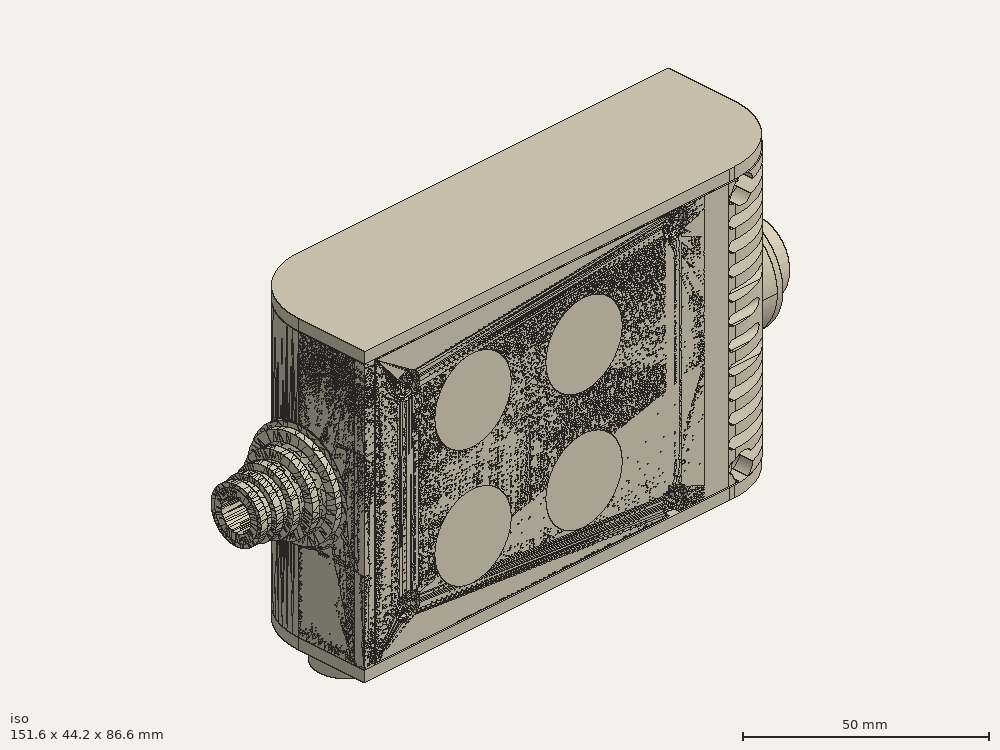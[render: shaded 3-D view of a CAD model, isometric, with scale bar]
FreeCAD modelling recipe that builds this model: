
FCSTD DOCUMENT  (FreeCAD 0.19R0.19.2)
Label: enclosure_205FCStd
License: All rights reserved
LicenseURL: http://en.wikipedia.org/wiki/All_rights_reserved
objects: Part::Revolution×152, Part::MultiFuse×146, Part::Feature×146, Sketcher::SketchObject×83, Part::Cut×70, Part::Cylinder×70, Part::Extrusion×68, Part::Fillet×58, Part::Box×36, App::MeasureDistance×4, Image::ImagePlane×1, PartDesign::Body×1, Part::FeaturePython×1
note: 831 computed .brp shape members not serialized (recipe doc carries the construction recipe); baked Part::Feature solids carry a one-line shape summary decoded from their .brp

FEATURE [Sketcher::SketchObject] Sketch  label="topSketch"
  FullyConstrained = true
  sketch-geometry (20):
    g0: LineSegment StartX=5.21097e-06 StartY=3 StartZ=0 EndX=5.21097e-06 EndY=19 EndZ=0
    g1: ArcOfCircle CenterX=19 CenterY=19 CenterZ=0 NormalX=0 NormalY=0 NormalZ=1 AngleXU=0 Radius=19 StartAngle=1.5708 EndAngle=3.14159
    g2: ArcOfCircle CenterX=19 CenterY=19 CenterZ=0 NormalX=0 NormalY=0 NormalZ=1 AngleXU=0 Radius=16 StartAngle=1.5708 EndAngle=3.14159
    g3: LineSegment StartX=114 StartY=35 StartZ=0 EndX=19 EndY=35 EndZ=0
    g4: LineSegment StartX=5.21097e-06 StartY=3 StartZ=0 EndX=5.21097e-06 EndY=0 EndZ=0
    g5: LineSegment StartX=3 StartY=0 StartZ=0 EndX=5.21097e-06 EndY=0 EndZ=0
    g6: LineSegment StartX=3 StartY=19 StartZ=0 EndX=3 EndY=0 EndZ=0
    g7: LineSegment StartX=19 StartY=38 StartZ=0 EndX=124 EndY=38 EndZ=0
    g8: Circle CenterX=119 CenterY=35 CenterZ=0 NormalX=0 NormalY=0 NormalZ=1 AngleXU=0 Radius=1
    g9: Circle CenterX=121 CenterY=35 CenterZ=0 NormalX=0 NormalY=0 NormalZ=1 AngleXU=0 Radius=1
    g10: Circle CenterX=121 CenterY=33 CenterZ=0 NormalX=0 NormalY=0 NormalZ=1 AngleXU=0 Radius=1
    g11: BSplineCurve PolesCount=3 KnotsCount=2 Degree=2 IsPeriodic=0
    g12: GeomPoint X=119 Y=35 Z=0
    g13: GeomPoint X=121 Y=33 Z=0
    g14: LineSegment StartX=119 StartY=35 StartZ=0 EndX=114 EndY=35 EndZ=0
    g15: ArcOfCircle CenterX=105 CenterY=19 CenterZ=0 NormalX=0 NormalY=0 NormalZ=1 AngleXU=0 Radius=19 StartAngle=5.7297 EndAngle=6.28319
    g16: ArcOfCircle CenterX=105 CenterY=19 CenterZ=0 NormalX=0 NormalY=0 NormalZ=1 AngleXU=0 Radius=16 StartAngle=5.60905 EndAngle=6.28319
    g17: LineSegment StartX=121 StartY=33 StartZ=0 EndX=121 EndY=19 EndZ=0
    g18: LineSegment StartX=124 StartY=38 StartZ=0 EndX=124 EndY=19 EndZ=0
    g19: LineSegment StartX=117.5 StartY=9.01251 StartZ=0 EndX=121.163 EndY=9.0125 EndZ=0
  constraints (46):
    c: Vertical(g0)
    c: Block(g0)
    c: Coincident(g1,g0)
    c: Block(g1)
    c: Coincident(g2,g1)
    c: Block(g2)
    c: Coincident(g3,g2)
    c: Horizontal(g3)
    c: Tangent(g3,g2)
    c: Coincident(g4,g0)
    c: Distance(g4) = 3
    c: Vertical(g4)
    c: Coincident(g5,g4)
    c: Horizontal(g5)
    c: Coincident(g6,g2)
    c: Coincident(g6,g5)
    c: Vertical(g6)
    c: Horizontal(g7)
    c: Distance(g7) = 105
    c: Coincident(g7,g1)
    c: Block(g3)
    c: Weight(g8) = 1
    c: Equal(g8,g9)
    c: Equal(g8,g10)
    c: InternalAlignment(g8,g11)
    c: InternalAlignment(g9,g11)
    c: InternalAlignment(g10,g11)
    c: InternalAlignment(g12,g11)
    c: InternalAlignment(g13,g11)
    c: Block(g11)
    c: Coincident(g14,g11)
    c: Coincident(g14,g3)
    c: Horizontal(g14)
    c: Block(g15)
    c: Coincident(g16,g15)
    c: Block(g16)
    c: Coincident(g17,g11)
    c: Coincident(g17,g16)
    c: Vertical(g17)
    c: Distance(g17) = 14
    c: Coincident(g18,g7)
    c: Coincident(g18,g15)
    c: Vertical(g18)
    c: Distance(g18) = 19
    c: Coincident(g19,g16)
    c: Coincident(g19,g15)
FEATURE [Sketcher::SketchObject] Sketch001  label="bottomSketch"
  FullyConstrained = true
  sketch-geometry (32):
    g0: LineSegment StartX=3.3 StartY=-6.03275e-07 StartZ=0 EndX=98 EndY=-6.03275e-07 EndZ=0
    g1: ArcOfCircle CenterX=98 CenterY=19 CenterZ=0 NormalX=0 NormalY=0 NormalZ=1 AngleXU=0 Radius=19 StartAngle=4.71239 EndAngle=5.71103
    g2: LineSegment StartX=6.3 StartY=8 StartZ=0 EndX=3.3 EndY=8 EndZ=0
    g3: LineSegment StartX=3.3 StartY=8 StartZ=0 EndX=3.3 EndY=-6.03275e-07 EndZ=0
    g4: ArcOfCircle CenterX=8.3 CenterY=5 CenterZ=0 NormalX=0 NormalY=0 NormalZ=1 AngleXU=0 Radius=2 StartAngle=3.14159 EndAngle=4.71239
    g5: LineSegment StartX=6.3 StartY=8 StartZ=0 EndX=6.3 EndY=5 EndZ=0
    g6: ArcOfCircle CenterX=98 CenterY=19 CenterZ=0 NormalX=0 NormalY=0 NormalZ=1 AngleXU=0 Radius=12.7 StartAngle=4.71239 EndAngle=6.28319
    g7: LineSegment StartX=94.7 StartY=3 StartZ=0 EndX=8.3 EndY=3 EndZ=0
    g8-g12: Circle x5 (B-spline internal-alignment scaffolding for g13; pole/knot coordinates omitted)
    g13: BSplineCurve PolesCount=5 KnotsCount=3 Degree=3 IsPeriodic=0
    g14: GeomPoint X=98 Y=6.3 Z=0
    g15: GeomPoint X=96.3938 Y=4.71946 Z=0
    g16: GeomPoint X=94.7 Y=3 Z=0
    g17-g23: Circle x7 (B-spline internal-alignment scaffolding for g24; pole/knot coordinates omitted)
    g24: BSplineCurve PolesCount=7 KnotsCount=5 Degree=3 IsPeriodic=0
    g25-g29: GeomPoint x5 (B-spline internal-alignment scaffolding for g24; pole/knot coordinates omitted)
    g30: ArcOfCircle CenterX=98 CenterY=19 CenterZ=0 NormalX=0 NormalY=0 NormalZ=1 AngleXU=0 Radius=15.7 StartAngle=5.81226 EndAngle=6.28319
    g31: LineSegment StartX=110.7 StartY=19 StartZ=0 EndX=113.7 EndY=19 EndZ=0
  constraints (41):
    c: Horizontal(g0)
    c: Coincident(g1,g0)
    c: Block(g1)
    c: Horizontal(g2)
    c: Distance(g2) = 3
    c: Coincident(g3,g2)
    c: Vertical(g3)
    c: Coincident(g3,g0)
    c: Block(g4)
    c: Block(g2)
    c: Coincident(g5,g2)
    c: Coincident(g5,g4)
    c: Vertical(g5)
    c: Coincident(g6,g1)
    c: Block(g6)
    c: Coincident(g7,g4)
    c: Horizontal(g7)
    c: Block(g0)
    c: Block(g7)
    c: Block(g3)
    c: Coincident(g13,g6)
    c: Weight(g8) = 1
    c: Equal(g8, g9-g12) x4
    c: Coincident(g13,g7)
    c: InternalAlignment(g8-g12 -> g13) x5
    c: InternalAlignment(g14,g13)
    c: InternalAlignment(g15,g13)
    c: InternalAlignment(g16,g13)
    c: Block(g13)
    c: Weight(g17) = 1
    c: Equal(g17, g18-g23) x6
    c: Coincident(g24,g1)
    c: InternalAlignment(g17-g23 -> g24) x7
    c: InternalAlignment(g25-g29 -> g24) x5
    c: Block(g24)
    c: Coincident(g30,g24)
    c: Coincident(g31,g6)
    c: Coincident(g31,g30)
    c: Horizontal(g31)
    c: Block(g31)
    c: Block(g30)
FEATURE [Part::Extrusion] Extrude  label="top"
  Base = -> Sketch
  Dir = (0,0,1)
  DirMode = 2
  FaceMakerClass = Part::FaceMakerBullseye
  LengthFwd = 72
  LengthRev = 0
  Solid = true
  Symmetric = false
FEATURE [Part::Extrusion] Extrude001  label="bottom"
  Base = -> Sketch001
  Dir = (0,0,1)
  DirMode = 2
  FaceMakerClass = Part::FaceMakerBullseye
  LengthFwd = 71.4
  LengthRev = 0
  Placement = pos=(0,0,0.3) rot=(0,0,1;0rad)
  Solid = true
  Symmetric = false
FEATURE [Sketcher::SketchObject] Sketch002  label="topSketch001"
  FullyConstrained = true
  sketch-geometry (8):
    g0: ArcOfCircle CenterX=19 CenterY=19.0975 CenterZ=0 NormalX=0 NormalY=0 NormalZ=1 AngleXU=0 Radius=18.9025 StartAngle=1.5708 EndAngle=3.14674
    g1: LineSegment StartX=0.0977805 StartY=19.0003 StartZ=0 EndX=0.0977805 EndY=0.000251602 EndZ=0
    g2: LineSegment StartX=19 StartY=38 StartZ=0 EndX=124 EndY=38 EndZ=0
    g3: LineSegment StartX=0.0977805 StartY=0.000251602 StartZ=0 EndX=105.098 EndY=0.000251602 EndZ=0
    g4: LineSegment StartX=124 StartY=38 StartZ=0 EndX=125.616 EndY=38 EndZ=0
    g5: LineSegment StartX=105.098 StartY=0.000251602 StartZ=0 EndX=106.713 EndY=0.000251602 EndZ=0
    g6: ArcOfCircle CenterX=106.616 CenterY=19 CenterZ=0 NormalX=0 NormalY=0 NormalZ=1 AngleXU=0 Radius=19 StartAngle=4.71754 EndAngle=6.28319
    g7: LineSegment StartX=125.616 StartY=38 StartZ=0 EndX=125.616 EndY=19 EndZ=0
  constraints (21):
    c: Block(g0)
    c: Coincident(g1,g0)
    c: Vertical(g1)
    c: Horizontal(g2)
    c: Distance(g2) = 105
    c: Coincident(g2,g0)
    c: Distance(g1) = 19
    c: Coincident(g3,g1)
    c: Horizontal(g3)
    c: Distance(g3) = 105
    c: Coincident(g4,g2)
    c: Horizontal(g4)
    c: Distance(g4) = 1.61553
    c: Horizontal(g5)
    c: Equal(g4,g5) = 1.61553
    c: Coincident(g5,g3)
    c: Block(g6)
    c: Coincident(g6,g5)
    c: Coincident(g7,g4)
    c: Coincident(g7,g6)
    c: Vertical(g7)
FEATURE [Part::Extrusion] Extrude002  label="sideA"
  Base = -> Sketch002
  Dir = (0,0,1)
  DirMode = 2
  FaceMakerClass = Part::FaceMakerBullseye
  LengthFwd = 3
  LengthRev = 0
  Placement = pos=(0,0,-3) rot=(0,0,1;0rad)
  Solid = true
  Symmetric = false
FEATURE [Sketcher::SketchObject] Sketch003  label="topSketch002"
  FullyConstrained = true
  sketch-geometry (6):
    g0: LineSegment StartX=19 StartY=38 StartZ=0 EndX=117 EndY=38 EndZ=0
    g1: ArcOfCircle CenterX=19 CenterY=19 CenterZ=0 NormalX=0 NormalY=0 NormalZ=1 AngleXU=0 Radius=19 StartAngle=1.5708 EndAngle=3.14159
    g2: LineSegment StartX=117 StartY=38 StartZ=0 EndX=117 EndY=19 EndZ=0
    g3: LineSegment StartX=98 StartY=1.0161e-12 StartZ=0 EndX=5.22862e-06 EndY=1.0161e-12 EndZ=0
    g4: LineSegment StartX=5.22862e-06 StartY=19 StartZ=0 EndX=5.22862e-06 EndY=1.0161e-12 EndZ=0
    g5: ArcOfCircle CenterX=98 CenterY=19 CenterZ=0 NormalX=0 NormalY=0 NormalZ=1 AngleXU=0 Radius=19 StartAngle=4.71239 EndAngle=6.28319
  constraints (16):
    c: Horizontal(g0)
    c: Distance(g0) = 98
    c: Coincident(g1,g0)
    c: Block(g1)
    c: Coincident(g2,g0)
    c: Vertical(g2)
    c: Distance(g2) = 19
    c: Horizontal(g3)
    c: Coincident(g4,g1)
    c: Vertical(g4)
    c: Coincident(g3,g4)
    c: Block(g3)
    c: Coincident(g5,g2)
    c: Coincident(g5,g3)
    c: Block(g0)
    c: Block(g5)
FEATURE [Sketcher::SketchObject] Sketch004
  FullyConstrained = true
  MapMode = 3
  Placement = pos=(0,0,0) rot=(1,0,0;1.5708rad)
  Support = -> [Extrude]
  sketch-geometry (8):
    g0: Circle CenterX=80.351 CenterY=-67.6202 CenterZ=0 NormalX=0 NormalY=0 NormalZ=1 AngleXU=0 Radius=2
    g1: Circle CenterX=80.351 CenterY=-67.6202 CenterZ=0 NormalX=0 NormalY=0 NormalZ=1 AngleXU=0 Radius=3
    g2: Circle CenterX=80.351 CenterY=-4.92017 CenterZ=0 NormalX=0 NormalY=0 NormalZ=1 AngleXU=0 Radius=2
    g3: Circle CenterX=80.351 CenterY=-4.92017 CenterZ=0 NormalX=0 NormalY=0 NormalZ=1 AngleXU=0 Radius=3
    g4: Circle CenterX=23.851 CenterY=-4.92017 CenterZ=0 NormalX=0 NormalY=0 NormalZ=1 AngleXU=0 Radius=2
    g5: Circle CenterX=23.851 CenterY=-4.92017 CenterZ=0 NormalX=0 NormalY=0 NormalZ=1 AngleXU=0 Radius=3
    g6: Circle CenterX=23.851 CenterY=-67.6202 CenterZ=0 NormalX=0 NormalY=0 NormalZ=1 AngleXU=0 Radius=2
    g7: Circle CenterX=23.851 CenterY=-67.6202 CenterZ=0 NormalX=0 NormalY=0 NormalZ=1 AngleXU=0 Radius=3
  constraints (8):
    c: Block(g3)
    c: Block(g2)
    c: Block(g1)
    c: Block(g0)
    c: Block(g6)
    c: Block(g7)
    c: Block(g4)
    c: Block(g5)
FEATURE [Part::Extrusion] Extrude004
  Base = -> Sketch004
  Dir = (0,-1,2e-16)
  DirMode = 2
  FaceMakerClass = Part::FaceMakerBullseye
  LengthFwd = 6
  LengthRev = 0
  Placement = pos=(0,9,0) rot=(0,0,1;0rad)
  Solid = true
  Symmetric = false
FEATURE [Sketcher::SketchObject] Sketch005
  FullyConstrained = true
  MapMode = 3
  Placement = pos=(0,0,0) rot=(1,0,0;1.5708rad)
  Support = -> [Extrude]
  sketch-geometry (8):
    g0: Circle CenterX=80.351 CenterY=-67.6202 CenterZ=0 NormalX=0 NormalY=0 NormalZ=1 AngleXU=0 Radius=3
    g1: Circle CenterX=80.351 CenterY=-4.92017 CenterZ=0 NormalX=0 NormalY=0 NormalZ=1 AngleXU=0 Radius=3
    g2: Circle CenterX=23.851 CenterY=-4.92017 CenterZ=0 NormalX=0 NormalY=0 NormalZ=1 AngleXU=0 Radius=3
    g3: Circle CenterX=23.851 CenterY=-67.6202 CenterZ=0 NormalX=0 NormalY=0 NormalZ=1 AngleXU=0 Radius=3
    g4: Circle CenterX=23.851 CenterY=-67.6202 CenterZ=0 NormalX=0 NormalY=0 NormalZ=1 AngleXU=0 Radius=5
    g5: Circle CenterX=80.351 CenterY=-67.6202 CenterZ=0 NormalX=0 NormalY=0 NormalZ=1 AngleXU=0 Radius=5
    g6: Circle CenterX=23.851 CenterY=-4.92017 CenterZ=0 NormalX=0 NormalY=0 NormalZ=1 AngleXU=0 Radius=5
    g7: Circle CenterX=80.351 CenterY=-4.92017 CenterZ=0 NormalX=0 NormalY=0 NormalZ=1 AngleXU=0 Radius=5
  constraints (8):
    c: Block(g1)
    c: Block(g0)
    c: Block(g3)
    c: Block(g2)
    c: Block(g5)
    c: Block(g4)
    c: Block(g6)
    c: Block(g7)
FEATURE [Part::Extrusion] Extrude005
  Base = -> Sketch005
  Dir = (0,-1,2e-16)
  DirMode = 2
  FaceMakerClass = Part::FaceMakerBullseye
  LengthFwd = 2
  LengthRev = 0
  Solid = true
  Symmetric = false
FEATURE [Sketcher::SketchObject] Sketch006
  FullyConstrained = true
  MapMode = 3
  Placement = pos=(0,0,0) rot=(1,0,0;1.5708rad)
  sketch-geometry (8):
    g0: Circle CenterX=80.351 CenterY=-67.6202 CenterZ=0 NormalX=0 NormalY=0 NormalZ=1 AngleXU=0 Radius=3
    g1: Circle CenterX=80.351 CenterY=-4.92017 CenterZ=0 NormalX=0 NormalY=0 NormalZ=1 AngleXU=0 Radius=3
    g2: Circle CenterX=23.851 CenterY=-4.92017 CenterZ=0 NormalX=0 NormalY=0 NormalZ=1 AngleXU=0 Radius=3
    g3: Circle CenterX=23.851 CenterY=-67.6202 CenterZ=0 NormalX=0 NormalY=0 NormalZ=1 AngleXU=0 Radius=3
    g4: Circle CenterX=23.851 CenterY=-67.6202 CenterZ=0 NormalX=0 NormalY=0 NormalZ=1 AngleXU=0 Radius=5
    g5: Circle CenterX=80.351 CenterY=-67.6202 CenterZ=0 NormalX=0 NormalY=0 NormalZ=1 AngleXU=0 Radius=5
    g6: Circle CenterX=23.851 CenterY=-4.92017 CenterZ=0 NormalX=0 NormalY=0 NormalZ=1 AngleXU=0 Radius=5
    g7: Circle CenterX=80.351 CenterY=-4.92017 CenterZ=0 NormalX=0 NormalY=0 NormalZ=1 AngleXU=0 Radius=5
  constraints (8):
    c: Block(g1)
    c: Block(g0)
    c: Block(g3)
    c: Block(g2)
    c: Block(g5)
    c: Block(g4)
    c: Block(g6)
    c: Block(g7)
FEATURE [Part::Extrusion] Extrude007
  Base = -> Sketch006
  Dir = (0,-1,2e-16)
  DirMode = 2
  FaceMakerClass = Part::FaceMakerBullseye
  LengthFwd = 2
  LengthRev = 0
  Solid = true
  Symmetric = false
FEATURE [Part::Fillet] Fillet
  Base = -> Extrude007
  Edges = 4 edges r=1.99: [Edge6,Edge12,Edge18,Edge24]
FEATURE [Part::Cut] Cut
  Base = -> Extrude005
  Placement = pos=(0,5,0) rot=(0,0,1;0rad)
  Tool = -> Fillet
FEATURE [Part::MultiFuse] Fusion  label="pCBScrews"
  Placement = pos=(-2.5,0,72.3) rot=(0,0,1;0rad)
  Shapes = -> [Extrude004,Cut]
FEATURE [App::MeasureDistance] Distance  label="Distance: 0.69 mm"
  Distance = 0.685967
  P1 = (24.0138,2.9647,0.3)
  P2 = (23.8901,3,-0.373787)
FEATURE [App::MeasureDistance] Distance001  label="Distance: 0.53 mm"
  Distance = 0.533607
  P1 = (80.2939,3,72.2334)
  P2 = (80.281,2.99661,71.7)
FEATURE [Part::Fillet] Fillet001
  Base = -> Extrude001
  Edges = 1 edges r=2.4: [Edge17]
FEATURE [Part::Fillet] Fillet002  label="bottom001"
  Base = -> Fillet001
  Edges = 1 edges r=2.4: [Edge36]
FEATURE [Part::Fillet] Fillet003  label="top001"
  Base = -> Extrude
  Edges = 1 edges r=2: [Edge1]
FEATURE [Sketcher::SketchObject] Sketch007
  FullyConstrained = true
  sketch-geometry (16):
    g0: LineSegment StartX=4 StartY=0 StartZ=0 EndX=4 EndY=2.4 EndZ=0
    g1: LineSegment StartX=4 StartY=2.4 StartZ=0 EndX=7 EndY=2.4 EndZ=0
    g2: LineSegment StartX=4 StartY=0 StartZ=0 EndX=5.7 EndY=0 EndZ=0
    g3: LineSegment StartX=5.7 StartY=0 StartZ=0 EndX=5.7 EndY=-5.6 EndZ=0
    g4-g8: Circle x5 (B-spline internal-alignment scaffolding for g9; pole/knot coordinates omitted)
    g9: BSplineCurve PolesCount=5 KnotsCount=3 Degree=3 IsPeriodic=0
    g10: GeomPoint X=7 Y=2.4 Z=0
    g11: GeomPoint X=10.4582 Y=-1.55472 Z=0
    g12: GeomPoint X=14 Y=-5.6 Z=0
    g13: LineSegment StartX=14 StartY=-5.6 StartZ=0 EndX=14 EndY=-14.1 EndZ=0
    g14: LineSegment StartX=14 StartY=-14.1 StartZ=0 EndX=6.5 EndY=-14.1 EndZ=0
    g15: LineSegment StartX=5.7 StartY=-5.6 StartZ=0 EndX=6.5 EndY=-14.1 EndZ=0
  constraints (28):
    c: Distance(g0) = 2.4
    c: Vertical(g0)
    c: Block(g0)
    c: Coincident(g1,g0)
    c: Horizontal(g1)
    c: Distance(g1) = 3
    c: Coincident(g2,g0)
    c: Horizontal(g2)
    c: Distance(g2) = 1.7
    c: Coincident(g3,g2)
    c: Vertical(g3)
    c: Distance(g3) = 5.6
    c: Coincident(g9,g1)
    c: Weight(g4) = 1
    c: Equal(g4, g5-g8) x4
    c: InternalAlignment(g4-g8 -> g9) x5
    c: InternalAlignment(g10,g9)
    c: InternalAlignment(g11,g9)
    c: InternalAlignment(g12,g9)
    c: Block(g9)
    c: Coincident(g13,g9)
    c: Vertical(g13)
    c: Distance(g13) = 8.5
    c: Coincident(g14,g13)
    c: Horizontal(g14)
    c: Distance(g14) = 7.5
    c: Coincident(g15,g3)
    c: Coincident(g15,g14)
FEATURE [Part::Feature] Face
  shape: bbox 10 x 16.5 x 2e-07 mm, 1 faces, 0 solids (baked)
FEATURE [Part::Revolution] Revolve  label="plugHousing"
  Angle = 360
  Axis = (0,1,0)
  Base = (0,0,0)
  FaceMakerClass = Part::FaceMakerBullseye
  Placement = pos=(0,0,36.15) rot=(0,0,1;0rad)
  Solid = false
  Source = -> Face
  Symmetric = false
FEATURE [Part::Feature] Face001
  shape: bbox 10 x 16.5 x 2e-07 mm, 1 faces, 0 solids (baked)
FEATURE [Part::Revolution] Revolve001  label="plugHousing001"
  Angle = 360
  Axis = (0,1,0)
  Base = (0,0,0)
  FaceMakerClass = Part::FaceMakerBullseye
  Placement = pos=(0,0,36.15) rot=(0,0,1;0rad)
  Solid = false
  Source = -> Face001
  Symmetric = false
FEATURE [Part::MultiFuse] Fusion001  label="plugHousing002"
  Placement = pos=(0,0,0) rot=(0,0,1;1.5708rad)
  Shapes = -> [Revolve001,Revolve]
FEATURE [Part::Feature] Face002
  shape: bbox 10 x 16.5 x 2e-07 mm, 1 faces, 0 solids (baked)
FEATURE [Part::Revolution] Revolve003  label="plugHousing005"
  Angle = 360
  Axis = (0,1,0)
  Base = (0,0,0)
  FaceMakerClass = Part::FaceMakerBullseye
  Placement = pos=(0,0,36.15) rot=(0,0,1;0rad)
  Solid = false
  Source = -> Face002
  Symmetric = false
FEATURE [Part::Feature] Face003
  shape: bbox 10 x 16.5 x 2e-07 mm, 1 faces, 0 solids (baked)
FEATURE [Part::Revolution] Revolve002  label="plugHousing003"
  Angle = 360
  Axis = (0,1,0)
  Base = (0,0,0)
  FaceMakerClass = Part::FaceMakerBullseye
  Placement = pos=(0,0,36.15) rot=(0,0,1;0rad)
  Solid = false
  Source = -> Face003
  Symmetric = false
FEATURE [Part::MultiFuse] Fusion002  label="plugHousing004"
  Placement = pos=(0,0,0) rot=(0,0,1;1.5708rad)
  Shapes = -> [Revolve002,Revolve003]
FEATURE [Part::MultiFuse] Fusion003  label="plugHousing006"
  Placement = pos=(0,19,0) rot=(0,0,1;3.14159rad)
  Shapes = -> [Fusion002,Fusion001]
FEATURE [Part::Feature] Face004
  shape: bbox 10 x 16.5 x 2e-07 mm, 1 faces, 0 solids (baked)
FEATURE [Part::Revolution] Revolve006  label="plugHousing010"
  Angle = 360
  Axis = (0,1,0)
  Base = (0,0,0)
  FaceMakerClass = Part::FaceMakerBullseye
  Placement = pos=(0,0,36.15) rot=(0,0,1;0rad)
  Solid = false
  Source = -> Face004
  Symmetric = false
FEATURE [Part::Feature] Face005
  shape: bbox 10 x 16.5 x 2e-07 mm, 1 faces, 0 solids (baked)
FEATURE [Part::Revolution] Revolve007  label="plugHousing011"
  Angle = 360
  Axis = (0,1,0)
  Base = (0,0,0)
  FaceMakerClass = Part::FaceMakerBullseye
  Placement = pos=(0,0,36.15) rot=(0,0,1;0rad)
  Solid = false
  Source = -> Face005
  Symmetric = false
FEATURE [Part::Feature] Face006
  shape: bbox 10 x 16.5 x 2e-07 mm, 1 faces, 0 solids (baked)
FEATURE [Part::Revolution] Revolve004  label="plugHousing007"
  Angle = 360
  Axis = (0,1,0)
  Base = (0,0,0)
  FaceMakerClass = Part::FaceMakerBullseye
  Placement = pos=(0,0,36.15) rot=(0,0,1;0rad)
  Solid = false
  Source = -> Face006
  Symmetric = false
FEATURE [Part::MultiFuse] Fusion004  label="plugHousing009"
  Placement = pos=(0,0,0) rot=(0,0,1;1.5708rad)
  Shapes = -> [Revolve004,Revolve007]
FEATURE [Part::Feature] Face007
  shape: bbox 10 x 16.5 x 2e-07 mm, 1 faces, 0 solids (baked)
FEATURE [Part::Revolution] Revolve005  label="plugHousing008"
  Angle = 360
  Axis = (0,1,0)
  Base = (0,0,0)
  FaceMakerClass = Part::FaceMakerBullseye
  Placement = pos=(0,0,36.15) rot=(0,0,1;0rad)
  Solid = false
  Source = -> Face007
  Symmetric = false
FEATURE [Part::MultiFuse] Fusion005  label="plugHousing012"
  Placement = pos=(0,0,0) rot=(0,0,1;1.5708rad)
  Shapes = -> [Revolve006,Revolve005]
FEATURE [Part::MultiFuse] Fusion006  label="plugHousing013"
  Placement = pos=(0,19,0) rot=(0,0,1;3.14159rad)
  Shapes = -> [Fusion005,Fusion004]
FEATURE [Part::MultiFuse] Fusion007  label="plugHousing014"
  Placement = pos=(122.621,0,-0.15) rot=(0,0,1;0rad)
  Shapes = -> [Fusion003,Fusion006]
FEATURE [Part::Cylinder] Cylinder002
  Angle = 360
  AttacherType = Attacher::AttachEngine3D
  Height = 20
  Placement = pos=(0,0,36.15) rot=(0,0,1;0rad)
  Radius = 4
FEATURE [Part::Cylinder] Cylinder003
  Angle = 360
  AttacherType = Attacher::AttachEngine3D
  Height = 10
  Placement = pos=(0,0,36.15) rot=(0,0,1;0rad)
  Radius = 4
FEATURE [Part::MultiFuse] Fusion009  label="removeToCreateHoleForPlugHousing"
  Placement = pos=(70,19,36.15) rot=(0,1,0;1.5708rad)
  Shapes = -> [Cylinder002,Cylinder003]
FEATURE [Part::Cylinder] Cylinder004
  Angle = 360
  AttacherType = Attacher::AttachEngine3D
  Height = 20
  Placement = pos=(0,0,36.15) rot=(0,0,1;0rad)
  Radius = 4
FEATURE [Part::Cylinder] Cylinder005
  Angle = 360
  AttacherType = Attacher::AttachEngine3D
  Height = 10
  Placement = pos=(0,0,36.15) rot=(0,0,1;0rad)
  Radius = 4
FEATURE [Part::MultiFuse] Fusion010  label="removeToCreateHoleForPlugHousing001"
  Placement = pos=(70,19,36.15) rot=(0,1,0;1.5708rad)
  Shapes = -> [Cylinder004,Cylinder005]
FEATURE [Part::Cut] Cut001
  Base = -> Fillet003
  Tool = -> Fusion010
FEATURE [Part::Cut] Cut002  label="Bottom"
  Base = -> Fillet002
  Tool = -> Fusion009
FEATURE [Part::Feature] Face008
  shape: bbox 10 x 16.5 x 2e-07 mm, 1 faces, 0 solids (baked)
FEATURE [Part::Revolution] Revolve011  label="plugHousing021"
  Angle = 360
  Axis = (0,1,0)
  Base = (0,0,0)
  FaceMakerClass = Part::FaceMakerBullseye
  Placement = pos=(0,0,36.15) rot=(0,0,1;0rad)
  Solid = false
  Source = -> Face008
  Symmetric = false
FEATURE [Part::Feature] Face009
  shape: bbox 10 x 16.5 x 2e-07 mm, 1 faces, 0 solids (baked)
FEATURE [Part::Revolution] Revolve012  label="plugHousing022"
  Angle = 360
  Axis = (0,1,0)
  Base = (0,0,0)
  FaceMakerClass = Part::FaceMakerBullseye
  Placement = pos=(0,0,36.15) rot=(0,0,1;0rad)
  Solid = false
  Source = -> Face009
  Symmetric = false
FEATURE [Part::Feature] Face010 .. Face013  x4 (patterned run collapsed; names and placements below)
  shape: bbox 10 x 16.5 x 2e-07 mm, 1 faces, 0 solids (baked)
FEATURE [Part::Revolution] Revolve015  label="plugHousing027"
  Angle = 360
  Axis = (0,1,0)
  Base = (0,0,0)
  FaceMakerClass = Part::FaceMakerBullseye
  Placement = pos=(0,0,36.15) rot=(0,0,1;0rad)
  Solid = false
  Source = -> Face013
  Symmetric = false
FEATURE [Part::Feature] Face014
  shape: bbox 10 x 16.5 x 2e-07 mm, 1 faces, 0 solids (baked)
FEATURE [Part::Feature] Face015
  shape: bbox 10 x 16.5 x 2e-07 mm, 1 faces, 0 solids (baked)
FEATURE [Part::Feature] Face016
  shape: bbox 10 x 16.5 x 2e-07 mm, 1 faces, 0 solids (baked)
FEATURE [Part::Revolution] Revolve019  label="plugHousing033"
  Angle = 360
  Axis = (0,1,0)
  Base = (0,0,0)
  FaceMakerClass = Part::FaceMakerBullseye
  Placement = pos=(0,0,36.15) rot=(0,0,1;0rad)
  Solid = false
  Source = -> Face016
  Symmetric = false
FEATURE [Part::Feature] Face017
  shape: bbox 10 x 16.5 x 2e-07 mm, 1 faces, 0 solids (baked)
FEATURE [Part::Revolution] Revolve020  label="plugHousing034"
  Angle = 360
  Axis = (0,1,0)
  Base = (0,0,0)
  FaceMakerClass = Part::FaceMakerBullseye
  Placement = pos=(0,0,36.15) rot=(0,0,1;0rad)
  Solid = false
  Source = -> Face017
  Symmetric = false
FEATURE [Part::Feature] Face018
  shape: bbox 10 x 16.5 x 2e-07 mm, 1 faces, 0 solids (baked)
FEATURE [Part::Revolution] Revolve016  label="plugHousing030"
  Angle = 360
  Axis = (0,1,0)
  Base = (0,0,0)
  FaceMakerClass = Part::FaceMakerBullseye
  Placement = pos=(0,0,36.15) rot=(0,0,1;0rad)
  Solid = false
  Source = -> Face018
  Symmetric = false
FEATURE [Part::MultiFuse] Fusion020  label="plugHousing038"
  Placement = pos=(0,0,0) rot=(0,0,1;1.5708rad)
  Shapes = -> [Revolve016,Revolve020]
FEATURE [Part::Feature] Face019
  shape: bbox 10 x 16.5 x 2e-07 mm, 1 faces, 0 solids (baked)
FEATURE [Part::Feature] Face020
  shape: bbox 10 x 16.5 x 2e-07 mm, 1 faces, 0 solids (baked)
FEATURE [Part::Revolution] Revolve017  label="plugHousing031"
  Angle = 360
  Axis = (0,1,0)
  Base = (0,0,0)
  FaceMakerClass = Part::FaceMakerBullseye
  Placement = pos=(0,0,36.15) rot=(0,0,1;0rad)
  Solid = false
  Source = -> Face020
  Symmetric = false
FEATURE [Part::MultiFuse] Fusion021  label="plugHousing039"
  Placement = pos=(0,0,0) rot=(0,0,1;1.5708rad)
  Shapes = -> [Revolve019,Revolve017]
FEATURE [Part::MultiFuse] Fusion023  label="plugHousing041"
  Placement = pos=(0,19,0) rot=(0,0,1;3.14159rad)
  Shapes = -> [Fusion021,Fusion020]
FEATURE [Part::Revolution] Revolve022  label="plugHousing043"
  Angle = 360
  Axis = (0,1,0)
  Base = (0,0,0)
  FaceMakerClass = Part::FaceMakerBullseye
  Placement = pos=(0,0,36.15) rot=(0,0,1;0rad)
  Solid = false
  Source = -> Face019
  Symmetric = false
FEATURE [Part::Feature] Face021
  shape: bbox 10 x 16.5 x 2e-07 mm, 1 faces, 0 solids (baked)
FEATURE [Part::Revolution] Revolve023  label="plugHousing044"
  Angle = 360
  Axis = (0,1,0)
  Base = (0,0,0)
  FaceMakerClass = Part::FaceMakerBullseye
  Placement = pos=(0,0,36.15) rot=(0,0,1;0rad)
  Solid = false
  Source = -> Face021
  Symmetric = false
FEATURE [Part::Feature] Face022
  shape: bbox 10 x 16.5 x 2e-07 mm, 1 faces, 0 solids (baked)
FEATURE [Part::Revolution] Revolve018  label="plugHousing032"
  Angle = 360
  Axis = (0,1,0)
  Base = (0,0,0)
  FaceMakerClass = Part::FaceMakerBullseye
  Placement = pos=(0,0,36.15) rot=(0,0,1;0rad)
  Solid = false
  Source = -> Face022
  Symmetric = false
FEATURE [Part::MultiFuse] Fusion022  label="plugHousing040"
  Placement = pos=(0,0,0) rot=(0,0,1;1.5708rad)
  Shapes = -> [Revolve018,Revolve023]
FEATURE [Part::Feature] Face023
  shape: bbox 10 x 16.5 x 2e-07 mm, 1 faces, 0 solids (baked)
FEATURE [Part::Revolution] Revolve021  label="plugHousing035"
  Angle = 360
  Axis = (0,1,0)
  Base = (0,0,0)
  FaceMakerClass = Part::FaceMakerBullseye
  Placement = pos=(0,0,36.15) rot=(0,0,1;0rad)
  Solid = false
  Source = -> Face023
  Symmetric = false
FEATURE [Part::MultiFuse] Fusion018  label="plugHousing036"
  Placement = pos=(0,0,0) rot=(0,0,1;1.5708rad)
  Shapes = -> [Revolve022,Revolve021]
FEATURE [Part::MultiFuse] Fusion019  label="plugHousing037"
  Placement = pos=(0,19,0) rot=(0,0,1;3.14159rad)
  Shapes = -> [Fusion018,Fusion022]
FEATURE [Part::MultiFuse] Fusion024  label="plugHousing042"
  Placement = pos=(122.621,0,-0.15) rot=(0,0,1;0rad)
  Shapes = -> [Fusion023,Fusion019]
FEATURE [Part::Cylinder] Cylinder006
  Angle = 360
  AttacherType = Attacher::AttachEngine3D
  Height = 20
  Placement = pos=(0,0,36.15) rot=(0,0,1;0rad)
  Radius = 14.3
FEATURE [Part::Cylinder] Cylinder007
  Angle = 360
  AttacherType = Attacher::AttachEngine3D
  Height = 10
  Placement = pos=(0,0,36.15) rot=(0,0,1;0rad)
  Radius = 4
FEATURE [Part::MultiFuse] Fusion026  label="removeToCreteHoleForPlugHousing"
  Placement = pos=(70,19,36) rot=(0,1,0;1.5708rad)
  Shapes = -> [Cylinder006,Cylinder007]
FEATURE [Part::Box] Box001  label="Cube001"
  AttacherType = Attacher::AttachEngine3D
  Height = 28
  Length = 3
  Placement = pos=(110.7,19,22) rot=(0,0,1;0rad)
  Width = 15.7
FEATURE [Part::Cut] Cut003  label="top002"
  Base = -> Cut001
  Tool = -> Fusion007
FEATURE [Part::Revolution] Revolve008  label="plugHousing015"
  Angle = 360
  Axis = (0,1,0)
  Base = (0,0,0)
  FaceMakerClass = Part::FaceMakerBullseye
  Placement = pos=(0,0,36.15) rot=(0,0,1;0rad)
  Solid = false
  Source = -> Face010
  Symmetric = false
FEATURE [Part::MultiFuse] Fusion013  label="plugHousing020"
  Placement = pos=(0,0,0) rot=(0,0,1;1.5708rad)
  Shapes = -> [Revolve008,Revolve012]
FEATURE [Part::Cut] Cut004  label="top003"
  Base = -> Cut003
  Placement = pos=(1,0,0) rot=(0,0,1;0rad)
  Tool = -> Fusion026
FEATURE [Part::Cylinder] Cylinder008
  Angle = 360
  AttacherType = Attacher::AttachEngine3D
  Height = 20
  Placement = pos=(0,0,36.15) rot=(0,0,1;0rad)
  Radius = 10.3
FEATURE [Part::Cylinder] Cylinder009
  Angle = 360
  AttacherType = Attacher::AttachEngine3D
  Height = 10
  Placement = pos=(0,0,36.15) rot=(0,0,1;0rad)
  Radius = 4
FEATURE [Part::MultiFuse] Fusion027  label="removeToCreteHoleForPlugHousing001"
  Placement = pos=(70,19,36) rot=(0,1,0;1.5708rad)
  Shapes = -> [Cylinder008,Cylinder009]
FEATURE [Part::Cut] Cut005  label="plugHousingTab"
  Base = -> Box001
  Tool = -> Fusion027
FEATURE [Part::MultiFuse] Fusion028  label="plugHousing045"
  Shapes = -> [Fusion024,Cut005]
FEATURE [Part::Box] Box002  label="Cube002"
  AttacherType = Attacher::AttachEngine3D
  Height = 28.8
  Length = 3
  Placement = pos=(107.3,28,21.6) rot=(0,0,1;0rad)
  Width = 7
FEATURE [Part::Box] Box003  label="Cube003"
  AttacherType = Attacher::AttachEngine3D
  Height = 3
  Length = 6.4
  Placement = pos=(107.3,28,18.6) rot=(0,0,1;0rad)
  Width = 7
FEATURE [Part::Box] Box004  label="Cube004"
  AttacherType = Attacher::AttachEngine3D
  Height = 3
  Length = 6.4
  Placement = pos=(107.3,28,50.4) rot=(0,0,1;0rad)
  Width = 7
FEATURE [Part::MultiFuse] Fusion029  label="plugHousingBracketHolder"
  Shapes = -> [Box004,Box002,Box003]
FEATURE [Part::Cylinder] Cylinder010
  Angle = 360
  AttacherType = Attacher::AttachEngine3D
  Height = 20
  Placement = pos=(0,0,36.15) rot=(0,0,1;0rad)
  Radius = 14.3
FEATURE [Part::Cylinder] Cylinder011
  Angle = 360
  AttacherType = Attacher::AttachEngine3D
  Height = 10
  Placement = pos=(0,0,36.15) rot=(0,0,1;0rad)
  Radius = 4
FEATURE [Part::MultiFuse] Fusion030  label="removeToCreteHoleForPlugHousing002"
  Placement = pos=(70,19,36) rot=(0,1,0;1.5708rad)
  Shapes = -> [Cylinder010,Cylinder011]
FEATURE [Part::Cut] Cut006  label="plugHousingBracketHolder001"
  Base = -> Fusion029
  Tool = -> Fusion030
FEATURE [Part::Cylinder] Cylinder012
  Angle = 360
  AttacherType = Attacher::AttachEngine3D
  Height = 20
  Placement = pos=(0,0,36.15) rot=(0,0,1;0rad)
  Radius = 7
FEATURE [Part::Cylinder] Cylinder013
  Angle = 360
  AttacherType = Attacher::AttachEngine3D
  Height = 10
  Placement = pos=(0,0,36.15) rot=(0,0,1;0rad)
  Radius = 4
FEATURE [Part::MultiFuse] Fusion032  label="removeToCreteHoleForPlugHousing003"
  Placement = pos=(70,19,36) rot=(0,1,0;1.5708rad)
  Shapes = -> [Cylinder012,Cylinder013]
FEATURE [Part::Cut] Cut007  label="bottom002"
  Base = -> Cut002
  Tool = -> Fusion032
FEATURE [Sketcher::SketchObject] Sketch008
  FullyConstrained = true
  sketch-geometry (54):
    g0: LineSegment StartX=-4.2 StartY=0 StartZ=0 EndX=-6.2 EndY=0 EndZ=0
    g1: LineSegment StartX=-14 StartY=-18 StartZ=0 EndX=-14 EndY=-26.5 EndZ=0
    g2: LineSegment StartX=-4.2 StartY=0 StartZ=0 EndX=-4.2 EndY=-13.4877 EndZ=0
    g3: Circle CenterX=-4.2 CenterY=-13.4877 CenterZ=0 NormalX=0 NormalY=0 NormalZ=1 AngleXU=0 Radius=1
    g4: Circle CenterX=-4.2 CenterY=-26.5 CenterZ=0 NormalX=0 NormalY=0 NormalZ=1 AngleXU=0 Radius=1
    g5: Circle CenterX=-8.2 CenterY=-26.5 CenterZ=0 NormalX=0 NormalY=0 NormalZ=1 AngleXU=0 Radius=1
    g6: BSplineCurve PolesCount=3 KnotsCount=2 Degree=2 IsPeriodic=0
    g7: GeomPoint X=-4.2 Y=-13.4877 Z=0
    g8: GeomPoint X=-8.2 Y=-26.5 Z=0
    g9: LineSegment StartX=-14 StartY=-26.5 StartZ=0 EndX=-8.2 EndY=-26.5 EndZ=0
    g10: LineSegment StartX=-10.15 StartY=-12 StartZ=0 EndX=-10.15 EndY=-14 EndZ=0
    g11: LineSegment StartX=-12.8401 StartY=-16 StartZ=0 EndX=-10.1571 EndY=-16 EndZ=0
    g12: LineSegment StartX=-10.15 StartY=-14 StartZ=0 EndX=-8.70761 EndY=-14 EndZ=0
    g13: LineSegment StartX=-12.8401 StartY=-16 StartZ=0 EndX=-12.8401 EndY=-17.6958 EndZ=0
    g14: LineSegment StartX=-10.15 StartY=-12 StartZ=0 EndX=-7.79258 EndY=-12 EndZ=0
    g15: Circle CenterX=-6.2215 CenterY=-2 CenterZ=0 NormalX=0 NormalY=0 NormalZ=1 AngleXU=0 Radius=1
    g16: Circle CenterX=-6.22762 CenterY=-2.58724 CenterZ=0 NormalX=0 NormalY=0 NormalZ=1 AngleXU=0 Radius=1
    g17: Circle CenterX=-6.32538 CenterY=-4 CenterZ=0 NormalX=0 NormalY=0 NormalZ=1 AngleXU=0 Radius=1
    g18: BSplineCurve PolesCount=3 KnotsCount=2 Degree=2 IsPeriodic=0
    g19: GeomPoint X=-6.2215 Y=-2 Z=0
    g20: GeomPoint X=-6.32538 Y=-4 Z=0
    g21: Circle CenterX=-6.48644 CenterY=-5.99526 CenterZ=0 NormalX=0 NormalY=0 NormalZ=1 AngleXU=0 Radius=1
    g22: Circle CenterX=-6.58486 CenterY=-6.99526 CenterZ=0 NormalX=0 NormalY=0 NormalZ=1 AngleXU=0 Radius=1
    g23: Circle CenterX=-6.77343 CenterY=-8 CenterZ=0 NormalX=0 NormalY=0 NormalZ=1 AngleXU=0 Radius=1
    g24: BSplineCurve PolesCount=3 KnotsCount=2 Degree=2 IsPeriodic=0
    g25: GeomPoint X=-6.48644 Y=-5.99526 Z=0
    g26: GeomPoint X=-6.77343 Y=-8 Z=0
    g27: Circle CenterX=-7.19003 CenterY=-10 CenterZ=0 NormalX=0 NormalY=0 NormalZ=1 AngleXU=0 Radius=1
    g28: Circle CenterX=-7.44407 CenterY=-11.0915 CenterZ=0 NormalX=0 NormalY=0 NormalZ=1 AngleXU=0 Radius=1
    g29: Circle CenterX=-7.79258 CenterY=-12 CenterZ=0 NormalX=0 NormalY=0 NormalZ=1 AngleXU=0 Radius=1
    g30: BSplineCurve PolesCount=3 KnotsCount=2 Degree=2 IsPeriodic=0
    g31: GeomPoint X=-7.19003 Y=-10 Z=0
    g32: GeomPoint X=-7.79258 Y=-12 Z=0
    g33: Circle CenterX=-8.70761 CenterY=-14 CenterZ=0 NormalX=0 NormalY=0 NormalZ=1 AngleXU=0 Radius=1
    g34: Circle CenterX=-9.33087 CenterY=-15.1837 CenterZ=0 NormalX=0 NormalY=0 NormalZ=1 AngleXU=0 Radius=1
    g35: Circle CenterX=-10.1571 CenterY=-16 CenterZ=0 NormalX=0 NormalY=0 NormalZ=1 AngleXU=0 Radius=1
    g36: BSplineCurve PolesCount=3 KnotsCount=2 Degree=2 IsPeriodic=0
    g37: GeomPoint X=-8.70761 Y=-14 Z=0
    g38: GeomPoint X=-10.1571 Y=-16 Z=0
    g39: Circle CenterX=-12.8401 CenterY=-17.6958 CenterZ=0 NormalX=0 NormalY=0 NormalZ=1 AngleXU=0 Radius=1
    g40: Circle CenterX=-13.3521 CenterY=-17.9027 CenterZ=0 NormalX=0 NormalY=0 NormalZ=1 AngleXU=0 Radius=1
    g41: Circle CenterX=-14 CenterY=-18 CenterZ=0 NormalX=0 NormalY=0 NormalZ=1 AngleXU=0 Radius=1
    g42: BSplineCurve PolesCount=3 KnotsCount=2 Degree=2 IsPeriodic=0
    g43: GeomPoint X=-12.8401 Y=-17.6958 Z=0
    g44: GeomPoint X=-14 Y=-18 Z=0
    g45: LineSegment StartX=-6.2 StartY=0 StartZ=0 EndX=-7.2 EndY=0 EndZ=0
    g46: LineSegment StartX=-7.2 StartY=0 StartZ=0 EndX=-7.2 EndY=-2 EndZ=0
    g47: LineSegment StartX=-7.2 StartY=-2 StartZ=0 EndX=-6.2215 EndY=-2 EndZ=0
    g48: LineSegment StartX=-6.32538 StartY=-4 StartZ=0 EndX=-7.65538 EndY=-4 EndZ=0
    g49: LineSegment StartX=-7.65538 StartY=-4 StartZ=0 EndX=-7.65538 EndY=-5.99526 EndZ=0
    g50: LineSegment StartX=-7.65538 StartY=-5.99526 StartZ=0 EndX=-6.48644 EndY=-5.99526 EndZ=0
    g51: LineSegment StartX=-6.77343 StartY=-8 StartZ=0 EndX=-8.43343 EndY=-8 EndZ=0
    g52: LineSegment StartX=-8.43343 StartY=-8 StartZ=0 EndX=-8.43343 EndY=-10 EndZ=0
    g53: LineSegment StartX=-8.43343 StartY=-10 StartZ=0 EndX=-7.19003 EndY=-10 EndZ=0
  constraints (112):
    c: Horizontal(g0)
    c: Distance(g0) = 2
    c: Block(g0)
    c: Vertical(g1)
    c: Coincident(g2,g0)
    c: Vertical(g2)
    c: Block(g2)
    c: Coincident(g6,g2)
    c: Weight(g3) = 1
    c: Equal(g3,g4)
    c: Equal(g3,g5)
    c: InternalAlignment(g3,g6)
    c: InternalAlignment(g4,g6)
    c: InternalAlignment(g5,g6)
    c: InternalAlignment(g7,g6)
    c: InternalAlignment(g8,g6)
    c: Block(g6)
    c: Coincident(g9,g1)
    c: Coincident(g9,g6)
    c: Horizontal(g9)
    c: Vertical(g10)
    c: Block(g10)
    c: Horizontal(g11)
    c: Block(g11)
    c: Coincident(g12,g10)
    c: Horizontal(g12)
    c: Block(g12)
    c: Coincident(g13,g11)
    c: Vertical(g13)
    c: Block(g13)
    c: Coincident(g14,g10)
    c: Horizontal(g14)
    c: Block(g14)
    c: Block(g9)
    c: Block(g1)
    c: Weight(g15) = 1
    c: Equal(g15,g16)
    c: Equal(g15,g17)
    c: InternalAlignment(g15,g18)
    c: InternalAlignment(g16,g18)
    c: InternalAlignment(g17,g18)
    c: InternalAlignment(g19,g18)
    c: InternalAlignment(g20,g18)
    c: Weight(g21) = 1
    c: Equal(g21,g22)
    c: Equal(g21,g23)
    c: InternalAlignment(g21,g24)
    c: InternalAlignment(g22,g24)
    c: InternalAlignment(g23,g24)
    c: InternalAlignment(g25,g24)
    c: InternalAlignment(g26,g24)
    c: Weight(g27) = 1
    c: Equal(g27,g28)
    c: Equal(g27,g29)
    c: Coincident(g30,g14)
    c: InternalAlignment(g27,g30)
    c: InternalAlignment(g28,g30)
    c: InternalAlignment(g29,g30)
    c: InternalAlignment(g31,g30)
    c: InternalAlignment(g32,g30)
    c: Coincident(g36,g12)
    c: Weight(g33) = 1
    c: Equal(g33,g34)
    c: Equal(g33,g35)
    c: Coincident(g36,g11)
    c: InternalAlignment(g33,g36)
    c: InternalAlignment(g34,g36)
    c: InternalAlignment(g35,g36)
    c: InternalAlignment(g37,g36)
    c: InternalAlignment(g38,g36)
    c: Coincident(g42,g13)
    c: Weight(g39) = 1
    c: Equal(g39,g40)
    c: Equal(g39,g41)
    c: Coincident(g42,g1)
    c: InternalAlignment(g39,g42)
    c: InternalAlignment(g40,g42)
    c: InternalAlignment(g41,g42)
    c: InternalAlignment(g43,g42)
    c: InternalAlignment(g44,g42)
    c: Block(g18)
    c: Block(g24)
    c: Block(g30)
    c: Block(g36)
    c: Block(g42)
    c: Horizontal(g45)
    c: Coincident(g45,g0)
    c: Vertical(g46)
    c: Coincident(g46,g45)
    c: Coincident(g47,g46)
    c: Coincident(g47,g18)
    c: Horizontal(g47)
    c: Block(g46)
    c: Coincident(g48,g18)
    c: Horizontal(g48)
    c: Distance(g48) = 1.33
    c: Vertical(g49)
    c: Coincident(g49,g48)
    c: Coincident(g50,g49)
    c: Coincident(g50,g24)
    c: Horizontal(g50)
    c: Tangent(g50,g22)
    c: Horizontal(g51)
    c: Coincident(g51,g24)
    c: Block(g51)
    c: Vertical(g52)
    c: Block(g52)
    c: Coincident(g52,g51)
    c: Coincident(g53,g52)
    c: Coincident(g53,g30)
    c: Horizontal(g53)
    c: Distance(g1) = 8.5
FEATURE [Part::Feature] Face024
  shape: bbox 9.8 x 26.5 x 2e-07 mm, 1 faces, 0 solids (baked)
FEATURE [Part::Revolution] Revolve024
  Angle = 360
  Axis = (0,1,0)
  Base = (0,0,0)
  FaceMakerClass = Part::FaceMakerBullseye
  Placement = pos=(0,0,0) rot=(0,0,1;1.5708rad)
  Solid = false
  Source = -> Face024
  Symmetric = false
FEATURE [Part::Feature] Face025
  shape: bbox 9.8 x 26.5 x 2e-07 mm, 1 faces, 0 solids (baked)
FEATURE [Part::Revolution] Revolve025
  Angle = 360
  Axis = (0,1,0)
  Base = (0,0,0)
  FaceMakerClass = Part::FaceMakerBullseye
  Placement = pos=(0,0,0) rot=(0,0,1;1.5708rad)
  Solid = false
  Source = -> Face025
  Symmetric = false
FEATURE [Part::MultiFuse] Fusion033
  Placement = pos=(-18,19,36) rot=(0,0,1;0rad)
  Shapes = -> [Revolve025,Revolve024]
FEATURE [Part::Cylinder] Cylinder014
  Angle = 360
  AttacherType = Attacher::AttachEngine3D
  Height = 20
  Placement = pos=(0,0,36.15) rot=(0,0,1;0rad)
  Radius = 14.3
FEATURE [Part::Cylinder] Cylinder015
  Angle = 360
  AttacherType = Attacher::AttachEngine3D
  Height = 10
  Placement = pos=(0,0,36.15) rot=(0,0,1;0rad)
  Radius = 4
FEATURE [Part::MultiFuse] Fusion034  label="removeToCreteHoleForPlugHousing004"
  Placement = pos=(-42,19,36) rot=(0,1,0;1.5708rad)
  Shapes = -> [Cylinder014,Cylinder015]
FEATURE [Part::Cut] Cut008  label="top004"
  Base = -> Cut004
  Placement = pos=(-1,0,0) rot=(0,0,1;0rad)
  Tool = -> Fusion034
FEATURE [Part::Box] Box005  label="Cube005"
  AttacherType = Attacher::AttachEngine3D
  Height = 28
  Length = 3
  Placement = pos=(110.7,19,22) rot=(0,0,1;0rad)
  Width = 15.7
FEATURE [Part::Cylinder] Cylinder016
  Angle = 360
  AttacherType = Attacher::AttachEngine3D
  Height = 10
  Placement = pos=(0,0,36.15) rot=(0,0,1;0rad)
  Radius = 4
FEATURE [Part::Cylinder] Cylinder017
  Angle = 360
  AttacherType = Attacher::AttachEngine3D
  Height = 20
  Placement = pos=(0,0,36.15) rot=(0,0,1;0rad)
  Radius = 10.3
FEATURE [Part::MultiFuse] Fusion035  label="removeToCreteHoleForPlugHousing005"
  Placement = pos=(70,19,36) rot=(0,1,0;1.5708rad)
  Shapes = -> [Cylinder017,Cylinder016]
FEATURE [Part::Cut] Cut009  label="plugHousingTab001"
  Base = -> Box005
  Placement = pos=(-107.4,-14,0) rot=(0,0,1;0rad)
  Tool = -> Fusion035
FEATURE [Part::Box] Box006  label="Cube006"
  AttacherType = Attacher::AttachEngine3D
  Height = 28
  Length = 3
  Placement = pos=(110.7,19,22) rot=(0,0,1;0rad)
  Width = 15.7
FEATURE [Part::Cylinder] Cylinder018
  Angle = 360
  AttacherType = Attacher::AttachEngine3D
  Height = 10
  Placement = pos=(0,0,36.15) rot=(0,0,1;0rad)
  Radius = 4
FEATURE [Part::Cylinder] Cylinder019
  Angle = 360
  AttacherType = Attacher::AttachEngine3D
  Height = 20
  Placement = pos=(0,0,36.15) rot=(0,0,1;0rad)
  Radius = 10.3
FEATURE [Part::MultiFuse] Fusion036  label="removeToCreteHoleForPlugHousing006"
  Placement = pos=(70,19,36) rot=(0,1,0;1.5708rad)
  Shapes = -> [Cylinder019,Cylinder018]
FEATURE [Part::Cut] Cut010  label="plugHousingTab002"
  Base = -> Box006
  Placement = pos=(-107.4,-14,0) rot=(0,0,1;0rad)
  Tool = -> Fusion036
FEATURE [Part::MultiFuse] Fusion037
  Placement = pos=(9.6,23,0) rot=(0,0,1;3.14159rad)
  Shapes = -> [Cut009,Cut010]
FEATURE [Part::Box] Box  label="Cube"
  AttacherType = Attacher::AttachEngine3D
  Height = 10
  Length = 3
  Placement = pos=(3.3,4,12) rot=(0,0,1;0rad)
  Width = 10
FEATURE [Part::Fillet] Fillet004
  Base = -> Fusion028
  Edges = 1 edges r=2: [Edge25]
FEATURE [Part::Fillet] Fillet005  label="plugHousing046"
  Base = -> Fillet004
  Edges = 1 edges r=2: [Edge8]
FEATURE [Part::Fillet] Fillet006
  Base = -> Box
  Edges = 1 edges r=2: [Edge11]
FEATURE [Part::Box] Box007  label="Cube007"
  AttacherType = Attacher::AttachEngine3D
  Height = 10
  Length = 3
  Placement = pos=(3.3,4,50) rot=(0,0,1;0rad)
  Width = 10
FEATURE [Part::Fillet] Fillet007
  Base = -> Box007
  Edges = 1 edges r=2: [Edge12]
FEATURE [Part::Box] Box008  label="Cube008"
  AttacherType = Attacher::AttachEngine3D
  Height = 28
  Length = 4
  Placement = pos=(5,0,22) rot=(0,0,1;0rad)
  Width = 10
FEATURE [Part::Fillet] Fillet008
  Base = -> Box008
  Edges = 1 edges r=1: [Edge7]
FEATURE [Part::Fillet] Fillet009
  Base = -> Fillet008
  Edges = 1 edges r=2: [Edge5]
FEATURE [Part::Fillet] Fillet010
  Base = -> Fillet009
  Edges = 1 edges r=2: [Edge2]
FEATURE [Sketcher::SketchObject] Sketch009  label="topSketch003"
  FullyConstrained = true
  sketch-geometry (4):
    g0: LineSegment StartX=16.8446 StartY=31.512 StartZ=0 EndX=16.3251 EndY=34.4666 EndZ=0
    g1: ArcOfCircle CenterX=19 CenterY=19.2524 CenterZ=0 NormalX=0 NormalY=0 NormalZ=1 AngleXU=0 Radius=15.4476 StartAngle=1.74483 EndAngle=2.72717
    g2: ArcOfCircle CenterX=19 CenterY=19.2524 CenterZ=0 NormalX=0 NormalY=0 NormalZ=1 AngleXU=0 Radius=12.4476 StartAngle=1.74483 EndAngle=2.73189
    g3: LineSegment StartX=4.86004 StartY=25.4725 StartZ=0 EndX=7.58253 EndY=24.2107 EndZ=0
  constraints (7):
    c: Block(g0)
    c: Coincident(g1,g0)
    c: Coincident(g2,g0)
    c: Coincident(g3,g1)
    c: Coincident(g3,g2)
    c: Block(g1)
    c: Block(g2)
FEATURE [Part::Extrusion] Extrude008
  Base = -> Sketch009
  Dir = (0,0,1)
  DirMode = 2
  FaceMakerClass = Part::FaceMakerBullseye
  LengthFwd = 10
  LengthRev = 0
  Placement = pos=(0,0,31) rot=(0,0,1;0rad)
  Solid = true
  Symmetric = false
FEATURE [Part::Cylinder] Cylinder020
  Angle = 360
  AttacherType = Attacher::AttachEngine3D
  Height = 20
  Placement = pos=(0,0,36.15) rot=(0,0,1;0rad)
  Radius = 8.2
FEATURE [Part::Cylinder] Cylinder021
  Angle = 360
  AttacherType = Attacher::AttachEngine3D
  Height = 10
  Placement = pos=(0,0,36.15) rot=(0,0,1;0rad)
  Radius = 4
FEATURE [Part::MultiFuse] Fusion038  label="removeToCreteHoleForPlugHousing007"
  Placement = pos=(-42,19,36) rot=(0,1,0;1.5708rad)
  Shapes = -> [Cylinder020,Cylinder021]
FEATURE [Part::Cut] Cut011
  Base = -> Extrude008
  Tool = -> Fusion038
FEATURE [Part::Fillet] Fillet011
  Base = -> Cut011
  Edges = 1 edges r=2: [Edge1]
FEATURE [Part::Fillet] Fillet012
  Base = -> Fillet011
  Edges = 1 edges r=2.5: [Edge1]
FEATURE [Part::Fillet] Fillet013
  Base = -> Fillet012
  Edges = 1 edges r=2.5: [Edge2]
FEATURE [Part::Box] Box010  label="Cube010"
  AttacherType = Attacher::AttachEngine3D
  Height = 16
  Length = 8
  Placement = pos=(12.7,31.52,28) rot=(0,0,1;0rad)
  Width = 4
FEATURE [Sketcher::SketchObject] Sketch010  label="topSketch004"
  FullyConstrained = true
  sketch-geometry (4):
    g0: LineSegment StartX=16.8446 StartY=31.512 StartZ=0 EndX=16.3251 EndY=34.4666 EndZ=0
    g1: ArcOfCircle CenterX=19 CenterY=19.2524 CenterZ=0 NormalX=0 NormalY=0 NormalZ=1 AngleXU=0 Radius=15.4476 StartAngle=1.74483 EndAngle=2.72717
    g2: ArcOfCircle CenterX=19 CenterY=19.2524 CenterZ=0 NormalX=0 NormalY=0 NormalZ=1 AngleXU=0 Radius=12.4476 StartAngle=1.74483 EndAngle=2.73189
    g3: LineSegment StartX=4.86004 StartY=25.4725 StartZ=0 EndX=7.58253 EndY=24.2107 EndZ=0
  constraints (7):
    c: Block(g0)
    c: Coincident(g1,g0)
    c: Coincident(g2,g0)
    c: Coincident(g3,g1)
    c: Coincident(g3,g2)
    c: Block(g1)
    c: Block(g2)
FEATURE [Part::Cylinder] Cylinder022
  Angle = 360
  AttacherType = Attacher::AttachEngine3D
  Height = 10
  Placement = pos=(0,0,36.15) rot=(0,0,1;0rad)
  Radius = 4
FEATURE [Sketcher::SketchObject] Sketch011  label="topSketch005"
  FullyConstrained = true
  sketch-geometry (4):
    g0: LineSegment StartX=16.8446 StartY=31.512 StartZ=0 EndX=16.3251 EndY=34.4666 EndZ=0
    g1: ArcOfCircle CenterX=19 CenterY=19.2524 CenterZ=0 NormalX=0 NormalY=0 NormalZ=1 AngleXU=0 Radius=15.4476 StartAngle=1.74483 EndAngle=2.72717
    g2: ArcOfCircle CenterX=19 CenterY=19.2524 CenterZ=0 NormalX=0 NormalY=0 NormalZ=1 AngleXU=0 Radius=12.4476 StartAngle=1.74483 EndAngle=2.73189
    g3: LineSegment StartX=4.86004 StartY=25.4725 StartZ=0 EndX=7.58253 EndY=24.2107 EndZ=0
  constraints (7):
    c: Block(g0)
    c: Coincident(g1,g0)
    c: Coincident(g2,g0)
    c: Coincident(g3,g1)
    c: Coincident(g3,g2)
    c: Block(g1)
    c: Block(g2)
FEATURE [Part::Extrusion] Extrude010
  Base = -> Sketch011
  Dir = (0,0,1)
  DirMode = 2
  FaceMakerClass = Part::FaceMakerBullseye
  LengthFwd = 10.6
  LengthRev = 0
  Placement = pos=(0,0,31) rot=(0,0,1;0rad)
  Solid = true
  Symmetric = false
FEATURE [Part::Cylinder] Cylinder023
  Angle = 360
  AttacherType = Attacher::AttachEngine3D
  Height = 20
  Placement = pos=(0,0,36.15) rot=(0,0,1;0rad)
  Radius = 8.2
FEATURE [Part::MultiFuse] Fusion039  label="removeToCreteHoleForPlugHousing008"
  Placement = pos=(-42,19,36) rot=(0,1,0;1.5708rad)
  Shapes = -> [Cylinder023,Cylinder022]
FEATURE [Part::Cut] Cut012
  Base = -> Extrude010
  Placement = pos=(0,0,-0.3) rot=(0,0,1;0rad)
  Tool = -> Fusion039
FEATURE [Part::Cut] Cut013
  Base = -> Box010
  Tool = -> Cut012
FEATURE [Part::Fillet] Fillet014
  Base = -> Cut013
  Edges = 1 edges r=0.7: [Edge13]
FEATURE [Part::Fillet] Fillet015
  Base = -> Fillet014
  Edges = 1 edges r=0.7: [Edge13]
FEATURE [Part::Fillet] Fillet016
  Base = -> Fillet015
  Edges = 1 edges r=0.7: [Edge16]
FEATURE [Part::Fillet] Fillet017
  Base = -> Fillet016
  Edges = 1 edges r=0.7: [Edge11]
FEATURE [Part::Fillet] Fillet018
  Base = -> Fillet017
  Edges = 1 edges r=0.7: [Edge10]
FEATURE [Part::Fillet] Fillet019
  Base = -> Fillet018
  Edges = 1 edges r=1.2: [Edge5]
FEATURE [Part::Fillet] Fillet020
  Base = -> Fillet019
  Edges = 1 edges r=1.2: [Edge12]
FEATURE [Part::Fillet] Fillet021
  Base = -> Fillet020
  Edges = 1 edges r=2: [Edge1]
  Placement = pos=(0.3,0,0) rot=(0,0,1;0rad)
FEATURE [Part::MultiFuse] Fusion040  label="top005"
  Shapes = -> [Cut008,Fillet021]
FEATURE [Part::MultiFuse] Fusion041  label="wireHolder"
  Shapes = -> [Fusion033,Fillet013]
FEATURE [Part::MultiFuse] Fusion042
  Shapes = -> [Fillet007,Fusion041]
FEATURE [Part::MultiFuse] Fusion043  label="wireHolder001"
  Shapes = -> [Fusion042,Fillet010]
FEATURE [Part::MultiFuse] Fusion044  label="wireHolder002"
  Shapes = -> [Fillet006,Fusion037,Fusion043]
FEATURE [Part::Feature] Face026
  shape: bbox 11 x 6 x 2e-07 mm, 1 faces, 0 solids (baked)
FEATURE [Part::Revolution] Revolve026
  Angle = 360
  Axis = (0,1,0)
  Base = (0,0,0)
  FaceMakerClass = Part::FaceMakerBullseye
  Placement = pos=(30.3,-1,19.7) rot=(0,0,1;0rad)
  Solid = false
  Source = -> Face026
  Symmetric = false
FEATURE [Sketcher::SketchObject] Sketch013  label="topSketch006"
  FullyConstrained = true
  sketch-geometry (13):
    g0: LineSegment StartX=117 StartY=19 StartZ=0 EndX=117 EndY=38 EndZ=0
    g1: ArcOfCircle CenterX=98 CenterY=19 CenterZ=0 NormalX=0 NormalY=0 NormalZ=1 AngleXU=0 Radius=19 StartAngle=5.7297 EndAngle=6.28319
    g2: LineSegment StartX=0 StartY=3 StartZ=0 EndX=0 EndY=19 EndZ=0
    g3: LineSegment StartX=19 StartY=38 StartZ=0 EndX=117 EndY=38 EndZ=0
    g4: ArcOfCircle CenterX=19 CenterY=19 CenterZ=0 NormalX=0 NormalY=0 NormalZ=1 AngleXU=0 Radius=19 StartAngle=1.5708 EndAngle=3.14159
    g5: ArcOfCircle CenterX=19 CenterY=19 CenterZ=0 NormalX=0 NormalY=0 NormalZ=1 AngleXU=0 Radius=16 StartAngle=1.5708 EndAngle=3.14159
    g6: ArcOfCircle CenterX=98 CenterY=19 CenterZ=0 NormalX=0 NormalY=0 NormalZ=1 AngleXU=0 Radius=16 StartAngle=5.60905 EndAngle=6.28319
    g7: LineSegment StartX=114 StartY=19 StartZ=0 EndX=114 EndY=35 EndZ=0
    g8: LineSegment StartX=110.5 StartY=9.01251 StartZ=0 EndX=114.163 EndY=9.01251 EndZ=0
    g9: LineSegment StartX=114 StartY=35 StartZ=0 EndX=19 EndY=35 EndZ=0
    g10: LineSegment StartX=0 StartY=3 StartZ=0 EndX=0 EndY=0 EndZ=0
    g11: LineSegment StartX=3 StartY=0 StartZ=0 EndX=0 EndY=0 EndZ=0
    g12: LineSegment StartX=3 StartY=19 StartZ=0 EndX=3 EndY=0 EndZ=0
  constraints (33):
    c: Vertical(g0)
    c: Distance(g0) = 19
    c: Block(g0)
    c: Coincident(g1,g0)
    c: Block(g1)
    c: Vertical(g2)
    c: Block(g2)
    c: Coincident(g3,g0)
    c: Horizontal(g3)
    c: Distance(g3) = 98
    c: Coincident(g4,g3)
    c: Coincident(g4,g2)
    c: Block(g4)
    c: Coincident(g5,g4)
    c: Coincident(g6,g1)
    c: Block(g6)
    c: Block(g5)
    c: Coincident(g7,g6)
    c: Vertical(g7)
    c: Coincident(g8,g6)
    c: Coincident(g8,g1)
    c: Coincident(g9,g7)
    c: Coincident(g9,g5)
    c: Horizontal(g9)
    c: Tangent(g9,g5)
    c: Coincident(g10,g2)
    c: Distance(g10) = 3
    c: Vertical(g10)
    c: Coincident(g11,g10)
    c: Horizontal(g11)
    c: Coincident(g12,g5)
    c: Coincident(g12,g11)
    c: Vertical(g12)
FEATURE [Part::Extrusion] Extrude011  label="top006"
  Base = -> Sketch013
  Dir = (0,0,1)
  DirMode = 2
  FaceMakerClass = Part::FaceMakerBullseye
  LengthFwd = 72
  LengthRev = 0
  Solid = true
  Symmetric = false
FEATURE [Sketcher::SketchObject] Sketch014
  FullyConstrained = true
  MapMode = 3
  Placement = pos=(0,0,0) rot=(1,0,0;1.5708rad)
  Support = -> [Extrude011]
  sketch-geometry (8):
    g0: Circle CenterX=80.351 CenterY=-67.6202 CenterZ=0 NormalX=0 NormalY=0 NormalZ=1 AngleXU=0 Radius=2
    g1: Circle CenterX=80.351 CenterY=-67.6202 CenterZ=0 NormalX=0 NormalY=0 NormalZ=1 AngleXU=0 Radius=3
    g2: Circle CenterX=80.351 CenterY=-4.92017 CenterZ=0 NormalX=0 NormalY=0 NormalZ=1 AngleXU=0 Radius=2
    g3: Circle CenterX=80.351 CenterY=-4.92017 CenterZ=0 NormalX=0 NormalY=0 NormalZ=1 AngleXU=0 Radius=3
    g4: Circle CenterX=23.851 CenterY=-4.92017 CenterZ=0 NormalX=0 NormalY=0 NormalZ=1 AngleXU=0 Radius=2
    g5: Circle CenterX=23.851 CenterY=-4.92017 CenterZ=0 NormalX=0 NormalY=0 NormalZ=1 AngleXU=0 Radius=3
    g6: Circle CenterX=23.851 CenterY=-67.6202 CenterZ=0 NormalX=0 NormalY=0 NormalZ=1 AngleXU=0 Radius=2
    g7: Circle CenterX=23.851 CenterY=-67.6202 CenterZ=0 NormalX=0 NormalY=0 NormalZ=1 AngleXU=0 Radius=3
  constraints (8):
    c: Block(g3)
    c: Block(g2)
    c: Block(g1)
    c: Block(g0)
    c: Block(g6)
    c: Block(g7)
    c: Block(g4)
    c: Block(g5)
FEATURE [Part::Feature] Face027
  shape: bbox 11 x 6 x 2e-07 mm, 1 faces, 0 solids (baked)
FEATURE [Part::Revolution] Revolve027
  Angle = 360
  Axis = (0,1,0)
  Base = (0,0,0)
  FaceMakerClass = Part::FaceMakerBullseye
  Placement = pos=(30.3,-1,51.7) rot=(0,0,1;0rad)
  Solid = false
  Source = -> Face027
  Symmetric = false
FEATURE [Part::Feature] Face028
  shape: bbox 11 x 6 x 2e-07 mm, 1 faces, 0 solids (baked)
FEATURE [Part::Revolution] Revolve028
  Angle = 360
  Axis = (0,1,0)
  Base = (0,0,0)
  FaceMakerClass = Part::FaceMakerBullseye
  Placement = pos=(62.3,-1,19.7) rot=(0,0,1;0rad)
  Solid = false
  Source = -> Face028
  Symmetric = false
FEATURE [Part::Feature] Face029
  shape: bbox 11 x 6 x 2e-07 mm, 1 faces, 0 solids (baked)
FEATURE [Part::Revolution] Revolve029
  Angle = 360
  Axis = (0,1,0)
  Base = (0,0,0)
  FaceMakerClass = Part::FaceMakerBullseye
  Placement = pos=(62.3,-1,51.7) rot=(0,0,1;0rad)
  Solid = false
  Source = -> Face029
  Symmetric = false
FEATURE [Part::Feature] Wire
  shape: bbox 11 x 5.2 x 2e-07 mm, 0 faces, 0 solids (baked)
FEATURE [Part::Revolution] Revolve030
  Angle = 360
  Axis = (0,1,0)
  Base = (0,0,0)
  FaceMakerClass = Part::FaceMakerBullseye
  Placement = pos=(30.3,38,19.7) rot=(0,0,1;0rad)
  Solid = true
  Source = -> Wire
  Symmetric = false
FEATURE [Part::Feature] Wire001
  shape: bbox 11 x 5.2 x 2e-07 mm, 0 faces, 0 solids (baked)
FEATURE [Part::Revolution] Revolve031
  Angle = 360
  Axis = (0,1,0)
  Base = (0,0,0)
  FaceMakerClass = Part::FaceMakerBullseye
  Placement = pos=(30.3,38,51.7) rot=(0,0,1;0rad)
  Solid = true
  Source = -> Wire001
  Symmetric = false
FEATURE [Part::Feature] Wire002
  shape: bbox 11 x 5.2 x 2e-07 mm, 0 faces, 0 solids (baked)
FEATURE [Part::Revolution] Revolve032
  Angle = 360
  Axis = (0,1,0)
  Base = (0,0,0)
  FaceMakerClass = Part::FaceMakerBullseye
  Placement = pos=(62.3,38,51.7) rot=(0,0,1;0rad)
  Solid = true
  Source = -> Wire002
  Symmetric = false
FEATURE [Part::Feature] Wire003
  shape: bbox 11 x 5.2 x 2e-07 mm, 0 faces, 0 solids (baked)
FEATURE [Part::Revolution] Revolve033
  Angle = 360
  Axis = (0,1,0)
  Base = (0,0,0)
  FaceMakerClass = Part::FaceMakerBullseye
  Placement = pos=(62.3,38,19.7) rot=(0,0,1;0rad)
  Solid = true
  Source = -> Wire003
  Symmetric = false
FEATURE [Part::MultiFuse] Fusion045  label="altRandScrewHousing"
  Shapes = -> [Revolve029,Revolve027,Revolve028,Revolve026]
FEATURE [Part::MultiFuse] Fusion046  label="fanScrewHousing"
  Shapes = -> [Revolve033,Revolve032,Revolve031,Revolve030]
FEATURE [Sketcher::SketchObject] Sketch015
  FullyConstrained = true
  sketch-geometry (17):
    g0: Circle CenterX=-3.5 CenterY=23.5 CenterZ=0 NormalX=0 NormalY=0 NormalZ=1 AngleXU=0 Radius=1
    g1: Circle CenterX=-1 CenterY=15.25 CenterZ=0 NormalX=0 NormalY=0 NormalZ=1 AngleXU=0 Radius=1
    g2: Circle CenterX=-3.5 CenterY=7 CenterZ=0 NormalX=0 NormalY=0 NormalZ=1 AngleXU=0 Radius=1
    g3: BSplineCurve PolesCount=3 KnotsCount=2 Degree=2 IsPeriodic=0
    g4: GeomPoint X=-3.5 Y=23.5 Z=0
    g5: GeomPoint X=-3.5 Y=7 Z=0
    g6: Circle CenterX=-4.8 CenterY=30.5 CenterZ=0 NormalX=0 NormalY=0 NormalZ=1 AngleXU=0 Radius=1
    g7: Circle CenterX=-3.5 CenterY=30.5 CenterZ=0 NormalX=0 NormalY=0 NormalZ=1 AngleXU=0 Radius=1
    g8: Circle CenterX=-3.5 CenterY=29.2 CenterZ=0 NormalX=0 NormalY=0 NormalZ=1 AngleXU=0 Radius=1
    g9: BSplineCurve PolesCount=3 KnotsCount=2 Degree=2 IsPeriodic=0
    g10: GeomPoint X=-4.8 Y=30.5 Z=0
    g11: GeomPoint X=-3.5 Y=29.2 Z=0
    g12: LineSegment StartX=-3.5 StartY=29.2 StartZ=0 EndX=-3.5 EndY=23.5 EndZ=0
    g13: LineSegment StartX=-4.8 StartY=30.5 StartZ=0 EndX=0 EndY=30.5 EndZ=0
    g14: LineSegment StartX=-3.5 StartY=0.3 StartZ=0 EndX=0 EndY=0.3 EndZ=0
    g15: LineSegment StartX=-3.5 StartY=0.3 StartZ=0 EndX=-3.5 EndY=7 EndZ=0
    g16: LineSegment StartX=0 StartY=0.3 StartZ=0 EndX=0 EndY=30.5 EndZ=0
  constraints (33):
    c: Weight(g0) = 1
    c: Equal(g0,g1)
    c: Equal(g0,g2)
    c: InternalAlignment(g0,g3)
    c: InternalAlignment(g1,g3)
    c: InternalAlignment(g2,g3)
    c: InternalAlignment(g4,g3)
    c: InternalAlignment(g5,g3)
    c: Block(g3)
    c: Weight(g6) = 1
    c: Equal(g6,g7)
    c: Equal(g6,g8)
    c: InternalAlignment(g6,g9)
    c: InternalAlignment(g7,g9)
    c: InternalAlignment(g8,g9)
    c: InternalAlignment(g10,g9)
    c: InternalAlignment(g11,g9)
    c: Block(g9)
    c: Coincident(g12,g9)
    c: Coincident(g12,g3)
    c: Vertical(g12)
    c: Coincident(g13,g9)
    c: Horizontal(g13)
    c: Distance(g13) = 4.8
    c: Horizontal(g14)
    c: Block(g14)
    c: Coincident(g15,g14)
    c: Coincident(g15,g3)
    c: Vertical(g15)
    c: Coincident(g16,g14)
    c: Coincident(g16,g13)
    c: Vertical(g16)
    c: Tangent(g16,g1)
FEATURE [Sketcher::SketchObject] Sketch016
  FullyConstrained = true
  sketch-geometry (16):
    g0: Circle CenterX=-3.5 CenterY=23.5 CenterZ=0 NormalX=0 NormalY=0 NormalZ=1 AngleXU=0 Radius=1
    g1: Circle CenterX=-1 CenterY=15.25 CenterZ=0 NormalX=0 NormalY=0 NormalZ=1 AngleXU=0 Radius=1
    g2: Circle CenterX=-3.5 CenterY=7 CenterZ=0 NormalX=0 NormalY=0 NormalZ=1 AngleXU=0 Radius=1
    g3: BSplineCurve PolesCount=3 KnotsCount=2 Degree=2 IsPeriodic=0
    g4: GeomPoint X=-3.5 Y=23.5 Z=0
    g5: GeomPoint X=-3.5 Y=7 Z=0
    g6: LineSegment StartX=-3.5 StartY=28.2 StartZ=0 EndX=-3.5 EndY=23.5 EndZ=0
    g7: LineSegment StartX=0 StartY=29.5 StartZ=0 EndX=0 EndY=30 EndZ=0
    g8: LineSegment StartX=-3.5 StartY=28.2 StartZ=0 EndX=-3.5 EndY=30 EndZ=0
    g9: LineSegment StartX=0 StartY=30 StartZ=0 EndX=0 EndY=30.5 EndZ=0
    g10: LineSegment StartX=0 StartY=30.5 StartZ=0 EndX=-3.5 EndY=30.5 EndZ=0
    g11: LineSegment StartX=-3.5 StartY=30.5 StartZ=0 EndX=-3.5 EndY=30 EndZ=0
    g12: LineSegment StartX=0 StartY=29.5 StartZ=0 EndX=0 EndY=5 EndZ=0
    g13: LineSegment StartX=-3.5 StartY=0.3 StartZ=0 EndX=-3.5 EndY=7 EndZ=0
    g14: LineSegment StartX=-3.5 StartY=0.3 StartZ=0 EndX=0 EndY=0.3 EndZ=0
    g15: LineSegment StartX=0 StartY=5 StartZ=0 EndX=0 EndY=0.3 EndZ=0
  constraints (39):
    c: Weight(g0) = 1
    c: Equal(g0,g1)
    c: Equal(g0,g2)
    c: InternalAlignment(g0,g3)
    c: InternalAlignment(g1,g3)
    c: InternalAlignment(g2,g3)
    c: InternalAlignment(g4,g3)
    c: InternalAlignment(g5,g3)
    c: Block(g3)
    c: Coincident(g6,g3)
    c: Vertical(g6)
    c: Vertical(g7)
    c: Distance(g7) = 0.5
    c: Coincident(g8,g6)
    c: Vertical(g8)
    c: Block(g6)
    c: Block(g7)
    c: Vertical(g9)
    c: Equal(g7,g9) = 0.5
    c: Block(g9)
    c: Coincident(g9,g7)
    c: Horizontal(g10)
    c: Coincident(g10,g9)
    c: Coincident(g11,g10)
    c: Coincident(g11,g8)
    c: Vertical(g11)
    c: Block(g11)
    c: Coincident(g12,g7)
    c: Vertical(g12)
    c: Coincident(g13,g3)
    c: Vertical(g13)
    c: Distance(g13) = 6.7
    c: Coincident(g14,g13)
    c: Horizontal(g14)
    c: Block(g14)
    c: Coincident(g15,g12)
    c: Coincident(g15,g14)
    c: Vertical(g15)
    c: Block(g15)
FEATURE [Sketcher::SketchObject] Sketch017
  FullyConstrained = true
  sketch-geometry (11):
    g0: LineSegment StartX=-3.5 StartY=1e-16 StartZ=0 EndX=-1.6 EndY=1e-16 EndZ=0
    g1: LineSegment StartX=-1.6 StartY=1e-16 StartZ=0 EndX=-1.6 EndY=1.5 EndZ=0
    g2: LineSegment StartX=-3.5 StartY=1.5 StartZ=0 EndX=-1.6 EndY=1.5 EndZ=0
    g3: LineSegment StartX=-3.5 StartY=1e-16 StartZ=0 EndX=-4.8 EndY=1e-16 EndZ=0
    g4: Circle CenterX=-3.5 CenterY=1.3 CenterZ=0 NormalX=0 NormalY=0 NormalZ=1 AngleXU=0 Radius=1
    g5: Circle CenterX=-3.5 CenterY=1e-16 CenterZ=0 NormalX=0 NormalY=0 NormalZ=1 AngleXU=0 Radius=1
    g6: Circle CenterX=-4.8 CenterY=1e-16 CenterZ=0 NormalX=0 NormalY=0 NormalZ=1 AngleXU=0 Radius=1
    g7: BSplineCurve PolesCount=3 KnotsCount=2 Degree=2 IsPeriodic=0
    g8: GeomPoint X=-3.5 Y=1.3 Z=0
    g9: GeomPoint X=-4.8 Y=1e-16 Z=0
    g10: LineSegment StartX=-3.5 StartY=1.3 StartZ=0 EndX=-3.5 EndY=1.5 EndZ=0
  constraints (24):
    c: Horizontal(g0)
    c: Distance(g0) = 1.9
    c: Block(g0)
    c: Coincident(g1,g0)
    c: Vertical(g1)
    c: Coincident(g2,g1)
    c: Horizontal(g2)
    c: Coincident(g3,g0)
    c: Horizontal(g3)
    c: Distance(g3) = 1.3
    c: Weight(g4) = 1
    c: Equal(g4,g5)
    c: Coincident(g5,g0)
    c: Equal(g4,g6)
    c: Coincident(g7,g3)
    c: InternalAlignment(g4,g7)
    c: InternalAlignment(g5,g7)
    c: InternalAlignment(g6,g7)
    c: InternalAlignment(g8,g7)
    c: InternalAlignment(g9,g7)
    c: Coincident(g10,g7)
    c: Coincident(g10,g2)
    c: Vertical(g10)
    c: Block(g10)
FEATURE [Part::Feature] Face035
  shape: bbox 3.2 x 1.5 x 2e-07 mm, 1 faces, 0 solids (baked)
FEATURE [Part::Revolution] Revolve039  label="backCaseScrewRetainer"
  Angle = 360
  Axis = (0,1,0)
  Base = (0,0,0)
  FaceMakerClass = Part::FaceMakerBullseye
  Placement = pos=(12.5,3,62) rot=(0,0,1;0rad)
  Solid = false
  Source = -> Face035
  Symmetric = false
FEATURE [Part::Feature] Face036
  shape: bbox 3.2 x 1.5 x 2e-07 mm, 1 faces, 0 solids (baked)
FEATURE [Part::Feature] Face039
  shape: bbox 4.8 x 30.2 x 2e-07 mm, 1 faces, 0 solids (baked)
FEATURE [Part::Revolution] Revolve043  label="frontCaseScrewPost002"
  Angle = 360
  Axis = (0,1,0)
  Base = (0,0,0)
  FaceMakerClass = Part::FaceMakerBullseye
  Placement = pos=(89.5,4.5,3.5) rot=(0,0,1;0rad)
  Solid = false
  Source = -> Face039
  Symmetric = false
FEATURE [Part::Feature] Face042
  shape: bbox 4.8 x 30.2 x 2e-07 mm, 1 faces, 0 solids (baked)
FEATURE [Part::Revolution] Revolve046  label="frontCaseScrewPost003"
  Angle = 360
  Axis = (0,1,0)
  Base = (0,0,0)
  FaceMakerClass = Part::FaceMakerBullseye
  Placement = pos=(89.5,4.5,68.5) rot=(0,0,1;0rad)
  Solid = false
  Source = -> Face042
  Symmetric = false
FEATURE [Part::Feature] Face043
  shape: bbox 3.2 x 1.5 x 2e-07 mm, 1 faces, 0 solids (baked)
FEATURE [Part::Revolution] Revolve047  label="frontCaseScrewRetainer002"
  Angle = 360
  Axis = (0,1,0)
  Base = (0,0,0)
  FaceMakerClass = Part::FaceMakerBullseye
  Placement = pos=(89.5,3,68.5) rot=(0,0,1;0rad)
  Solid = false
  Source = -> Face043
  Symmetric = false
FEATURE [Part::Feature] Face044
  shape: bbox 3.2 x 1.5 x 2e-07 mm, 1 faces, 0 solids (baked)
FEATURE [Part::Revolution] Revolve048  label="frontCaseScrewRetainer003"
  Angle = 360
  Axis = (0,1,0)
  Base = (0,0,0)
  FaceMakerClass = Part::FaceMakerBullseye
  Placement = pos=(89.5,3,3.5) rot=(0,0,1;0rad)
  Solid = false
  Source = -> Face044
  Symmetric = false
FEATURE [App::MeasureDistance] Distance002  label="Distance: 1.67 mm"
  Distance = 1.66921
  P1 = (99.2361,4.7524,71.7)
  P2 = (99.2347,6.42161,71.7)
FEATURE [Sketcher::SketchObject] Sketch018
  FullyConstrained = true
  sketch-geometry (7):
    g0: LineSegment StartX=0 StartY=0 StartZ=0 EndX=0 EndY=6 EndZ=0
    g1: Circle CenterX=0 CenterY=0 CenterZ=0 NormalX=0 NormalY=0 NormalZ=1 AngleXU=0 Radius=1
    g2: Circle CenterX=8 CenterY=6 CenterZ=0 NormalX=0 NormalY=0 NormalZ=1 AngleXU=0 Radius=1
    g3: BSplineCurve PolesCount=3 KnotsCount=2 Degree=2 IsPeriodic=0
    g4: GeomPoint X=0 Y=0 Z=0
    g5: GeomPoint X=8 Y=6 Z=0
    g6: LineSegment StartX=0 StartY=6 StartZ=0 EndX=8 EndY=6 EndZ=0
  constraints (14):
    c: Coincident(g0,g-1)
    c: Distance(g0) = 6
    c: Vertical(g0)
    c: Coincident(g3,g0)
    c: Weight(g1) = 1
    c: Equal(g1,g2)
    c: InternalAlignment(g1,g3)
    c: InternalAlignment(g2,g3)
    c: InternalAlignment(g4,g3)
    c: InternalAlignment(g5,g3)
    c: Block(g3)
    c: Coincident(g6,g0)
    c: Coincident(g6,g3)
    c: Horizontal(g6)
FEATURE [Part::Extrusion] Extrude012  label="caseScrewPillarBracket"
  Base = -> Sketch018
  Dir = (0,0,1)
  DirMode = 2
  FaceMakerClass = Part::FaceMakerBullseye
  LengthFwd = 2.4
  LengthRev = 0
  Placement = pos=(15.76,29,8.8) rot=(0,1,0;0rad)
  Solid = true
  Symmetric = false
FEATURE [Sketcher::SketchObject] Sketch019
  FullyConstrained = true
  sketch-geometry (7):
    g0: LineSegment StartX=0 StartY=0 StartZ=0 EndX=0 EndY=6 EndZ=0
    g1: Circle CenterX=0 CenterY=0 CenterZ=0 NormalX=0 NormalY=0 NormalZ=1 AngleXU=0 Radius=1
    g2: Circle CenterX=8 CenterY=6 CenterZ=0 NormalX=0 NormalY=0 NormalZ=1 AngleXU=0 Radius=1
    g3: BSplineCurve PolesCount=3 KnotsCount=2 Degree=2 IsPeriodic=0
    g4: GeomPoint X=0 Y=0 Z=0
    g5: GeomPoint X=8 Y=6 Z=0
    g6: LineSegment StartX=0 StartY=6 StartZ=0 EndX=8 EndY=6 EndZ=0
  constraints (14):
    c: Coincident(g0,g-1)
    c: Distance(g0) = 6
    c: Vertical(g0)
    c: Coincident(g3,g0)
    c: Weight(g1) = 1
    c: Equal(g1,g2)
    c: InternalAlignment(g1,g3)
    c: InternalAlignment(g2,g3)
    c: InternalAlignment(g4,g3)
    c: InternalAlignment(g5,g3)
    c: Block(g3)
    c: Coincident(g6,g0)
    c: Coincident(g6,g3)
    c: Horizontal(g6)
FEATURE [Part::Extrusion] Extrude013  label="caseScrewPillarBracket001"
  Base = -> Sketch019
  Dir = (0,0,1)
  DirMode = 2
  FaceMakerClass = Part::FaceMakerBullseye
  LengthFwd = 2.4
  LengthRev = 0
  Placement = pos=(15.76,29,60.8) rot=(0,0,1;0rad)
  Solid = true
  Symmetric = false
FEATURE [Sketcher::SketchObject] Sketch020
  FullyConstrained = true
  sketch-geometry (7):
    g0: LineSegment StartX=0 StartY=0 StartZ=0 EndX=0 EndY=6 EndZ=0
    g1: Circle CenterX=0 CenterY=0 CenterZ=0 NormalX=0 NormalY=0 NormalZ=1 AngleXU=0 Radius=1
    g2: Circle CenterX=8 CenterY=6 CenterZ=0 NormalX=0 NormalY=0 NormalZ=1 AngleXU=0 Radius=1
    g3: BSplineCurve PolesCount=3 KnotsCount=2 Degree=2 IsPeriodic=0
    g4: GeomPoint X=0 Y=0 Z=0
    g5: GeomPoint X=8 Y=6 Z=0
    g6: LineSegment StartX=0 StartY=6 StartZ=0 EndX=8 EndY=6 EndZ=0
  constraints (14):
    c: Coincident(g0,g-1)
    c: Distance(g0) = 6
    c: Vertical(g0)
    c: Coincident(g3,g0)
    c: Weight(g1) = 1
    c: Equal(g1,g2)
    c: InternalAlignment(g1,g3)
    c: InternalAlignment(g2,g3)
    c: InternalAlignment(g4,g3)
    c: InternalAlignment(g5,g3)
    c: Block(g3)
    c: Coincident(g6,g0)
    c: Coincident(g6,g3)
    c: Horizontal(g6)
FEATURE [Part::Extrusion] Extrude014  label="caseScrewPillarBracket002"
  Base = -> Sketch020
  Dir = (0,0,1)
  DirMode = 2
  FaceMakerClass = Part::FaceMakerBullseye
  LengthFwd = 2.4
  LengthRev = 0
  Placement = pos=(13.7,29,13.26) rot=(0,-1,0;1.5708rad)
  Solid = true
  Symmetric = false
FEATURE [Sketcher::SketchObject] Sketch021
  FullyConstrained = true
  sketch-geometry (7):
    g0: LineSegment StartX=0 StartY=0 StartZ=0 EndX=0 EndY=6 EndZ=0
    g1: Circle CenterX=0 CenterY=0 CenterZ=0 NormalX=0 NormalY=0 NormalZ=1 AngleXU=0 Radius=1
    g2: Circle CenterX=8 CenterY=6 CenterZ=0 NormalX=0 NormalY=0 NormalZ=1 AngleXU=0 Radius=1
    g3: BSplineCurve PolesCount=3 KnotsCount=2 Degree=2 IsPeriodic=0
    g4: GeomPoint X=0 Y=0 Z=0
    g5: GeomPoint X=8 Y=6 Z=0
    g6: LineSegment StartX=0 StartY=6 StartZ=0 EndX=8 EndY=6 EndZ=0
  constraints (14):
    c: Coincident(g0,g-1)
    c: Distance(g0) = 6
    c: Vertical(g0)
    c: Coincident(g3,g0)
    c: Weight(g1) = 1
    c: Equal(g1,g2)
    c: InternalAlignment(g1,g3)
    c: InternalAlignment(g2,g3)
    c: InternalAlignment(g4,g3)
    c: InternalAlignment(g5,g3)
    c: Block(g3)
    c: Coincident(g6,g0)
    c: Coincident(g6,g3)
    c: Horizontal(g6)
FEATURE [Part::Extrusion] Extrude015  label="caseScrewPillarBracket003"
  Base = -> Sketch021
  Dir = (0,0,1)
  DirMode = 2
  FaceMakerClass = Part::FaceMakerBullseye
  LengthFwd = 2.4
  LengthRev = 0
  Placement = pos=(11.3,29,58.74) rot=(0,1,0;1.5708rad)
  Solid = true
  Symmetric = false
FEATURE [Sketcher::SketchObject] Sketch022
  FullyConstrained = true
  sketch-geometry (7):
    g0: LineSegment StartX=0 StartY=0 StartZ=0 EndX=0 EndY=6 EndZ=0
    g1: Circle CenterX=0 CenterY=0 CenterZ=0 NormalX=0 NormalY=0 NormalZ=1 AngleXU=0 Radius=1
    g2: Circle CenterX=8 CenterY=6 CenterZ=0 NormalX=0 NormalY=0 NormalZ=1 AngleXU=0 Radius=1
    g3: BSplineCurve PolesCount=3 KnotsCount=2 Degree=2 IsPeriodic=0
    g4: GeomPoint X=0 Y=0 Z=0
    g5: GeomPoint X=8 Y=6 Z=0
    g6: LineSegment StartX=0 StartY=6 StartZ=0 EndX=8 EndY=6 EndZ=0
  constraints (14):
    c: Coincident(g0,g-1)
    c: Distance(g0) = 6
    c: Vertical(g0)
    c: Coincident(g3,g0)
    c: Weight(g1) = 1
    c: Equal(g1,g2)
    c: InternalAlignment(g1,g3)
    c: InternalAlignment(g2,g3)
    c: InternalAlignment(g4,g3)
    c: InternalAlignment(g5,g3)
    c: Block(g3)
    c: Coincident(g6,g0)
    c: Coincident(g6,g3)
    c: Horizontal(g6)
FEATURE [Part::Extrusion] Extrude016  label="caseScrewPillarBracket004"
  Base = -> Sketch022
  Dir = (0,0,1)
  DirMode = 2
  FaceMakerClass = Part::FaceMakerBullseye
  LengthFwd = 2.4
  LengthRev = 0
  Placement = pos=(88.3,29,65.23) rot=(0,1,0;1.5708rad)
  Solid = true
  Symmetric = false
FEATURE [Sketcher::SketchObject] Sketch023
  FullyConstrained = true
  sketch-geometry (7):
    g0: LineSegment StartX=0 StartY=0 StartZ=0 EndX=0 EndY=6 EndZ=0
    g1: Circle CenterX=0 CenterY=0 CenterZ=0 NormalX=0 NormalY=0 NormalZ=1 AngleXU=0 Radius=1
    g2: Circle CenterX=8 CenterY=6 CenterZ=0 NormalX=0 NormalY=0 NormalZ=1 AngleXU=0 Radius=1
    g3: BSplineCurve PolesCount=3 KnotsCount=2 Degree=2 IsPeriodic=0
    g4: GeomPoint X=0 Y=0 Z=0
    g5: GeomPoint X=8 Y=6 Z=0
    g6: LineSegment StartX=0 StartY=6 StartZ=0 EndX=8 EndY=6 EndZ=0
  constraints (14):
    c: Coincident(g0,g-1)
    c: Distance(g0) = 6
    c: Vertical(g0)
    c: Coincident(g3,g0)
    c: Weight(g1) = 1
    c: Equal(g1,g2)
    c: InternalAlignment(g1,g3)
    c: InternalAlignment(g2,g3)
    c: InternalAlignment(g4,g3)
    c: InternalAlignment(g5,g3)
    c: Block(g3)
    c: Coincident(g6,g0)
    c: Coincident(g6,g3)
    c: Horizontal(g6)
FEATURE [Part::Extrusion] Extrude017  label="caseScrewPillarBracket005"
  Base = -> Sketch023
  Dir = (0,0,1)
  DirMode = 2
  FaceMakerClass = Part::FaceMakerBullseye
  LengthFwd = 2.4
  LengthRev = 0
  Placement = pos=(90.7,29,6.77) rot=(0,-1,0;1.5708rad)
  Solid = true
  Symmetric = false
FEATURE [Sketcher::SketchObject] Sketch024
  FullyConstrained = true
  sketch-geometry (7):
    g0: LineSegment StartX=0 StartY=0 StartZ=0 EndX=0 EndY=6 EndZ=0
    g1: Circle CenterX=0 CenterY=0 CenterZ=0 NormalX=0 NormalY=0 NormalZ=1 AngleXU=0 Radius=1
    g2: Circle CenterX=8 CenterY=6 CenterZ=0 NormalX=0 NormalY=0 NormalZ=1 AngleXU=0 Radius=1
    g3: BSplineCurve PolesCount=3 KnotsCount=2 Degree=2 IsPeriodic=0
    g4: GeomPoint X=0 Y=0 Z=0
    g5: GeomPoint X=8 Y=6 Z=0
    g6: LineSegment StartX=0 StartY=6 StartZ=0 EndX=8 EndY=6 EndZ=0
  constraints (14):
    c: Coincident(g0,g-1)
    c: Distance(g0) = 6
    c: Vertical(g0)
    c: Coincident(g3,g0)
    c: Weight(g1) = 1
    c: Equal(g1,g2)
    c: InternalAlignment(g1,g3)
    c: InternalAlignment(g2,g3)
    c: InternalAlignment(g4,g3)
    c: InternalAlignment(g5,g3)
    c: Block(g3)
    c: Coincident(g6,g0)
    c: Coincident(g6,g3)
    c: Horizontal(g6)
FEATURE [Part::Extrusion] Extrude018  label="caseScrewPillarBracket006"
  Base = -> Sketch024
  Dir = (0,0,1)
  DirMode = 2
  FaceMakerClass = Part::FaceMakerBullseye
  LengthFwd = 2.4
  LengthRev = 0
  Placement = pos=(103.7,29,6.77) rot=(0,-1,0;1.5708rad)
  Solid = true
  Symmetric = false
FEATURE [Sketcher::SketchObject] Sketch025
  FullyConstrained = true
  sketch-geometry (7):
    g0: LineSegment StartX=0 StartY=0 StartZ=0 EndX=0 EndY=6 EndZ=0
    g1: Circle CenterX=0 CenterY=0 CenterZ=0 NormalX=0 NormalY=0 NormalZ=1 AngleXU=0 Radius=1
    g2: Circle CenterX=8 CenterY=6 CenterZ=0 NormalX=0 NormalY=0 NormalZ=1 AngleXU=0 Radius=1
    g3: BSplineCurve PolesCount=3 KnotsCount=2 Degree=2 IsPeriodic=0
    g4: GeomPoint X=0 Y=0 Z=0
    g5: GeomPoint X=8 Y=6 Z=0
    g6: LineSegment StartX=0 StartY=6 StartZ=0 EndX=8 EndY=6 EndZ=0
  constraints (14):
    c: Coincident(g0,g-1)
    c: Distance(g0) = 6
    c: Vertical(g0)
    c: Coincident(g3,g0)
    c: Weight(g1) = 1
    c: Equal(g1,g2)
    c: InternalAlignment(g1,g3)
    c: InternalAlignment(g2,g3)
    c: InternalAlignment(g4,g3)
    c: InternalAlignment(g5,g3)
    c: Block(g3)
    c: Coincident(g6,g0)
    c: Coincident(g6,g3)
    c: Horizontal(g6)
FEATURE [Part::Extrusion] Extrude019  label="caseScrewPillarBracket007"
  Base = -> Sketch025
  Dir = (0,0,1)
  DirMode = 2
  FaceMakerClass = Part::FaceMakerBullseye
  LengthFwd = 2.4
  LengthRev = 0
  Placement = pos=(101.3,29,65.23) rot=(0,1,0;1.5708rad)
  Solid = true
  Symmetric = false
FEATURE [Part::Box] Box011  label="frontCaseScrewPillarBracket"
  AttacherType = Attacher::AttachEngine3D
  Height = 2.4
  Length = 16
  Placement = pos=(87,28,2.3) rot=(0,0,1;0rad)
  Width = 7
FEATURE [Part::Box] Box012  label="frontCaseScrewPillarBracket001"
  AttacherType = Attacher::AttachEngine3D
  Height = 2.4
  Length = 16
  Placement = pos=(87,28,67.3) rot=(0,0,1;0rad)
  Width = 7
FEATURE [Sketcher::SketchObject] Sketch026
  FullyConstrained = true
  sketch-geometry (17):
    g0: Circle CenterX=-3.5 CenterY=23.5 CenterZ=0 NormalX=0 NormalY=0 NormalZ=1 AngleXU=0 Radius=1
    g1: Circle CenterX=-1 CenterY=15.25 CenterZ=0 NormalX=0 NormalY=0 NormalZ=1 AngleXU=0 Radius=1
    g2: Circle CenterX=-3.5 CenterY=7 CenterZ=0 NormalX=0 NormalY=0 NormalZ=1 AngleXU=0 Radius=1
    g3: BSplineCurve PolesCount=3 KnotsCount=2 Degree=2 IsPeriodic=0
    g4: GeomPoint X=-3.5 Y=23.5 Z=0
    g5: GeomPoint X=-3.5 Y=7 Z=0
    g6: Circle CenterX=-4.8 CenterY=30.5 CenterZ=0 NormalX=0 NormalY=0 NormalZ=1 AngleXU=0 Radius=1
    g7: Circle CenterX=-3.5 CenterY=30.5 CenterZ=0 NormalX=0 NormalY=0 NormalZ=1 AngleXU=0 Radius=1
    g8: Circle CenterX=-3.5 CenterY=29.2 CenterZ=0 NormalX=0 NormalY=0 NormalZ=1 AngleXU=0 Radius=1
    g9: BSplineCurve PolesCount=3 KnotsCount=2 Degree=2 IsPeriodic=0
    g10: GeomPoint X=-4.8 Y=30.5 Z=0
    g11: GeomPoint X=-3.5 Y=29.2 Z=0
    g12: LineSegment StartX=-3.5 StartY=29.2 StartZ=0 EndX=-3.5 EndY=23.5 EndZ=0
    g13: LineSegment StartX=-4.8 StartY=30.5 StartZ=0 EndX=0 EndY=30.5 EndZ=0
    g14: LineSegment StartX=-3.5 StartY=5 StartZ=0 EndX=-3.5 EndY=7 EndZ=0
    g15: LineSegment StartX=0 StartY=5 StartZ=0 EndX=0 EndY=30.5 EndZ=0
    g16: LineSegment StartX=-3.5 StartY=5 StartZ=0 EndX=0 EndY=5 EndZ=0
  constraints (33):
    c: Weight(g0) = 1
    c: Equal(g0,g1)
    c: Equal(g0,g2)
    c: InternalAlignment(g0,g3)
    c: InternalAlignment(g1,g3)
    c: InternalAlignment(g2,g3)
    c: InternalAlignment(g4,g3)
    c: InternalAlignment(g5,g3)
    c: Block(g3)
    c: Weight(g6) = 1
    c: Equal(g6,g7)
    c: Equal(g6,g8)
    c: InternalAlignment(g6,g9)
    c: InternalAlignment(g7,g9)
    c: InternalAlignment(g8,g9)
    c: InternalAlignment(g10,g9)
    c: InternalAlignment(g11,g9)
    c: Block(g9)
    c: Coincident(g12,g9)
    c: Coincident(g12,g3)
    c: Vertical(g12)
    c: Coincident(g13,g9)
    c: Horizontal(g13)
    c: Distance(g13) = 4.8
    c: Coincident(g14,g3)
    c: Vertical(g14)
    c: Coincident(g15,g13)
    c: Vertical(g15)
    c: Tangent(g15,g1)
    c: Distance(g14) = 2
    c: Coincident(g16,g14)
    c: Horizontal(g16)
    c: Coincident(g15,g16)
FEATURE [Part::Feature] Face050
  shape: bbox 4.8 x 25.5 x 2e-07 mm, 1 faces, 0 solids (baked)
FEATURE [Part::Revolution] Revolve054  label="moreFrontCaseScrewPost001"
  Angle = 360
  Axis = (0,1,0)
  Base = (0,0,0)
  FaceMakerClass = Part::FaceMakerBullseye
  Placement = pos=(102.5,4.5,3.5) rot=(0,0,1;0rad)
  Solid = false
  Source = -> Face050
  Symmetric = false
FEATURE [Part::Feature] Face051
  shape: bbox 4.8 x 25.5 x 2e-07 mm, 1 faces, 0 solids (baked)
FEATURE [Part::Revolution] Revolve055  label="moreFrontCaseScrewPost002"
  Angle = 360
  Axis = (0,1,0)
  Base = (0,0,0)
  FaceMakerClass = Part::FaceMakerBullseye
  Placement = pos=(102.5,4.5,68.5) rot=(0,0,1;0rad)
  Solid = false
  Source = -> Face051
  Symmetric = false
FEATURE [Sketcher::SketchObject] Sketch027
  FullyConstrained = true
  sketch-geometry (10):
    g0: LineSegment StartX=-1.6 StartY=4.7 StartZ=0 EndX=-1.6 EndY=1.7 EndZ=0
    g1: LineSegment StartX=-3.5 StartY=4.7 StartZ=0 EndX=-1.6 EndY=4.7 EndZ=0
    g2: LineSegment StartX=-1.6 StartY=1.7 StartZ=0 EndX=-1.6 EndY=1.5 EndZ=0
    g3: LineSegment StartX=-1.6 StartY=1.5 StartZ=0 EndX=-5.2 EndY=1.5 EndZ=0
    g4: Circle CenterX=-3.5 CenterY=4.7 CenterZ=0 NormalX=0 NormalY=0 NormalZ=1 AngleXU=0 Radius=1
    g5: Circle CenterX=-3.59627 CenterY=2.99743 CenterZ=0 NormalX=0 NormalY=0 NormalZ=1 AngleXU=0 Radius=1
    g6: Circle CenterX=-5.2 CenterY=1.5 CenterZ=0 NormalX=0 NormalY=0 NormalZ=1 AngleXU=0 Radius=1
    g7: BSplineCurve PolesCount=3 KnotsCount=2 Degree=2 IsPeriodic=0
    g8: GeomPoint X=-3.5 Y=4.7 Z=0
    g9: GeomPoint X=-5.2 Y=1.5 Z=0
  constraints (23):
    c: Vertical(g0)
    c: Distance(g0) = 3
    c: Coincident(g1,g0)
    c: Horizontal(g1)
    c: Block(g0)
    c: Block(g1)
    c: Coincident(g2,g0)
    c: Vertical(g2)
    c: Distance(g2) = 0.2
    c: Coincident(g3,g2)
    c: Horizontal(g3)
    c: Block(g3)
    c: Coincident(g7,g1)
    c: Weight(g4) = 1
    c: Equal(g4,g5)
    c: Equal(g4,g6)
    c: Coincident(g7,g3)
    c: InternalAlignment(g4,g7)
    c: InternalAlignment(g5,g7)
    c: InternalAlignment(g6,g7)
    c: InternalAlignment(g8,g7)
    c: InternalAlignment(g9,g7)
    c: Block(g7)
FEATURE [Sketcher::SketchObject] Sketch028
  FullyConstrained = true
  sketch-geometry (18):
    g0: LineSegment StartX=0 StartY=3e-16 StartZ=0 EndX=0 EndY=1.7 EndZ=0
    g1: LineSegment StartX=-3.5 StartY=0 StartZ=0 EndX=-3.5 EndY=0.9 EndZ=0
    g2: Circle CenterX=-2.7 CenterY=1.7 CenterZ=0 NormalX=0 NormalY=0 NormalZ=1 AngleXU=0 Radius=1
    g3: Circle CenterX=-3.5 CenterY=1.7 CenterZ=0 NormalX=0 NormalY=0 NormalZ=1 AngleXU=0 Radius=1
    g4: Circle CenterX=-3.5 CenterY=0.9 CenterZ=0 NormalX=0 NormalY=0 NormalZ=1 AngleXU=0 Radius=1
    g5: BSplineCurve PolesCount=3 KnotsCount=2 Degree=2 IsPeriodic=0
    g6: GeomPoint X=-2.7 Y=1.7 Z=0
    g7: GeomPoint X=-3.5 Y=0.9 Z=0
    g8: LineSegment StartX=-3.5 StartY=0 StartZ=0 EndX=-3.5 EndY=-7 EndZ=0
    g9: LineSegment StartX=0 StartY=3e-16 StartZ=0 EndX=0 EndY=-7 EndZ=0
    g10: LineSegment StartX=-3.5 StartY=-7 StartZ=0 EndX=0 EndY=-7 EndZ=0
    g11: LineSegment StartX=-2.7 StartY=1.7 StartZ=0 EndX=-1.6 EndY=1.7 EndZ=0
    g12: LineSegment StartX=0 StartY=1.7 StartZ=0 EndX=0 EndY=4.5 EndZ=0
    g13: LineSegment StartX=0 StartY=4.5 StartZ=0 EndX=0 EndY=10.8 EndZ=0
    g14: LineSegment StartX=0 StartY=10.8 StartZ=0 EndX=-2 EndY=10.8 EndZ=0
    g15: LineSegment StartX=-1.6 StartY=4.7 StartZ=0 EndX=-1.6 EndY=1.7 EndZ=0
    g16: LineSegment StartX=-1.6 StartY=4.7 StartZ=0 EndX=-2 EndY=4.7 EndZ=0
    g17: LineSegment StartX=-2 StartY=4.7 StartZ=0 EndX=-2 EndY=10.8 EndZ=0
  constraints (44):
    c: Vertical(g0)
    c: Vertical(g1)
    c: Distance(g1) = 0.9
    c: Block(g0)
    c: Distance(g0) = 1.7
    c: Weight(g2) = 1
    c: Equal(g2,g3)
    c: Equal(g2,g4)
    c: Coincident(g5,g1)
    c: InternalAlignment(g2,g5)
    c: InternalAlignment(g3,g5)
    c: InternalAlignment(g4,g5)
    c: InternalAlignment(g6,g5)
    c: InternalAlignment(g7,g5)
    c: Block(g5)
    c: Coincident(g8,g1)
    c: Vertical(g8)
    c: Distance(g8) = 7
    c: Vertical(g9)
    c: Equal(g8,g9) = 7
    c: Coincident(g9,g0)
    c: Coincident(g10,g8)
    c: Coincident(g10,g9)
    c: Horizontal(g10)
    c: Coincident(g11,g5)
    c: Horizontal(g11)
    c: Coincident(g12,g0)
    c: Vertical(g12)
    c: Distance(g12) = 2.8
    c: Coincident(g13,g12)
    c: Vertical(g13)
    c: Distance(g13) = 6.3
    c: Coincident(g14,g13)
    c: Horizontal(g14)
    c: Distance(g14) = 2
    c: Vertical(g15)
    c: Distance(g15) = 3
    c: Block(g11)
    c: Coincident(g15,g11)
    c: Coincident(g16,g15)
    c: Horizontal(g16)
    c: Coincident(g17,g16)
    c: Coincident(g17,g14)
    c: Vertical(g17)
FEATURE [Part::Revolution] Revolve040  label="backCaseScrewRetainer001"
  Angle = 360
  Axis = (0,1,0)
  Base = (0,0,0)
  FaceMakerClass = Part::FaceMakerBullseye
  Placement = pos=(12.5,3,10) rot=(0,0,1;0rad)
  Solid = false
  Source = -> Face036
  Symmetric = false
FEATURE [Part::Feature] Face055
  shape: bbox 3.5 x 30.2 x 2e-07 mm, 1 faces, 0 solids (baked)
FEATURE [Part::Revolution] Revolve059  label="backCaseScrewPost"
  Angle = 360
  Axis = (0,1,0)
  Base = (0,0,0)
  FaceMakerClass = Part::FaceMakerBullseye
  Placement = pos=(12.5,4.5,10) rot=(0,0,1;0rad)
  Solid = false
  Source = -> Face055
  Symmetric = false
FEATURE [Part::Feature] Face056
  shape: bbox 3.5 x 30.2 x 2e-07 mm, 1 faces, 0 solids (baked)
FEATURE [Part::Revolution] Revolve060  label="backCaseScrewPost001"
  Angle = 360
  Axis = (0,1,0)
  Base = (0,0,0)
  FaceMakerClass = Part::FaceMakerBullseye
  Placement = pos=(12.5,4.5,62) rot=(0,0,1;0rad)
  Solid = false
  Source = -> Face056
  Symmetric = false
FEATURE [Part::Feature] Face057
  shape: bbox 3.5 x 17.8 x 2e-07 mm, 1 faces, 0 solids (baked)
FEATURE [Part::Revolution] Revolve061  label="removeToCreateScrewAndThreadedInsertHole"
  Angle = 360
  Axis = (0,1,0)
  Base = (0,0,0)
  FaceMakerClass = Part::FaceMakerBullseye
  Placement = pos=(12.5,0,10) rot=(0,0,1;0rad)
  Solid = false
  Source = -> Face057
  Symmetric = false
FEATURE [Part::Feature] Face058
  shape: bbox 3.5 x 17.8 x 2e-07 mm, 1 faces, 0 solids (baked)
FEATURE [Part::Revolution] Revolve062  label="removeToCreateScrewAndThreadedInsertHole001"
  Angle = 360
  Axis = (0,1,0)
  Base = (0,0,0)
  FaceMakerClass = Part::FaceMakerBullseye
  Placement = pos=(12.5,0,62) rot=(0,0,1;0rad)
  Solid = false
  Source = -> Face058
  Symmetric = false
FEATURE [Part::Feature] Face059
  shape: bbox 3.5 x 17.8 x 2e-07 mm, 1 faces, 0 solids (baked)
FEATURE [Part::Revolution] Revolve063  label="removeToCreateScrewAndThreadedInsertHole002"
  Angle = 360
  Axis = (0,1,0)
  Base = (0,0,0)
  FaceMakerClass = Part::FaceMakerBullseye
  Placement = pos=(89.5,0,68.5) rot=(0,0,1;0rad)
  Solid = false
  Source = -> Face059
  Symmetric = false
FEATURE [Part::Feature] Face060
  shape: bbox 3.5 x 17.8 x 2e-07 mm, 1 faces, 0 solids (baked)
FEATURE [Part::Revolution] Revolve064  label="removeToCreateScrewAndThreadedInsertHole003"
  Angle = 360
  Axis = (0,1,0)
  Base = (0,0,0)
  FaceMakerClass = Part::FaceMakerBullseye
  Placement = pos=(89.5,0,3.5) rot=(0,0,1;0rad)
  Solid = false
  Source = -> Face060
  Symmetric = false
FEATURE [Part::Feature] Face061
  shape: bbox 3.5 x 17.8 x 2e-07 mm, 1 faces, 0 solids (baked)
FEATURE [Part::Revolution] Revolve065  label="removeToCreateScrewAndThreadedInsertHole004"
  Angle = 360
  Axis = (0,1,0)
  Base = (0,0,0)
  FaceMakerClass = Part::FaceMakerBullseye
  Placement = pos=(102.5,4.7,3.5) rot=(0,0,1;0rad)
  Solid = false
  Source = -> Face061
  Symmetric = false
FEATURE [Part::Feature] Face062
  shape: bbox 3.5 x 17.8 x 2e-07 mm, 1 faces, 0 solids (baked)
FEATURE [Part::Revolution] Revolve066  label="removeToCreateScrewAndThreadedInsertHole005"
  Angle = 360
  Axis = (0,1,0)
  Base = (0,0,0)
  FaceMakerClass = Part::FaceMakerBullseye
  Placement = pos=(102.5,4.7,68.5) rot=(0,0,1;0rad)
  Solid = false
  Source = -> Face062
  Symmetric = false
FEATURE [Part::MultiFuse] Fusion047  label="makeHoles"
  Shapes = -> [Revolve066,Revolve065,Revolve064,Revolve063,Revolve062,Revolve061]
FEATURE [Part::Feature] Face063
  shape: bbox 3.6 x 3.2 x 2e-07 mm, 1 faces, 0 solids (baked)
FEATURE [Part::Revolution] Revolve067  label="moreFrontCaseScrewRetainer002"
  Angle = 360
  Axis = (0,1,0)
  Base = (0,0,0)
  FaceMakerClass = Part::FaceMakerBullseye
  Placement = pos=(102.5,4.5,68.5) rot=(0,0,1;0rad)
  Solid = false
  Source = -> Face063
  Symmetric = false
FEATURE [Part::Feature] Face064
  shape: bbox 3.6 x 3.2 x 2e-07 mm, 1 faces, 0 solids (baked)
FEATURE [Part::Revolution] Revolve068  label="moreFrontCaseScrewRetainer003"
  Angle = 360
  Axis = (0,1,0)
  Base = (0,0,0)
  FaceMakerClass = Part::FaceMakerBullseye
  Placement = pos=(102.5,4.5,3.5) rot=(0,0,1;0rad)
  Solid = false
  Source = -> Face064
  Symmetric = false
FEATURE [Part::Feature] Face065
  shape: bbox 3.5 x 17.8 x 2e-07 mm, 1 faces, 0 solids (baked)
FEATURE [Part::Revolution] Revolve069  label="removeToCreateScrewAndThreadedInsertHole006"
  Angle = 360
  Axis = (0,1,0)
  Base = (0,0,0)
  FaceMakerClass = Part::FaceMakerBullseye
  Placement = pos=(12.5,0,10) rot=(0,0,1;0rad)
  Solid = false
  Source = -> Face065
  Symmetric = false
FEATURE [Part::Feature] Face066
  shape: bbox 3.5 x 17.8 x 2e-07 mm, 1 faces, 0 solids (baked)
FEATURE [Part::Revolution] Revolve070  label="removeToCreateScrewAndThreadedInsertHole007"
  Angle = 360
  Axis = (0,1,0)
  Base = (0,0,0)
  FaceMakerClass = Part::FaceMakerBullseye
  Placement = pos=(12.5,0,62) rot=(0,0,1;0rad)
  Solid = false
  Source = -> Face066
  Symmetric = false
FEATURE [Part::Feature] Face067
  shape: bbox 3.5 x 17.8 x 2e-07 mm, 1 faces, 0 solids (baked)
FEATURE [Part::Revolution] Revolve071  label="removeToCreateScrewAndThreadedInsertHole008"
  Angle = 360
  Axis = (0,1,0)
  Base = (0,0,0)
  FaceMakerClass = Part::FaceMakerBullseye
  Placement = pos=(89.5,0,68.5) rot=(0,0,1;0rad)
  Solid = false
  Source = -> Face067
  Symmetric = false
FEATURE [Part::Feature] Face068
  shape: bbox 3.5 x 17.8 x 2e-07 mm, 1 faces, 0 solids (baked)
FEATURE [Part::Revolution] Revolve072  label="removeToCreateScrewAndThreadedInsertHole009"
  Angle = 360
  Axis = (0,1,0)
  Base = (0,0,0)
  FaceMakerClass = Part::FaceMakerBullseye
  Placement = pos=(89.5,0,3.5) rot=(0,0,1;0rad)
  Solid = false
  Source = -> Face068
  Symmetric = false
FEATURE [Part::Feature] Face069
  shape: bbox 3.5 x 17.8 x 2e-07 mm, 1 faces, 0 solids (baked)
FEATURE [Part::Feature] Face070
  shape: bbox 3.5 x 17.8 x 2e-07 mm, 1 faces, 0 solids (baked)
FEATURE [Part::Revolution] Revolve073  label="removeToCreateScrewAndThreadedInsertHole010"
  Angle = 360
  Axis = (0,1,0)
  Base = (0,0,0)
  FaceMakerClass = Part::FaceMakerBullseye
  Placement = pos=(102.5,4.7,3.5) rot=(0,0,1;0rad)
  Solid = false
  Source = -> Face069
  Symmetric = false
FEATURE [Part::Revolution] Revolve074  label="removeToCreateScrewAndThreadedInsertHole011"
  Angle = 360
  Axis = (0,1,0)
  Base = (0,0,0)
  FaceMakerClass = Part::FaceMakerBullseye
  Placement = pos=(102.5,4.7,68.5) rot=(0,0,1;0rad)
  Solid = false
  Source = -> Face070
  Symmetric = false
FEATURE [Part::MultiFuse] Fusion048  label="makeHoles001"
  Shapes = -> [Revolve074,Revolve073,Revolve072,Revolve071,Revolve070,Revolve069]
FEATURE [Part::MultiFuse] Fusion049  label="caseScrewRetainers"
  Shapes = -> [Revolve067,Revolve068,Revolve048,Revolve047,Revolve039,Revolve040]
FEATURE [Part::Cut] Cut015  label="caseScrewRetainers001"
  Base = -> Fusion049
  Tool = -> Fusion048
FEATURE [Part::MultiFuse] Fusion050  label="casePillars"
  Shapes = -> [Revolve055,Revolve054,Revolve043,Revolve046,Revolve059,Revolve060]
FEATURE [Part::Feature] Face071 .. Face076  x6 (patterned run collapsed; names and placements below)
  shape: bbox 3.5 x 17.8 x 2e-07 mm, 1 faces, 0 solids (baked)
FEATURE [Part::Revolution] Revolve075  label="removeToCreateScrewAndThreadedInsertHole012"
  Angle = 360
  Axis = (0,1,0)
  Base = (0,0,0)
  FaceMakerClass = Part::FaceMakerBullseye
  Placement = pos=(12.5,0,10) rot=(0,0,1;0rad)
  Solid = false
  Source = -> Face071
  Symmetric = false
FEATURE [Part::Revolution] Revolve076  label="removeToCreateScrewAndThreadedInsertHole013"
  Angle = 360
  Axis = (0,1,0)
  Base = (0,0,0)
  FaceMakerClass = Part::FaceMakerBullseye
  Placement = pos=(12.5,0,62) rot=(0,0,1;0rad)
  Solid = false
  Source = -> Face072
  Symmetric = false
FEATURE [Part::Revolution] Revolve077  label="removeToCreateScrewAndThreadedInsertHole014"
  Angle = 360
  Axis = (0,1,0)
  Base = (0,0,0)
  FaceMakerClass = Part::FaceMakerBullseye
  Placement = pos=(89.5,0,68.5) rot=(0,0,1;0rad)
  Solid = false
  Source = -> Face073
  Symmetric = false
FEATURE [Part::Revolution] Revolve078  label="removeToCreateScrewAndThreadedInsertHole015"
  Angle = 360
  Axis = (0,1,0)
  Base = (0,0,0)
  FaceMakerClass = Part::FaceMakerBullseye
  Placement = pos=(89.5,0,3.5) rot=(0,0,1;0rad)
  Solid = false
  Source = -> Face074
  Symmetric = false
FEATURE [Part::Revolution] Revolve079  label="removeToCreateScrewAndThreadedInsertHole016"
  Angle = 360
  Axis = (0,1,0)
  Base = (0,0,0)
  FaceMakerClass = Part::FaceMakerBullseye
  Placement = pos=(102.5,4.7,3.5) rot=(0,0,1;0rad)
  Solid = false
  Source = -> Face075
  Symmetric = false
FEATURE [Part::Revolution] Revolve080  label="removeToCreateScrewAndThreadedInsertHole017"
  Angle = 360
  Axis = (0,1,0)
  Base = (0,0,0)
  FaceMakerClass = Part::FaceMakerBullseye
  Placement = pos=(102.5,4.7,68.5) rot=(0,0,1;0rad)
  Solid = false
  Source = -> Face076
  Symmetric = false
FEATURE [Part::MultiFuse] Fusion051  label="makeHoles002"
  Shapes = -> [Revolve080,Revolve079,Revolve078,Revolve077,Revolve076,Revolve075]
FEATURE [Part::Cut] Cut016  label="caesPillars"
  Base = -> Fusion050
  Tool = -> Fusion051
FEATURE [Part::Revolution] Revolve009  label="plugHousing016"
  Angle = 360
  Axis = (0,1,0)
  Base = (0,0,0)
  FaceMakerClass = Part::FaceMakerBullseye
  Placement = pos=(0,0,36.15) rot=(0,0,1;0rad)
  Solid = false
  Source = -> Face012
  Symmetric = false
FEATURE [Part::MultiFuse] Fusion014  label="plugHousing023"
  Placement = pos=(0,0,0) rot=(0,0,1;1.5708rad)
  Shapes = -> [Revolve011,Revolve009]
FEATURE [Part::Revolution] Revolve010  label="plugHousing017"
  Angle = 360
  Axis = (0,1,0)
  Base = (0,0,0)
  FaceMakerClass = Part::FaceMakerBullseye
  Placement = pos=(0,0,36.15) rot=(0,0,1;0rad)
  Solid = false
  Source = -> Face014
  Symmetric = false
FEATURE [Part::MultiFuse] Fusion015  label="plugHousing024"
  Placement = pos=(0,0,0) rot=(0,0,1;1.5708rad)
  Shapes = -> [Revolve010,Revolve015]
FEATURE [Part::Revolution] Revolve014  label="plugHousing026"
  Angle = 360
  Axis = (0,1,0)
  Base = (0,0,0)
  FaceMakerClass = Part::FaceMakerBullseye
  Placement = pos=(0,0,36.15) rot=(0,0,1;0rad)
  Solid = false
  Source = -> Face011
  Symmetric = false
FEATURE [Part::Revolution] Revolve013  label="plugHousing025"
  Angle = 360
  Axis = (0,1,0)
  Base = (0,0,0)
  FaceMakerClass = Part::FaceMakerBullseye
  Placement = pos=(0,0,36.15) rot=(0,0,1;0rad)
  Solid = false
  Source = -> Face015
  Symmetric = false
FEATURE [Part::MultiFuse] Fusion016  label="plugHousing028"
  Placement = pos=(0,19,0) rot=(0,0,1;3.14159rad)
  Shapes = -> [Fusion014,Fusion013]
FEATURE [Part::MultiFuse] Fusion011  label="plugHousing018"
  Placement = pos=(0,0,0) rot=(0,0,1;1.5708rad)
  Shapes = -> [Revolve014,Revolve013]
FEATURE [Part::MultiFuse] Fusion012  label="plugHousing019"
  Placement = pos=(0,19,0) rot=(0,0,1;3.14159rad)
  Shapes = -> [Fusion011,Fusion015]
FEATURE [Part::MultiFuse] Fusion017  label="plugHousing029"
  Placement = pos=(122.621,0,-0.15) rot=(0,0,1;0rad)
  Shapes = -> [Fusion016,Fusion012]
FEATURE [Part::MultiFuse] Fusion052  label="casePillarRetainers"
  Shapes = -> [Extrude012,Extrude013,Extrude014,Extrude015,Extrude016,Extrude017,Extrude018,Extrude019,Box011,Box012]
FEATURE [Part::Feature] Face077
  shape: bbox 3.5 x 17.8 x 2e-07 mm, 1 faces, 0 solids (baked)
FEATURE [Part::Revolution] Revolve081  label="removeToCreateScrewAndThreadedInsertHole018"
  Angle = 360
  Axis = (0,1,0)
  Base = (0,0,0)
  FaceMakerClass = Part::FaceMakerBullseye
  Placement = pos=(62.3,30.3,19.7) rot=(0,0,1;0rad)
  Solid = false
  Source = -> Face077
  Symmetric = false
FEATURE [Part::Feature] Face078
  shape: bbox 3.5 x 17.8 x 2e-07 mm, 1 faces, 0 solids (baked)
FEATURE [Part::Revolution] Revolve082  label="removeToCreateScrewAndThreadedInsertHole019"
  Angle = 360
  Axis = (0,1,0)
  Base = (0,0,0)
  FaceMakerClass = Part::FaceMakerBullseye
  Placement = pos=(62.3,30.3,51.7) rot=(0,0,1;0rad)
  Solid = false
  Source = -> Face078
  Symmetric = false
FEATURE [Part::Feature] Face079
  shape: bbox 3.5 x 17.8 x 2e-07 mm, 1 faces, 0 solids (baked)
FEATURE [Part::Revolution] Revolve083  label="removeToCreateScrewAndThreadedInsertHole020"
  Angle = 360
  Axis = (0,1,0)
  Base = (0,0,0)
  FaceMakerClass = Part::FaceMakerBullseye
  Placement = pos=(30.3,30.3,19.7) rot=(0,0,1;0rad)
  Solid = false
  Source = -> Face079
  Symmetric = false
FEATURE [Part::Feature] Face080
  shape: bbox 3.5 x 17.8 x 2e-07 mm, 1 faces, 0 solids (baked)
FEATURE [Part::Revolution] Revolve084  label="removeToCreateScrewAndThreadedInsertHole021"
  Angle = 360
  Axis = (0,1,0)
  Base = (0,0,0)
  FaceMakerClass = Part::FaceMakerBullseye
  Placement = pos=(30.3,30.3,51.7) rot=(0,0,1;0rad)
  Solid = false
  Source = -> Face080
  Symmetric = false
FEATURE [Part::MultiFuse] Fusion053  label="createThreadedInsertHolesForFan"
  Shapes = -> [Revolve081,Revolve082,Revolve083,Revolve084]
FEATURE [Part::Cut] Cut017  label="fanScrewHousing001"
  Base = -> Fusion046
  Tool = -> Fusion053
FEATURE [Part::Feature] Face081
  shape: bbox 3.5 x 17.8 x 2e-07 mm, 1 faces, 0 solids (baked)
FEATURE [Part::Revolution] Revolve085  label="removeToCreateScrewAndThreadedInsertHole022"
  Angle = 360
  Axis = (0,1,0)
  Base = (0,0,0)
  FaceMakerClass = Part::FaceMakerBullseye
  Placement = pos=(62.3,30.3,19.7) rot=(0,0,1;0rad)
  Solid = false
  Source = -> Face081
  Symmetric = false
FEATURE [Part::Feature] Face082
  shape: bbox 3.5 x 17.8 x 2e-07 mm, 1 faces, 0 solids (baked)
FEATURE [Part::Revolution] Revolve086  label="removeToCreateScrewAndThreadedInsertHole023"
  Angle = 360
  Axis = (0,1,0)
  Base = (0,0,0)
  FaceMakerClass = Part::FaceMakerBullseye
  Placement = pos=(62.3,30.3,51.7) rot=(0,0,1;0rad)
  Solid = false
  Source = -> Face082
  Symmetric = false
FEATURE [Part::Feature] Face083
  shape: bbox 3.5 x 17.8 x 2e-07 mm, 1 faces, 0 solids (baked)
FEATURE [Part::Revolution] Revolve087  label="removeToCreateScrewAndThreadedInsertHole024"
  Angle = 360
  Axis = (0,1,0)
  Base = (0,0,0)
  FaceMakerClass = Part::FaceMakerBullseye
  Placement = pos=(30.3,30.3,19.7) rot=(0,0,1;0rad)
  Solid = false
  Source = -> Face083
  Symmetric = false
FEATURE [Part::Feature] Face084
  shape: bbox 3.5 x 17.8 x 2e-07 mm, 1 faces, 0 solids (baked)
FEATURE [Part::Revolution] Revolve088  label="removeToCreateScrewAndThreadedInsertHole025"
  Angle = 360
  Axis = (0,1,0)
  Base = (0,0,0)
  FaceMakerClass = Part::FaceMakerBullseye
  Placement = pos=(30.3,30.3,51.7) rot=(0,0,1;0rad)
  Solid = false
  Source = -> Face084
  Symmetric = false
FEATURE [Part::MultiFuse] Fusion054  label="createThreadedInsertHolesForFan001"
  Shapes = -> [Revolve085,Revolve086,Revolve087,Revolve088]
FEATURE [Part::Cut] Cut018  label="top007"
  Base = -> Fusion040
  Tool = -> Fusion054
FEATURE [Sketcher::SketchObject] Sketch029
  FullyConstrained = false
  Placement = pos=(0,0,0) rot=(1,0,0;1.5708rad)
  sketch-geometry (24):
    g0: ArcOfCircle CenterX=-4 CenterY=-10.5 CenterZ=0 NormalX=0 NormalY=0 NormalZ=1 AngleXU=0 Radius=1.5 StartAngle=6e-16 EndAngle=3.14159
    g1: ArcOfCircle CenterX=-34.2 CenterY=-10.5 CenterZ=0 NormalX=0 NormalY=0 NormalZ=1 AngleXU=0 Radius=1.5 StartAngle=0 EndAngle=3.14159
    g2: ArcOfCircle CenterX=-34.2 CenterY=-27.7 CenterZ=0 NormalX=0 NormalY=0 NormalZ=1 AngleXU=0 Radius=1.5 StartAngle=3.14159 EndAngle=6.28319
    g3: ArcOfCircle CenterX=-4 CenterY=-27.7 CenterZ=0 NormalX=0 NormalY=0 NormalZ=1 AngleXU=0 Radius=1.5 StartAngle=3.1416 EndAngle=6.28319
    g4: ArcOfCircle CenterX=-10 CenterY=-4.3 CenterZ=0 NormalX=0 NormalY=0 NormalZ=1 AngleXU=0 Radius=1.5 StartAngle=2e-16 EndAngle=3.14159
    g5: ArcOfCircle CenterX=-16.1 CenterY=-1.8 CenterZ=0 NormalX=0 NormalY=0 NormalZ=1 AngleXU=0 Radius=1.5 StartAngle=5e-16 EndAngle=3.14159
    g6: ArcOfCircle CenterX=-22.1 CenterY=-1.8 CenterZ=0 NormalX=0 NormalY=0 NormalZ=1 AngleXU=0 Radius=1.5 StartAngle=5e-16 EndAngle=3.14159
    g7: ArcOfCircle CenterX=-28.2 CenterY=-4.3 CenterZ=0 NormalX=0 NormalY=0 NormalZ=1 AngleXU=0 Radius=1.5 StartAngle=2e-16 EndAngle=3.14159
    g8: ArcOfCircle CenterX=-10 CenterY=-33.9 CenterZ=0 NormalX=0 NormalY=0 NormalZ=1 AngleXU=0 Radius=1.5 StartAngle=3.14159 EndAngle=6.28319
    g9: ArcOfCircle CenterX=-16.1 CenterY=-36.4 CenterZ=0 NormalX=0 NormalY=0 NormalZ=1 AngleXU=0 Radius=1.5 StartAngle=3.14159 EndAngle=6.28319
    g10: ArcOfCircle CenterX=-22.1 CenterY=-36.4 CenterZ=0 NormalX=0 NormalY=0 NormalZ=1 AngleXU=0 Radius=1.5 StartAngle=3.14159 EndAngle=6.28319
    g11: ArcOfCircle CenterX=-28.2 CenterY=-33.9 CenterZ=0 NormalX=0 NormalY=0 NormalZ=1 AngleXU=0 Radius=1.5 StartAngle=3.14159 EndAngle=6.28319
    g12: LineSegment StartX=-35.7 StartY=-10.5 StartZ=0 EndX=-35.7 EndY=-27.7 EndZ=0
    g13: LineSegment StartX=-32.7 StartY=-10.5 StartZ=0 EndX=-32.7 EndY=-27.7 EndZ=0
    g14: LineSegment StartX=-29.7 StartY=-33.9 StartZ=0 EndX=-29.7 EndY=-4.3 EndZ=0
    g15: LineSegment StartX=-26.7 StartY=-33.9 StartZ=0 EndX=-26.7 EndY=-4.3 EndZ=0
    g16: LineSegment StartX=-2.5 StartY=-10.5 StartZ=0 EndX=-2.5 EndY=-27.7 EndZ=0
    g17: LineSegment StartX=-8.5 StartY=-4.3 StartZ=0 EndX=-8.5 EndY=-33.9 EndZ=0
    g18: LineSegment StartX=-5.5 StartY=-10.5 StartZ=0 EndX=-5.5 EndY=-27.7 EndZ=0
    g19: LineSegment StartX=-11.5 StartY=-4.3 StartZ=0 EndX=-11.5 EndY=-33.9 EndZ=0
    g20: LineSegment StartX=-14.6 StartY=-1.8 StartZ=0 EndX=-14.6 EndY=-36.4 EndZ=0
    g21: LineSegment StartX=-17.6 StartY=-1.8 StartZ=0 EndX=-17.6 EndY=-36.4 EndZ=0
    g22: LineSegment StartX=-20.6 StartY=-36.4 StartZ=0 EndX=-20.6 EndY=-1.8 EndZ=0
    g23: LineSegment StartX=-23.6 StartY=-1.8 StartZ=0 EndX=-23.6 EndY=-36.4 EndZ=0
  constraints (48):
    c: Block(g0)
    c: Block(g1)
    c: Block(g2)
    c: Block(g3)
    c: Block(g4)
    c: Block(g5)
    c: Block(g6)
    c: Block(g7)
    c: Block(g8)
    c: Block(g9)
    c: Block(g10)
    c: Block(g11)
    c: Coincident(g12,g1)
    c: Coincident(g12,g2)
    c: Vertical(g12)
    c: Coincident(g13,g1)
    c: Coincident(g13,g2)
    c: Vertical(g13)
    c: Coincident(g14,g11)
    c: Coincident(g14,g7)
    c: Vertical(g14)
    c: Coincident(g15,g11)
    c: Coincident(g15,g7)
    c: Vertical(g15)
    c: Coincident(g16,g0)
    c: Coincident(g16,g3)
    c: Vertical(g16)
    c: Coincident(g17,g4)
    c: Coincident(g17,g8)
    c: Vertical(g17)
    c: Coincident(g18,g0)
    c: Coincident(g18,g3)
    c: Vertical(g18)
    c: Coincident(g19,g4)
    c: Coincident(g19,g8)
    c: Vertical(g19)
    c: Coincident(g20,g5)
    c: Coincident(g20,g9)
    c: Vertical(g20)
    c: Coincident(g21,g5)
    c: Coincident(g21,g9)
    c: Vertical(g21)
    c: Coincident(g22,g10)
    c: Coincident(g22,g6)
    c: Vertical(g22)
    c: Coincident(g23,g6)
    c: Coincident(g23,g10)
    c: Vertical(g23)
FEATURE [Part::Extrusion] Extrude020  label="removeToCreateFanGrillHoles"
  Base = -> Sketch029
  Dir = (0,-1,6e-16)
  DirMode = 2
  FaceMakerClass = Part::FaceMakerBullseye
  LengthFwd = 10
  LengthRev = 0
  Placement = pos=(65.4,44,54.82) rot=(0,0,1;0rad)
  Solid = true
  Symmetric = false
FEATURE [Part::MultiFuse] Fusion055  label="top008"
  Shapes = -> [Cut017,Cut018]
FEATURE [Part::Cut] Cut019  label="top009"
  Base = -> Fusion055
  Tool = -> Extrude020
FEATURE [App::MeasureDistance] Distance003  label="Distance: 71.95 mm"
  Distance = 71.9513
  P1 = (117,38,72)
  P2 = (117,38,0.0487319)
FEATURE [Sketcher::SketchObject] Sketch030
  FullyConstrained = true
  Placement = pos=(117,19,0) rot=(0.57735,0.57735,0.57735;2.0944rad)
  sketch-geometry (48):
    g0: LineSegment StartX=-49.19 StartY=69.25 StartZ=0 EndX=-49.19 EndY=66.25 EndZ=0
    g1: LineSegment StartX=-49.19 StartY=63.5 StartZ=0 EndX=-49.19 EndY=60.5 EndZ=0
    g2: LineSegment StartX=-49.19 StartY=57.75 StartZ=0 EndX=-49.19 EndY=54.75 EndZ=0
    g3: LineSegment StartX=-49.19 StartY=52 StartZ=0 EndX=-49.19 EndY=49 EndZ=0
    g4: LineSegment StartX=-49.19 StartY=46.25 StartZ=0 EndX=-49.19 EndY=43.25 EndZ=0
    g5: LineSegment StartX=-49.19 StartY=40.5 StartZ=0 EndX=-49.19 EndY=37.5 EndZ=0
    g6: LineSegment StartX=-49.19 StartY=34.5 StartZ=0 EndX=-49.19 EndY=31.5 EndZ=0
    g7: LineSegment StartX=-49.19 StartY=28.75 StartZ=0 EndX=-49.19 EndY=25.75 EndZ=0
    g8: LineSegment StartX=-49.19 StartY=23 StartZ=0 EndX=-49.19 EndY=20 EndZ=0
    g9: LineSegment StartX=-49.19 StartY=17.25 StartZ=0 EndX=-49.19 EndY=14.25 EndZ=0
    g10: LineSegment StartX=-49.19 StartY=11.5 StartZ=0 EndX=-49.19 EndY=8.5 EndZ=0
    g11: LineSegment StartX=-49.19 StartY=5.75 StartZ=0 EndX=-49.19 EndY=2.75 EndZ=0
    g12: ArcOfCircle CenterX=-1.5 CenterY=67.75 CenterZ=0 NormalX=0 NormalY=0 NormalZ=1 AngleXU=0 Radius=1.5 StartAngle=4.71239 EndAngle=7.85398
    g13: ArcOfCircle CenterX=-1.5 CenterY=62 CenterZ=0 NormalX=0 NormalY=0 NormalZ=1 AngleXU=0 Radius=1.5 StartAngle=4.71239 EndAngle=7.85398
    g14: ArcOfCircle CenterX=-1.5 CenterY=56.25 CenterZ=0 NormalX=0 NormalY=0 NormalZ=1 AngleXU=0 Radius=1.5 StartAngle=4.71239 EndAngle=7.85398
    g15: ArcOfCircle CenterX=-11.49 CenterY=50.5 CenterZ=0 NormalX=0 NormalY=0 NormalZ=1 AngleXU=0 Radius=1.5 StartAngle=4.71239 EndAngle=7.85398
    g16: ArcOfCircle CenterX=-16.28 CenterY=44.75 CenterZ=0 NormalX=0 NormalY=0 NormalZ=1 AngleXU=0 Radius=1.5 StartAngle=4.71239 EndAngle=7.85398
    g17: ArcOfCircle CenterX=-18.2337 CenterY=39 CenterZ=0 NormalX=0 NormalY=0 NormalZ=1 AngleXU=0 Radius=1.5 StartAngle=4.71485 EndAngle=7.85398
    g18: ArcOfCircle CenterX=-16.2837 CenterY=27.25 CenterZ=0 NormalX=0 NormalY=0 NormalZ=1 AngleXU=0 Radius=1.5 StartAngle=4.71485 EndAngle=7.85398
    g19: ArcOfCircle CenterX=-18.2337 CenterY=33 CenterZ=0 NormalX=0 NormalY=0 NormalZ=1 AngleXU=0 Radius=1.5 StartAngle=4.71485 EndAngle=7.85398
    g20: ArcOfCircle CenterX=-11.49 CenterY=21.5 CenterZ=0 NormalX=0 NormalY=0 NormalZ=1 AngleXU=0 Radius=1.5 StartAngle=4.71239 EndAngle=7.85398
    g21: ArcOfCircle CenterX=-1.5 CenterY=4.25 CenterZ=0 NormalX=0 NormalY=0 NormalZ=1 AngleXU=0 Radius=1.5 StartAngle=4.71239 EndAngle=7.85398
    g22: ArcOfCircle CenterX=-1.5 CenterY=10 CenterZ=0 NormalX=0 NormalY=0 NormalZ=1 AngleXU=0 Radius=1.5 StartAngle=4.71239 EndAngle=7.85398
    g23: ArcOfCircle CenterX=-1.5 CenterY=15.75 CenterZ=0 NormalX=0 NormalY=0 NormalZ=1 AngleXU=0 Radius=1.5 StartAngle=4.71239 EndAngle=7.85398
    g24: LineSegment StartX=-49.19 StartY=69.25 StartZ=0 EndX=-1.5 EndY=69.25 EndZ=0
    g25: LineSegment StartX=-49.19 StartY=66.25 StartZ=0 EndX=-1.5 EndY=66.25 EndZ=0
    g26: LineSegment StartX=-49.19 StartY=63.5 StartZ=0 EndX=-1.5 EndY=63.5 EndZ=0
    g27: LineSegment StartX=-49.19 StartY=60.5 StartZ=0 EndX=-1.5 EndY=60.5 EndZ=0
    g28: LineSegment StartX=-49.19 StartY=57.75 StartZ=0 EndX=-1.5 EndY=57.75 EndZ=0
    g29: LineSegment StartX=-49.19 StartY=54.75 StartZ=0 EndX=-1.5 EndY=54.75 EndZ=0
    g30: LineSegment StartX=-49.19 StartY=52 StartZ=0 EndX=-11.49 EndY=52 EndZ=0
    g31: LineSegment StartX=-49.19 StartY=49 StartZ=0 EndX=-11.49 EndY=49 EndZ=0
    g32: LineSegment StartX=-49.19 StartY=46.25 StartZ=0 EndX=-16.28 EndY=46.25 EndZ=0
    g33: LineSegment StartX=-49.19 StartY=43.25 StartZ=0 EndX=-16.28 EndY=43.25 EndZ=0
    g34: LineSegment StartX=-49.19 StartY=40.5 StartZ=0 EndX=-18.2337 EndY=40.5 EndZ=0
    g35: LineSegment StartX=-49.19 StartY=37.5 StartZ=0 EndX=-18.23 EndY=37.5 EndZ=0
    g36: LineSegment StartX=-49.19 StartY=34.5 StartZ=0 EndX=-18.2337 EndY=34.5 EndZ=0
    g37: LineSegment StartX=-49.19 StartY=31.5 StartZ=0 EndX=-18.23 EndY=31.5 EndZ=0
    g38: LineSegment StartX=-49.19 StartY=28.75 StartZ=0 EndX=-16.2837 EndY=28.75 EndZ=0
    g39: LineSegment StartX=-49.19 StartY=25.75 StartZ=0 EndX=-16.28 EndY=25.75 EndZ=0
    g40: LineSegment StartX=-49.19 StartY=23 StartZ=0 EndX=-11.49 EndY=23 EndZ=0
    g41: LineSegment StartX=-49.19 StartY=20 StartZ=0 EndX=-11.49 EndY=20 EndZ=0
    g42: LineSegment StartX=-49.19 StartY=17.25 StartZ=0 EndX=-1.5 EndY=17.25 EndZ=0
    g43: LineSegment StartX=-49.19 StartY=14.25 StartZ=0 EndX=-1.5 EndY=14.25 EndZ=0
    g44: LineSegment StartX=-49.19 StartY=11.5 StartZ=0 EndX=-1.5 EndY=11.5 EndZ=0
    g45: LineSegment StartX=-49.19 StartY=8.5 StartZ=0 EndX=-1.5 EndY=8.5 EndZ=0
    g46: LineSegment StartX=-49.19 StartY=5.75 StartZ=0 EndX=-1.5 EndY=5.75 EndZ=0
    g47: LineSegment StartX=-49.19 StartY=2.75 StartZ=0 EndX=-1.5 EndY=2.75 EndZ=0
  constraints (120):
    c: Vertical(g0)
    c: Distance(g0) = 3
    c: Block(g0)
    c: Vertical(g1)
    c: Distance(g1) = 3
    c: Vertical(g2)
    c: Equal(g0,g2) = 3
    c: Block(g2)
    c: Vertical(g3)
    c: Equal(g1,g3) = 3
    c: Vertical(g4)
    c: Equal(g0,g4) = 3
    c: Block(g4)
    c: Vertical(g5)
    c: Equal(g1,g5) = 3
    c: Vertical(g6)
    c: Equal(g0,g6) = 3
    c: Block(g6)
    c: Vertical(g7)
    c: Equal(g1,g7) = 3
    c: Vertical(g8)
    c: Equal(g0,g8) = 3
    c: Block(g8)
    c: Vertical(g9)
    c: Equal(g1,g9) = 3
    c: Vertical(g10)
    c: Equal(g0,g10) = 3
    c: Block(g10)
    c: Vertical(g11)
    c: Equal(g1,g11) = 3
    c: Block(g12)
    c: Block(g13)
    c: Block(g14)
    c: Block(g15)
    c: Block(g16)
    c: Block(g17)
    c: Block(g18)
    c: Block(g19)
    c: Block(g20)
    c: Block(g21)
    c: Block(g22)
    c: Block(g23)
    c: Block(g11)
    c: Block(g9)
    c: Block(g7)
    c: Block(g5)
    c: Block(g3)
    c: Block(g1)
    c: Coincident(g24,g0)
    c: Coincident(g24,g12)
    c: Horizontal(g24)
    c: Coincident(g25,g0)
    c: Coincident(g25,g12)
    c: Horizontal(g25)
    c: Coincident(g26,g1)
    c: Coincident(g26,g13)
    c: Horizontal(g26)
    c: Coincident(g27,g1)
    c: Coincident(g27,g13)
    c: Horizontal(g27)
    c: Coincident(g28,g2)
    c: Coincident(g28,g14)
    c: Horizontal(g28)
    c: Coincident(g29,g2)
    c: Coincident(g29,g14)
    c: Horizontal(g29)
    c: Coincident(g30,g3)
    c: Coincident(g30,g15)
    c: Horizontal(g30)
    c: Coincident(g31,g3)
    c: Coincident(g31,g15)
    c: Horizontal(g31)
    c: Coincident(g32,g4)
    c: Coincident(g32,g16)
    c: Horizontal(g32)
    c: Coincident(g33,g4)
    c: Coincident(g33,g16)
    c: Horizontal(g33)
    c: Coincident(g34,g5)
    c: Coincident(g34,g17)
    c: Horizontal(g34)
    c: Coincident(g35,g5)
    c: Coincident(g35,g17)
    c: Horizontal(g35)
    c: Coincident(g36,g6)
    c: Coincident(g36,g19)
    c: Horizontal(g36)
    c: Coincident(g37,g6)
    c: Coincident(g37,g19)
    c: Horizontal(g37)
    c: Coincident(g38,g7)
    c: Coincident(g38,g18)
    c: Horizontal(g38)
    c: Coincident(g39,g7)
    c: Coincident(g39,g18)
    c: Horizontal(g39)
    c: Coincident(g40,g8)
    c: Coincident(g40,g20)
    c: Horizontal(g40)
    c: Coincident(g41,g8)
    c: Coincident(g41,g20)
    c: Horizontal(g41)
    c: Coincident(g42,g9)
    c: Coincident(g42,g23)
    c: Horizontal(g42)
    c: Coincident(g43,g9)
    c: Coincident(g43,g23)
    c: Horizontal(g43)
    c: Coincident(g44,g10)
    c: Coincident(g44,g22)
    c: Horizontal(g44)
    c: Coincident(g45,g10)
    c: Coincident(g45,g22)
    c: Horizontal(g45)
    c: Coincident(g46,g11)
    c: Coincident(g46,g21)
    c: Horizontal(g46)
    c: Coincident(g47,g11)
    c: Coincident(g47,g21)
    c: Horizontal(g47)
FEATURE [Sketcher::SketchObject] Sketch031
  FullyConstrained = true
  Placement = pos=(117,19,0) rot=(0.57735,0.57735,0.57735;2.0944rad)
  sketch-geometry (24):
    g0: ArcOfCircle CenterX=-49.19 CenterY=67.75 CenterZ=0 NormalX=0 NormalY=0 NormalZ=1 AngleXU=0 Radius=1.5 StartAngle=1.5708 EndAngle=4.71239
    g1: ArcOfCircle CenterX=-49.19 CenterY=62 CenterZ=0 NormalX=0 NormalY=0 NormalZ=1 AngleXU=0 Radius=1.5 StartAngle=1.5708 EndAngle=4.71239
    g2: ArcOfCircle CenterX=-49.19 CenterY=56.25 CenterZ=0 NormalX=0 NormalY=0 NormalZ=1 AngleXU=0 Radius=1.5 StartAngle=1.5708 EndAngle=4.71239
    g3: ArcOfCircle CenterX=-49.19 CenterY=50.5 CenterZ=0 NormalX=0 NormalY=0 NormalZ=1 AngleXU=0 Radius=1.5 StartAngle=1.5708 EndAngle=4.71239
    g4: ArcOfCircle CenterX=-49.19 CenterY=44.75 CenterZ=0 NormalX=0 NormalY=0 NormalZ=1 AngleXU=0 Radius=1.5 StartAngle=1.5708 EndAngle=4.71239
    g5: ArcOfCircle CenterX=-49.19 CenterY=39 CenterZ=0 NormalX=0 NormalY=0 NormalZ=1 AngleXU=0 Radius=1.5 StartAngle=1.5708 EndAngle=4.71239
    g6: ArcOfCircle CenterX=-49.19 CenterY=33 CenterZ=0 NormalX=0 NormalY=0 NormalZ=1 AngleXU=0 Radius=1.5 StartAngle=1.5708 EndAngle=4.71239
    g7: ArcOfCircle CenterX=-49.19 CenterY=27.25 CenterZ=0 NormalX=0 NormalY=0 NormalZ=1 AngleXU=0 Radius=1.5 StartAngle=1.5708 EndAngle=4.71239
    g8: ArcOfCircle CenterX=-49.19 CenterY=21.5 CenterZ=0 NormalX=0 NormalY=0 NormalZ=1 AngleXU=0 Radius=1.5 StartAngle=1.5708 EndAngle=4.71239
    g9: ArcOfCircle CenterX=-49.19 CenterY=15.75 CenterZ=0 NormalX=0 NormalY=0 NormalZ=1 AngleXU=0 Radius=1.5 StartAngle=1.5708 EndAngle=4.71239
    g10: ArcOfCircle CenterX=-49.19 CenterY=10 CenterZ=0 NormalX=0 NormalY=0 NormalZ=1 AngleXU=0 Radius=1.5 StartAngle=1.5708 EndAngle=4.71239
    g11: ArcOfCircle CenterX=-49.19 CenterY=4.25 CenterZ=0 NormalX=0 NormalY=0 NormalZ=1 AngleXU=0 Radius=1.5 StartAngle=1.5708 EndAngle=4.71239
    g12: LineSegment StartX=-49.19 StartY=69.25 StartZ=0 EndX=-49.19 EndY=66.25 EndZ=0
    g13: LineSegment StartX=-49.19 StartY=63.5 StartZ=0 EndX=-49.19 EndY=60.5 EndZ=0
    g14: LineSegment StartX=-49.19 StartY=57.75 StartZ=0 EndX=-49.19 EndY=54.75 EndZ=0
    g15: LineSegment StartX=-49.19 StartY=52 StartZ=0 EndX=-49.19 EndY=49 EndZ=0
    g16: LineSegment StartX=-49.19 StartY=46.25 StartZ=0 EndX=-49.19 EndY=43.25 EndZ=0
    g17: LineSegment StartX=-49.19 StartY=40.5 StartZ=0 EndX=-49.19 EndY=37.5 EndZ=0
    g18: LineSegment StartX=-49.19 StartY=34.5 StartZ=0 EndX=-49.19 EndY=31.5 EndZ=0
    g19: LineSegment StartX=-49.19 StartY=28.75 StartZ=0 EndX=-49.19 EndY=25.75 EndZ=0
    g20: LineSegment StartX=-49.19 StartY=23 StartZ=0 EndX=-49.19 EndY=20 EndZ=0
    g21: LineSegment StartX=-49.19 StartY=17.25 StartZ=0 EndX=-49.19 EndY=14.25 EndZ=0
    g22: LineSegment StartX=-49.19 StartY=11.5 StartZ=0 EndX=-49.19 EndY=8.5 EndZ=0
    g23: LineSegment StartX=-49.19 StartY=5.75 StartZ=0 EndX=-49.19 EndY=2.75 EndZ=0
  constraints (48):
    c: Block(g0)
    c: Block(g1)
    c: Block(g2)
    c: Block(g3)
    c: Block(g4)
    c: Block(g5)
    c: Block(g6)
    c: Block(g7)
    c: Block(g8)
    c: Block(g9)
    c: Block(g10)
    c: Block(g11)
    c: Coincident(g12,g0)
    c: Coincident(g12,g0)
    c: Vertical(g12)
    c: Vertical(g13)
    c: Coincident(g13,g1)
    c: Vertical(g14)
    c: Coincident(g14,g2)
    c: Vertical(g15)
    c: Coincident(g15,g3)
    c: Vertical(g16)
    c: Coincident(g16,g4)
    c: Vertical(g17)
    c: Coincident(g17,g5)
    c: Vertical(g18)
    c: Coincident(g18,g6)
    c: Vertical(g19)
    c: Coincident(g19,g7)
    c: Vertical(g20)
    c: Coincident(g20,g8)
    c: Vertical(g21)
    c: Coincident(g21,g9)
    c: Vertical(g22)
    c: Coincident(g22,g10)
    c: Vertical(g23)
    c: Coincident(g23,g11)
    c: Block(g23)
    c: Block(g22)
    c: Block(g21)
    c: Block(g20)
    c: Block(g13)
    c: Block(g14)
    c: Block(g15)
    c: Block(g16)
    c: Block(g17)
    c: Block(g18)
    c: Block(g19)
FEATURE [Part::Extrusion] Extrude022
  Base = -> Sketch030
  Dir = (1,-2e-16,2e-16)
  DirMode = 2
  FaceMakerClass = Part::FaceMakerBullseye
  LengthFwd = 19
  LengthRev = 0
  Placement = pos=(-19,0,0) rot=(0,0,1;0rad)
  Solid = true
  Symmetric = false
FEATURE [Part::Fillet] Fillet022
  Base = -> Extrude022
  Edges = 24 edges r=1.49: [Edge6,Edge11,Edge18,Edge23,Edge30,Edge35,Edge42,Edge47,Edge54,Edge59,Edge66,Edge71,Edge78,Edge83,Edge90,Edge95,Edge102,Edge107,Edge114,Edge119,Edge126,Edge131,Edge138,Edge143]
FEATURE [Part::Cut] Cut020  label="top010"
  Base = -> Cut019
  Tool = -> Fillet022
FEATURE [Sketcher::SketchObject] Sketch032
  FullyConstrained = true
  Placement = pos=(117,19,0) rot=(0.57735,0.57735,0.57735;2.0944rad)
  sketch-geometry (48):
    g0: LineSegment StartX=-49.19 StartY=69.25 StartZ=0 EndX=-49.19 EndY=66.25 EndZ=0
    g1: LineSegment StartX=-49.19 StartY=63.5 StartZ=0 EndX=-49.19 EndY=60.5 EndZ=0
    g2: LineSegment StartX=-49.19 StartY=57.75 StartZ=0 EndX=-49.19 EndY=54.75 EndZ=0
    g3: LineSegment StartX=-49.19 StartY=52 StartZ=0 EndX=-49.19 EndY=49 EndZ=0
    g4: LineSegment StartX=-49.19 StartY=46.25 StartZ=0 EndX=-49.19 EndY=43.25 EndZ=0
    g5: LineSegment StartX=-49.19 StartY=40.5 StartZ=0 EndX=-49.19 EndY=37.5 EndZ=0
    g6: LineSegment StartX=-49.19 StartY=34.5 StartZ=0 EndX=-49.19 EndY=31.5 EndZ=0
    g7: LineSegment StartX=-49.19 StartY=28.75 StartZ=0 EndX=-49.19 EndY=25.75 EndZ=0
    g8: LineSegment StartX=-49.19 StartY=23 StartZ=0 EndX=-49.19 EndY=20 EndZ=0
    g9: LineSegment StartX=-49.19 StartY=17.25 StartZ=0 EndX=-49.19 EndY=14.25 EndZ=0
    g10: LineSegment StartX=-49.19 StartY=11.5 StartZ=0 EndX=-49.19 EndY=8.5 EndZ=0
    g11: LineSegment StartX=-49.19 StartY=5.75 StartZ=0 EndX=-49.19 EndY=2.75 EndZ=0
    g12: ArcOfCircle CenterX=-1.5 CenterY=67.75 CenterZ=0 NormalX=0 NormalY=0 NormalZ=1 AngleXU=0 Radius=1.5 StartAngle=4.71239 EndAngle=7.85398
    g13: ArcOfCircle CenterX=-1.5 CenterY=62 CenterZ=0 NormalX=0 NormalY=0 NormalZ=1 AngleXU=0 Radius=1.5 StartAngle=4.71239 EndAngle=7.85398
    g14: ArcOfCircle CenterX=-1.5 CenterY=56.25 CenterZ=0 NormalX=0 NormalY=0 NormalZ=1 AngleXU=0 Radius=1.5 StartAngle=4.71239 EndAngle=7.85398
    g15: ArcOfCircle CenterX=-11.49 CenterY=50.5 CenterZ=0 NormalX=0 NormalY=0 NormalZ=1 AngleXU=0 Radius=1.5 StartAngle=4.71239 EndAngle=7.85398
    g16: ArcOfCircle CenterX=-16.28 CenterY=44.75 CenterZ=0 NormalX=0 NormalY=0 NormalZ=1 AngleXU=0 Radius=1.5 StartAngle=4.71239 EndAngle=7.85398
    g17: ArcOfCircle CenterX=-18.2337 CenterY=39 CenterZ=0 NormalX=0 NormalY=0 NormalZ=1 AngleXU=0 Radius=1.5 StartAngle=4.71485 EndAngle=7.85398
    g18: ArcOfCircle CenterX=-16.2837 CenterY=27.25 CenterZ=0 NormalX=0 NormalY=0 NormalZ=1 AngleXU=0 Radius=1.5 StartAngle=4.71485 EndAngle=7.85398
    g19: ArcOfCircle CenterX=-18.2337 CenterY=33 CenterZ=0 NormalX=0 NormalY=0 NormalZ=1 AngleXU=0 Radius=1.5 StartAngle=4.71485 EndAngle=7.85398
    g20: ArcOfCircle CenterX=-11.49 CenterY=21.5 CenterZ=0 NormalX=0 NormalY=0 NormalZ=1 AngleXU=0 Radius=1.5 StartAngle=4.71239 EndAngle=7.85398
    g21: ArcOfCircle CenterX=-1.5 CenterY=4.25 CenterZ=0 NormalX=0 NormalY=0 NormalZ=1 AngleXU=0 Radius=1.5 StartAngle=4.71239 EndAngle=7.85398
    g22: ArcOfCircle CenterX=-1.5 CenterY=10 CenterZ=0 NormalX=0 NormalY=0 NormalZ=1 AngleXU=0 Radius=1.5 StartAngle=4.71239 EndAngle=7.85398
    g23: ArcOfCircle CenterX=-1.5 CenterY=15.75 CenterZ=0 NormalX=0 NormalY=0 NormalZ=1 AngleXU=0 Radius=1.5 StartAngle=4.71239 EndAngle=7.85398
    g24: LineSegment StartX=-49.19 StartY=69.25 StartZ=0 EndX=-1.5 EndY=69.25 EndZ=0
    g25: LineSegment StartX=-49.19 StartY=66.25 StartZ=0 EndX=-1.5 EndY=66.25 EndZ=0
    g26: LineSegment StartX=-49.19 StartY=63.5 StartZ=0 EndX=-1.5 EndY=63.5 EndZ=0
    g27: LineSegment StartX=-49.19 StartY=60.5 StartZ=0 EndX=-1.5 EndY=60.5 EndZ=0
    g28: LineSegment StartX=-49.19 StartY=57.75 StartZ=0 EndX=-1.5 EndY=57.75 EndZ=0
    g29: LineSegment StartX=-49.19 StartY=54.75 StartZ=0 EndX=-1.5 EndY=54.75 EndZ=0
    g30: LineSegment StartX=-49.19 StartY=52 StartZ=0 EndX=-11.49 EndY=52 EndZ=0
    g31: LineSegment StartX=-49.19 StartY=49 StartZ=0 EndX=-11.49 EndY=49 EndZ=0
    g32: LineSegment StartX=-49.19 StartY=46.25 StartZ=0 EndX=-16.28 EndY=46.25 EndZ=0
    g33: LineSegment StartX=-49.19 StartY=43.25 StartZ=0 EndX=-16.28 EndY=43.25 EndZ=0
    g34: LineSegment StartX=-49.19 StartY=40.5 StartZ=0 EndX=-18.2337 EndY=40.5 EndZ=0
    g35: LineSegment StartX=-49.19 StartY=37.5 StartZ=0 EndX=-18.23 EndY=37.5 EndZ=0
    g36: LineSegment StartX=-49.19 StartY=34.5 StartZ=0 EndX=-18.2337 EndY=34.5 EndZ=0
    g37: LineSegment StartX=-49.19 StartY=31.5 StartZ=0 EndX=-18.23 EndY=31.5 EndZ=0
    g38: LineSegment StartX=-49.19 StartY=28.75 StartZ=0 EndX=-16.2837 EndY=28.75 EndZ=0
    g39: LineSegment StartX=-49.19 StartY=25.75 StartZ=0 EndX=-16.28 EndY=25.75 EndZ=0
    g40: LineSegment StartX=-49.19 StartY=23 StartZ=0 EndX=-11.49 EndY=23 EndZ=0
    g41: LineSegment StartX=-49.19 StartY=20 StartZ=0 EndX=-11.49 EndY=20 EndZ=0
    g42: LineSegment StartX=-49.19 StartY=17.25 StartZ=0 EndX=-1.5 EndY=17.25 EndZ=0
    g43: LineSegment StartX=-49.19 StartY=14.25 StartZ=0 EndX=-1.5 EndY=14.25 EndZ=0
    g44: LineSegment StartX=-49.19 StartY=11.5 StartZ=0 EndX=-1.5 EndY=11.5 EndZ=0
    g45: LineSegment StartX=-49.19 StartY=8.5 StartZ=0 EndX=-1.5 EndY=8.5 EndZ=0
    g46: LineSegment StartX=-49.19 StartY=5.75 StartZ=0 EndX=-1.5 EndY=5.75 EndZ=0
    g47: LineSegment StartX=-49.19 StartY=2.75 StartZ=0 EndX=-1.5 EndY=2.75 EndZ=0
  constraints (120):
    c: Vertical(g0)
    c: Distance(g0) = 3
    c: Block(g0)
    c: Vertical(g1)
    c: Distance(g1) = 3
    c: Vertical(g2)
    c: Equal(g0,g2) = 3
    c: Block(g2)
    c: Vertical(g3)
    c: Equal(g1,g3) = 3
    c: Vertical(g4)
    c: Equal(g0,g4) = 3
    c: Block(g4)
    c: Vertical(g5)
    c: Equal(g1,g5) = 3
    c: Vertical(g6)
    c: Equal(g0,g6) = 3
    c: Block(g6)
    c: Vertical(g7)
    c: Equal(g1,g7) = 3
    c: Vertical(g8)
    c: Equal(g0,g8) = 3
    c: Block(g8)
    c: Vertical(g9)
    c: Equal(g1,g9) = 3
    c: Vertical(g10)
    c: Equal(g0,g10) = 3
    c: Block(g10)
    c: Vertical(g11)
    c: Equal(g1,g11) = 3
    c: Block(g12)
    c: Block(g13)
    c: Block(g14)
    c: Block(g15)
    c: Block(g16)
    c: Block(g17)
    c: Block(g18)
    c: Block(g19)
    c: Block(g20)
    c: Block(g21)
    c: Block(g22)
    c: Block(g23)
    c: Block(g11)
    c: Block(g9)
    c: Block(g7)
    c: Block(g5)
    c: Block(g3)
    c: Block(g1)
    c: Coincident(g24,g0)
    c: Coincident(g24,g12)
    c: Horizontal(g24)
    c: Coincident(g25,g0)
    c: Coincident(g25,g12)
    c: Horizontal(g25)
    c: Coincident(g26,g1)
    c: Coincident(g26,g13)
    c: Horizontal(g26)
    c: Coincident(g27,g1)
    c: Coincident(g27,g13)
    c: Horizontal(g27)
    c: Coincident(g28,g2)
    c: Coincident(g28,g14)
    c: Horizontal(g28)
    c: Coincident(g29,g2)
    c: Coincident(g29,g14)
    c: Horizontal(g29)
    c: Coincident(g30,g3)
    c: Coincident(g30,g15)
    c: Horizontal(g30)
    c: Coincident(g31,g3)
    c: Coincident(g31,g15)
    c: Horizontal(g31)
    c: Coincident(g32,g4)
    c: Coincident(g32,g16)
    c: Horizontal(g32)
    c: Coincident(g33,g4)
    c: Coincident(g33,g16)
    c: Horizontal(g33)
    c: Coincident(g34,g5)
    c: Coincident(g34,g17)
    c: Horizontal(g34)
    c: Coincident(g35,g5)
    c: Coincident(g35,g17)
    c: Horizontal(g35)
    c: Coincident(g36,g6)
    c: Coincident(g36,g19)
    c: Horizontal(g36)
    c: Coincident(g37,g6)
    c: Coincident(g37,g19)
    c: Horizontal(g37)
    c: Coincident(g38,g7)
    c: Coincident(g38,g18)
    c: Horizontal(g38)
    c: Coincident(g39,g7)
    c: Coincident(g39,g18)
    c: Horizontal(g39)
    c: Coincident(g40,g8)
    c: Coincident(g40,g20)
    c: Horizontal(g40)
    c: Coincident(g41,g8)
    c: Coincident(g41,g20)
    c: Horizontal(g41)
    c: Coincident(g42,g9)
    c: Coincident(g42,g23)
    c: Horizontal(g42)
    c: Coincident(g43,g9)
    c: Coincident(g43,g23)
    c: Horizontal(g43)
    c: Coincident(g44,g10)
    c: Coincident(g44,g22)
    c: Horizontal(g44)
    c: Coincident(g45,g10)
    c: Coincident(g45,g22)
    c: Horizontal(g45)
    c: Coincident(g46,g11)
    c: Coincident(g46,g21)
    c: Horizontal(g46)
    c: Coincident(g47,g11)
    c: Coincident(g47,g21)
    c: Horizontal(g47)
FEATURE [Part::Extrusion] Extrude023
  Base = -> Sketch032
  Dir = (1,-2e-16,2e-16)
  DirMode = 2
  FaceMakerClass = Part::FaceMakerBullseye
  LengthFwd = 19
  LengthRev = 0
  Placement = pos=(-19,0,0) rot=(0,0,1;0rad)
  Solid = true
  Symmetric = false
FEATURE [Part::Fillet] Fillet023
  Base = -> Extrude023
  Edges = <same value as first occurrence — deduplicated (x6 in doc)>
  Placement = pos=(0,0.05,0) rot=(0,0,1;0rad)
FEATURE [Part::Cut] Cut014  label="bottom003"
  Base = -> Cut007
  Tool = -> Fusion047
FEATURE [Part::Cut] Cut021  label="bottom004"
  Base = -> Cut014
  Tool = -> Fillet023
FEATURE [Sketcher::SketchObject] Sketch033
  FullyConstrained = true
  Placement = pos=(117,19,0) rot=(0.57735,0.57735,0.57735;2.0944rad)
  sketch-geometry (8):
    g0: LineSegment StartX=-49.19 StartY=69.25 StartZ=0 EndX=-49.19 EndY=66.25 EndZ=0
    g1: LineSegment StartX=-49.19 StartY=5.75 StartZ=0 EndX=-49.19 EndY=2.75 EndZ=0
    g2: ArcOfCircle CenterX=-1.5 CenterY=67.75 CenterZ=0 NormalX=0 NormalY=0 NormalZ=1 AngleXU=0 Radius=1.5 StartAngle=4.71239 EndAngle=7.85398
    g3: ArcOfCircle CenterX=-1.5 CenterY=4.25 CenterZ=0 NormalX=0 NormalY=0 NormalZ=1 AngleXU=0 Radius=1.5 StartAngle=4.71239 EndAngle=7.85398
    g4: LineSegment StartX=-49.19 StartY=69.25 StartZ=0 EndX=-1.5 EndY=69.25 EndZ=0
    g5: LineSegment StartX=-49.19 StartY=66.25 StartZ=0 EndX=-1.5 EndY=66.25 EndZ=0
    g6: LineSegment StartX=-49.19 StartY=5.75 StartZ=0 EndX=-1.5 EndY=5.75 EndZ=0
    g7: LineSegment StartX=-49.19 StartY=2.75 StartZ=0 EndX=-1.5 EndY=2.75 EndZ=0
  constraints (19):
    c: Vertical(g0)
    c: Distance(g0) = 3
    c: Block(g0)
    c: Vertical(g1)
    c: Block(g2)
    c: Block(g3)
    c: Block(g1)
    c: Coincident(g4,g0)
    c: Coincident(g4,g2)
    c: Horizontal(g4)
    c: Coincident(g5,g0)
    c: Coincident(g5,g2)
    c: Horizontal(g5)
    c: Coincident(g6,g1)
    c: Coincident(g6,g3)
    c: Horizontal(g6)
    c: Coincident(g7,g1)
    c: Coincident(g7,g3)
    c: Horizontal(g7)
FEATURE [Sketcher::SketchObject] Sketch034
  FullyConstrained = true
  Placement = pos=(117,19,0) rot=(0.57735,0.57735,0.57735;2.0944rad)
  sketch-geometry (8):
    g0: LineSegment StartX=-49.19 StartY=63.5 StartZ=0 EndX=-49.19 EndY=60.5 EndZ=0
    g1: LineSegment StartX=-49.19 StartY=11.5 StartZ=0 EndX=-49.19 EndY=8.5 EndZ=0
    g2: ArcOfCircle CenterX=-1.5 CenterY=62 CenterZ=0 NormalX=0 NormalY=0 NormalZ=1 AngleXU=0 Radius=1.5 StartAngle=4.71239 EndAngle=7.85398
    g3: ArcOfCircle CenterX=-1.5 CenterY=10 CenterZ=0 NormalX=0 NormalY=0 NormalZ=1 AngleXU=0 Radius=1.5 StartAngle=4.71239 EndAngle=7.85398
    g4: LineSegment StartX=-49.19 StartY=63.5 StartZ=0 EndX=-1.5 EndY=63.5 EndZ=0
    g5: LineSegment StartX=-49.19 StartY=60.5 StartZ=0 EndX=-1.5 EndY=60.5 EndZ=0
    g6: LineSegment StartX=-49.19 StartY=11.5 StartZ=0 EndX=-1.5 EndY=11.5 EndZ=0
    g7: LineSegment StartX=-49.19 StartY=8.5 StartZ=0 EndX=-1.5 EndY=8.5 EndZ=0
  constraints (19):
    c: Vertical(g0)
    c: Distance(g0) = 3
    c: Vertical(g1)
    c: Block(g1)
    c: Block(g2)
    c: Block(g3)
    c: Block(g0)
    c: Coincident(g4,g0)
    c: Coincident(g4,g2)
    c: Horizontal(g4)
    c: Coincident(g5,g0)
    c: Coincident(g5,g2)
    c: Horizontal(g5)
    c: Coincident(g6,g1)
    c: Coincident(g6,g3)
    c: Horizontal(g6)
    c: Coincident(g7,g1)
    c: Coincident(g7,g3)
    c: Horizontal(g7)
FEATURE [Part::Extrusion] Extrude024
  Base = -> Sketch033
  Dir = (1,0,0)
  DirMode = 2
  FaceMakerClass = Part::FaceMakerBullseye
  LengthFwd = 10
  LengthRev = 0
  Solid = true
  Symmetric = false
FEATURE [Part::Extrusion] Extrude025
  Base = -> Sketch034
  Dir = (1,0,0)
  DirMode = 2
  FaceMakerClass = Part::FaceMakerBullseye
  LengthFwd = 10
  LengthRev = 0
  Solid = true
  Symmetric = false
FEATURE [Part::Fillet] Fillet024  label="removeFromtMoreFrontCaseScrewRetainers"
  Base = -> Extrude024
  Edges = 4 edges r=1.49: [Edge6,Edge11,Edge18,Edge23]
  Placement = pos=(-11,0,0) rot=(0,0,1;0rad)
FEATURE [Part::Fillet] Fillet025  label="removeFromtMoreFrontCaseScrewRetainers001"
  Base = -> Extrude025
  Edges = 4 edges r=1.49: [Edge6,Edge11,Edge18,Edge23]
  Placement = pos=(-19,0,0) rot=(0,0,1;0rad)
FEATURE [Part::Cut] Cut022
  Base = -> Cut015
  Tool = -> Fillet025
FEATURE [Part::Cut] Cut023  label="screwRetainers"
  Base = -> Cut022
  Tool = -> Fillet024
FEATURE [Part::MultiFuse] Fusion056  label="bottom005"
  Shapes = -> [Fusion044,Cut021]
FEATURE [Part::MultiFuse] Fusion057  label="casePillars001"
  Shapes = -> [Cut016,Fusion052]
FEATURE [Part::MultiFuse] Fusion058  label="bottom006"
  Shapes = -> [Fusion056,Cut023]
FEATURE [Part::MultiFuse] Fusion059  label="bottom007"
  Shapes = -> [Fusion058,Fillet005]
FEATURE [Part::MultiFuse] Fusion060  label="bottom008"
  Shapes = -> [Fusion059,Fusion]
FEATURE [Part::MultiFuse] Fusion061  label="top011"
  Shapes = -> [Cut006,Cut020]
FEATURE [Part::MultiFuse] Fusion062  label="top012"
  Shapes = -> [Fusion057,Fusion061]
FEATURE [Sketcher::SketchObject] Sketch035  label="topSketch007"
  FullyConstrained = true
  sketch-geometry (6):
    g0: LineSegment StartX=19 StartY=38 StartZ=0 EndX=117 EndY=38 EndZ=0
    g1: ArcOfCircle CenterX=19 CenterY=19 CenterZ=0 NormalX=0 NormalY=0 NormalZ=1 AngleXU=0 Radius=19 StartAngle=1.5708 EndAngle=3.14159
    g2: LineSegment StartX=117 StartY=38 StartZ=0 EndX=117 EndY=19 EndZ=0
    g3: LineSegment StartX=98 StartY=1.0161e-12 StartZ=0 EndX=5.22862e-06 EndY=1.0161e-12 EndZ=0
    g4: LineSegment StartX=5.22862e-06 StartY=19 StartZ=0 EndX=5.22862e-06 EndY=1.0161e-12 EndZ=0
    g5: ArcOfCircle CenterX=98 CenterY=19 CenterZ=0 NormalX=0 NormalY=0 NormalZ=1 AngleXU=0 Radius=19 StartAngle=4.71239 EndAngle=6.28319
  constraints (16):
    c: Horizontal(g0)
    c: Distance(g0) = 98
    c: Coincident(g1,g0)
    c: Block(g1)
    c: Coincident(g2,g0)
    c: Vertical(g2)
    c: Distance(g2) = 19
    c: Horizontal(g3)
    c: Coincident(g4,g1)
    c: Vertical(g4)
    c: Coincident(g3,g4)
    c: Block(g3)
    c: Coincident(g5,g2)
    c: Coincident(g5,g3)
    c: Block(g0)
    c: Block(g5)
FEATURE [Part::Extrusion] Extrude026  label="sideA001"
  Base = -> Sketch035
  Dir = (0,0,1)
  DirMode = 2
  FaceMakerClass = Part::FaceMakerBullseye
  LengthFwd = 3
  LengthRev = 0
  Placement = pos=(0,0,-2.7) rot=(0,0,1;0rad)
  Solid = true
  Symmetric = false
FEATURE [Sketcher::SketchObject] Sketch036  label="topSketch008"
  FullyConstrained = true
  sketch-geometry (6):
    g0: LineSegment StartX=19 StartY=38 StartZ=0 EndX=117 EndY=38 EndZ=0
    g1: ArcOfCircle CenterX=19 CenterY=19 CenterZ=0 NormalX=0 NormalY=0 NormalZ=1 AngleXU=0 Radius=19 StartAngle=1.5708 EndAngle=3.14159
    g2: LineSegment StartX=117 StartY=38 StartZ=0 EndX=117 EndY=19 EndZ=0
    g3: LineSegment StartX=98 StartY=1.0161e-12 StartZ=0 EndX=5.22862e-06 EndY=1.0161e-12 EndZ=0
    g4: LineSegment StartX=5.22862e-06 StartY=19 StartZ=0 EndX=5.22862e-06 EndY=1.0161e-12 EndZ=0
    g5: ArcOfCircle CenterX=98 CenterY=19 CenterZ=0 NormalX=0 NormalY=0 NormalZ=1 AngleXU=0 Radius=19 StartAngle=4.71239 EndAngle=6.28319
  constraints (16):
    c: Horizontal(g0)
    c: Distance(g0) = 98
    c: Coincident(g1,g0)
    c: Block(g1)
    c: Coincident(g2,g0)
    c: Vertical(g2)
    c: Distance(g2) = 19
    c: Horizontal(g3)
    c: Coincident(g4,g1)
    c: Vertical(g4)
    c: Coincident(g3,g4)
    c: Block(g3)
    c: Coincident(g5,g2)
    c: Coincident(g5,g3)
    c: Block(g0)
    c: Block(g5)
FEATURE [Part::Extrusion] Extrude027  label="sideB001"
  Base = -> Sketch036
  Dir = (0,0,1)
  DirMode = 2
  FaceMakerClass = Part::FaceMakerBullseye
  LengthFwd = 3
  LengthRev = 0
  Placement = pos=(0,0,71.7) rot=(0,0,1;0rad)
  Solid = true
  Symmetric = false
FEATURE [Part::MultiFuse] Fusion064  label="removeFromBottom"
  Shapes = -> [Extrude026,Extrude027]
FEATURE [Part::Cut] Cut024  label="bottom009"
  Base = -> Fusion060
  Tool = -> Fusion064
FEATURE [Sketcher::SketchObject] Sketch037  label="topSketch009"
  FullyConstrained = true
  sketch-geometry (8):
    g0: ArcOfCircle CenterX=19 CenterY=19.1201 CenterZ=0 NormalX=0 NormalY=0 NormalZ=1 AngleXU=0 Radius=18.8799 StartAngle=1.5708 EndAngle=3.14793
    g1: LineSegment StartX=0.120501 StartY=19.0004 StartZ=0 EndX=0.120501 EndY=0.000382114 EndZ=0
    g2: LineSegment StartX=19 StartY=38 StartZ=0 EndX=124 EndY=38 EndZ=0
    g3: LineSegment StartX=0.120501 StartY=0.000382114 StartZ=0 EndX=105.121 EndY=0.000382114 EndZ=0
    g4: LineSegment StartX=124 StartY=38 StartZ=0 EndX=125.616 EndY=38 EndZ=0
    g5: LineSegment StartX=105.121 StartY=0.000382114 StartZ=0 EndX=106.736 EndY=0.000382114 EndZ=0
    g6: ArcOfCircle CenterX=106.616 CenterY=19 CenterZ=0 NormalX=0 NormalY=0 NormalZ=1 AngleXU=0 Radius=19 StartAngle=4.71873 EndAngle=6.28319
    g7: LineSegment StartX=125.616 StartY=38 StartZ=0 EndX=125.616 EndY=19 EndZ=0
  constraints (21):
    c: Block(g0)
    c: Coincident(g1,g0)
    c: Vertical(g1)
    c: Horizontal(g2)
    c: Distance(g2) = 105
    c: Coincident(g2,g0)
    c: Distance(g1) = 19
    c: Coincident(g3,g1)
    c: Horizontal(g3)
    c: Distance(g3) = 105
    c: Coincident(g4,g2)
    c: Horizontal(g4)
    c: Distance(g4) = 1.61553
    c: Horizontal(g5)
    c: Equal(g4,g5) = 1.61553
    c: Coincident(g5,g3)
    c: Block(g6)
    c: Coincident(g6,g5)
    c: Coincident(g7,g4)
    c: Coincident(g7,g6)
    c: Vertical(g7)
FEATURE [Part::Extrusion] Extrude028  label="sideB"
  Base = -> Sketch037
  Dir = (0,0,1)
  DirMode = 2
  FaceMakerClass = Part::FaceMakerBullseye
  LengthFwd = 3
  LengthRev = 0
  Placement = pos=(0,0,72) rot=(0,0,1;0rad)
  Solid = true
  Symmetric = false
FEATURE [Sketcher::SketchObject] Sketch038  label="topSketch010"
  FullyConstrained = true
  sketch-geometry (22):
    g0: LineSegment StartX=5.21097e-06 StartY=3 StartZ=0 EndX=5.21097e-06 EndY=19 EndZ=0
    g1: ArcOfCircle CenterX=19 CenterY=19 CenterZ=0 NormalX=0 NormalY=0 NormalZ=1 AngleXU=0 Radius=19 StartAngle=1.5708 EndAngle=3.14159
    g2: ArcOfCircle CenterX=19 CenterY=19 CenterZ=0 NormalX=0 NormalY=0 NormalZ=1 AngleXU=0 Radius=16 StartAngle=1.5708 EndAngle=3.14159
    g3: LineSegment StartX=114 StartY=35 StartZ=0 EndX=19 EndY=35 EndZ=0
    g4: LineSegment StartX=5.21097e-06 StartY=3 StartZ=0 EndX=5.21097e-06 EndY=0 EndZ=0
    g5: LineSegment StartX=3 StartY=0 StartZ=0 EndX=5.21097e-06 EndY=0 EndZ=0
    g6: LineSegment StartX=3 StartY=19 StartZ=0 EndX=3 EndY=0 EndZ=0
    g7: LineSegment StartX=19 StartY=38 StartZ=0 EndX=124 EndY=38 EndZ=0
    g8: Circle CenterX=119 CenterY=35 CenterZ=0 NormalX=0 NormalY=0 NormalZ=1 AngleXU=0 Radius=1
    g9: Circle CenterX=121 CenterY=35 CenterZ=0 NormalX=0 NormalY=0 NormalZ=1 AngleXU=0 Radius=1
    g10: Circle CenterX=121 CenterY=33 CenterZ=0 NormalX=0 NormalY=0 NormalZ=1 AngleXU=0 Radius=1
    g11: BSplineCurve PolesCount=3 KnotsCount=2 Degree=2 IsPeriodic=0
    g12: GeomPoint X=119 Y=35 Z=0
    g13: GeomPoint X=121 Y=33 Z=0
    g14: LineSegment StartX=119 StartY=35 StartZ=0 EndX=114 EndY=35 EndZ=0
    g15: ArcOfCircle CenterX=105 CenterY=19 CenterZ=0 NormalX=0 NormalY=0 NormalZ=1 AngleXU=0 Radius=16 StartAngle=5.60905 EndAngle=6.28319
    g16: LineSegment StartX=121 StartY=33 StartZ=0 EndX=121 EndY=19 EndZ=0
    g17: LineSegment StartX=117.5 StartY=9.01251 StartZ=0 EndX=121.163 EndY=9.0125 EndZ=0
    g18: ArcOfCircle CenterX=105 CenterY=19 CenterZ=0 NormalX=0 NormalY=0 NormalZ=1 AngleXU=0 Radius=20.6155 StartAngle=5.7297 EndAngle=6.28319
    g19: LineSegment StartX=121.163 StartY=9.0125 StartZ=0 EndX=122.538 EndY=8.16329 EndZ=0
    g20: LineSegment StartX=124 StartY=38 StartZ=0 EndX=125.616 EndY=38 EndZ=0
    g21: LineSegment StartX=125.616 StartY=19 StartZ=0 EndX=125.616 EndY=38 EndZ=0
  constraints (49):
    c: Vertical(g0)
    c: Block(g0)
    c: Coincident(g1,g0)
    c: Block(g1)
    c: Coincident(g2,g1)
    c: Block(g2)
    c: Coincident(g3,g2)
    c: Horizontal(g3)
    c: Tangent(g3,g2)
    c: Coincident(g4,g0)
    c: Distance(g4) = 3
    c: Vertical(g4)
    c: Coincident(g5,g4)
    c: Horizontal(g5)
    c: Coincident(g6,g2)
    c: Coincident(g6,g5)
    c: Vertical(g6)
    c: Horizontal(g7)
    c: Distance(g7) = 105
    c: Coincident(g7,g1)
    c: Block(g3)
    c: Weight(g8) = 1
    c: Equal(g8,g9)
    c: Equal(g8,g10)
    c: InternalAlignment(g8,g11)
    c: InternalAlignment(g9,g11)
    c: InternalAlignment(g10,g11)
    c: InternalAlignment(g12,g11)
    c: InternalAlignment(g13,g11)
    c: Block(g11)
    c: Coincident(g14,g11)
    c: Coincident(g14,g3)
    c: Horizontal(g14)
    c: Block(g15)
    c: Coincident(g16,g11)
    c: Coincident(g16,g15)
    c: Vertical(g16)
    c: Distance(g16) = 14
    c: Coincident(g17,g15)
    c: Block(g18)
    c: Coincident(g19,g18)
    c: Coincident(g20,g7)
    c: Horizontal(g20)
    c: Vertical(g21)
    c: Coincident(g20,g21)
    c: Block(g20)
    c: Block(g21)
    c: Block(g19)
    c: Block(g17)
FEATURE [Part::Extrusion] Extrude029
  Base = -> Sketch038
  Dir = (0,0,1)
  DirMode = 2
  FaceMakerClass = Part::FaceMakerBullseye
  LengthFwd = 72
  LengthRev = 0
  Solid = true
  Symmetric = false
FEATURE [Part::Feature] Face085
  shape: bbox 4.8 x 25.5 x 2e-07 mm, 1 faces, 0 solids (baked)
FEATURE [Part::Revolution] Revolve089  label="moreFrontCaseScrewPost003"
  Angle = 360
  Axis = (0,1,0)
  Base = (0,0,0)
  FaceMakerClass = Part::FaceMakerBullseye
  Placement = pos=(109.5,4.5,3.5) rot=(0,0,1;0rad)
  Solid = false
  Source = -> Face085
  Symmetric = false
FEATURE [Part::Feature] Face086
  shape: bbox 4.8 x 25.5 x 2e-07 mm, 1 faces, 0 solids (baked)
FEATURE [Part::Revolution] Revolve090  label="moreFrontCaseScrewPost004"
  Angle = 360
  Axis = (0,1,0)
  Base = (0,0,0)
  FaceMakerClass = Part::FaceMakerBullseye
  Placement = pos=(109.5,4.5,68.5) rot=(0,0,1;0rad)
  Solid = false
  Source = -> Face086
  Symmetric = false
FEATURE [Part::Fillet] Fillet026  label="top013"
  Base = -> Extrude029
  Edges = 1 edges r=2: [Edge35]
FEATURE [Sketcher::SketchObject] Sketch039
  FullyConstrained = true
  sketch-geometry (7):
    g0: LineSegment StartX=0 StartY=0 StartZ=0 EndX=0 EndY=6 EndZ=0
    g1: Circle CenterX=0 CenterY=0 CenterZ=0 NormalX=0 NormalY=0 NormalZ=1 AngleXU=0 Radius=1
    g2: Circle CenterX=8 CenterY=6 CenterZ=0 NormalX=0 NormalY=0 NormalZ=1 AngleXU=0 Radius=1
    g3: BSplineCurve PolesCount=3 KnotsCount=2 Degree=2 IsPeriodic=0
    g4: GeomPoint X=0 Y=0 Z=0
    g5: GeomPoint X=8 Y=6 Z=0
    g6: LineSegment StartX=0 StartY=6 StartZ=0 EndX=8 EndY=6 EndZ=0
  constraints (14):
    c: Coincident(g0,g-1)
    c: Distance(g0) = 6
    c: Vertical(g0)
    c: Coincident(g3,g0)
    c: Weight(g1) = 1
    c: Equal(g1,g2)
    c: InternalAlignment(g1,g3)
    c: InternalAlignment(g2,g3)
    c: InternalAlignment(g4,g3)
    c: InternalAlignment(g5,g3)
    c: Block(g3)
    c: Coincident(g6,g0)
    c: Coincident(g6,g3)
    c: Horizontal(g6)
FEATURE [Sketcher::SketchObject] Sketch040
  FullyConstrained = true
  sketch-geometry (7):
    g0: LineSegment StartX=0 StartY=0 StartZ=0 EndX=0 EndY=6 EndZ=0
    g1: Circle CenterX=0 CenterY=0 CenterZ=0 NormalX=0 NormalY=0 NormalZ=1 AngleXU=0 Radius=1
    g2: Circle CenterX=8 CenterY=6 CenterZ=0 NormalX=0 NormalY=0 NormalZ=1 AngleXU=0 Radius=1
    g3: BSplineCurve PolesCount=3 KnotsCount=2 Degree=2 IsPeriodic=0
    g4: GeomPoint X=0 Y=0 Z=0
    g5: GeomPoint X=8 Y=6 Z=0
    g6: LineSegment StartX=0 StartY=6 StartZ=0 EndX=8 EndY=6 EndZ=0
  constraints (14):
    c: Coincident(g0,g-1)
    c: Distance(g0) = 6
    c: Vertical(g0)
    c: Coincident(g3,g0)
    c: Weight(g1) = 1
    c: Equal(g1,g2)
    c: InternalAlignment(g1,g3)
    c: InternalAlignment(g2,g3)
    c: InternalAlignment(g4,g3)
    c: InternalAlignment(g5,g3)
    c: Block(g3)
    c: Coincident(g6,g0)
    c: Coincident(g6,g3)
    c: Horizontal(g6)
FEATURE [Sketcher::SketchObject] Sketch041
  FullyConstrained = true
  sketch-geometry (7):
    g0: LineSegment StartX=0 StartY=0 StartZ=0 EndX=0 EndY=6 EndZ=0
    g1: Circle CenterX=0 CenterY=0 CenterZ=0 NormalX=0 NormalY=0 NormalZ=1 AngleXU=0 Radius=1
    g2: Circle CenterX=8 CenterY=6 CenterZ=0 NormalX=0 NormalY=0 NormalZ=1 AngleXU=0 Radius=1
    g3: BSplineCurve PolesCount=3 KnotsCount=2 Degree=2 IsPeriodic=0
    g4: GeomPoint X=0 Y=0 Z=0
    g5: GeomPoint X=8 Y=6 Z=0
    g6: LineSegment StartX=0 StartY=6 StartZ=0 EndX=8 EndY=6 EndZ=0
  constraints (14):
    c: Coincident(g0,g-1)
    c: Distance(g0) = 6
    c: Vertical(g0)
    c: Coincident(g3,g0)
    c: Weight(g1) = 1
    c: Equal(g1,g2)
    c: InternalAlignment(g1,g3)
    c: InternalAlignment(g2,g3)
    c: InternalAlignment(g4,g3)
    c: InternalAlignment(g5,g3)
    c: Block(g3)
    c: Coincident(g6,g0)
    c: Coincident(g6,g3)
    c: Horizontal(g6)
FEATURE [Sketcher::SketchObject] Sketch042
  FullyConstrained = true
  sketch-geometry (7):
    g0: LineSegment StartX=0 StartY=0 StartZ=0 EndX=0 EndY=6 EndZ=0
    g1: Circle CenterX=0 CenterY=0 CenterZ=0 NormalX=0 NormalY=0 NormalZ=1 AngleXU=0 Radius=1
    g2: Circle CenterX=8 CenterY=6 CenterZ=0 NormalX=0 NormalY=0 NormalZ=1 AngleXU=0 Radius=1
    g3: BSplineCurve PolesCount=3 KnotsCount=2 Degree=2 IsPeriodic=0
    g4: GeomPoint X=0 Y=0 Z=0
    g5: GeomPoint X=8 Y=6 Z=0
    g6: LineSegment StartX=0 StartY=6 StartZ=0 EndX=8 EndY=6 EndZ=0
  constraints (14):
    c: Coincident(g0,g-1)
    c: Distance(g0) = 6
    c: Vertical(g0)
    c: Coincident(g3,g0)
    c: Weight(g1) = 1
    c: Equal(g1,g2)
    c: InternalAlignment(g1,g3)
    c: InternalAlignment(g2,g3)
    c: InternalAlignment(g4,g3)
    c: InternalAlignment(g5,g3)
    c: Block(g3)
    c: Coincident(g6,g0)
    c: Coincident(g6,g3)
    c: Horizontal(g6)
FEATURE [Part::Extrusion] Extrude030  label="caseScrewPillarBracket008"
  Base = -> Sketch039
  Dir = (0,0,1)
  DirMode = 2
  FaceMakerClass = Part::FaceMakerBullseye
  LengthFwd = 2.4
  LengthRev = 0
  Placement = pos=(15.76,29,8.8) rot=(0,1,0;0rad)
  Solid = true
  Symmetric = false
FEATURE [Part::Extrusion] Extrude031  label="caseScrewPillarBracket009"
  Base = -> Sketch040
  Dir = (0,0,1)
  DirMode = 2
  FaceMakerClass = Part::FaceMakerBullseye
  LengthFwd = 2.4
  LengthRev = 0
  Placement = pos=(15.76,29,60.8) rot=(0,0,1;0rad)
  Solid = true
  Symmetric = false
FEATURE [Part::Extrusion] Extrude032  label="caseScrewPillarBracket010"
  Base = -> Sketch041
  Dir = (0,0,1)
  DirMode = 2
  FaceMakerClass = Part::FaceMakerBullseye
  LengthFwd = 2.4
  LengthRev = 0
  Placement = pos=(13.7,29,13.26) rot=(0,-1,0;1.5708rad)
  Solid = true
  Symmetric = false
FEATURE [Part::Extrusion] Extrude033  label="caseScrewPillarBracket011"
  Base = -> Sketch042
  Dir = (0,0,1)
  DirMode = 2
  FaceMakerClass = Part::FaceMakerBullseye
  LengthFwd = 2.4
  LengthRev = 0
  Placement = pos=(11.3,29,58.74) rot=(0,1,0;1.5708rad)
  Solid = true
  Symmetric = false
FEATURE [Sketcher::SketchObject] Sketch043
  FullyConstrained = true
  sketch-geometry (7):
    g0: LineSegment StartX=0 StartY=0 StartZ=0 EndX=0 EndY=6 EndZ=0
    g1: Circle CenterX=0 CenterY=0 CenterZ=0 NormalX=0 NormalY=0 NormalZ=1 AngleXU=0 Radius=1
    g2: Circle CenterX=8 CenterY=6 CenterZ=0 NormalX=0 NormalY=0 NormalZ=1 AngleXU=0 Radius=1
    g3: BSplineCurve PolesCount=3 KnotsCount=2 Degree=2 IsPeriodic=0
    g4: GeomPoint X=0 Y=0 Z=0
    g5: GeomPoint X=8 Y=6 Z=0
    g6: LineSegment StartX=0 StartY=6 StartZ=0 EndX=8 EndY=6 EndZ=0
  constraints (14):
    c: Coincident(g0,g-1)
    c: Distance(g0) = 6
    c: Vertical(g0)
    c: Coincident(g3,g0)
    c: Weight(g1) = 1
    c: Equal(g1,g2)
    c: InternalAlignment(g1,g3)
    c: InternalAlignment(g2,g3)
    c: InternalAlignment(g4,g3)
    c: InternalAlignment(g5,g3)
    c: Block(g3)
    c: Coincident(g6,g0)
    c: Coincident(g6,g3)
    c: Horizontal(g6)
FEATURE [Part::Extrusion] Extrude034  label="caseScrewPillarBracket012"
  Base = -> Sketch043
  Dir = (0,0,1)
  DirMode = 2
  FaceMakerClass = Part::FaceMakerBullseye
  LengthFwd = 2.4
  LengthRev = 0
  Placement = pos=(88.3,29,65.23) rot=(0,1,0;1.5708rad)
  Solid = true
  Symmetric = false
FEATURE [Sketcher::SketchObject] Sketch044
  FullyConstrained = true
  sketch-geometry (7):
    g0: LineSegment StartX=0 StartY=0 StartZ=0 EndX=0 EndY=6 EndZ=0
    g1: Circle CenterX=0 CenterY=0 CenterZ=0 NormalX=0 NormalY=0 NormalZ=1 AngleXU=0 Radius=1
    g2: Circle CenterX=8 CenterY=6 CenterZ=0 NormalX=0 NormalY=0 NormalZ=1 AngleXU=0 Radius=1
    g3: BSplineCurve PolesCount=3 KnotsCount=2 Degree=2 IsPeriodic=0
    g4: GeomPoint X=0 Y=0 Z=0
    g5: GeomPoint X=8 Y=6 Z=0
    g6: LineSegment StartX=0 StartY=6 StartZ=0 EndX=8 EndY=6 EndZ=0
  constraints (14):
    c: Coincident(g0,g-1)
    c: Distance(g0) = 6
    c: Vertical(g0)
    c: Coincident(g3,g0)
    c: Weight(g1) = 1
    c: Equal(g1,g2)
    c: InternalAlignment(g1,g3)
    c: InternalAlignment(g2,g3)
    c: InternalAlignment(g4,g3)
    c: InternalAlignment(g5,g3)
    c: Block(g3)
    c: Coincident(g6,g0)
    c: Coincident(g6,g3)
    c: Horizontal(g6)
FEATURE [Part::Extrusion] Extrude035  label="caseScrewPillarBracket013"
  Base = -> Sketch044
  Dir = (0,0,1)
  DirMode = 2
  FaceMakerClass = Part::FaceMakerBullseye
  LengthFwd = 2.4
  LengthRev = 0
  Placement = pos=(90.7,29,6.77) rot=(0,-1,0;1.5708rad)
  Solid = true
  Symmetric = false
FEATURE [Sketcher::SketchObject] Sketch045
  FullyConstrained = true
  sketch-geometry (7):
    g0: LineSegment StartX=0 StartY=0 StartZ=0 EndX=0 EndY=6 EndZ=0
    g1: Circle CenterX=0 CenterY=0 CenterZ=0 NormalX=0 NormalY=0 NormalZ=1 AngleXU=0 Radius=1
    g2: Circle CenterX=8 CenterY=6 CenterZ=0 NormalX=0 NormalY=0 NormalZ=1 AngleXU=0 Radius=1
    g3: BSplineCurve PolesCount=3 KnotsCount=2 Degree=2 IsPeriodic=0
    g4: GeomPoint X=0 Y=0 Z=0
    g5: GeomPoint X=8 Y=6 Z=0
    g6: LineSegment StartX=0 StartY=6 StartZ=0 EndX=8 EndY=6 EndZ=0
  constraints (14):
    c: Coincident(g0,g-1)
    c: Distance(g0) = 6
    c: Vertical(g0)
    c: Coincident(g3,g0)
    c: Weight(g1) = 1
    c: Equal(g1,g2)
    c: InternalAlignment(g1,g3)
    c: InternalAlignment(g2,g3)
    c: InternalAlignment(g4,g3)
    c: InternalAlignment(g5,g3)
    c: Block(g3)
    c: Coincident(g6,g0)
    c: Coincident(g6,g3)
    c: Horizontal(g6)
FEATURE [Sketcher::SketchObject] Sketch046
  FullyConstrained = true
  sketch-geometry (7):
    g0: LineSegment StartX=0 StartY=0 StartZ=0 EndX=0 EndY=6 EndZ=0
    g1: Circle CenterX=0 CenterY=0 CenterZ=0 NormalX=0 NormalY=0 NormalZ=1 AngleXU=0 Radius=1
    g2: Circle CenterX=8 CenterY=6 CenterZ=0 NormalX=0 NormalY=0 NormalZ=1 AngleXU=0 Radius=1
    g3: BSplineCurve PolesCount=3 KnotsCount=2 Degree=2 IsPeriodic=0
    g4: GeomPoint X=0 Y=0 Z=0
    g5: GeomPoint X=8 Y=6 Z=0
    g6: LineSegment StartX=0 StartY=6 StartZ=0 EndX=8 EndY=6 EndZ=0
  constraints (14):
    c: Coincident(g0,g-1)
    c: Distance(g0) = 6
    c: Vertical(g0)
    c: Coincident(g3,g0)
    c: Weight(g1) = 1
    c: Equal(g1,g2)
    c: InternalAlignment(g1,g3)
    c: InternalAlignment(g2,g3)
    c: InternalAlignment(g4,g3)
    c: InternalAlignment(g5,g3)
    c: Block(g3)
    c: Coincident(g6,g0)
    c: Coincident(g6,g3)
    c: Horizontal(g6)
FEATURE [Part::Extrusion] Extrude036  label="caseScrewPillarBracket014"
  Base = -> Sketch045
  Dir = (0,0,1)
  DirMode = 2
  FaceMakerClass = Part::FaceMakerBullseye
  LengthFwd = 2.4
  LengthRev = 0
  Placement = pos=(110.7,29,6.77) rot=(0,-1,0;1.5708rad)
  Solid = true
  Symmetric = false
FEATURE [Part::Extrusion] Extrude037  label="caseScrewPillarBracket015"
  Base = -> Sketch046
  Dir = (0,0,1)
  DirMode = 2
  FaceMakerClass = Part::FaceMakerBullseye
  LengthFwd = 2.4
  LengthRev = 0
  Placement = pos=(108.3,29,65.23) rot=(0,1,0;1.5708rad)
  Solid = true
  Symmetric = false
FEATURE [Part::Box] Box013  label="frontCaseScrewPillarBracket002"
  AttacherType = Attacher::AttachEngine3D
  Height = 2.4
  Length = 22
  Placement = pos=(87,28,2.3) rot=(0,0,1;0rad)
  Width = 7
FEATURE [Part::Box] Box014  label="frontCaseScrewPillarBracket003"
  AttacherType = Attacher::AttachEngine3D
  Height = 2.4
  Length = 22
  Placement = pos=(87,28,67.3) rot=(0,0,1;0rad)
  Width = 7
FEATURE [Part::Feature] Face087
  shape: bbox 4.8 x 30.2 x 2e-07 mm, 1 faces, 0 solids (baked)
FEATURE [Part::Revolution] Revolve091  label="frontCaseScrewPost004"
  Angle = 360
  Axis = (0,1,0)
  Base = (0,0,0)
  FaceMakerClass = Part::FaceMakerBullseye
  Placement = pos=(89.5,4.5,3.5) rot=(0,0,1;0rad)
  Solid = false
  Source = -> Face087
  Symmetric = false
FEATURE [Part::Feature] Face088
  shape: bbox 4.8 x 30.2 x 2e-07 mm, 1 faces, 0 solids (baked)
FEATURE [Part::Revolution] Revolve092  label="frontCaseScrewPost005"
  Angle = 360
  Axis = (0,1,0)
  Base = (0,0,0)
  FaceMakerClass = Part::FaceMakerBullseye
  Placement = pos=(89.5,4.5,68.5) rot=(0,0,1;0rad)
  Solid = false
  Source = -> Face088
  Symmetric = false
FEATURE [Part::Feature] Face089
  shape: bbox 3.5 x 30.2 x 2e-07 mm, 1 faces, 0 solids (baked)
FEATURE [Part::Revolution] Revolve093  label="backCaseScrewPost002"
  Angle = 360
  Axis = (0,1,0)
  Base = (0,0,0)
  FaceMakerClass = Part::FaceMakerBullseye
  Placement = pos=(12.5,4.5,10) rot=(0,0,1;0rad)
  Solid = false
  Source = -> Face089
  Symmetric = false
FEATURE [Part::Feature] Face090
  shape: bbox 3.5 x 30.2 x 2e-07 mm, 1 faces, 0 solids (baked)
FEATURE [Part::Revolution] Revolve094  label="backCaseScrewPost003"
  Angle = 360
  Axis = (0,1,0)
  Base = (0,0,0)
  FaceMakerClass = Part::FaceMakerBullseye
  Placement = pos=(12.5,4.5,62) rot=(0,0,1;0rad)
  Solid = false
  Source = -> Face090
  Symmetric = false
FEATURE [Part::Box] Box015  label="Cube011"
  AttacherType = Attacher::AttachEngine3D
  Height = 28.8
  Length = 3
  Placement = pos=(107.3,28,21.6) rot=(0,0,1;0rad)
  Width = 7
FEATURE [Part::Box] Box016  label="Cube012"
  AttacherType = Attacher::AttachEngine3D
  Height = 3
  Length = 7.4
  Placement = pos=(107.3,28,18.6) rot=(0,0,1;0rad)
  Width = 7
FEATURE [Part::Box] Box017  label="Cube013"
  AttacherType = Attacher::AttachEngine3D
  Height = 3
  Length = 7.4
  Placement = pos=(107.3,28,50.4) rot=(0,0,1;0rad)
  Width = 7
FEATURE [Part::Cylinder] Cylinder024
  Angle = 360
  AttacherType = Attacher::AttachEngine3D
  Height = 20
  Placement = pos=(0,0,36.15) rot=(0,0,1;0rad)
  Radius = 14.3
FEATURE [Part::Cylinder] Cylinder025
  Angle = 360
  AttacherType = Attacher::AttachEngine3D
  Height = 10
  Placement = pos=(0,0,36.15) rot=(0,0,1;0rad)
  Radius = 4
FEATURE [Part::MultiFuse] Fusion066  label="removeToCreteHoleForPlugHousing009"
  Placement = pos=(70,19,36) rot=(0,1,0;1.5708rad)
  Shapes = -> [Cylinder024,Cylinder025]
FEATURE [Part::MultiFuse] Fusion065  label="plugHousingBracketHolder002"
  Shapes = -> [Box017,Box015,Box016]
FEATURE [Part::Cut] Cut025  label="plugHousingBracketHolder003"
  Base = -> Fusion065
  Placement = pos=(7,0,0) rot=(0,0,1;0rad)
  Tool = -> Fusion066
FEATURE [Sketcher::SketchObject] Sketch047
  FullyConstrained = false
  Placement = pos=(0,0,0) rot=(1,0,0;1.5708rad)
  sketch-geometry (24):
    g0: ArcOfCircle CenterX=-4 CenterY=-10.5 CenterZ=0 NormalX=0 NormalY=0 NormalZ=1 AngleXU=0 Radius=1.5 StartAngle=6e-16 EndAngle=3.14159
    g1: ArcOfCircle CenterX=-34.2 CenterY=-10.5 CenterZ=0 NormalX=0 NormalY=0 NormalZ=1 AngleXU=0 Radius=1.5 StartAngle=0 EndAngle=3.14159
    g2: ArcOfCircle CenterX=-34.2 CenterY=-27.7 CenterZ=0 NormalX=0 NormalY=0 NormalZ=1 AngleXU=0 Radius=1.5 StartAngle=3.14159 EndAngle=6.28319
    g3: ArcOfCircle CenterX=-4 CenterY=-27.7 CenterZ=0 NormalX=0 NormalY=0 NormalZ=1 AngleXU=0 Radius=1.5 StartAngle=3.1416 EndAngle=6.28319
    g4: ArcOfCircle CenterX=-10 CenterY=-4.3 CenterZ=0 NormalX=0 NormalY=0 NormalZ=1 AngleXU=0 Radius=1.5 StartAngle=2e-16 EndAngle=3.14159
    g5: ArcOfCircle CenterX=-16.1 CenterY=-1.8 CenterZ=0 NormalX=0 NormalY=0 NormalZ=1 AngleXU=0 Radius=1.5 StartAngle=5e-16 EndAngle=3.14159
    g6: ArcOfCircle CenterX=-22.1 CenterY=-1.8 CenterZ=0 NormalX=0 NormalY=0 NormalZ=1 AngleXU=0 Radius=1.5 StartAngle=5e-16 EndAngle=3.14159
    g7: ArcOfCircle CenterX=-28.2 CenterY=-4.3 CenterZ=0 NormalX=0 NormalY=0 NormalZ=1 AngleXU=0 Radius=1.5 StartAngle=2e-16 EndAngle=3.14159
    g8: ArcOfCircle CenterX=-10 CenterY=-33.9 CenterZ=0 NormalX=0 NormalY=0 NormalZ=1 AngleXU=0 Radius=1.5 StartAngle=3.14159 EndAngle=6.28319
    g9: ArcOfCircle CenterX=-16.1 CenterY=-36.4 CenterZ=0 NormalX=0 NormalY=0 NormalZ=1 AngleXU=0 Radius=1.5 StartAngle=3.14159 EndAngle=6.28319
    g10: ArcOfCircle CenterX=-22.1 CenterY=-36.4 CenterZ=0 NormalX=0 NormalY=0 NormalZ=1 AngleXU=0 Radius=1.5 StartAngle=3.14159 EndAngle=6.28319
    g11: ArcOfCircle CenterX=-28.2 CenterY=-33.9 CenterZ=0 NormalX=0 NormalY=0 NormalZ=1 AngleXU=0 Radius=1.5 StartAngle=3.14159 EndAngle=6.28319
    g12: LineSegment StartX=-35.7 StartY=-10.5 StartZ=0 EndX=-35.7 EndY=-27.7 EndZ=0
    g13: LineSegment StartX=-32.7 StartY=-10.5 StartZ=0 EndX=-32.7 EndY=-27.7 EndZ=0
    g14: LineSegment StartX=-29.7 StartY=-33.9 StartZ=0 EndX=-29.7 EndY=-4.3 EndZ=0
    g15: LineSegment StartX=-26.7 StartY=-33.9 StartZ=0 EndX=-26.7 EndY=-4.3 EndZ=0
    g16: LineSegment StartX=-2.5 StartY=-10.5 StartZ=0 EndX=-2.5 EndY=-27.7 EndZ=0
    g17: LineSegment StartX=-8.5 StartY=-4.3 StartZ=0 EndX=-8.5 EndY=-33.9 EndZ=0
    g18: LineSegment StartX=-5.5 StartY=-10.5 StartZ=0 EndX=-5.5 EndY=-27.7 EndZ=0
    g19: LineSegment StartX=-11.5 StartY=-4.3 StartZ=0 EndX=-11.5 EndY=-33.9 EndZ=0
    g20: LineSegment StartX=-14.6 StartY=-1.8 StartZ=0 EndX=-14.6 EndY=-36.4 EndZ=0
    g21: LineSegment StartX=-17.6 StartY=-1.8 StartZ=0 EndX=-17.6 EndY=-36.4 EndZ=0
    g22: LineSegment StartX=-20.6 StartY=-36.4 StartZ=0 EndX=-20.6 EndY=-1.8 EndZ=0
    g23: LineSegment StartX=-23.6 StartY=-1.8 StartZ=0 EndX=-23.6 EndY=-36.4 EndZ=0
  constraints (48):
    c: Block(g0)
    c: Block(g1)
    c: Block(g2)
    c: Block(g3)
    c: Block(g4)
    c: Block(g5)
    c: Block(g6)
    c: Block(g7)
    c: Block(g8)
    c: Block(g9)
    c: Block(g10)
    c: Block(g11)
    c: Coincident(g12,g1)
    c: Coincident(g12,g2)
    c: Vertical(g12)
    c: Coincident(g13,g1)
    c: Coincident(g13,g2)
    c: Vertical(g13)
    c: Coincident(g14,g11)
    c: Coincident(g14,g7)
    c: Vertical(g14)
    c: Coincident(g15,g11)
    c: Coincident(g15,g7)
    c: Vertical(g15)
    c: Coincident(g16,g0)
    c: Coincident(g16,g3)
    c: Vertical(g16)
    c: Coincident(g17,g4)
    c: Coincident(g17,g8)
    c: Vertical(g17)
    c: Coincident(g18,g0)
    c: Coincident(g18,g3)
    c: Vertical(g18)
    c: Coincident(g19,g4)
    c: Coincident(g19,g8)
    c: Vertical(g19)
    c: Coincident(g20,g5)
    c: Coincident(g20,g9)
    c: Vertical(g20)
    c: Coincident(g21,g5)
    c: Coincident(g21,g9)
    c: Vertical(g21)
    c: Coincident(g22,g10)
    c: Coincident(g22,g6)
    c: Vertical(g22)
    c: Coincident(g23,g6)
    c: Coincident(g23,g10)
    c: Vertical(g23)
FEATURE [Part::Extrusion] Extrude038  label="removeToCreateFanGrillHoles001"
  Base = -> Sketch047
  Dir = (0,-1,6e-16)
  DirMode = 2
  FaceMakerClass = Part::FaceMakerBullseye
  LengthFwd = 10
  LengthRev = 0
  Placement = pos=(65.4,44,54.82) rot=(0,0,1;0rad)
  Solid = true
  Symmetric = false
FEATURE [Part::Feature] Wire004
  shape: bbox 11 x 5.2 x 2e-07 mm, 0 faces, 0 solids (baked)
FEATURE [Part::Revolution] Revolve095
  Angle = 360
  Axis = (0,1,0)
  Base = (0,0,0)
  FaceMakerClass = Part::FaceMakerBullseye
  Placement = pos=(30.3,38,19.7) rot=(0,0,1;0rad)
  Solid = true
  Source = -> Wire004
  Symmetric = false
FEATURE [Part::Feature] Wire005
  shape: bbox 11 x 5.2 x 2e-07 mm, 0 faces, 0 solids (baked)
FEATURE [Part::Revolution] Revolve096
  Angle = 360
  Axis = (0,1,0)
  Base = (0,0,0)
  FaceMakerClass = Part::FaceMakerBullseye
  Placement = pos=(30.3,38,51.7) rot=(0,0,1;0rad)
  Solid = true
  Source = -> Wire005
  Symmetric = false
FEATURE [Part::Feature] Wire006
  shape: bbox 11 x 5.2 x 2e-07 mm, 0 faces, 0 solids (baked)
FEATURE [Part::Revolution] Revolve097
  Angle = 360
  Axis = (0,1,0)
  Base = (0,0,0)
  FaceMakerClass = Part::FaceMakerBullseye
  Placement = pos=(62.3,38,51.7) rot=(0,0,1;0rad)
  Solid = true
  Source = -> Wire006
  Symmetric = false
FEATURE [Part::Feature] Wire007
  shape: bbox 11 x 5.2 x 2e-07 mm, 0 faces, 0 solids (baked)
FEATURE [Part::Revolution] Revolve098
  Angle = 360
  Axis = (0,1,0)
  Base = (0,0,0)
  FaceMakerClass = Part::FaceMakerBullseye
  Placement = pos=(62.3,38,19.7) rot=(0,0,1;0rad)
  Solid = true
  Source = -> Wire007
  Symmetric = false
FEATURE [Part::MultiFuse] Fusion067  label="fanScrewHousing002"
  Shapes = -> [Revolve098,Revolve097,Revolve096,Revolve095]
FEATURE [Part::Feature] Face091 .. Face094  x4 (patterned run collapsed; names and placements below)
  shape: bbox 3.5 x 17.8 x 2e-07 mm, 1 faces, 0 solids (baked)
FEATURE [Part::Revolution] Revolve099  label="removeToCreateScrewAndThreadedInsertHole026"
  Angle = 360
  Axis = (0,1,0)
  Base = (0,0,0)
  FaceMakerClass = Part::FaceMakerBullseye
  Placement = pos=(62.3,30.3,19.7) rot=(0,0,1;0rad)
  Solid = false
  Source = -> Face091
  Symmetric = false
FEATURE [Part::Revolution] Revolve100  label="removeToCreateScrewAndThreadedInsertHole027"
  Angle = 360
  Axis = (0,1,0)
  Base = (0,0,0)
  FaceMakerClass = Part::FaceMakerBullseye
  Placement = pos=(62.3,30.3,51.7) rot=(0,0,1;0rad)
  Solid = false
  Source = -> Face092
  Symmetric = false
FEATURE [Part::Revolution] Revolve101  label="removeToCreateScrewAndThreadedInsertHole028"
  Angle = 360
  Axis = (0,1,0)
  Base = (0,0,0)
  FaceMakerClass = Part::FaceMakerBullseye
  Placement = pos=(30.3,30.3,19.7) rot=(0,0,1;0rad)
  Solid = false
  Source = -> Face093
  Symmetric = false
FEATURE [Part::Revolution] Revolve102  label="removeToCreateScrewAndThreadedInsertHole029"
  Angle = 360
  Axis = (0,1,0)
  Base = (0,0,0)
  FaceMakerClass = Part::FaceMakerBullseye
  Placement = pos=(30.3,30.3,51.7) rot=(0,0,1;0rad)
  Solid = false
  Source = -> Face094
  Symmetric = false
FEATURE [Part::MultiFuse] Fusion068  label="createThreadedInsertHolesForFan002"
  Shapes = -> [Revolve099,Revolve100,Revolve101,Revolve102]
FEATURE [Part::Cut] Cut026  label="fanScrewHousing003"
  Base = -> Fusion067
  Tool = -> Fusion068
FEATURE [Sketcher::SketchObject] Sketch048
  FullyConstrained = false
  Placement = pos=(0,0,0) rot=(1,0,0;1.5708rad)
  sketch-geometry (24):
    g0: ArcOfCircle CenterX=-4 CenterY=-10.5 CenterZ=0 NormalX=0 NormalY=0 NormalZ=1 AngleXU=0 Radius=1.5 StartAngle=6e-16 EndAngle=3.14159
    g1: ArcOfCircle CenterX=-34.2 CenterY=-10.5 CenterZ=0 NormalX=0 NormalY=0 NormalZ=1 AngleXU=0 Radius=1.5 StartAngle=0 EndAngle=3.14159
    g2: ArcOfCircle CenterX=-34.2 CenterY=-27.7 CenterZ=0 NormalX=0 NormalY=0 NormalZ=1 AngleXU=0 Radius=1.5 StartAngle=3.14159 EndAngle=6.28319
    g3: ArcOfCircle CenterX=-4 CenterY=-27.7 CenterZ=0 NormalX=0 NormalY=0 NormalZ=1 AngleXU=0 Radius=1.5 StartAngle=3.1416 EndAngle=6.28319
    g4: ArcOfCircle CenterX=-10 CenterY=-4.3 CenterZ=0 NormalX=0 NormalY=0 NormalZ=1 AngleXU=0 Radius=1.5 StartAngle=2e-16 EndAngle=3.14159
    g5: ArcOfCircle CenterX=-16.1 CenterY=-1.8 CenterZ=0 NormalX=0 NormalY=0 NormalZ=1 AngleXU=0 Radius=1.5 StartAngle=5e-16 EndAngle=3.14159
    g6: ArcOfCircle CenterX=-22.1 CenterY=-1.8 CenterZ=0 NormalX=0 NormalY=0 NormalZ=1 AngleXU=0 Radius=1.5 StartAngle=5e-16 EndAngle=3.14159
    g7: ArcOfCircle CenterX=-28.2 CenterY=-4.3 CenterZ=0 NormalX=0 NormalY=0 NormalZ=1 AngleXU=0 Radius=1.5 StartAngle=2e-16 EndAngle=3.14159
    g8: ArcOfCircle CenterX=-10 CenterY=-33.9 CenterZ=0 NormalX=0 NormalY=0 NormalZ=1 AngleXU=0 Radius=1.5 StartAngle=3.14159 EndAngle=6.28319
    g9: ArcOfCircle CenterX=-16.1 CenterY=-36.4 CenterZ=0 NormalX=0 NormalY=0 NormalZ=1 AngleXU=0 Radius=1.5 StartAngle=3.14159 EndAngle=6.28319
    g10: ArcOfCircle CenterX=-22.1 CenterY=-36.4 CenterZ=0 NormalX=0 NormalY=0 NormalZ=1 AngleXU=0 Radius=1.5 StartAngle=3.14159 EndAngle=6.28319
    g11: ArcOfCircle CenterX=-28.2 CenterY=-33.9 CenterZ=0 NormalX=0 NormalY=0 NormalZ=1 AngleXU=0 Radius=1.5 StartAngle=3.14159 EndAngle=6.28319
    g12: LineSegment StartX=-35.7 StartY=-10.5 StartZ=0 EndX=-35.7 EndY=-27.7 EndZ=0
    g13: LineSegment StartX=-32.7 StartY=-10.5 StartZ=0 EndX=-32.7 EndY=-27.7 EndZ=0
    g14: LineSegment StartX=-29.7 StartY=-33.9 StartZ=0 EndX=-29.7 EndY=-4.3 EndZ=0
    g15: LineSegment StartX=-26.7 StartY=-33.9 StartZ=0 EndX=-26.7 EndY=-4.3 EndZ=0
    g16: LineSegment StartX=-2.5 StartY=-10.5 StartZ=0 EndX=-2.5 EndY=-27.7 EndZ=0
    g17: LineSegment StartX=-8.5 StartY=-4.3 StartZ=0 EndX=-8.5 EndY=-33.9 EndZ=0
    g18: LineSegment StartX=-5.5 StartY=-10.5 StartZ=0 EndX=-5.5 EndY=-27.7 EndZ=0
    g19: LineSegment StartX=-11.5 StartY=-4.3 StartZ=0 EndX=-11.5 EndY=-33.9 EndZ=0
    g20: LineSegment StartX=-14.6 StartY=-1.8 StartZ=0 EndX=-14.6 EndY=-36.4 EndZ=0
    g21: LineSegment StartX=-17.6 StartY=-1.8 StartZ=0 EndX=-17.6 EndY=-36.4 EndZ=0
    g22: LineSegment StartX=-20.6 StartY=-36.4 StartZ=0 EndX=-20.6 EndY=-1.8 EndZ=0
    g23: LineSegment StartX=-23.6 StartY=-1.8 StartZ=0 EndX=-23.6 EndY=-36.4 EndZ=0
  constraints (48):
    c: Block(g0)
    c: Block(g1)
    c: Block(g2)
    c: Block(g3)
    c: Block(g4)
    c: Block(g5)
    c: Block(g6)
    c: Block(g7)
    c: Block(g8)
    c: Block(g9)
    c: Block(g10)
    c: Block(g11)
    c: Coincident(g12,g1)
    c: Coincident(g12,g2)
    c: Vertical(g12)
    c: Coincident(g13,g1)
    c: Coincident(g13,g2)
    c: Vertical(g13)
    c: Coincident(g14,g11)
    c: Coincident(g14,g7)
    c: Vertical(g14)
    c: Coincident(g15,g11)
    c: Coincident(g15,g7)
    c: Vertical(g15)
    c: Coincident(g16,g0)
    c: Coincident(g16,g3)
    c: Vertical(g16)
    c: Coincident(g17,g4)
    c: Coincident(g17,g8)
    c: Vertical(g17)
    c: Coincident(g18,g0)
    c: Coincident(g18,g3)
    c: Vertical(g18)
    c: Coincident(g19,g4)
    c: Coincident(g19,g8)
    c: Vertical(g19)
    c: Coincident(g20,g5)
    c: Coincident(g20,g9)
    c: Vertical(g20)
    c: Coincident(g21,g5)
    c: Coincident(g21,g9)
    c: Vertical(g21)
    c: Coincident(g22,g10)
    c: Coincident(g22,g6)
    c: Vertical(g22)
    c: Coincident(g23,g6)
    c: Coincident(g23,g10)
    c: Vertical(g23)
FEATURE [Part::Extrusion] Extrude039  label="removeToCreateFanGrillHoles002"
  Base = -> Sketch048
  Dir = (0,-1,6e-16)
  DirMode = 2
  FaceMakerClass = Part::FaceMakerBullseye
  LengthFwd = 10
  LengthRev = 0
  Placement = pos=(65.4,44,54.82) rot=(0,0,1;0rad)
  Solid = true
  Symmetric = false
FEATURE [Part::Cut] Cut027  label="fanScrewHousing004"
  Base = -> Cut026
  Tool = -> Extrude038
FEATURE [Part::Cut] Cut028  label="top014"
  Base = -> Fillet026
  Tool = -> Extrude039
FEATURE [Part::Feature] Face095 .. Face098  x4 (patterned run collapsed; names and placements below)
  shape: bbox 3.5 x 17.8 x 2e-07 mm, 1 faces, 0 solids (baked)
FEATURE [Part::Revolution] Revolve103  label="removeToCreateScrewAndThreadedInsertHole030"
  Angle = 360
  Axis = (0,1,0)
  Base = (0,0,0)
  FaceMakerClass = Part::FaceMakerBullseye
  Placement = pos=(62.3,30.3,19.7) rot=(0,0,1;0rad)
  Solid = false
  Source = -> Face095
  Symmetric = false
FEATURE [Part::Revolution] Revolve104  label="removeToCreateScrewAndThreadedInsertHole031"
  Angle = 360
  Axis = (0,1,0)
  Base = (0,0,0)
  FaceMakerClass = Part::FaceMakerBullseye
  Placement = pos=(62.3,30.3,51.7) rot=(0,0,1;0rad)
  Solid = false
  Source = -> Face096
  Symmetric = false
FEATURE [Part::Revolution] Revolve105  label="removeToCreateScrewAndThreadedInsertHole032"
  Angle = 360
  Axis = (0,1,0)
  Base = (0,0,0)
  FaceMakerClass = Part::FaceMakerBullseye
  Placement = pos=(30.3,30.3,19.7) rot=(0,0,1;0rad)
  Solid = false
  Source = -> Face097
  Symmetric = false
FEATURE [Part::Revolution] Revolve106  label="removeToCreateScrewAndThreadedInsertHole033"
  Angle = 360
  Axis = (0,1,0)
  Base = (0,0,0)
  FaceMakerClass = Part::FaceMakerBullseye
  Placement = pos=(30.3,30.3,51.7) rot=(0,0,1;0rad)
  Solid = false
  Source = -> Face098
  Symmetric = false
FEATURE [Part::MultiFuse] Fusion069  label="createThreadedInsertHolesForFan003"
  Shapes = -> [Revolve103,Revolve104,Revolve105,Revolve106]
FEATURE [Part::Cut] Cut029  label="top015"
  Base = -> Cut028
  Tool = -> Fusion054
FEATURE [Part::Cut] Cut030  label="fanScrewHousing005"
  Base = -> Cut027
  Tool = -> Fusion069
FEATURE [Part::Cylinder] Cylinder026  label="removeToCreteHoleForPlugHousing010"
  Angle = 360
  AttacherType = Attacher::AttachEngine3D
  Height = 20
  Placement = pos=(-2,19,36) rot=(0,1,0;1.5708rad)
  Radius = 14.3
FEATURE [Part::Box] Box018  label="removeToCreteHoleForPlugHousing011"
  AttacherType = Attacher::AttachEngine3D
  Height = 28.6
  Length = 10
  Placement = pos=(-2,0,21.7) rot=(0,0,1;0rad)
  Width = 19
FEATURE [Part::Box] Box019  label="wireHolderBottomCaseBit"
  AttacherType = Attacher::AttachEngine3D
  Height = 28
  Length = 3
  Placement = pos=(0,0,22) rot=(0,0,1;0rad)
  Width = 21
FEATURE [Part::Cylinder] Cylinder027  label="removeToCreteHoleForPlugHousing012"
  Angle = 360
  AttacherType = Attacher::AttachEngine3D
  Height = 20
  Placement = pos=(-2,19,36) rot=(0,1,0;1.5708rad)
  Radius = 14.3
FEATURE [Part::Cut] Cut031  label="wireHolderBottomCaseBit001"
  Base = -> Box019
  Tool = -> Cylinder027
FEATURE [Part::MultiFuse] Fusion070  label="removeToCreteHoleForPlugHousing013"
  Shapes = -> [Box018,Cylinder026]
FEATURE [Part::Cut] Cut032  label="top016"
  Base = -> Cut029
  Tool = -> Fusion070
FEATURE [Part::Cylinder] Cylinder028
  Angle = 360
  AttacherType = Attacher::AttachEngine3D
  Height = 20
  Placement = pos=(0,0,36.15) rot=(0,0,1;0rad)
  Radius = 14.3
FEATURE [Part::Cylinder] Cylinder029
  Angle = 360
  AttacherType = Attacher::AttachEngine3D
  Height = 10
  Placement = pos=(0,0,36.15) rot=(0,0,1;0rad)
  Radius = 4
FEATURE [Part::MultiFuse] Fusion071  label="removeToCreteHoleForPlugHousing014"
  Placement = pos=(70,19,36) rot=(0,1,0;1.5708rad)
  Shapes = -> [Cylinder028,Cylinder029]
FEATURE [Sketcher::SketchObject] Sketch049  label="topSketch011"
  FullyConstrained = true
  sketch-geometry (4):
    g0: ArcOfCircle CenterX=105 CenterY=19 CenterZ=0 NormalX=0 NormalY=0 NormalZ=1 AngleXU=0 Radius=20.6155 StartAngle=5.54125 EndAngle=6.28319
    g1: ArcOfCircle CenterX=105 CenterY=19 CenterZ=0 NormalX=0 NormalY=0 NormalZ=1 AngleXU=0 Radius=13 StartAngle=5.54125 EndAngle=6.28319
    g2: LineSegment StartX=118 StartY=19 StartZ=0 EndX=125.616 EndY=19 EndZ=0
    g3: LineSegment StartX=114.583 StartY=10.2157 StartZ=0 EndX=120.197 EndY=5.06982 EndZ=0
  constraints (7):
    c: Block(g0)
    c: Block(g1)
    c: Coincident(g2,g1)
    c: Coincident(g2,g0)
    c: Horizontal(g2)
    c: Coincident(g3,g1)
    c: Coincident(g3,g0)
FEATURE [Part::Box] Box020  label="removeToCreteHoleForPlugHousing015"
  AttacherType = Attacher::AttachEngine3D
  Height = 28.6
  Length = 20
  Placement = pos=(106.15,0,21.7) rot=(0,0,1;0rad)
  Width = 19
FEATURE [Part::MultiFuse] Fusion072  label="removeToCreteHoleForPlugHousing016"
  Shapes = -> [Box020,Fusion071]
FEATURE [Part::Cut] Cut033  label="removeToCreteHoleForPlugHousing017"
  Base = -> Cut032
  Tool = -> Fusion072
FEATURE [Part::Cylinder] Cylinder030
  Angle = 360
  AttacherType = Attacher::AttachEngine3D
  Height = 20
  Placement = pos=(0,0,36.15) rot=(0,0,1;0rad)
  Radius = 14.3
FEATURE [Part::Cylinder] Cylinder031
  Angle = 360
  AttacherType = Attacher::AttachEngine3D
  Height = 10
  Placement = pos=(0,0,36.15) rot=(0,0,1;0rad)
  Radius = 4
FEATURE [Part::Box] Box021  label="removeToCreteHoleForPlugHousing019"
  AttacherType = Attacher::AttachEngine3D
  Height = 28.6
  Length = 20
  Placement = pos=(106.15,0,21.7) rot=(0,0,1;0rad)
  Width = 19
FEATURE [Part::MultiFuse] Fusion074  label="removeToCreteHoleForPlugHousing020"
  Placement = pos=(70,19,36) rot=(0,1,0;1.5708rad)
  Shapes = -> [Cylinder030,Cylinder031]
FEATURE [Part::MultiFuse] Fusion073  label="removeToCreteHoleForPlugHousing018"
  Placement = pos=(0,0,28.3) rot=(0,0,1;0rad)
  Shapes = -> [Box021,Fusion074]
FEATURE [Part::Cylinder] Cylinder032
  Angle = 360
  AttacherType = Attacher::AttachEngine3D
  Height = 20
  Placement = pos=(0,0,36.15) rot=(0,0,1;0rad)
  Radius = 14.3
FEATURE [Part::Cylinder] Cylinder033
  Angle = 360
  AttacherType = Attacher::AttachEngine3D
  Height = 10
  Placement = pos=(0,0,36.15) rot=(0,0,1;0rad)
  Radius = 4
FEATURE [Part::Box] Box022  label="removeToCreteHoleForPlugHousing021"
  AttacherType = Attacher::AttachEngine3D
  Height = 28.6
  Length = 20
  Placement = pos=(106.15,0,21.7) rot=(0,0,1;0rad)
  Width = 19
FEATURE [Part::MultiFuse] Fusion076  label="removeToCreteHoleForPlugHousing023"
  Placement = pos=(70,19,36) rot=(0,1,0;1.5708rad)
  Shapes = -> [Cylinder032,Cylinder033]
FEATURE [Part::MultiFuse] Fusion075  label="removeToCreteHoleForPlugHousing022"
  Placement = pos=(0,0,-28.3) rot=(0,0,1;0rad)
  Shapes = -> [Box022,Fusion076]
FEATURE [Part::MultiFuse] Fusion077  label="removeToCreatePlugHousingBottomBit"
  Shapes = -> [Fusion075,Fusion073]
FEATURE [Part::Cylinder] Cylinder034
  Angle = 360
  AttacherType = Attacher::AttachEngine3D
  Height = 20
  Placement = pos=(0,0,36.15) rot=(0,0,1;0rad)
  Radius = 14
FEATURE [Part::Cylinder] Cylinder035
  Angle = 360
  AttacherType = Attacher::AttachEngine3D
  Height = 10
  Placement = pos=(0,0,36.15) rot=(0,0,1;0rad)
  Radius = 4
FEATURE [Part::MultiFuse] Fusion078  label="removeToCreteHoleForPlugHousing024"
  Placement = pos=(70,19,36) rot=(0,1,0;1.5708rad)
  Shapes = -> [Cylinder034,Cylinder035]
FEATURE [Part::MultiFuse] Fusion079  label="removeToCreatePlugHousingBottomBit001"
  Shapes = -> [Fusion078,Fusion077]
FEATURE [Part::Extrusion] Extrude040  label="bottomPlugHousingBit"
  Base = -> Sketch049
  Dir = (0,0,1)
  DirMode = 2
  FaceMakerClass = Part::FaceMakerBullseye
  LengthFwd = 72
  LengthRev = 0
  Solid = true
  Symmetric = false
FEATURE [Part::Cut] Cut034  label="bottomPlugHousingBit001"
  Base = -> Extrude040
  Placement = pos=(-0.09,0,0) rot=(0,0,1;0rad)
  Tool = -> Fusion079
FEATURE [Part::Box] Box023  label="Cube014"
  AttacherType = Attacher::AttachEngine3D
  Height = 16
  Length = 8
  Placement = pos=(12.7,31.52,28) rot=(0,0,1;0rad)
  Width = 4
FEATURE [Part::Cylinder] Cylinder036
  Angle = 360
  AttacherType = Attacher::AttachEngine3D
  Height = 10
  Placement = pos=(0,0,36.15) rot=(0,0,1;0rad)
  Radius = 4
FEATURE [Part::Cylinder] Cylinder037
  Angle = 360
  AttacherType = Attacher::AttachEngine3D
  Height = 20
  Placement = pos=(0,0,36.15) rot=(0,0,1;0rad)
  Radius = 8.2
FEATURE [Part::MultiFuse] Fusion080  label="removeToCreteHoleForPlugHousing025"
  Placement = pos=(-42,19,36) rot=(0,1,0;1.5708rad)
  Shapes = -> [Cylinder037,Cylinder036]
FEATURE [Sketcher::SketchObject] Sketch050  label="topSketch012"
  FullyConstrained = true
  sketch-geometry (4):
    g0: LineSegment StartX=16.8446 StartY=31.512 StartZ=0 EndX=16.3251 EndY=34.4666 EndZ=0
    g1: ArcOfCircle CenterX=19 CenterY=19.2524 CenterZ=0 NormalX=0 NormalY=0 NormalZ=1 AngleXU=0 Radius=15.4476 StartAngle=1.74483 EndAngle=2.72717
    g2: ArcOfCircle CenterX=19 CenterY=19.2524 CenterZ=0 NormalX=0 NormalY=0 NormalZ=1 AngleXU=0 Radius=12.4476 StartAngle=1.74483 EndAngle=2.73189
    g3: LineSegment StartX=4.86004 StartY=25.4725 StartZ=0 EndX=7.58253 EndY=24.2107 EndZ=0
  constraints (7):
    c: Block(g0)
    c: Coincident(g1,g0)
    c: Coincident(g2,g0)
    c: Coincident(g3,g1)
    c: Coincident(g3,g2)
    c: Block(g1)
    c: Block(g2)
FEATURE [Part::Extrusion] Extrude041
  Base = -> Sketch050
  Dir = (0,0,1)
  DirMode = 2
  FaceMakerClass = Part::FaceMakerBullseye
  LengthFwd = 10.6
  LengthRev = 0
  Placement = pos=(0,0,31) rot=(0,0,1;0rad)
  Solid = true
  Symmetric = false
FEATURE [Part::Cut] Cut035
  Base = -> Extrude041
  Placement = pos=(0,0,-0.3) rot=(0,0,1;0rad)
  Tool = -> Fusion080
FEATURE [Part::Cut] Cut036
  Base = -> Box023
  Tool = -> Cut035
FEATURE [Part::Fillet] Fillet027
  Base = -> Cut036
  Edges = 1 edges r=0.7: [Edge13]
FEATURE [Part::Fillet] Fillet028
  Base = -> Fillet027
  Edges = 1 edges r=0.7: [Edge13]
FEATURE [Part::Fillet] Fillet029
  Base = -> Fillet028
  Edges = 1 edges r=0.7: [Edge16]
FEATURE [Part::Fillet] Fillet030
  Base = -> Fillet029
  Edges = 1 edges r=0.7: [Edge11]
FEATURE [Part::Fillet] Fillet031
  Base = -> Fillet030
  Edges = 1 edges r=0.7: [Edge10]
FEATURE [Part::Fillet] Fillet032
  Base = -> Fillet031
  Edges = 1 edges r=1.2: [Edge5]
FEATURE [Part::Fillet] Fillet033
  Base = -> Fillet032
  Edges = 1 edges r=1.2: [Edge12]
FEATURE [Part::Fillet] Fillet034  label="wireHousingRetainer"
  Base = -> Fillet033
  Edges = 1 edges r=2: [Edge1]
  Placement = pos=(0.3,0,0) rot=(0,0,1;0rad)
FEATURE [Part::Feature] Face099
  shape: bbox 3.5 x 17.8 x 2e-07 mm, 1 faces, 0 solids (baked)
FEATURE [Part::Revolution] Revolve107  label="removeToCreateScrewAndThreadedInsertHole034"
  Angle = 360
  Axis = (0,1,0)
  Base = (0,0,0)
  FaceMakerClass = Part::FaceMakerBullseye
  Placement = pos=(12.5,0,10) rot=(0,0,1;0rad)
  Solid = false
  Source = -> Face099
  Symmetric = false
FEATURE [Part::Feature] Face100
  shape: bbox 3.5 x 17.8 x 2e-07 mm, 1 faces, 0 solids (baked)
FEATURE [Part::Revolution] Revolve108  label="removeToCreateScrewAndThreadedInsertHole035"
  Angle = 360
  Axis = (0,1,0)
  Base = (0,0,0)
  FaceMakerClass = Part::FaceMakerBullseye
  Placement = pos=(12.5,0,62) rot=(0,0,1;0rad)
  Solid = false
  Source = -> Face100
  Symmetric = false
FEATURE [Part::Feature] Face101
  shape: bbox 3.5 x 17.8 x 2e-07 mm, 1 faces, 0 solids (baked)
FEATURE [Part::Revolution] Revolve109  label="removeToCreateScrewAndThreadedInsertHole036"
  Angle = 360
  Axis = (0,1,0)
  Base = (0,0,0)
  FaceMakerClass = Part::FaceMakerBullseye
  Placement = pos=(89.5,0,68.5) rot=(0,0,1;0rad)
  Solid = false
  Source = -> Face101
  Symmetric = false
FEATURE [Part::Feature] Face102
  shape: bbox 3.5 x 17.8 x 2e-07 mm, 1 faces, 0 solids (baked)
FEATURE [Part::Revolution] Revolve110  label="removeToCreateScrewAndThreadedInsertHole037"
  Angle = 360
  Axis = (0,1,0)
  Base = (0,0,0)
  FaceMakerClass = Part::FaceMakerBullseye
  Placement = pos=(89.5,0,3.5) rot=(0,0,1;0rad)
  Solid = false
  Source = -> Face102
  Symmetric = false
FEATURE [Part::Feature] Face103
  shape: bbox 3.5 x 17.8 x 2e-07 mm, 1 faces, 0 solids (baked)
FEATURE [Part::Revolution] Revolve111  label="removeToCreateScrewAndThreadedInsertHole038"
  Angle = 360
  Axis = (0,1,0)
  Base = (0,0,0)
  FaceMakerClass = Part::FaceMakerBullseye
  Placement = pos=(109.5,4.7,3.5) rot=(0,0,1;0rad)
  Solid = false
  Source = -> Face103
  Symmetric = false
FEATURE [Part::Feature] Face104
  shape: bbox 3.5 x 17.8 x 2e-07 mm, 1 faces, 0 solids (baked)
FEATURE [Part::Revolution] Revolve112  label="removeToCreateScrewAndThreadedInsertHole039"
  Angle = 360
  Axis = (0,1,0)
  Base = (0,0,0)
  FaceMakerClass = Part::FaceMakerBullseye
  Placement = pos=(109.5,4.7,68.5) rot=(0,0,1;0rad)
  Solid = false
  Source = -> Face104
  Symmetric = false
FEATURE [Part::MultiFuse] Fusion081  label="removeToCreateScrewAndThreadedInsertHole040"
  Shapes = -> [Revolve107,Revolve108,Revolve109,Revolve110,Revolve111,Revolve112]
FEATURE [Part::MultiFuse] Fusion082  label="casePillars002"
  Shapes = -> [Revolve094,Revolve092,Revolve090,Revolve089,Revolve091,Revolve093]
FEATURE [Part::Cut] Cut037  label="casePillars003"
  Base = -> Fusion082
  Tool = -> Fusion081
FEATURE [Sketcher::SketchObject] Sketch051
  FullyConstrained = true
  Placement = pos=(117,19,0) rot=(0.57735,0.57735,0.57735;2.0944rad)
  sketch-geometry (48):
    g0: LineSegment StartX=-49.19 StartY=69.25 StartZ=0 EndX=-49.19 EndY=66.25 EndZ=0
    g1: LineSegment StartX=-49.19 StartY=63.5 StartZ=0 EndX=-49.19 EndY=60.5 EndZ=0
    g2: LineSegment StartX=-49.19 StartY=57.75 StartZ=0 EndX=-49.19 EndY=54.75 EndZ=0
    g3: LineSegment StartX=-49.19 StartY=52 StartZ=0 EndX=-49.19 EndY=49 EndZ=0
    g4: LineSegment StartX=-49.19 StartY=46.25 StartZ=0 EndX=-49.19 EndY=43.25 EndZ=0
    g5: LineSegment StartX=-49.19 StartY=40.5 StartZ=0 EndX=-49.19 EndY=37.5 EndZ=0
    g6: LineSegment StartX=-49.19 StartY=34.5 StartZ=0 EndX=-49.19 EndY=31.5 EndZ=0
    g7: LineSegment StartX=-49.19 StartY=28.75 StartZ=0 EndX=-49.19 EndY=25.75 EndZ=0
    g8: LineSegment StartX=-49.19 StartY=23 StartZ=0 EndX=-49.19 EndY=20 EndZ=0
    g9: LineSegment StartX=-49.19 StartY=17.25 StartZ=0 EndX=-49.19 EndY=14.25 EndZ=0
    g10: LineSegment StartX=-49.19 StartY=11.5 StartZ=0 EndX=-49.19 EndY=8.5 EndZ=0
    g11: LineSegment StartX=-49.19 StartY=5.75 StartZ=0 EndX=-49.19 EndY=2.75 EndZ=0
    g12: ArcOfCircle CenterX=-1.5 CenterY=67.75 CenterZ=0 NormalX=0 NormalY=0 NormalZ=1 AngleXU=0 Radius=1.5 StartAngle=4.71239 EndAngle=7.85398
    g13: ArcOfCircle CenterX=-1.5 CenterY=62 CenterZ=0 NormalX=0 NormalY=0 NormalZ=1 AngleXU=0 Radius=1.5 StartAngle=4.71239 EndAngle=7.85398
    g14: ArcOfCircle CenterX=-1.5 CenterY=56.25 CenterZ=0 NormalX=0 NormalY=0 NormalZ=1 AngleXU=0 Radius=1.5 StartAngle=4.71239 EndAngle=7.85398
    g15: ArcOfCircle CenterX=-11.49 CenterY=50.5 CenterZ=0 NormalX=0 NormalY=0 NormalZ=1 AngleXU=0 Radius=1.5 StartAngle=4.71239 EndAngle=7.85398
    g16: ArcOfCircle CenterX=-16.28 CenterY=44.75 CenterZ=0 NormalX=0 NormalY=0 NormalZ=1 AngleXU=0 Radius=1.5 StartAngle=4.71239 EndAngle=7.85398
    g17: ArcOfCircle CenterX=-18.2337 CenterY=39 CenterZ=0 NormalX=0 NormalY=0 NormalZ=1 AngleXU=0 Radius=1.5 StartAngle=4.71485 EndAngle=7.85398
    g18: ArcOfCircle CenterX=-16.2837 CenterY=27.25 CenterZ=0 NormalX=0 NormalY=0 NormalZ=1 AngleXU=0 Radius=1.5 StartAngle=4.71485 EndAngle=7.85398
    g19: ArcOfCircle CenterX=-18.2337 CenterY=33 CenterZ=0 NormalX=0 NormalY=0 NormalZ=1 AngleXU=0 Radius=1.5 StartAngle=4.71485 EndAngle=7.85398
    g20: ArcOfCircle CenterX=-11.49 CenterY=21.5 CenterZ=0 NormalX=0 NormalY=0 NormalZ=1 AngleXU=0 Radius=1.5 StartAngle=4.71239 EndAngle=7.85398
    g21: ArcOfCircle CenterX=-1.5 CenterY=4.25 CenterZ=0 NormalX=0 NormalY=0 NormalZ=1 AngleXU=0 Radius=1.5 StartAngle=4.71239 EndAngle=7.85398
    g22: ArcOfCircle CenterX=-1.5 CenterY=10 CenterZ=0 NormalX=0 NormalY=0 NormalZ=1 AngleXU=0 Radius=1.5 StartAngle=4.71239 EndAngle=7.85398
    g23: ArcOfCircle CenterX=-1.5 CenterY=15.75 CenterZ=0 NormalX=0 NormalY=0 NormalZ=1 AngleXU=0 Radius=1.5 StartAngle=4.71239 EndAngle=7.85398
    g24: LineSegment StartX=-49.19 StartY=69.25 StartZ=0 EndX=-1.5 EndY=69.25 EndZ=0
    g25: LineSegment StartX=-49.19 StartY=66.25 StartZ=0 EndX=-1.5 EndY=66.25 EndZ=0
    g26: LineSegment StartX=-49.19 StartY=63.5 StartZ=0 EndX=-1.5 EndY=63.5 EndZ=0
    g27: LineSegment StartX=-49.19 StartY=60.5 StartZ=0 EndX=-1.5 EndY=60.5 EndZ=0
    g28: LineSegment StartX=-49.19 StartY=57.75 StartZ=0 EndX=-1.5 EndY=57.75 EndZ=0
    g29: LineSegment StartX=-49.19 StartY=54.75 StartZ=0 EndX=-1.5 EndY=54.75 EndZ=0
    g30: LineSegment StartX=-49.19 StartY=52 StartZ=0 EndX=-11.49 EndY=52 EndZ=0
    g31: LineSegment StartX=-49.19 StartY=49 StartZ=0 EndX=-11.49 EndY=49 EndZ=0
    g32: LineSegment StartX=-49.19 StartY=46.25 StartZ=0 EndX=-16.28 EndY=46.25 EndZ=0
    g33: LineSegment StartX=-49.19 StartY=43.25 StartZ=0 EndX=-16.28 EndY=43.25 EndZ=0
    g34: LineSegment StartX=-49.19 StartY=40.5 StartZ=0 EndX=-18.2337 EndY=40.5 EndZ=0
    g35: LineSegment StartX=-49.19 StartY=37.5 StartZ=0 EndX=-18.23 EndY=37.5 EndZ=0
    g36: LineSegment StartX=-49.19 StartY=34.5 StartZ=0 EndX=-18.2337 EndY=34.5 EndZ=0
    g37: LineSegment StartX=-49.19 StartY=31.5 StartZ=0 EndX=-18.23 EndY=31.5 EndZ=0
    g38: LineSegment StartX=-49.19 StartY=28.75 StartZ=0 EndX=-16.2837 EndY=28.75 EndZ=0
    g39: LineSegment StartX=-49.19 StartY=25.75 StartZ=0 EndX=-16.28 EndY=25.75 EndZ=0
    g40: LineSegment StartX=-49.19 StartY=23 StartZ=0 EndX=-11.49 EndY=23 EndZ=0
    g41: LineSegment StartX=-49.19 StartY=20 StartZ=0 EndX=-11.49 EndY=20 EndZ=0
    g42: LineSegment StartX=-49.19 StartY=17.25 StartZ=0 EndX=-1.5 EndY=17.25 EndZ=0
    g43: LineSegment StartX=-49.19 StartY=14.25 StartZ=0 EndX=-1.5 EndY=14.25 EndZ=0
    g44: LineSegment StartX=-49.19 StartY=11.5 StartZ=0 EndX=-1.5 EndY=11.5 EndZ=0
    g45: LineSegment StartX=-49.19 StartY=8.5 StartZ=0 EndX=-1.5 EndY=8.5 EndZ=0
    g46: LineSegment StartX=-49.19 StartY=5.75 StartZ=0 EndX=-1.5 EndY=5.75 EndZ=0
    g47: LineSegment StartX=-49.19 StartY=2.75 StartZ=0 EndX=-1.5 EndY=2.75 EndZ=0
  constraints (120):
    c: Vertical(g0)
    c: Distance(g0) = 3
    c: Block(g0)
    c: Vertical(g1)
    c: Distance(g1) = 3
    c: Vertical(g2)
    c: Equal(g0,g2) = 3
    c: Block(g2)
    c: Vertical(g3)
    c: Equal(g1,g3) = 3
    c: Vertical(g4)
    c: Equal(g0,g4) = 3
    c: Block(g4)
    c: Vertical(g5)
    c: Equal(g1,g5) = 3
    c: Vertical(g6)
    c: Equal(g0,g6) = 3
    c: Block(g6)
    c: Vertical(g7)
    c: Equal(g1,g7) = 3
    c: Vertical(g8)
    c: Equal(g0,g8) = 3
    c: Block(g8)
    c: Vertical(g9)
    c: Equal(g1,g9) = 3
    c: Vertical(g10)
    c: Equal(g0,g10) = 3
    c: Block(g10)
    c: Vertical(g11)
    c: Equal(g1,g11) = 3
    c: Block(g12)
    c: Block(g13)
    c: Block(g14)
    c: Block(g15)
    c: Block(g16)
    c: Block(g17)
    c: Block(g18)
    c: Block(g19)
    c: Block(g20)
    c: Block(g21)
    c: Block(g22)
    c: Block(g23)
    c: Block(g11)
    c: Block(g9)
    c: Block(g7)
    c: Block(g5)
    c: Block(g3)
    c: Block(g1)
    c: Coincident(g24,g0)
    c: Coincident(g24,g12)
    c: Horizontal(g24)
    c: Coincident(g25,g0)
    c: Coincident(g25,g12)
    c: Horizontal(g25)
    c: Coincident(g26,g1)
    c: Coincident(g26,g13)
    c: Horizontal(g26)
    c: Coincident(g27,g1)
    c: Coincident(g27,g13)
    c: Horizontal(g27)
    c: Coincident(g28,g2)
    c: Coincident(g28,g14)
    c: Horizontal(g28)
    c: Coincident(g29,g2)
    c: Coincident(g29,g14)
    c: Horizontal(g29)
    c: Coincident(g30,g3)
    c: Coincident(g30,g15)
    c: Horizontal(g30)
    c: Coincident(g31,g3)
    c: Coincident(g31,g15)
    c: Horizontal(g31)
    c: Coincident(g32,g4)
    c: Coincident(g32,g16)
    c: Horizontal(g32)
    c: Coincident(g33,g4)
    c: Coincident(g33,g16)
    c: Horizontal(g33)
    c: Coincident(g34,g5)
    c: Coincident(g34,g17)
    c: Horizontal(g34)
    c: Coincident(g35,g5)
    c: Coincident(g35,g17)
    c: Horizontal(g35)
    c: Coincident(g36,g6)
    c: Coincident(g36,g19)
    c: Horizontal(g36)
    c: Coincident(g37,g6)
    c: Coincident(g37,g19)
    c: Horizontal(g37)
    c: Coincident(g38,g7)
    c: Coincident(g38,g18)
    c: Horizontal(g38)
    c: Coincident(g39,g7)
    c: Coincident(g39,g18)
    c: Horizontal(g39)
    c: Coincident(g40,g8)
    c: Coincident(g40,g20)
    c: Horizontal(g40)
    c: Coincident(g41,g8)
    c: Coincident(g41,g20)
    c: Horizontal(g41)
    c: Coincident(g42,g9)
    c: Coincident(g42,g23)
    c: Horizontal(g42)
    c: Coincident(g43,g9)
    c: Coincident(g43,g23)
    c: Horizontal(g43)
    c: Coincident(g44,g10)
    c: Coincident(g44,g22)
    c: Horizontal(g44)
    c: Coincident(g45,g10)
    c: Coincident(g45,g22)
    c: Horizontal(g45)
    c: Coincident(g46,g11)
    c: Coincident(g46,g21)
    c: Horizontal(g46)
    c: Coincident(g47,g11)
    c: Coincident(g47,g21)
    c: Horizontal(g47)
FEATURE [Part::Extrusion] Extrude042
  Base = -> Sketch051
  Dir = (1,-2e-16,2e-16)
  DirMode = 2
  FaceMakerClass = Part::FaceMakerBullseye
  LengthFwd = 19
  LengthRev = 0
  Placement = pos=(-19,0,0) rot=(0,0,1;0rad)
  Solid = true
  Symmetric = false
FEATURE [Part::Fillet] Fillet035  label="removeToCreateVentalationHoles"
  Base = -> Extrude042
  Edges = <same value as first occurrence — deduplicated (x6 in doc)>
  Placement = pos=(7,0,0) rot=(0,0,1;0rad)
FEATURE [Part::Cut] Cut038  label="top017"
  Base = -> Cut033
  Tool = -> Fillet035
FEATURE [Sketcher::SketchObject] Sketch052  label="bottomSketch001"
  FullyConstrained = true
  sketch-geometry (45):
    g0: LineSegment StartX=6.29999 StartY=8 StartZ=0 EndX=3.29999 EndY=8 EndZ=0
    g1: LineSegment StartX=3.29999 StartY=8 StartZ=0 EndX=3.29999 EndY=-6.03275e-07 EndZ=0
    g2: ArcOfCircle CenterX=8.29999 CenterY=5 CenterZ=0 NormalX=0 NormalY=0 NormalZ=1 AngleXU=0 Radius=2 StartAngle=3.14159 EndAngle=4.71239
    g3: LineSegment StartX=6.29999 StartY=8 StartZ=0 EndX=6.29999 EndY=5 EndZ=0
    g4: ArcOfCircle CenterX=105 CenterY=19 CenterZ=0 NormalX=0 NormalY=0 NormalZ=1 AngleXU=0 Radius=12.7 StartAngle=4.71239 EndAngle=5.94289
    g5-g11: Circle x7 (B-spline internal-alignment scaffolding for g12; pole/knot coordinates omitted)
    g12: BSplineCurve PolesCount=7 KnotsCount=5 Degree=3 IsPeriodic=0
    g13-g17: GeomPoint x5 (B-spline internal-alignment scaffolding for g12; pole/knot coordinates omitted)
    g18: ArcOfCircle CenterX=105 CenterY=19 CenterZ=0 NormalX=0 NormalY=0 NormalZ=1 AngleXU=0 Radius=15.7 StartAngle=5.81226 EndAngle=6.28319
    g19: BSplineCurve PolesCount=5 KnotsCount=3 Degree=3 IsPeriodic=0
    g20: LineSegment StartX=8.29999 StartY=3 StartZ=0 EndX=101.7 EndY=3 EndZ=0
    g21: LineSegment StartX=3.29999 StartY=-6.03275e-07 StartZ=0 EndX=105 EndY=-6.03275e-07 EndZ=0
    g22: LineSegment StartX=120.974 StartY=8.71251 StartZ=0 EndX=122.332 EndY=7.83778 EndZ=0
    g23: LineSegment StartX=105 StartY=-6.03274e-07 StartZ=0 EndX=113 EndY=-6.03274e-07 EndZ=0
    g24: ArcOfCircle CenterX=105 CenterY=19 CenterZ=0 NormalX=0 NormalY=0 NormalZ=1 AngleXU=0 Radius=20.6155 StartAngle=5.11091 EndAngle=5.71103
    g25: ArcOfCircle CenterX=117.7 CenterY=19 CenterZ=0 NormalX=0 NormalY=0 NormalZ=1 AngleXU=0 Radius=3 StartAngle=1.2e-15 EndAngle=2.10468
    g26: Circle CenterX=116.345 CenterY=16.3232 CenterZ=0 NormalX=0 NormalY=0 NormalZ=1 AngleXU=0 Radius=1
    g27: Circle CenterX=117.24 CenterY=15.7584 CenterZ=0 NormalX=0 NormalY=0 NormalZ=1 AngleXU=0 Radius=1
    g28: Circle CenterX=116.972 CenterY=14.7612 CenterZ=0 NormalX=0 NormalY=0 NormalZ=1 AngleXU=0 Radius=1
    g29: BSplineCurve PolesCount=3 KnotsCount=2 Degree=2 IsPeriodic=0
    g30: GeomPoint X=116.345 Y=16.3232 Z=0
    g31: GeomPoint X=116.972 Y=14.7612 Z=0
    g32: Circle CenterX=115.828 CenterY=17.157 CenterZ=0 NormalX=0 NormalY=0 NormalZ=1 AngleXU=0 Radius=1
    g33: Circle CenterX=115.841 CenterY=16.639 CenterZ=0 NormalX=0 NormalY=0 NormalZ=1 AngleXU=0 Radius=1
    g34: Circle CenterX=116.345 CenterY=16.3232 CenterZ=0 NormalX=0 NormalY=0 NormalZ=1 AngleXU=0 Radius=1
    g35: BSplineCurve PolesCount=3 KnotsCount=2 Degree=2 IsPeriodic=0
    g36: GeomPoint X=115.828 Y=17.157 Z=0
    g37: GeomPoint X=116.345 Y=16.3232 Z=0
    g38: LineSegment StartX=115.828 StartY=17.157 StartZ=0 EndX=115.828 EndY=20.8307 EndZ=0
    g39: Circle CenterX=115.828 CenterY=20.8307 CenterZ=0 NormalX=0 NormalY=0 NormalZ=1 AngleXU=0 Radius=1
    g40: Circle CenterX=115.831 CenterY=21.3396 CenterZ=0 NormalX=0 NormalY=0 NormalZ=1 AngleXU=0 Radius=1
    g41: Circle CenterX=116.173 CenterY=21.5825 CenterZ=0 NormalX=0 NormalY=0 NormalZ=1 AngleXU=0 Radius=1
    g42: BSplineCurve PolesCount=3 KnotsCount=2 Degree=2 IsPeriodic=0
    g43: GeomPoint X=115.828 Y=20.8307 Z=0
    g44: GeomPoint X=116.173 Y=21.5825 Z=0
  constraints (70):
    c: Horizontal(g0)
    c: Distance(g0) = 3
    c: Coincident(g1,g0)
    c: Vertical(g1)
    c: Block(g2)
    c: Block(g0)
    c: Coincident(g3,g0)
    c: Coincident(g3,g2)
    c: Vertical(g3)
    c: Block(g1)
    c: Block(g4)
    c: Coincident(g19,g4)
    c: Block(g19)
    c: Equal(g5, g6-g11) x6
    c: InternalAlignment(g5-g11 -> g12) x7
    c: InternalAlignment(g13-g17 -> g12) x5
    c: Block(g12)
    c: Coincident(g18,g12)
    c: Block(g18)
    c: Coincident(g20,g2)
    c: Coincident(g20,g19)
    c: Horizontal(g20)
    c: Distance(g20) = 93.4
    c: Coincident(g21,g1)
    c: Horizontal(g21)
    c: Distance(g21) = 101.7
    c: Horizontal(g23)
    c: Distance(g23) = 8
    c: Coincident(g24,g23)
    c: Block(g23)
    c: Coincident(g22,g24)
    c: Block(g24)
    c: Block(g22)
    c: Distance(g22) = 1.61553
    c: Coincident(g25,g18)
    c: Block(g25)
    c: Weight(g26) = 1
    c: Equal(g26,g27)
    c: Equal(g26,g28)
    c: Coincident(g29,g4)
    c: InternalAlignment(g26,g29)
    c: InternalAlignment(g27,g29)
    c: InternalAlignment(g28,g29)
    c: InternalAlignment(g30,g29)
    c: InternalAlignment(g31,g29)
    c: Block(g29)
    c: Weight(g32) = 1
    c: Equal(g32,g33)
    c: Equal(g32,g34)
    c: Coincident(g35,g29)
    c: InternalAlignment(g32,g35)
    c: InternalAlignment(g33,g35)
    c: InternalAlignment(g34,g35)
    c: InternalAlignment(g36,g35)
    c: InternalAlignment(g37,g35)
    c: Block(g35)
    c: Coincident(g38,g35)
    c: Vertical(g38)
    c: Block(g38)
    c: Coincident(g42,g38)
    c: Weight(g39) = 1
    c: Equal(g39,g40)
    c: Equal(g39,g41)
    c: Coincident(g42,g25)
    c: InternalAlignment(g39,g42)
    c: InternalAlignment(g40,g42)
    c: InternalAlignment(g41,g42)
    c: InternalAlignment(g43,g42)
    c: InternalAlignment(g44,g42)
    c: Block(g42)
FEATURE [Part::Extrusion] Extrude043  label="bottom010"
  Base = -> Sketch052
  Dir = (0,0,1)
  DirMode = 2
  FaceMakerClass = Part::FaceMakerBullseye
  LengthFwd = 71.4
  LengthRev = 0
  Placement = pos=(0,0,0.3) rot=(0,0,1;0rad)
  Solid = true
  Symmetric = false
FEATURE [Sketcher::SketchObject] Sketch053  label="topSketch013"
  FullyConstrained = true
  sketch-geometry (22):
    g0: LineSegment StartX=5.21097e-06 StartY=3 StartZ=0 EndX=5.21097e-06 EndY=19 EndZ=0
    g1: ArcOfCircle CenterX=19 CenterY=19 CenterZ=0 NormalX=0 NormalY=0 NormalZ=1 AngleXU=0 Radius=19 StartAngle=1.5708 EndAngle=3.14159
    g2: ArcOfCircle CenterX=19 CenterY=19 CenterZ=0 NormalX=0 NormalY=0 NormalZ=1 AngleXU=0 Radius=16 StartAngle=1.5708 EndAngle=3.14159
    g3: LineSegment StartX=114 StartY=35 StartZ=0 EndX=19 EndY=35 EndZ=0
    g4: LineSegment StartX=5.21097e-06 StartY=3 StartZ=0 EndX=5.21097e-06 EndY=0 EndZ=0
    g5: LineSegment StartX=3 StartY=0 StartZ=0 EndX=5.21097e-06 EndY=0 EndZ=0
    g6: LineSegment StartX=3 StartY=19 StartZ=0 EndX=3 EndY=0 EndZ=0
    g7: LineSegment StartX=19 StartY=38 StartZ=0 EndX=124 EndY=38 EndZ=0
    g8: Circle CenterX=119 CenterY=35 CenterZ=0 NormalX=0 NormalY=0 NormalZ=1 AngleXU=0 Radius=1
    g9: Circle CenterX=121 CenterY=35 CenterZ=0 NormalX=0 NormalY=0 NormalZ=1 AngleXU=0 Radius=1
    g10: Circle CenterX=121 CenterY=33 CenterZ=0 NormalX=0 NormalY=0 NormalZ=1 AngleXU=0 Radius=1
    g11: BSplineCurve PolesCount=3 KnotsCount=2 Degree=2 IsPeriodic=0
    g12: GeomPoint X=119 Y=35 Z=0
    g13: GeomPoint X=121 Y=33 Z=0
    g14: LineSegment StartX=119 StartY=35 StartZ=0 EndX=114 EndY=35 EndZ=0
    g15: ArcOfCircle CenterX=105 CenterY=19 CenterZ=0 NormalX=0 NormalY=0 NormalZ=1 AngleXU=0 Radius=16 StartAngle=5.60905 EndAngle=6.28319
    g16: LineSegment StartX=121 StartY=33 StartZ=0 EndX=121 EndY=19 EndZ=0
    g17: LineSegment StartX=117.5 StartY=9.01251 StartZ=0 EndX=121.163 EndY=9.0125 EndZ=0
    g18: ArcOfCircle CenterX=105 CenterY=19 CenterZ=0 NormalX=0 NormalY=0 NormalZ=1 AngleXU=0 Radius=20.6155 StartAngle=5.7297 EndAngle=6.28319
    g19: LineSegment StartX=121.163 StartY=9.0125 StartZ=0 EndX=122.538 EndY=8.16329 EndZ=0
    g20: LineSegment StartX=124 StartY=38 StartZ=0 EndX=125.616 EndY=38 EndZ=0
    g21: LineSegment StartX=125.616 StartY=19 StartZ=0 EndX=125.616 EndY=38 EndZ=0
  constraints (50):
    c: Vertical(g0)
    c: Block(g0)
    c: Coincident(g1,g0)
    c: Block(g1)
    c: Coincident(g2,g1)
    c: Block(g2)
    c: Coincident(g3,g2)
    c: Horizontal(g3)
    c: Tangent(g3,g2)
    c: Coincident(g4,g0)
    c: Distance(g4) = 3
    c: Vertical(g4)
    c: Coincident(g5,g4)
    c: Horizontal(g5)
    c: Coincident(g6,g2)
    c: Coincident(g6,g5)
    c: Vertical(g6)
    c: Horizontal(g7)
    c: Distance(g7) = 105
    c: Coincident(g7,g1)
    c: Block(g3)
    c: Weight(g8) = 1
    c: Equal(g8,g9)
    c: Equal(g8,g10)
    c: InternalAlignment(g8,g11)
    c: InternalAlignment(g9,g11)
    c: InternalAlignment(g10,g11)
    c: InternalAlignment(g12,g11)
    c: InternalAlignment(g13,g11)
    c: Block(g11)
    c: Coincident(g14,g11)
    c: Coincident(g14,g3)
    c: Horizontal(g14)
    c: Block(g15)
    c: Coincident(g16,g11)
    c: Coincident(g16,g15)
    c: Vertical(g16)
    c: Distance(g16) = 14
    c: Coincident(g17,g15)
    c: Block(g18)
    c: Coincident(g19,g18)
    c: Coincident(g20,g7)
    c: Horizontal(g20)
    c: Vertical(g21)
    c: Coincident(g20,g21)
    c: Block(g20)
    c: Block(g21)
    c: Block(g19)
    c: Block(g17)
    c: Distance(g20) = 1.61553
FEATURE [Part::Extrusion] Extrude044
  Base = -> Sketch053
  Dir = (0,0,1)
  DirMode = 2
  FaceMakerClass = Part::FaceMakerBullseye
  LengthFwd = 72
  LengthRev = 0
  Solid = true
  Symmetric = false
FEATURE [Part::Fillet] Fillet036  label="top018"
  Base = -> Extrude044
  Edges = 1 edges r=2: [Edge41]
FEATURE [Sketcher::SketchObject] Sketch054
  FullyConstrained = false
  Placement = pos=(0,0,0) rot=(1,0,0;1.5708rad)
  sketch-geometry (24):
    g0: ArcOfCircle CenterX=-4 CenterY=-10.5 CenterZ=0 NormalX=0 NormalY=0 NormalZ=1 AngleXU=0 Radius=1.5 StartAngle=6e-16 EndAngle=3.14159
    g1: ArcOfCircle CenterX=-34.2 CenterY=-10.5 CenterZ=0 NormalX=0 NormalY=0 NormalZ=1 AngleXU=0 Radius=1.5 StartAngle=0 EndAngle=3.14159
    g2: ArcOfCircle CenterX=-34.2 CenterY=-27.7 CenterZ=0 NormalX=0 NormalY=0 NormalZ=1 AngleXU=0 Radius=1.5 StartAngle=3.14159 EndAngle=6.28319
    g3: ArcOfCircle CenterX=-4 CenterY=-27.7 CenterZ=0 NormalX=0 NormalY=0 NormalZ=1 AngleXU=0 Radius=1.5 StartAngle=3.1416 EndAngle=6.28319
    g4: ArcOfCircle CenterX=-10 CenterY=-4.3 CenterZ=0 NormalX=0 NormalY=0 NormalZ=1 AngleXU=0 Radius=1.5 StartAngle=2e-16 EndAngle=3.14159
    g5: ArcOfCircle CenterX=-16.1 CenterY=-1.8 CenterZ=0 NormalX=0 NormalY=0 NormalZ=1 AngleXU=0 Radius=1.5 StartAngle=5e-16 EndAngle=3.14159
    g6: ArcOfCircle CenterX=-22.1 CenterY=-1.8 CenterZ=0 NormalX=0 NormalY=0 NormalZ=1 AngleXU=0 Radius=1.5 StartAngle=5e-16 EndAngle=3.14159
    g7: ArcOfCircle CenterX=-28.2 CenterY=-4.3 CenterZ=0 NormalX=0 NormalY=0 NormalZ=1 AngleXU=0 Radius=1.5 StartAngle=2e-16 EndAngle=3.14159
    g8: ArcOfCircle CenterX=-10 CenterY=-33.9 CenterZ=0 NormalX=0 NormalY=0 NormalZ=1 AngleXU=0 Radius=1.5 StartAngle=3.14159 EndAngle=6.28319
    g9: ArcOfCircle CenterX=-16.1 CenterY=-36.4 CenterZ=0 NormalX=0 NormalY=0 NormalZ=1 AngleXU=0 Radius=1.5 StartAngle=3.14159 EndAngle=6.28319
    g10: ArcOfCircle CenterX=-22.1 CenterY=-36.4 CenterZ=0 NormalX=0 NormalY=0 NormalZ=1 AngleXU=0 Radius=1.5 StartAngle=3.14159 EndAngle=6.28319
    g11: ArcOfCircle CenterX=-28.2 CenterY=-33.9 CenterZ=0 NormalX=0 NormalY=0 NormalZ=1 AngleXU=0 Radius=1.5 StartAngle=3.14159 EndAngle=6.28319
    g12: LineSegment StartX=-35.7 StartY=-10.5 StartZ=0 EndX=-35.7 EndY=-27.7 EndZ=0
    g13: LineSegment StartX=-32.7 StartY=-10.5 StartZ=0 EndX=-32.7 EndY=-27.7 EndZ=0
    g14: LineSegment StartX=-29.7 StartY=-33.9 StartZ=0 EndX=-29.7 EndY=-4.3 EndZ=0
    g15: LineSegment StartX=-26.7 StartY=-33.9 StartZ=0 EndX=-26.7 EndY=-4.3 EndZ=0
    g16: LineSegment StartX=-2.5 StartY=-10.5 StartZ=0 EndX=-2.5 EndY=-27.7 EndZ=0
    g17: LineSegment StartX=-8.5 StartY=-4.3 StartZ=0 EndX=-8.5 EndY=-33.9 EndZ=0
    g18: LineSegment StartX=-5.5 StartY=-10.5 StartZ=0 EndX=-5.5 EndY=-27.7 EndZ=0
    g19: LineSegment StartX=-11.5 StartY=-4.3 StartZ=0 EndX=-11.5 EndY=-33.9 EndZ=0
    g20: LineSegment StartX=-14.6 StartY=-1.8 StartZ=0 EndX=-14.6 EndY=-36.4 EndZ=0
    g21: LineSegment StartX=-17.6 StartY=-1.8 StartZ=0 EndX=-17.6 EndY=-36.4 EndZ=0
    g22: LineSegment StartX=-20.6 StartY=-36.4 StartZ=0 EndX=-20.6 EndY=-1.8 EndZ=0
    g23: LineSegment StartX=-23.6 StartY=-1.8 StartZ=0 EndX=-23.6 EndY=-36.4 EndZ=0
  constraints (48):
    c: Block(g0)
    c: Block(g1)
    c: Block(g2)
    c: Block(g3)
    c: Block(g4)
    c: Block(g5)
    c: Block(g6)
    c: Block(g7)
    c: Block(g8)
    c: Block(g9)
    c: Block(g10)
    c: Block(g11)
    c: Coincident(g12,g1)
    c: Coincident(g12,g2)
    c: Vertical(g12)
    c: Coincident(g13,g1)
    c: Coincident(g13,g2)
    c: Vertical(g13)
    c: Coincident(g14,g11)
    c: Coincident(g14,g7)
    c: Vertical(g14)
    c: Coincident(g15,g11)
    c: Coincident(g15,g7)
    c: Vertical(g15)
    c: Coincident(g16,g0)
    c: Coincident(g16,g3)
    c: Vertical(g16)
    c: Coincident(g17,g4)
    c: Coincident(g17,g8)
    c: Vertical(g17)
    c: Coincident(g18,g0)
    c: Coincident(g18,g3)
    c: Vertical(g18)
    c: Coincident(g19,g4)
    c: Coincident(g19,g8)
    c: Vertical(g19)
    c: Coincident(g20,g5)
    c: Coincident(g20,g9)
    c: Vertical(g20)
    c: Coincident(g21,g5)
    c: Coincident(g21,g9)
    c: Vertical(g21)
    c: Coincident(g22,g10)
    c: Coincident(g22,g6)
    c: Vertical(g22)
    c: Coincident(g23,g6)
    c: Coincident(g23,g10)
    c: Vertical(g23)
FEATURE [Part::Extrusion] Extrude045  label="removeToCreateFanGrillHoles003"
  Base = -> Sketch054
  Dir = (0,-1,6e-16)
  DirMode = 2
  FaceMakerClass = Part::FaceMakerBullseye
  LengthFwd = 10
  LengthRev = 0
  Placement = pos=(65.4,44,54.82) rot=(0,0,1;0rad)
  Solid = true
  Symmetric = false
FEATURE [Part::Feature] Face105 .. Face108  x4 (patterned run collapsed; names and placements below)
  shape: bbox 3.5 x 17.8 x 2e-07 mm, 1 faces, 0 solids (baked)
FEATURE [Part::Revolution] Revolve113  label="removeToCreateScrewAndThreadedInsertHole041"
  Angle = 360
  Axis = (0,1,0)
  Base = (0,0,0)
  FaceMakerClass = Part::FaceMakerBullseye
  Placement = pos=(62.3,30.3,19.7) rot=(0,0,1;0rad)
  Solid = false
  Source = -> Face105
  Symmetric = false
FEATURE [Part::Revolution] Revolve114  label="removeToCreateScrewAndThreadedInsertHole042"
  Angle = 360
  Axis = (0,1,0)
  Base = (0,0,0)
  FaceMakerClass = Part::FaceMakerBullseye
  Placement = pos=(62.3,30.3,51.7) rot=(0,0,1;0rad)
  Solid = false
  Source = -> Face106
  Symmetric = false
FEATURE [Part::Revolution] Revolve115  label="removeToCreateScrewAndThreadedInsertHole043"
  Angle = 360
  Axis = (0,1,0)
  Base = (0,0,0)
  FaceMakerClass = Part::FaceMakerBullseye
  Placement = pos=(30.3,30.3,19.7) rot=(0,0,1;0rad)
  Solid = false
  Source = -> Face107
  Symmetric = false
FEATURE [Part::Revolution] Revolve116  label="removeToCreateScrewAndThreadedInsertHole044"
  Angle = 360
  Axis = (0,1,0)
  Base = (0,0,0)
  FaceMakerClass = Part::FaceMakerBullseye
  Placement = pos=(30.3,30.3,51.7) rot=(0,0,1;0rad)
  Solid = false
  Source = -> Face108
  Symmetric = false
FEATURE [Part::MultiFuse] Fusion083  label="createThreadedInsertHolesForFan004"
  Shapes = -> [Revolve113,Revolve114,Revolve115,Revolve116]
FEATURE [Part::Box] Box024  label="removeToCreteHoleForPlugHousing026"
  AttacherType = Attacher::AttachEngine3D
  Height = 28.6
  Length = 10
  Placement = pos=(-2,0,21.7) rot=(0,0,1;0rad)
  Width = 19
FEATURE [Part::Cylinder] Cylinder038  label="removeToCreteHoleForPlugHousing027"
  Angle = 360
  AttacherType = Attacher::AttachEngine3D
  Height = 20
  Placement = pos=(-2,19,36) rot=(0,1,0;1.5708rad)
  Radius = 14.3
FEATURE [Part::MultiFuse] Fusion084  label="removeToCreteHoleForPlugHousing028"
  Shapes = -> [Box024,Cylinder038]
FEATURE [Part::Cylinder] Cylinder039
  Angle = 360
  AttacherType = Attacher::AttachEngine3D
  Height = 20
  Placement = pos=(0,0,36.15) rot=(0,0,1;0rad)
  Radius = 14.3
FEATURE [Part::Cylinder] Cylinder040
  Angle = 360
  AttacherType = Attacher::AttachEngine3D
  Height = 10
  Placement = pos=(0,0,36.15) rot=(0,0,1;0rad)
  Radius = 4
FEATURE [Part::Box] Box025  label="removeToCreteHoleForPlugHousing030"
  AttacherType = Attacher::AttachEngine3D
  Height = 28.6
  Length = 20
  Placement = pos=(106.15,0,21.7) rot=(0,0,1;0rad)
  Width = 19
FEATURE [Part::MultiFuse] Fusion086  label="removeToCreteHoleForPlugHousing031"
  Placement = pos=(70,19,36) rot=(0,1,0;1.5708rad)
  Shapes = -> [Cylinder039,Cylinder040]
FEATURE [Part::MultiFuse] Fusion085  label="removeToCreteHoleForPlugHousing029"
  Shapes = -> [Box025,Fusion086]
FEATURE [Sketcher::SketchObject] Sketch055
  FullyConstrained = true
  Placement = pos=(117,19,0) rot=(0.57735,0.57735,0.57735;2.0944rad)
  sketch-geometry (48):
    g0: LineSegment StartX=-49.19 StartY=69.25 StartZ=0 EndX=-49.19 EndY=66.25 EndZ=0
    g1: LineSegment StartX=-49.19 StartY=63.5 StartZ=0 EndX=-49.19 EndY=60.5 EndZ=0
    g2: LineSegment StartX=-49.19 StartY=57.75 StartZ=0 EndX=-49.19 EndY=54.75 EndZ=0
    g3: LineSegment StartX=-49.19 StartY=52 StartZ=0 EndX=-49.19 EndY=49 EndZ=0
    g4: LineSegment StartX=-49.19 StartY=46.25 StartZ=0 EndX=-49.19 EndY=43.25 EndZ=0
    g5: LineSegment StartX=-49.19 StartY=40.5 StartZ=0 EndX=-49.19 EndY=37.5 EndZ=0
    g6: LineSegment StartX=-49.19 StartY=34.5 StartZ=0 EndX=-49.19 EndY=31.5 EndZ=0
    g7: LineSegment StartX=-49.19 StartY=28.75 StartZ=0 EndX=-49.19 EndY=25.75 EndZ=0
    g8: LineSegment StartX=-49.19 StartY=23 StartZ=0 EndX=-49.19 EndY=20 EndZ=0
    g9: LineSegment StartX=-49.19 StartY=17.25 StartZ=0 EndX=-49.19 EndY=14.25 EndZ=0
    g10: LineSegment StartX=-49.19 StartY=11.5 StartZ=0 EndX=-49.19 EndY=8.5 EndZ=0
    g11: LineSegment StartX=-49.19 StartY=5.75 StartZ=0 EndX=-49.19 EndY=2.75 EndZ=0
    g12: ArcOfCircle CenterX=-1.5 CenterY=67.75 CenterZ=0 NormalX=0 NormalY=0 NormalZ=1 AngleXU=0 Radius=1.5 StartAngle=4.71239 EndAngle=7.85398
    g13: ArcOfCircle CenterX=-1.5 CenterY=62 CenterZ=0 NormalX=0 NormalY=0 NormalZ=1 AngleXU=0 Radius=1.5 StartAngle=4.71239 EndAngle=7.85398
    g14: ArcOfCircle CenterX=-1.5 CenterY=56.25 CenterZ=0 NormalX=0 NormalY=0 NormalZ=1 AngleXU=0 Radius=1.5 StartAngle=4.71239 EndAngle=7.85398
    g15: ArcOfCircle CenterX=-11.49 CenterY=50.5 CenterZ=0 NormalX=0 NormalY=0 NormalZ=1 AngleXU=0 Radius=1.5 StartAngle=4.71239 EndAngle=7.85398
    g16: ArcOfCircle CenterX=-16.28 CenterY=44.75 CenterZ=0 NormalX=0 NormalY=0 NormalZ=1 AngleXU=0 Radius=1.5 StartAngle=4.71239 EndAngle=7.85398
    g17: ArcOfCircle CenterX=-18.2337 CenterY=39 CenterZ=0 NormalX=0 NormalY=0 NormalZ=1 AngleXU=0 Radius=1.5 StartAngle=4.71485 EndAngle=7.85398
    g18: ArcOfCircle CenterX=-16.2837 CenterY=27.25 CenterZ=0 NormalX=0 NormalY=0 NormalZ=1 AngleXU=0 Radius=1.5 StartAngle=4.71485 EndAngle=7.85398
    g19: ArcOfCircle CenterX=-18.2337 CenterY=33 CenterZ=0 NormalX=0 NormalY=0 NormalZ=1 AngleXU=0 Radius=1.5 StartAngle=4.71485 EndAngle=7.85398
    g20: ArcOfCircle CenterX=-11.49 CenterY=21.5 CenterZ=0 NormalX=0 NormalY=0 NormalZ=1 AngleXU=0 Radius=1.5 StartAngle=4.71239 EndAngle=7.85398
    g21: ArcOfCircle CenterX=-1.5 CenterY=4.25 CenterZ=0 NormalX=0 NormalY=0 NormalZ=1 AngleXU=0 Radius=1.5 StartAngle=4.71239 EndAngle=7.85398
    g22: ArcOfCircle CenterX=-1.5 CenterY=10 CenterZ=0 NormalX=0 NormalY=0 NormalZ=1 AngleXU=0 Radius=1.5 StartAngle=4.71239 EndAngle=7.85398
    g23: ArcOfCircle CenterX=-1.5 CenterY=15.75 CenterZ=0 NormalX=0 NormalY=0 NormalZ=1 AngleXU=0 Radius=1.5 StartAngle=4.71239 EndAngle=7.85398
    g24: LineSegment StartX=-49.19 StartY=69.25 StartZ=0 EndX=-1.5 EndY=69.25 EndZ=0
    g25: LineSegment StartX=-49.19 StartY=66.25 StartZ=0 EndX=-1.5 EndY=66.25 EndZ=0
    g26: LineSegment StartX=-49.19 StartY=63.5 StartZ=0 EndX=-1.5 EndY=63.5 EndZ=0
    g27: LineSegment StartX=-49.19 StartY=60.5 StartZ=0 EndX=-1.5 EndY=60.5 EndZ=0
    g28: LineSegment StartX=-49.19 StartY=57.75 StartZ=0 EndX=-1.5 EndY=57.75 EndZ=0
    g29: LineSegment StartX=-49.19 StartY=54.75 StartZ=0 EndX=-1.5 EndY=54.75 EndZ=0
    g30: LineSegment StartX=-49.19 StartY=52 StartZ=0 EndX=-11.49 EndY=52 EndZ=0
    g31: LineSegment StartX=-49.19 StartY=49 StartZ=0 EndX=-11.49 EndY=49 EndZ=0
    g32: LineSegment StartX=-49.19 StartY=46.25 StartZ=0 EndX=-16.28 EndY=46.25 EndZ=0
    g33: LineSegment StartX=-49.19 StartY=43.25 StartZ=0 EndX=-16.28 EndY=43.25 EndZ=0
    g34: LineSegment StartX=-49.19 StartY=40.5 StartZ=0 EndX=-18.2337 EndY=40.5 EndZ=0
    g35: LineSegment StartX=-49.19 StartY=37.5 StartZ=0 EndX=-18.23 EndY=37.5 EndZ=0
    g36: LineSegment StartX=-49.19 StartY=34.5 StartZ=0 EndX=-18.2337 EndY=34.5 EndZ=0
    g37: LineSegment StartX=-49.19 StartY=31.5 StartZ=0 EndX=-18.23 EndY=31.5 EndZ=0
    g38: LineSegment StartX=-49.19 StartY=28.75 StartZ=0 EndX=-16.2837 EndY=28.75 EndZ=0
    g39: LineSegment StartX=-49.19 StartY=25.75 StartZ=0 EndX=-16.28 EndY=25.75 EndZ=0
    g40: LineSegment StartX=-49.19 StartY=23 StartZ=0 EndX=-11.49 EndY=23 EndZ=0
    g41: LineSegment StartX=-49.19 StartY=20 StartZ=0 EndX=-11.49 EndY=20 EndZ=0
    g42: LineSegment StartX=-49.19 StartY=17.25 StartZ=0 EndX=-1.5 EndY=17.25 EndZ=0
    g43: LineSegment StartX=-49.19 StartY=14.25 StartZ=0 EndX=-1.5 EndY=14.25 EndZ=0
    g44: LineSegment StartX=-49.19 StartY=11.5 StartZ=0 EndX=-1.5 EndY=11.5 EndZ=0
    g45: LineSegment StartX=-49.19 StartY=8.5 StartZ=0 EndX=-1.5 EndY=8.5 EndZ=0
    g46: LineSegment StartX=-49.19 StartY=5.75 StartZ=0 EndX=-1.5 EndY=5.75 EndZ=0
    g47: LineSegment StartX=-49.19 StartY=2.75 StartZ=0 EndX=-1.5 EndY=2.75 EndZ=0
  constraints (120):
    c: Vertical(g0)
    c: Distance(g0) = 3
    c: Block(g0)
    c: Vertical(g1)
    c: Distance(g1) = 3
    c: Vertical(g2)
    c: Equal(g0,g2) = 3
    c: Block(g2)
    c: Vertical(g3)
    c: Equal(g1,g3) = 3
    c: Vertical(g4)
    c: Equal(g0,g4) = 3
    c: Block(g4)
    c: Vertical(g5)
    c: Equal(g1,g5) = 3
    c: Vertical(g6)
    c: Equal(g0,g6) = 3
    c: Block(g6)
    c: Vertical(g7)
    c: Equal(g1,g7) = 3
    c: Vertical(g8)
    c: Equal(g0,g8) = 3
    c: Block(g8)
    c: Vertical(g9)
    c: Equal(g1,g9) = 3
    c: Vertical(g10)
    c: Equal(g0,g10) = 3
    c: Block(g10)
    c: Vertical(g11)
    c: Equal(g1,g11) = 3
    c: Block(g12)
    c: Block(g13)
    c: Block(g14)
    c: Block(g15)
    c: Block(g16)
    c: Block(g17)
    c: Block(g18)
    c: Block(g19)
    c: Block(g20)
    c: Block(g21)
    c: Block(g22)
    c: Block(g23)
    c: Block(g11)
    c: Block(g9)
    c: Block(g7)
    c: Block(g5)
    c: Block(g3)
    c: Block(g1)
    c: Coincident(g24,g0)
    c: Coincident(g24,g12)
    c: Horizontal(g24)
    c: Coincident(g25,g0)
    c: Coincident(g25,g12)
    c: Horizontal(g25)
    c: Coincident(g26,g1)
    c: Coincident(g26,g13)
    c: Horizontal(g26)
    c: Coincident(g27,g1)
    c: Coincident(g27,g13)
    c: Horizontal(g27)
    c: Coincident(g28,g2)
    c: Coincident(g28,g14)
    c: Horizontal(g28)
    c: Coincident(g29,g2)
    c: Coincident(g29,g14)
    c: Horizontal(g29)
    c: Coincident(g30,g3)
    c: Coincident(g30,g15)
    c: Horizontal(g30)
    c: Coincident(g31,g3)
    c: Coincident(g31,g15)
    c: Horizontal(g31)
    c: Coincident(g32,g4)
    c: Coincident(g32,g16)
    c: Horizontal(g32)
    c: Coincident(g33,g4)
    c: Coincident(g33,g16)
    c: Horizontal(g33)
    c: Coincident(g34,g5)
    c: Coincident(g34,g17)
    c: Horizontal(g34)
    c: Coincident(g35,g5)
    c: Coincident(g35,g17)
    c: Horizontal(g35)
    c: Coincident(g36,g6)
    c: Coincident(g36,g19)
    c: Horizontal(g36)
    c: Coincident(g37,g6)
    c: Coincident(g37,g19)
    c: Horizontal(g37)
    c: Coincident(g38,g7)
    c: Coincident(g38,g18)
    c: Horizontal(g38)
    c: Coincident(g39,g7)
    c: Coincident(g39,g18)
    c: Horizontal(g39)
    c: Coincident(g40,g8)
    c: Coincident(g40,g20)
    c: Horizontal(g40)
    c: Coincident(g41,g8)
    c: Coincident(g41,g20)
    c: Horizontal(g41)
    c: Coincident(g42,g9)
    c: Coincident(g42,g23)
    c: Horizontal(g42)
    c: Coincident(g43,g9)
    c: Coincident(g43,g23)
    c: Horizontal(g43)
    c: Coincident(g44,g10)
    c: Coincident(g44,g22)
    c: Horizontal(g44)
    c: Coincident(g45,g10)
    c: Coincident(g45,g22)
    c: Horizontal(g45)
    c: Coincident(g46,g11)
    c: Coincident(g46,g21)
    c: Horizontal(g46)
    c: Coincident(g47,g11)
    c: Coincident(g47,g21)
    c: Horizontal(g47)
FEATURE [Part::Extrusion] Extrude046
  Base = -> Sketch055
  Dir = (1,0,0)
  DirMode = 2
  FaceMakerClass = Part::FaceMakerBullseye
  LengthFwd = 23
  LengthRev = 0
  Placement = pos=(-19,0,0) rot=(0,0,1;0rad)
  Solid = true
  Symmetric = false
FEATURE [Part::Fillet] Fillet038  label="removeToCreateVentalationHoles001"
  Base = -> Extrude046
  Edges = <same value as first occurrence — deduplicated (x6 in doc)>
  Placement = pos=(7,0,0) rot=(0,0,1;0rad)
FEATURE [Sketcher::SketchObject] Sketch056  label="topSketch014"
  FullyConstrained = true
  sketch-geometry (22):
    g0: LineSegment StartX=5.21097e-06 StartY=3 StartZ=0 EndX=5.21097e-06 EndY=19 EndZ=0
    g1: ArcOfCircle CenterX=19 CenterY=19 CenterZ=0 NormalX=0 NormalY=0 NormalZ=1 AngleXU=0 Radius=19 StartAngle=1.5708 EndAngle=3.14159
    g2: ArcOfCircle CenterX=19 CenterY=19 CenterZ=0 NormalX=0 NormalY=0 NormalZ=1 AngleXU=0 Radius=16 StartAngle=1.5708 EndAngle=3.14159
    g3: LineSegment StartX=114 StartY=35 StartZ=0 EndX=19 EndY=35 EndZ=0
    g4: LineSegment StartX=5.21097e-06 StartY=3 StartZ=0 EndX=5.21097e-06 EndY=0 EndZ=0
    g5: LineSegment StartX=3 StartY=0 StartZ=0 EndX=5.21097e-06 EndY=0 EndZ=0
    g6: LineSegment StartX=3 StartY=19 StartZ=0 EndX=3 EndY=0 EndZ=0
    g7: LineSegment StartX=19 StartY=38 StartZ=0 EndX=124 EndY=38 EndZ=0
    g8: Circle CenterX=119 CenterY=35 CenterZ=0 NormalX=0 NormalY=0 NormalZ=1 AngleXU=0 Radius=1
    g9: Circle CenterX=121 CenterY=35 CenterZ=0 NormalX=0 NormalY=0 NormalZ=1 AngleXU=0 Radius=1
    g10: Circle CenterX=121 CenterY=33 CenterZ=0 NormalX=0 NormalY=0 NormalZ=1 AngleXU=0 Radius=1
    g11: BSplineCurve PolesCount=3 KnotsCount=2 Degree=2 IsPeriodic=0
    g12: GeomPoint X=119 Y=35 Z=0
    g13: GeomPoint X=121 Y=33 Z=0
    g14: LineSegment StartX=119 StartY=35 StartZ=0 EndX=114 EndY=35 EndZ=0
    g15: ArcOfCircle CenterX=105 CenterY=19 CenterZ=0 NormalX=0 NormalY=0 NormalZ=1 AngleXU=0 Radius=16 StartAngle=5.60905 EndAngle=6.28319
    g16: LineSegment StartX=121 StartY=33 StartZ=0 EndX=121 EndY=19 EndZ=0
    g17: LineSegment StartX=117.5 StartY=9.01251 StartZ=0 EndX=121.163 EndY=9.0125 EndZ=0
    g18: ArcOfCircle CenterX=105 CenterY=19 CenterZ=0 NormalX=0 NormalY=0 NormalZ=1 AngleXU=0 Radius=20.6155 StartAngle=5.7297 EndAngle=6.28319
    g19: LineSegment StartX=121.163 StartY=9.0125 StartZ=0 EndX=122.538 EndY=8.16329 EndZ=0
    g20: LineSegment StartX=124 StartY=38 StartZ=0 EndX=125.616 EndY=38 EndZ=0
    g21: LineSegment StartX=125.616 StartY=19 StartZ=0 EndX=125.616 EndY=38 EndZ=0
  constraints (49):
    c: Vertical(g0)
    c: Block(g0)
    c: Coincident(g1,g0)
    c: Block(g1)
    c: Coincident(g2,g1)
    c: Block(g2)
    c: Coincident(g3,g2)
    c: Horizontal(g3)
    c: Tangent(g3,g2)
    c: Coincident(g4,g0)
    c: Distance(g4) = 3
    c: Vertical(g4)
    c: Coincident(g5,g4)
    c: Horizontal(g5)
    c: Coincident(g6,g2)
    c: Coincident(g6,g5)
    c: Vertical(g6)
    c: Horizontal(g7)
    c: Distance(g7) = 105
    c: Coincident(g7,g1)
    c: Block(g3)
    c: Weight(g8) = 1
    c: Equal(g8,g9)
    c: Equal(g8,g10)
    c: InternalAlignment(g8,g11)
    c: InternalAlignment(g9,g11)
    c: InternalAlignment(g10,g11)
    c: InternalAlignment(g12,g11)
    c: InternalAlignment(g13,g11)
    c: Block(g11)
    c: Coincident(g14,g11)
    c: Coincident(g14,g3)
    c: Horizontal(g14)
    c: Block(g15)
    c: Coincident(g16,g11)
    c: Coincident(g16,g15)
    c: Vertical(g16)
    c: Distance(g16) = 14
    c: Coincident(g17,g15)
    c: Block(g18)
    c: Coincident(g19,g18)
    c: Coincident(g20,g7)
    c: Horizontal(g20)
    c: Vertical(g21)
    c: Coincident(g20,g21)
    c: Block(g20)
    c: Block(g21)
    c: Block(g19)
    c: Block(g17)
FEATURE [Part::Box] Box026  label="removeToCreteHoleForPlugHousing032"
  AttacherType = Attacher::AttachEngine3D
  Height = 28.6
  Length = 10
  Placement = pos=(-2,0,21.7) rot=(0,0,1;0rad)
  Width = 19
FEATURE [Part::Feature] Face109 .. Face112  x4 (patterned run collapsed; names and placements below)
  shape: bbox 3.5 x 17.8 x 2e-07 mm, 1 faces, 0 solids (baked)
FEATURE [Part::Revolution] Revolve117  label="removeToCreateScrewAndThreadedInsertHole045"
  Angle = 360
  Axis = (0,1,0)
  Base = (0,0,0)
  FaceMakerClass = Part::FaceMakerBullseye
  Placement = pos=(62.3,30.3,19.7) rot=(0,0,1;0rad)
  Solid = false
  Source = -> Face109
  Symmetric = false
FEATURE [Part::Revolution] Revolve118  label="removeToCreateScrewAndThreadedInsertHole046"
  Angle = 360
  Axis = (0,1,0)
  Base = (0,0,0)
  FaceMakerClass = Part::FaceMakerBullseye
  Placement = pos=(62.3,30.3,51.7) rot=(0,0,1;0rad)
  Solid = false
  Source = -> Face110
  Symmetric = false
FEATURE [Part::Revolution] Revolve119  label="removeToCreateScrewAndThreadedInsertHole047"
  Angle = 360
  Axis = (0,1,0)
  Base = (0,0,0)
  FaceMakerClass = Part::FaceMakerBullseye
  Placement = pos=(30.3,30.3,19.7) rot=(0,0,1;0rad)
  Solid = false
  Source = -> Face111
  Symmetric = false
FEATURE [Part::Revolution] Revolve120  label="removeToCreateScrewAndThreadedInsertHole048"
  Angle = 360
  Axis = (0,1,0)
  Base = (0,0,0)
  FaceMakerClass = Part::FaceMakerBullseye
  Placement = pos=(30.3,30.3,51.7) rot=(0,0,1;0rad)
  Solid = false
  Source = -> Face112
  Symmetric = false
FEATURE [Part::MultiFuse] Fusion087  label="createThreadedInsertHolesForFan005"
  Shapes = -> [Revolve117,Revolve118,Revolve119,Revolve120]
FEATURE [Part::Extrusion] Extrude047
  Base = -> Sketch056
  Dir = (0,0,1)
  DirMode = 2
  FaceMakerClass = Part::FaceMakerBullseye
  LengthFwd = 72
  LengthRev = 0
  Solid = true
  Symmetric = false
FEATURE [Part::Fillet] Fillet039  label="top019"
  Base = -> Extrude047
  Edges = 1 edges r=2: [Edge35]
FEATURE [Sketcher::SketchObject] Sketch057
  FullyConstrained = false
  Placement = pos=(0,0,0) rot=(1,0,0;1.5708rad)
  sketch-geometry (24):
    g0: ArcOfCircle CenterX=-4 CenterY=-10.5 CenterZ=0 NormalX=0 NormalY=0 NormalZ=1 AngleXU=0 Radius=1.5 StartAngle=6e-16 EndAngle=3.14159
    g1: ArcOfCircle CenterX=-34.2 CenterY=-10.5 CenterZ=0 NormalX=0 NormalY=0 NormalZ=1 AngleXU=0 Radius=1.5 StartAngle=0 EndAngle=3.14159
    g2: ArcOfCircle CenterX=-34.2 CenterY=-27.7 CenterZ=0 NormalX=0 NormalY=0 NormalZ=1 AngleXU=0 Radius=1.5 StartAngle=3.14159 EndAngle=6.28319
    g3: ArcOfCircle CenterX=-4 CenterY=-27.7 CenterZ=0 NormalX=0 NormalY=0 NormalZ=1 AngleXU=0 Radius=1.5 StartAngle=3.1416 EndAngle=6.28319
    g4: ArcOfCircle CenterX=-10 CenterY=-4.3 CenterZ=0 NormalX=0 NormalY=0 NormalZ=1 AngleXU=0 Radius=1.5 StartAngle=2e-16 EndAngle=3.14159
    g5: ArcOfCircle CenterX=-16.1 CenterY=-1.8 CenterZ=0 NormalX=0 NormalY=0 NormalZ=1 AngleXU=0 Radius=1.5 StartAngle=5e-16 EndAngle=3.14159
    g6: ArcOfCircle CenterX=-22.1 CenterY=-1.8 CenterZ=0 NormalX=0 NormalY=0 NormalZ=1 AngleXU=0 Radius=1.5 StartAngle=5e-16 EndAngle=3.14159
    g7: ArcOfCircle CenterX=-28.2 CenterY=-4.3 CenterZ=0 NormalX=0 NormalY=0 NormalZ=1 AngleXU=0 Radius=1.5 StartAngle=2e-16 EndAngle=3.14159
    g8: ArcOfCircle CenterX=-10 CenterY=-33.9 CenterZ=0 NormalX=0 NormalY=0 NormalZ=1 AngleXU=0 Radius=1.5 StartAngle=3.14159 EndAngle=6.28319
    g9: ArcOfCircle CenterX=-16.1 CenterY=-36.4 CenterZ=0 NormalX=0 NormalY=0 NormalZ=1 AngleXU=0 Radius=1.5 StartAngle=3.14159 EndAngle=6.28319
    g10: ArcOfCircle CenterX=-22.1 CenterY=-36.4 CenterZ=0 NormalX=0 NormalY=0 NormalZ=1 AngleXU=0 Radius=1.5 StartAngle=3.14159 EndAngle=6.28319
    g11: ArcOfCircle CenterX=-28.2 CenterY=-33.9 CenterZ=0 NormalX=0 NormalY=0 NormalZ=1 AngleXU=0 Radius=1.5 StartAngle=3.14159 EndAngle=6.28319
    g12: LineSegment StartX=-35.7 StartY=-10.5 StartZ=0 EndX=-35.7 EndY=-27.7 EndZ=0
    g13: LineSegment StartX=-32.7 StartY=-10.5 StartZ=0 EndX=-32.7 EndY=-27.7 EndZ=0
    g14: LineSegment StartX=-29.7 StartY=-33.9 StartZ=0 EndX=-29.7 EndY=-4.3 EndZ=0
    g15: LineSegment StartX=-26.7 StartY=-33.9 StartZ=0 EndX=-26.7 EndY=-4.3 EndZ=0
    g16: LineSegment StartX=-2.5 StartY=-10.5 StartZ=0 EndX=-2.5 EndY=-27.7 EndZ=0
    g17: LineSegment StartX=-8.5 StartY=-4.3 StartZ=0 EndX=-8.5 EndY=-33.9 EndZ=0
    g18: LineSegment StartX=-5.5 StartY=-10.5 StartZ=0 EndX=-5.5 EndY=-27.7 EndZ=0
    g19: LineSegment StartX=-11.5 StartY=-4.3 StartZ=0 EndX=-11.5 EndY=-33.9 EndZ=0
    g20: LineSegment StartX=-14.6 StartY=-1.8 StartZ=0 EndX=-14.6 EndY=-36.4 EndZ=0
    g21: LineSegment StartX=-17.6 StartY=-1.8 StartZ=0 EndX=-17.6 EndY=-36.4 EndZ=0
    g22: LineSegment StartX=-20.6 StartY=-36.4 StartZ=0 EndX=-20.6 EndY=-1.8 EndZ=0
    g23: LineSegment StartX=-23.6 StartY=-1.8 StartZ=0 EndX=-23.6 EndY=-36.4 EndZ=0
  constraints (48):
    c: Block(g0)
    c: Block(g1)
    c: Block(g2)
    c: Block(g3)
    c: Block(g4)
    c: Block(g5)
    c: Block(g6)
    c: Block(g7)
    c: Block(g8)
    c: Block(g9)
    c: Block(g10)
    c: Block(g11)
    c: Coincident(g12,g1)
    c: Coincident(g12,g2)
    c: Vertical(g12)
    c: Coincident(g13,g1)
    c: Coincident(g13,g2)
    c: Vertical(g13)
    c: Coincident(g14,g11)
    c: Coincident(g14,g7)
    c: Vertical(g14)
    c: Coincident(g15,g11)
    c: Coincident(g15,g7)
    c: Vertical(g15)
    c: Coincident(g16,g0)
    c: Coincident(g16,g3)
    c: Vertical(g16)
    c: Coincident(g17,g4)
    c: Coincident(g17,g8)
    c: Vertical(g17)
    c: Coincident(g18,g0)
    c: Coincident(g18,g3)
    c: Vertical(g18)
    c: Coincident(g19,g4)
    c: Coincident(g19,g8)
    c: Vertical(g19)
    c: Coincident(g20,g5)
    c: Coincident(g20,g9)
    c: Vertical(g20)
    c: Coincident(g21,g5)
    c: Coincident(g21,g9)
    c: Vertical(g21)
    c: Coincident(g22,g10)
    c: Coincident(g22,g6)
    c: Vertical(g22)
    c: Coincident(g23,g6)
    c: Coincident(g23,g10)
    c: Vertical(g23)
FEATURE [Part::Extrusion] Extrude048  label="removeToCreateFanGrillHoles004"
  Base = -> Sketch057
  Dir = (0,-1,6e-16)
  DirMode = 2
  FaceMakerClass = Part::FaceMakerBullseye
  LengthFwd = 10
  LengthRev = 0
  Placement = pos=(65.4,44,54.82) rot=(0,0,1;0rad)
  Solid = true
  Symmetric = false
FEATURE [Part::Cut] Cut040  label="top021"
  Base = -> Fillet039
  Tool = -> Extrude048
FEATURE [Part::Cylinder] Cylinder041  label="removeToCreteHoleForPlugHousing034"
  Angle = 360
  AttacherType = Attacher::AttachEngine3D
  Height = 20
  Placement = pos=(-2,19,36) rot=(0,1,0;1.5708rad)
  Radius = 14.3
FEATURE [Part::MultiFuse] Fusion089  label="removeToCreteHoleForPlugHousing035"
  Shapes = -> [Box026,Cylinder041]
FEATURE [Part::Cylinder] Cylinder042
  Angle = 360
  AttacherType = Attacher::AttachEngine3D
  Height = 20
  Placement = pos=(0,0,36.15) rot=(0,0,1;0rad)
  Radius = 14.3
FEATURE [Part::Cylinder] Cylinder043
  Angle = 360
  AttacherType = Attacher::AttachEngine3D
  Height = 10
  Placement = pos=(0,0,36.15) rot=(0,0,1;0rad)
  Radius = 4
FEATURE [Part::Box] Box027  label="removeToCreteHoleForPlugHousing036"
  AttacherType = Attacher::AttachEngine3D
  Height = 28.6
  Length = 20
  Placement = pos=(106.15,0,21.7) rot=(0,0,1;0rad)
  Width = 19
FEATURE [Part::Cut] Cut041  label="top022"
  Base = -> Cut040
  Tool = -> Fusion087
FEATURE [Part::Cut] Cut039  label="top020"
  Base = -> Cut041
  Tool = -> Fusion089
FEATURE [Part::MultiFuse] Fusion090  label="removeToCreteHoleForPlugHousing037"
  Placement = pos=(70,19,36) rot=(0,1,0;1.5708rad)
  Shapes = -> [Cylinder042,Cylinder043]
FEATURE [Part::MultiFuse] Fusion088  label="removeToCreteHoleForPlugHousing033"
  Shapes = -> [Box027,Fusion090]
FEATURE [Part::Cut] Cut042  label="removeToCreteHoleForPlugHousing038"
  Base = -> Cut039
  Tool = -> Fusion088
FEATURE [Part::MultiFuse] Fusion091  label="removeFromTop"
  Shapes = -> [Fillet038,Fusion085,Fusion084,Fusion083,Extrude045]
FEATURE [Part::Cut] Cut043  label="REAL TOP ====="
  Base = -> Fillet036
  Tool = -> Fusion091
FEATURE [Part::MultiFuse] Fusion092  label="caseScrewPillarBracket016"
  Shapes = -> [Extrude030,Extrude031,Extrude032,Extrude033,Extrude034,Extrude035,Extrude036,Extrude037,Box013,Box014]
FEATURE [Sketcher::SketchObject] Sketch058  label="topSketch015"
  FullyConstrained = true
  sketch-geometry (20):
    g0: LineSegment StartX=5.21097e-06 StartY=3 StartZ=0 EndX=5.21097e-06 EndY=19 EndZ=0
    g1: ArcOfCircle CenterX=19 CenterY=19 CenterZ=0 NormalX=0 NormalY=0 NormalZ=1 AngleXU=0 Radius=19 StartAngle=1.5708 EndAngle=3.14159
    g2: ArcOfCircle CenterX=19 CenterY=19 CenterZ=0 NormalX=0 NormalY=0 NormalZ=1 AngleXU=0 Radius=16 StartAngle=1.5708 EndAngle=3.14159
    g3: LineSegment StartX=114 StartY=35 StartZ=0 EndX=19 EndY=35 EndZ=0
    g4: LineSegment StartX=5.21097e-06 StartY=3 StartZ=0 EndX=5.21097e-06 EndY=0 EndZ=0
    g5: LineSegment StartX=3 StartY=0 StartZ=0 EndX=5.21097e-06 EndY=0 EndZ=0
    g6: LineSegment StartX=3 StartY=19 StartZ=0 EndX=3 EndY=0 EndZ=0
    g7: LineSegment StartX=19 StartY=38 StartZ=0 EndX=124 EndY=38 EndZ=0
    g8: Circle CenterX=119 CenterY=35 CenterZ=0 NormalX=0 NormalY=0 NormalZ=1 AngleXU=0 Radius=1
    g9: Circle CenterX=121 CenterY=35 CenterZ=0 NormalX=0 NormalY=0 NormalZ=1 AngleXU=0 Radius=1
    g10: Circle CenterX=121 CenterY=33 CenterZ=0 NormalX=0 NormalY=0 NormalZ=1 AngleXU=0 Radius=1
    g11: BSplineCurve PolesCount=3 KnotsCount=2 Degree=2 IsPeriodic=0
    g12: GeomPoint X=119 Y=35 Z=0
    g13: GeomPoint X=121 Y=33 Z=0
    g14: LineSegment StartX=119 StartY=35 StartZ=0 EndX=114 EndY=35 EndZ=0
    g15: ArcOfCircle CenterX=105 CenterY=19 CenterZ=0 NormalX=0 NormalY=0 NormalZ=1 AngleXU=0 Radius=19 StartAngle=5.7297 EndAngle=6.28319
    g16: ArcOfCircle CenterX=105 CenterY=19 CenterZ=0 NormalX=0 NormalY=0 NormalZ=1 AngleXU=0 Radius=16 StartAngle=5.60905 EndAngle=6.28319
    g17: LineSegment StartX=121 StartY=33 StartZ=0 EndX=121 EndY=19 EndZ=0
    g18: LineSegment StartX=124 StartY=38 StartZ=0 EndX=124 EndY=19 EndZ=0
    g19: LineSegment StartX=117.5 StartY=9.01251 StartZ=0 EndX=121.163 EndY=9.0125 EndZ=0
  constraints (46):
    c: Vertical(g0)
    c: Block(g0)
    c: Coincident(g1,g0)
    c: Block(g1)
    c: Coincident(g2,g1)
    c: Block(g2)
    c: Coincident(g3,g2)
    c: Horizontal(g3)
    c: Tangent(g3,g2)
    c: Coincident(g4,g0)
    c: Distance(g4) = 3
    c: Vertical(g4)
    c: Coincident(g5,g4)
    c: Horizontal(g5)
    c: Coincident(g6,g2)
    c: Coincident(g6,g5)
    c: Vertical(g6)
    c: Horizontal(g7)
    c: Distance(g7) = 105
    c: Coincident(g7,g1)
    c: Block(g3)
    c: Weight(g8) = 1
    c: Equal(g8,g9)
    c: Equal(g8,g10)
    c: InternalAlignment(g8,g11)
    c: InternalAlignment(g9,g11)
    c: InternalAlignment(g10,g11)
    c: InternalAlignment(g12,g11)
    c: InternalAlignment(g13,g11)
    c: Block(g11)
    c: Coincident(g14,g11)
    c: Coincident(g14,g3)
    c: Horizontal(g14)
    c: Block(g15)
    c: Coincident(g16,g15)
    c: Block(g16)
    c: Coincident(g17,g11)
    c: Coincident(g17,g16)
    c: Vertical(g17)
    c: Distance(g17) = 14
    c: Coincident(g18,g7)
    c: Coincident(g18,g15)
    c: Vertical(g18)
    c: Distance(g18) = 19
    c: Coincident(g19,g16)
    c: Coincident(g19,g15)
FEATURE [Part::Extrusion] Extrude049  label="top023"
  Base = -> Sketch058
  Dir = (0,0,1)
  DirMode = 2
  FaceMakerClass = Part::FaceMakerBullseye
  LengthFwd = 72
  LengthRev = 0
  Solid = true
  Symmetric = false
FEATURE [Sketcher::SketchObject] Sketch059
  FullyConstrained = true
  MapMode = 3
  Placement = pos=(0,0,0) rot=(1,0,0;1.5708rad)
  Support = -> [Extrude049]
  sketch-geometry (8):
    g0: Circle CenterX=80.351 CenterY=-67.6202 CenterZ=0 NormalX=0 NormalY=0 NormalZ=1 AngleXU=0 Radius=2
    g1: Circle CenterX=80.351 CenterY=-67.6202 CenterZ=0 NormalX=0 NormalY=0 NormalZ=1 AngleXU=0 Radius=3
    g2: Circle CenterX=80.351 CenterY=-4.92017 CenterZ=0 NormalX=0 NormalY=0 NormalZ=1 AngleXU=0 Radius=2
    g3: Circle CenterX=80.351 CenterY=-4.92017 CenterZ=0 NormalX=0 NormalY=0 NormalZ=1 AngleXU=0 Radius=3
    g4: Circle CenterX=23.851 CenterY=-4.92017 CenterZ=0 NormalX=0 NormalY=0 NormalZ=1 AngleXU=0 Radius=2
    g5: Circle CenterX=23.851 CenterY=-4.92017 CenterZ=0 NormalX=0 NormalY=0 NormalZ=1 AngleXU=0 Radius=3
    g6: Circle CenterX=23.851 CenterY=-67.6202 CenterZ=0 NormalX=0 NormalY=0 NormalZ=1 AngleXU=0 Radius=2
    g7: Circle CenterX=23.851 CenterY=-67.6202 CenterZ=0 NormalX=0 NormalY=0 NormalZ=1 AngleXU=0 Radius=3
  constraints (8):
    c: Block(g3)
    c: Block(g2)
    c: Block(g1)
    c: Block(g0)
    c: Block(g6)
    c: Block(g7)
    c: Block(g4)
    c: Block(g5)
FEATURE [Sketcher::SketchObject] Sketch060
  FullyConstrained = true
  MapMode = 3
  Placement = pos=(0,0,0) rot=(1,0,0;1.5708rad)
  Support = -> [Extrude049]
  sketch-geometry (8):
    g0: Circle CenterX=80.351 CenterY=-67.6202 CenterZ=0 NormalX=0 NormalY=0 NormalZ=1 AngleXU=0 Radius=3
    g1: Circle CenterX=80.351 CenterY=-4.92017 CenterZ=0 NormalX=0 NormalY=0 NormalZ=1 AngleXU=0 Radius=3
    g2: Circle CenterX=23.851 CenterY=-4.92017 CenterZ=0 NormalX=0 NormalY=0 NormalZ=1 AngleXU=0 Radius=3
    g3: Circle CenterX=23.851 CenterY=-67.6202 CenterZ=0 NormalX=0 NormalY=0 NormalZ=1 AngleXU=0 Radius=3
    g4: Circle CenterX=23.851 CenterY=-67.6202 CenterZ=0 NormalX=0 NormalY=0 NormalZ=1 AngleXU=0 Radius=5
    g5: Circle CenterX=80.351 CenterY=-67.6202 CenterZ=0 NormalX=0 NormalY=0 NormalZ=1 AngleXU=0 Radius=5
    g6: Circle CenterX=23.851 CenterY=-4.92017 CenterZ=0 NormalX=0 NormalY=0 NormalZ=1 AngleXU=0 Radius=5
    g7: Circle CenterX=80.351 CenterY=-4.92017 CenterZ=0 NormalX=0 NormalY=0 NormalZ=1 AngleXU=0 Radius=5
  constraints (8):
    c: Block(g1)
    c: Block(g0)
    c: Block(g3)
    c: Block(g2)
    c: Block(g5)
    c: Block(g4)
    c: Block(g6)
    c: Block(g7)
FEATURE [Sketcher::SketchObject] Sketch061
  FullyConstrained = true
  MapMode = 3
  Placement = pos=(0,0,0) rot=(1,0,0;1.5708rad)
  sketch-geometry (8):
    g0: Circle CenterX=80.351 CenterY=-67.6202 CenterZ=0 NormalX=0 NormalY=0 NormalZ=1 AngleXU=0 Radius=3
    g1: Circle CenterX=80.351 CenterY=-4.92017 CenterZ=0 NormalX=0 NormalY=0 NormalZ=1 AngleXU=0 Radius=3
    g2: Circle CenterX=23.851 CenterY=-4.92017 CenterZ=0 NormalX=0 NormalY=0 NormalZ=1 AngleXU=0 Radius=3
    g3: Circle CenterX=23.851 CenterY=-67.6202 CenterZ=0 NormalX=0 NormalY=0 NormalZ=1 AngleXU=0 Radius=3
    g4: Circle CenterX=23.851 CenterY=-67.6202 CenterZ=0 NormalX=0 NormalY=0 NormalZ=1 AngleXU=0 Radius=5
    g5: Circle CenterX=80.351 CenterY=-67.6202 CenterZ=0 NormalX=0 NormalY=0 NormalZ=1 AngleXU=0 Radius=5
    g6: Circle CenterX=23.851 CenterY=-4.92017 CenterZ=0 NormalX=0 NormalY=0 NormalZ=1 AngleXU=0 Radius=5
    g7: Circle CenterX=80.351 CenterY=-4.92017 CenterZ=0 NormalX=0 NormalY=0 NormalZ=1 AngleXU=0 Radius=5
  constraints (8):
    c: Block(g1)
    c: Block(g0)
    c: Block(g3)
    c: Block(g2)
    c: Block(g5)
    c: Block(g4)
    c: Block(g6)
    c: Block(g7)
FEATURE [Sketcher::SketchObject] Sketch062  label="topSketch016"
  FullyConstrained = true
  sketch-geometry (20):
    g0: LineSegment StartX=5.21097e-06 StartY=3 StartZ=0 EndX=5.21097e-06 EndY=19 EndZ=0
    g1: ArcOfCircle CenterX=19 CenterY=19 CenterZ=0 NormalX=0 NormalY=0 NormalZ=1 AngleXU=0 Radius=19 StartAngle=1.5708 EndAngle=3.14159
    g2: ArcOfCircle CenterX=19 CenterY=19 CenterZ=0 NormalX=0 NormalY=0 NormalZ=1 AngleXU=0 Radius=16 StartAngle=1.5708 EndAngle=3.14159
    g3: LineSegment StartX=114 StartY=35 StartZ=0 EndX=19 EndY=35 EndZ=0
    g4: LineSegment StartX=5.21097e-06 StartY=3 StartZ=0 EndX=5.21097e-06 EndY=0 EndZ=0
    g5: LineSegment StartX=3 StartY=0 StartZ=0 EndX=5.21097e-06 EndY=0 EndZ=0
    g6: LineSegment StartX=3 StartY=19 StartZ=0 EndX=3 EndY=0 EndZ=0
    g7: LineSegment StartX=19 StartY=38 StartZ=0 EndX=124 EndY=38 EndZ=0
    g8: Circle CenterX=119 CenterY=35 CenterZ=0 NormalX=0 NormalY=0 NormalZ=1 AngleXU=0 Radius=1
    g9: Circle CenterX=121 CenterY=35 CenterZ=0 NormalX=0 NormalY=0 NormalZ=1 AngleXU=0 Radius=1
    g10: Circle CenterX=121 CenterY=33 CenterZ=0 NormalX=0 NormalY=0 NormalZ=1 AngleXU=0 Radius=1
    g11: BSplineCurve PolesCount=3 KnotsCount=2 Degree=2 IsPeriodic=0
    g12: GeomPoint X=119 Y=35 Z=0
    g13: GeomPoint X=121 Y=33 Z=0
    g14: LineSegment StartX=119 StartY=35 StartZ=0 EndX=114 EndY=35 EndZ=0
    g15: ArcOfCircle CenterX=105 CenterY=19 CenterZ=0 NormalX=0 NormalY=0 NormalZ=1 AngleXU=0 Radius=19 StartAngle=5.7297 EndAngle=6.28319
    g16: ArcOfCircle CenterX=105 CenterY=19 CenterZ=0 NormalX=0 NormalY=0 NormalZ=1 AngleXU=0 Radius=16 StartAngle=5.60905 EndAngle=6.28319
    g17: LineSegment StartX=121 StartY=33 StartZ=0 EndX=121 EndY=19 EndZ=0
    g18: LineSegment StartX=124 StartY=38 StartZ=0 EndX=124 EndY=19 EndZ=0
    g19: LineSegment StartX=117.5 StartY=9.01251 StartZ=0 EndX=121.163 EndY=9.0125 EndZ=0
  constraints (46):
    c: Vertical(g0)
    c: Block(g0)
    c: Coincident(g1,g0)
    c: Block(g1)
    c: Coincident(g2,g1)
    c: Block(g2)
    c: Coincident(g3,g2)
    c: Horizontal(g3)
    c: Tangent(g3,g2)
    c: Coincident(g4,g0)
    c: Distance(g4) = 3
    c: Vertical(g4)
    c: Coincident(g5,g4)
    c: Horizontal(g5)
    c: Coincident(g6,g2)
    c: Coincident(g6,g5)
    c: Vertical(g6)
    c: Horizontal(g7)
    c: Distance(g7) = 105
    c: Coincident(g7,g1)
    c: Block(g3)
    c: Weight(g8) = 1
    c: Equal(g8,g9)
    c: Equal(g8,g10)
    c: InternalAlignment(g8,g11)
    c: InternalAlignment(g9,g11)
    c: InternalAlignment(g10,g11)
    c: InternalAlignment(g12,g11)
    c: InternalAlignment(g13,g11)
    c: Block(g11)
    c: Coincident(g14,g11)
    c: Coincident(g14,g3)
    c: Horizontal(g14)
    c: Block(g15)
    c: Coincident(g16,g15)
    c: Block(g16)
    c: Coincident(g17,g11)
    c: Coincident(g17,g16)
    c: Vertical(g17)
    c: Distance(g17) = 14
    c: Coincident(g18,g7)
    c: Coincident(g18,g15)
    c: Vertical(g18)
    c: Distance(g18) = 19
    c: Coincident(g19,g16)
    c: Coincident(g19,g15)
FEATURE [Part::Extrusion] Extrude053  label="top024"
  Base = -> Sketch062
  Dir = (0,0,1)
  DirMode = 2
  FaceMakerClass = Part::FaceMakerBullseye
  LengthFwd = 72
  LengthRev = 0
  Solid = true
  Symmetric = false
FEATURE [Sketcher::SketchObject] Sketch063
  FullyConstrained = true
  MapMode = 3
  Placement = pos=(0,0,0) rot=(1,0,0;1.5708rad)
  Support = -> [Extrude053]
  sketch-geometry (8):
    g0: Circle CenterX=80.351 CenterY=-67.6202 CenterZ=0 NormalX=0 NormalY=0 NormalZ=1 AngleXU=0 Radius=2
    g1: Circle CenterX=80.351 CenterY=-67.6202 CenterZ=0 NormalX=0 NormalY=0 NormalZ=1 AngleXU=0 Radius=3
    g2: Circle CenterX=80.351 CenterY=-4.92017 CenterZ=0 NormalX=0 NormalY=0 NormalZ=1 AngleXU=0 Radius=2
    g3: Circle CenterX=80.351 CenterY=-4.92017 CenterZ=0 NormalX=0 NormalY=0 NormalZ=1 AngleXU=0 Radius=3
    g4: Circle CenterX=23.851 CenterY=-4.92017 CenterZ=0 NormalX=0 NormalY=0 NormalZ=1 AngleXU=0 Radius=2
    g5: Circle CenterX=23.851 CenterY=-4.92017 CenterZ=0 NormalX=0 NormalY=0 NormalZ=1 AngleXU=0 Radius=3
    g6: Circle CenterX=23.851 CenterY=-67.6202 CenterZ=0 NormalX=0 NormalY=0 NormalZ=1 AngleXU=0 Radius=2
    g7: Circle CenterX=23.851 CenterY=-67.6202 CenterZ=0 NormalX=0 NormalY=0 NormalZ=1 AngleXU=0 Radius=3
  constraints (8):
    c: Block(g3)
    c: Block(g2)
    c: Block(g1)
    c: Block(g0)
    c: Block(g6)
    c: Block(g7)
    c: Block(g4)
    c: Block(g5)
FEATURE [Part::Extrusion] Extrude054
  Base = -> Sketch063
  Dir = (0,-1,2e-16)
  DirMode = 2
  FaceMakerClass = Part::FaceMakerBullseye
  LengthFwd = 6
  LengthRev = 0
  Placement = pos=(0,9,0) rot=(0,0,1;0rad)
  Solid = true
  Symmetric = false
FEATURE [Sketcher::SketchObject] Sketch064  label="topSketch017"
  FullyConstrained = true
  sketch-geometry (20):
    g0: LineSegment StartX=5.21097e-06 StartY=3 StartZ=0 EndX=5.21097e-06 EndY=19 EndZ=0
    g1: ArcOfCircle CenterX=19 CenterY=19 CenterZ=0 NormalX=0 NormalY=0 NormalZ=1 AngleXU=0 Radius=19 StartAngle=1.5708 EndAngle=3.14159
    g2: ArcOfCircle CenterX=19 CenterY=19 CenterZ=0 NormalX=0 NormalY=0 NormalZ=1 AngleXU=0 Radius=16 StartAngle=1.5708 EndAngle=3.14159
    g3: LineSegment StartX=114 StartY=35 StartZ=0 EndX=19 EndY=35 EndZ=0
    g4: LineSegment StartX=5.21097e-06 StartY=3 StartZ=0 EndX=5.21097e-06 EndY=0 EndZ=0
    g5: LineSegment StartX=3 StartY=0 StartZ=0 EndX=5.21097e-06 EndY=0 EndZ=0
    g6: LineSegment StartX=3 StartY=19 StartZ=0 EndX=3 EndY=0 EndZ=0
    g7: LineSegment StartX=19 StartY=38 StartZ=0 EndX=124 EndY=38 EndZ=0
    g8: Circle CenterX=119 CenterY=35 CenterZ=0 NormalX=0 NormalY=0 NormalZ=1 AngleXU=0 Radius=1
    g9: Circle CenterX=121 CenterY=35 CenterZ=0 NormalX=0 NormalY=0 NormalZ=1 AngleXU=0 Radius=1
    g10: Circle CenterX=121 CenterY=33 CenterZ=0 NormalX=0 NormalY=0 NormalZ=1 AngleXU=0 Radius=1
    g11: BSplineCurve PolesCount=3 KnotsCount=2 Degree=2 IsPeriodic=0
    g12: GeomPoint X=119 Y=35 Z=0
    g13: GeomPoint X=121 Y=33 Z=0
    g14: LineSegment StartX=119 StartY=35 StartZ=0 EndX=114 EndY=35 EndZ=0
    g15: ArcOfCircle CenterX=105 CenterY=19 CenterZ=0 NormalX=0 NormalY=0 NormalZ=1 AngleXU=0 Radius=19 StartAngle=5.7297 EndAngle=6.28319
    g16: ArcOfCircle CenterX=105 CenterY=19 CenterZ=0 NormalX=0 NormalY=0 NormalZ=1 AngleXU=0 Radius=16 StartAngle=5.60905 EndAngle=6.28319
    g17: LineSegment StartX=121 StartY=33 StartZ=0 EndX=121 EndY=19 EndZ=0
    g18: LineSegment StartX=124 StartY=38 StartZ=0 EndX=124 EndY=19 EndZ=0
    g19: LineSegment StartX=117.5 StartY=9.01251 StartZ=0 EndX=121.163 EndY=9.0125 EndZ=0
  constraints (46):
    c: Vertical(g0)
    c: Block(g0)
    c: Coincident(g1,g0)
    c: Block(g1)
    c: Coincident(g2,g1)
    c: Block(g2)
    c: Coincident(g3,g2)
    c: Horizontal(g3)
    c: Tangent(g3,g2)
    c: Coincident(g4,g0)
    c: Distance(g4) = 3
    c: Vertical(g4)
    c: Coincident(g5,g4)
    c: Horizontal(g5)
    c: Coincident(g6,g2)
    c: Coincident(g6,g5)
    c: Vertical(g6)
    c: Horizontal(g7)
    c: Distance(g7) = 105
    c: Coincident(g7,g1)
    c: Block(g3)
    c: Weight(g8) = 1
    c: Equal(g8,g9)
    c: Equal(g8,g10)
    c: InternalAlignment(g8,g11)
    c: InternalAlignment(g9,g11)
    c: InternalAlignment(g10,g11)
    c: InternalAlignment(g12,g11)
    c: InternalAlignment(g13,g11)
    c: Block(g11)
    c: Coincident(g14,g11)
    c: Coincident(g14,g3)
    c: Horizontal(g14)
    c: Block(g15)
    c: Coincident(g16,g15)
    c: Block(g16)
    c: Coincident(g17,g11)
    c: Coincident(g17,g16)
    c: Vertical(g17)
    c: Distance(g17) = 14
    c: Coincident(g18,g7)
    c: Coincident(g18,g15)
    c: Vertical(g18)
    c: Distance(g18) = 19
    c: Coincident(g19,g16)
    c: Coincident(g19,g15)
FEATURE [Sketcher::SketchObject] Sketch065
  FullyConstrained = true
  MapMode = 3
  Placement = pos=(0,0,0) rot=(1,0,0;1.5708rad)
  sketch-geometry (8):
    g0: Circle CenterX=80.351 CenterY=-67.6202 CenterZ=0 NormalX=0 NormalY=0 NormalZ=1 AngleXU=0 Radius=3
    g1: Circle CenterX=80.351 CenterY=-4.92017 CenterZ=0 NormalX=0 NormalY=0 NormalZ=1 AngleXU=0 Radius=3
    g2: Circle CenterX=23.851 CenterY=-4.92017 CenterZ=0 NormalX=0 NormalY=0 NormalZ=1 AngleXU=0 Radius=3
    g3: Circle CenterX=23.851 CenterY=-67.6202 CenterZ=0 NormalX=0 NormalY=0 NormalZ=1 AngleXU=0 Radius=3
    g4: Circle CenterX=23.851 CenterY=-67.6202 CenterZ=0 NormalX=0 NormalY=0 NormalZ=1 AngleXU=0 Radius=5
    g5: Circle CenterX=80.351 CenterY=-67.6202 CenterZ=0 NormalX=0 NormalY=0 NormalZ=1 AngleXU=0 Radius=5
    g6: Circle CenterX=23.851 CenterY=-4.92017 CenterZ=0 NormalX=0 NormalY=0 NormalZ=1 AngleXU=0 Radius=5
    g7: Circle CenterX=80.351 CenterY=-4.92017 CenterZ=0 NormalX=0 NormalY=0 NormalZ=1 AngleXU=0 Radius=5
  constraints (8):
    c: Block(g1)
    c: Block(g0)
    c: Block(g3)
    c: Block(g2)
    c: Block(g5)
    c: Block(g4)
    c: Block(g6)
    c: Block(g7)
FEATURE [Part::Extrusion] Extrude056
  Base = -> Sketch065
  Dir = (0,-1,2e-16)
  DirMode = 2
  FaceMakerClass = Part::FaceMakerBullseye
  LengthFwd = 2
  LengthRev = 0
  Solid = true
  Symmetric = false
FEATURE [Part::Extrusion] Extrude057  label="top025"
  Base = -> Sketch064
  Dir = (0,0,1)
  DirMode = 2
  FaceMakerClass = Part::FaceMakerBullseye
  LengthFwd = 72
  LengthRev = 0
  Solid = true
  Symmetric = false
FEATURE [Sketcher::SketchObject] Sketch066
  FullyConstrained = true
  MapMode = 3
  Placement = pos=(0,0,0) rot=(1,0,0;1.5708rad)
  Support = -> [Extrude057]
  sketch-geometry (8):
    g0: Circle CenterX=80.351 CenterY=-67.6202 CenterZ=0 NormalX=0 NormalY=0 NormalZ=1 AngleXU=0 Radius=3
    g1: Circle CenterX=80.351 CenterY=-4.92017 CenterZ=0 NormalX=0 NormalY=0 NormalZ=1 AngleXU=0 Radius=3
    g2: Circle CenterX=23.851 CenterY=-4.92017 CenterZ=0 NormalX=0 NormalY=0 NormalZ=1 AngleXU=0 Radius=3
    g3: Circle CenterX=23.851 CenterY=-67.6202 CenterZ=0 NormalX=0 NormalY=0 NormalZ=1 AngleXU=0 Radius=3
    g4: Circle CenterX=23.851 CenterY=-67.6202 CenterZ=0 NormalX=0 NormalY=0 NormalZ=1 AngleXU=0 Radius=5
    g5: Circle CenterX=80.351 CenterY=-67.6202 CenterZ=0 NormalX=0 NormalY=0 NormalZ=1 AngleXU=0 Radius=5
    g6: Circle CenterX=23.851 CenterY=-4.92017 CenterZ=0 NormalX=0 NormalY=0 NormalZ=1 AngleXU=0 Radius=5
    g7: Circle CenterX=80.351 CenterY=-4.92017 CenterZ=0 NormalX=0 NormalY=0 NormalZ=1 AngleXU=0 Radius=5
  constraints (8):
    c: Block(g1)
    c: Block(g0)
    c: Block(g3)
    c: Block(g2)
    c: Block(g5)
    c: Block(g4)
    c: Block(g6)
    c: Block(g7)
FEATURE [Part::Extrusion] Extrude055
  Base = -> Sketch066
  Dir = (0,-1,2e-16)
  DirMode = 2
  FaceMakerClass = Part::FaceMakerBullseye
  LengthFwd = 2
  LengthRev = 0
  Solid = true
  Symmetric = false
FEATURE [Part::Fillet] Fillet041
  Base = -> Extrude056
  Edges = 4 edges r=1.99: [Edge6,Edge12,Edge18,Edge24]
FEATURE [Part::Cut] Cut045
  Base = -> Extrude055
  Placement = pos=(0,6,0) rot=(0,0,1;0rad)
  Tool = -> Fillet041
FEATURE [Part::MultiFuse] Fusion095  label="pcbScrewPillars"
  Placement = pos=(-3.2,-1,72.3) rot=(0,0,1;0rad)
  Shapes = -> [Cut045,Extrude054]
FEATURE [Part::Feature] Face113
  shape: bbox 3.2 x 1.5 x 2e-07 mm, 1 faces, 0 solids (baked)
FEATURE [Part::Revolution] Revolve121  label="backCaseScrewRetainer002"
  Angle = 360
  Axis = (0,1,0)
  Base = (0,0,0)
  FaceMakerClass = Part::FaceMakerBullseye
  Placement = pos=(12.5,3,62) rot=(0,0,1;0rad)
  Solid = false
  Source = -> Face113
  Symmetric = false
FEATURE [Part::Feature] Face114
  shape: bbox 3.2 x 1.5 x 2e-07 mm, 1 faces, 0 solids (baked)
FEATURE [Part::Feature] Face115
  shape: bbox 3.2 x 1.5 x 2e-07 mm, 1 faces, 0 solids (baked)
FEATURE [Part::Feature] Face116
  shape: bbox 3.2 x 1.5 x 2e-07 mm, 1 faces, 0 solids (baked)
FEATURE [Part::Revolution] Revolve122  label="frontCaseScrewRetainer004"
  Angle = 360
  Axis = (0,1,0)
  Base = (0,0,0)
  FaceMakerClass = Part::FaceMakerBullseye
  Placement = pos=(89.5,3,68.5) rot=(0,0,1;0rad)
  Solid = false
  Source = -> Face115
  Symmetric = false
FEATURE [Part::Revolution] Revolve123  label="frontCaseScrewRetainer005"
  Angle = 360
  Axis = (0,1,0)
  Base = (0,0,0)
  FaceMakerClass = Part::FaceMakerBullseye
  Placement = pos=(89.5,3,3.5) rot=(0,0,1;0rad)
  Solid = false
  Source = -> Face116
  Symmetric = false
FEATURE [Part::Revolution] Revolve124  label="backCaseScrewRetainer003"
  Angle = 360
  Axis = (0,1,0)
  Base = (0,0,0)
  FaceMakerClass = Part::FaceMakerBullseye
  Placement = pos=(12.5,3,10) rot=(0,0,1;0rad)
  Solid = false
  Source = -> Face114
  Symmetric = false
FEATURE [Part::Feature] Face117
  shape: bbox 3.6 x 3.2 x 2e-07 mm, 1 faces, 0 solids (baked)
FEATURE [Part::Revolution] Revolve125  label="moreFrontCaseScrewRetainer004"
  Angle = 360
  Axis = (0,1,0)
  Base = (0,0,0)
  FaceMakerClass = Part::FaceMakerBullseye
  Placement = pos=(109.5,4.5,68.5) rot=(0,0,1;0rad)
  Solid = false
  Source = -> Face117
  Symmetric = false
FEATURE [Part::Feature] Face118
  shape: bbox 3.6 x 3.2 x 2e-07 mm, 1 faces, 0 solids (baked)
FEATURE [Part::Revolution] Revolve126  label="moreFrontCaseScrewRetainer005"
  Angle = 360
  Axis = (0,1,0)
  Base = (0,0,0)
  FaceMakerClass = Part::FaceMakerBullseye
  Placement = pos=(109.5,4.5,3.5) rot=(0,0,1;0rad)
  Solid = false
  Source = -> Face118
  Symmetric = false
FEATURE [Part::MultiFuse] Fusion096  label="screwRetainers001"
  Shapes = -> [Revolve126,Revolve125,Revolve124,Revolve123,Revolve122,Revolve121]
FEATURE [Part::Feature] Face119
  shape: bbox 10 x 16.5 x 2e-07 mm, 1 faces, 0 solids (baked)
FEATURE [Part::Revolution] Revolve130  label="plugHousing050"
  Angle = 360
  Axis = (0,1,0)
  Base = (0,0,0)
  FaceMakerClass = Part::FaceMakerBullseye
  Placement = pos=(0,0,36.15) rot=(0,0,1;0rad)
  Solid = false
  Source = -> Face119
  Symmetric = false
FEATURE [Part::Feature] Face120
  shape: bbox 10 x 16.5 x 2e-07 mm, 1 faces, 0 solids (baked)
FEATURE [Part::Feature] Face121
  shape: bbox 10 x 16.5 x 2e-07 mm, 1 faces, 0 solids (baked)
FEATURE [Part::Revolution] Revolve127  label="plugHousing047"
  Angle = 360
  Axis = (0,1,0)
  Base = (0,0,0)
  FaceMakerClass = Part::FaceMakerBullseye
  Placement = pos=(0,0,36.15) rot=(0,0,1;0rad)
  Solid = false
  Source = -> Face121
  Symmetric = false
FEATURE [Part::Feature] Face122
  shape: bbox 10 x 16.5 x 2e-07 mm, 1 faces, 0 solids (baked)
FEATURE [Part::Feature] Face123
  shape: bbox 10 x 16.5 x 2e-07 mm, 1 faces, 0 solids (baked)
FEATURE [Part::Revolution] Revolve128  label="plugHousing048"
  Angle = 360
  Axis = (0,1,0)
  Base = (0,0,0)
  FaceMakerClass = Part::FaceMakerBullseye
  Placement = pos=(0,0,36.15) rot=(0,0,1;0rad)
  Solid = false
  Source = -> Face123
  Symmetric = false
FEATURE [Part::MultiFuse] Fusion100  label="plugHousing054"
  Placement = pos=(0,0,0) rot=(0,0,1;1.5708rad)
  Shapes = -> [Revolve130,Revolve128]
FEATURE [Part::Feature] Face124
  shape: bbox 10 x 16.5 x 2e-07 mm, 1 faces, 0 solids (baked)
FEATURE [Part::Feature] Face125
  shape: bbox 10 x 16.5 x 2e-07 mm, 1 faces, 0 solids (baked)
FEATURE [Part::Revolution] Revolve129  label="plugHousing049"
  Angle = 360
  Axis = (0,1,0)
  Base = (0,0,0)
  FaceMakerClass = Part::FaceMakerBullseye
  Placement = pos=(0,0,36.15) rot=(0,0,1;0rad)
  Solid = false
  Source = -> Face125
  Symmetric = false
FEATURE [Part::Feature] Face126
  shape: bbox 10 x 16.5 x 2e-07 mm, 1 faces, 0 solids (baked)
FEATURE [Part::Revolution] Revolve131  label="plugHousing058"
  Angle = 360
  Axis = (0,1,0)
  Base = (0,0,0)
  FaceMakerClass = Part::FaceMakerBullseye
  Placement = pos=(0,0,36.15) rot=(0,0,1;0rad)
  Solid = false
  Source = -> Face120
  Symmetric = false
FEATURE [Part::MultiFuse] Fusion099  label="plugHousing053"
  Placement = pos=(0,0,0) rot=(0,0,1;1.5708rad)
  Shapes = -> [Revolve127,Revolve131]
FEATURE [Part::MultiFuse] Fusion102  label="plugHousing056"
  Placement = pos=(0,19,0) rot=(0,0,1;3.14159rad)
  Shapes = -> [Fusion100,Fusion099]
FEATURE [Part::Revolution] Revolve132  label="plugHousing059"
  Angle = 360
  Axis = (0,1,0)
  Base = (0,0,0)
  FaceMakerClass = Part::FaceMakerBullseye
  Placement = pos=(0,0,36.15) rot=(0,0,1;0rad)
  Solid = false
  Source = -> Face126
  Symmetric = false
FEATURE [Part::Revolution] Revolve133  label="plugHousing060"
  Angle = 360
  Axis = (0,1,0)
  Base = (0,0,0)
  FaceMakerClass = Part::FaceMakerBullseye
  Placement = pos=(0,0,36.15) rot=(0,0,1;0rad)
  Solid = false
  Source = -> Face122
  Symmetric = false
FEATURE [Part::MultiFuse] Fusion097  label="plugHousing051"
  Placement = pos=(0,0,0) rot=(0,0,1;1.5708rad)
  Shapes = -> [Revolve133,Revolve132]
FEATURE [Part::Revolution] Revolve134  label="plugHousing061"
  Angle = 360
  Axis = (0,1,0)
  Base = (0,0,0)
  FaceMakerClass = Part::FaceMakerBullseye
  Placement = pos=(0,0,36.15) rot=(0,0,1;0rad)
  Solid = false
  Source = -> Face124
  Symmetric = false
FEATURE [Part::MultiFuse] Fusion101  label="plugHousing055"
  Placement = pos=(0,0,0) rot=(0,0,1;1.5708rad)
  Shapes = -> [Revolve129,Revolve134]
FEATURE [Part::MultiFuse] Fusion098  label="plugHousing052"
  Placement = pos=(0,19,0) rot=(0,0,1;3.14159rad)
  Shapes = -> [Fusion097,Fusion101]
FEATURE [Part::MultiFuse] Fusion103  label="plugHousing057"
  Placement = pos=(122.621,0,-0.15) rot=(0,0,1;0rad)
  Shapes = -> [Fusion102,Fusion098]
FEATURE [Part::Box] Box028  label="Cube015"
  AttacherType = Attacher::AttachEngine3D
  Height = 28
  Length = 3
  Placement = pos=(110.7,19,22) rot=(0,0,1;0rad)
  Width = 15.7
FEATURE [Part::Cylinder] Cylinder044
  Angle = 360
  AttacherType = Attacher::AttachEngine3D
  Height = 20
  Placement = pos=(0,0,36.15) rot=(0,0,1;0rad)
  Radius = 10.3
FEATURE [Part::Cylinder] Cylinder045
  Angle = 360
  AttacherType = Attacher::AttachEngine3D
  Height = 10
  Placement = pos=(0,0,36.15) rot=(0,0,1;0rad)
  Radius = 4
FEATURE [Part::MultiFuse] Fusion104  label="removeToCreteHoleForPlugHousing040"
  Placement = pos=(70,19,36) rot=(0,1,0;1.5708rad)
  Shapes = -> [Cylinder044,Cylinder045]
FEATURE [Part::Cut] Cut046  label="plugHousingTab003"
  Base = -> Box028
  Tool = -> Fusion104
FEATURE [Part::MultiFuse] Fusion105  label="plugHousing062"
  Shapes = -> [Fusion103,Cut046]
FEATURE [Part::Fillet] Fillet042
  Base = -> Fusion105
  Edges = 1 edges r=2: [Edge25]
FEATURE [Part::Fillet] Fillet043  label="plugHousing063"
  Base = -> Fillet042
  Edges = 1 edges r=2: [Edge8]
  Placement = pos=(7,0,0) rot=(0,0,1;0rad)
FEATURE [Part::Feature] Face127
  shape: bbox 10 x 16.5 x 2e-07 mm, 1 faces, 0 solids (baked)
FEATURE [Part::Feature] Face128
  shape: bbox 10 x 16.5 x 2e-07 mm, 1 faces, 0 solids (baked)
FEATURE [Part::Revolution] Revolve137  label="plugHousing070"
  Angle = 360
  Axis = (0,1,0)
  Base = (0,0,0)
  FaceMakerClass = Part::FaceMakerBullseye
  Placement = pos=(0,0,36.15) rot=(0,0,1;0rad)
  Solid = false
  Source = -> Face127
  Symmetric = false
FEATURE [Part::Revolution] Revolve140  label="plugHousing073"
  Angle = 360
  Axis = (0,1,0)
  Base = (0,0,0)
  FaceMakerClass = Part::FaceMakerBullseye
  Placement = pos=(0,0,36.15) rot=(0,0,1;0rad)
  Solid = false
  Source = -> Face128
  Symmetric = false
FEATURE [Part::Feature] Face129
  shape: bbox 10 x 16.5 x 2e-07 mm, 1 faces, 0 solids (baked)
FEATURE [Part::Revolution] Revolve138  label="plugHousing071"
  Angle = 360
  Axis = (0,1,0)
  Base = (0,0,0)
  FaceMakerClass = Part::FaceMakerBullseye
  Placement = pos=(0,0,36.15) rot=(0,0,1;0rad)
  Solid = false
  Source = -> Face129
  Symmetric = false
FEATURE [Part::Feature] Face130
  shape: bbox 10 x 16.5 x 2e-07 mm, 1 faces, 0 solids (baked)
FEATURE [Part::Revolution] Revolve139  label="plugHousing072"
  Angle = 360
  Axis = (0,1,0)
  Base = (0,0,0)
  FaceMakerClass = Part::FaceMakerBullseye
  Placement = pos=(0,0,36.15) rot=(0,0,1;0rad)
  Solid = false
  Source = -> Face130
  Symmetric = false
FEATURE [Part::Feature] Face131
  shape: bbox 10 x 16.5 x 2e-07 mm, 1 faces, 0 solids (baked)
FEATURE [Part::Revolution] Revolve135  label="plugHousing068"
  Angle = 360
  Axis = (0,1,0)
  Base = (0,0,0)
  FaceMakerClass = Part::FaceMakerBullseye
  Placement = pos=(0,0,36.15) rot=(0,0,1;0rad)
  Solid = false
  Source = -> Face131
  Symmetric = false
FEATURE [Part::MultiFuse] Fusion112  label="plugHousing078"
  Placement = pos=(0,0,0) rot=(0,0,1;1.5708rad)
  Shapes = -> [Revolve135,Revolve139]
FEATURE [Part::Feature] Face132
  shape: bbox 10 x 16.5 x 2e-07 mm, 1 faces, 0 solids (baked)
FEATURE [Part::Revolution] Revolve141  label="plugHousing074"
  Angle = 360
  Axis = (0,1,0)
  Base = (0,0,0)
  FaceMakerClass = Part::FaceMakerBullseye
  Placement = pos=(0,0,36.15) rot=(0,0,1;0rad)
  Solid = false
  Source = -> Face132
  Symmetric = false
FEATURE [Part::MultiFuse] Fusion110  label="plugHousing076"
  Placement = pos=(0,0,0) rot=(0,0,1;1.5708rad)
  Shapes = -> [Revolve141,Revolve140]
FEATURE [Part::Feature] Face133
  shape: bbox 10 x 16.5 x 2e-07 mm, 1 faces, 0 solids (baked)
FEATURE [Part::Revolution] Revolve136  label="plugHousing069"
  Angle = 360
  Axis = (0,1,0)
  Base = (0,0,0)
  FaceMakerClass = Part::FaceMakerBullseye
  Placement = pos=(0,0,36.15) rot=(0,0,1;0rad)
  Solid = false
  Source = -> Face133
  Symmetric = false
FEATURE [Part::MultiFuse] Fusion106  label="plugHousing064"
  Placement = pos=(0,0,0) rot=(0,0,1;1.5708rad)
  Shapes = -> [Revolve138,Revolve136]
FEATURE [Part::MultiFuse] Fusion108  label="plugHousing066"
  Placement = pos=(0,19,0) rot=(0,0,1;3.14159rad)
  Shapes = -> [Fusion106,Fusion112]
FEATURE [Part::Feature] Face134
  shape: bbox 10 x 16.5 x 2e-07 mm, 1 faces, 0 solids (baked)
FEATURE [Part::Revolution] Revolve142  label="plugHousing075"
  Angle = 360
  Axis = (0,1,0)
  Base = (0,0,0)
  FaceMakerClass = Part::FaceMakerBullseye
  Placement = pos=(0,0,36.15) rot=(0,0,1;0rad)
  Solid = false
  Source = -> Face134
  Symmetric = false
FEATURE [Part::MultiFuse] Fusion107  label="plugHousing065"
  Placement = pos=(0,0,0) rot=(0,0,1;1.5708rad)
  Shapes = -> [Revolve137,Revolve142]
FEATURE [Part::MultiFuse] Fusion111  label="plugHousing077"
  Placement = pos=(0,19,0) rot=(0,0,1;3.14159rad)
  Shapes = -> [Fusion110,Fusion107]
FEATURE [Part::MultiFuse] Fusion109  label="plugHousing067"
  Placement = pos=(131.236,0,-0.15) rot=(0,0,1;0rad)
  Shapes = -> [Fusion108,Fusion111]
FEATURE [Part::MultiFuse] Fusion113  label="plugHousing079"
  Shapes = -> [Fillet043,Fusion109]
FEATURE [Part::Feature] Face135
  shape: bbox 3.5 x 17.8 x 2e-07 mm, 1 faces, 0 solids (baked)
FEATURE [Part::Revolution] Revolve143  label="removeToCreateScrewAndThreadedInsertHole049"
  Angle = 360
  Axis = (0,1,0)
  Base = (0,0,0)
  FaceMakerClass = Part::FaceMakerBullseye
  Placement = pos=(12.5,0,10) rot=(0,0,1;0rad)
  Solid = false
  Source = -> Face135
  Symmetric = false
FEATURE [Part::Feature] Face136
  shape: bbox 3.5 x 17.8 x 2e-07 mm, 1 faces, 0 solids (baked)
FEATURE [Part::Revolution] Revolve144  label="removeToCreateScrewAndThreadedInsertHole050"
  Angle = 360
  Axis = (0,1,0)
  Base = (0,0,0)
  FaceMakerClass = Part::FaceMakerBullseye
  Placement = pos=(12.5,0,62) rot=(0,0,1;0rad)
  Solid = false
  Source = -> Face136
  Symmetric = false
FEATURE [Part::Feature] Face137
  shape: bbox 3.5 x 17.8 x 2e-07 mm, 1 faces, 0 solids (baked)
FEATURE [Part::Revolution] Revolve145  label="removeToCreateScrewAndThreadedInsertHole051"
  Angle = 360
  Axis = (0,1,0)
  Base = (0,0,0)
  FaceMakerClass = Part::FaceMakerBullseye
  Placement = pos=(89.5,0,68.5) rot=(0,0,1;0rad)
  Solid = false
  Source = -> Face137
  Symmetric = false
FEATURE [Part::Feature] Face138
  shape: bbox 3.5 x 17.8 x 2e-07 mm, 1 faces, 0 solids (baked)
FEATURE [Part::Revolution] Revolve146  label="removeToCreateScrewAndThreadedInsertHole052"
  Angle = 360
  Axis = (0,1,0)
  Base = (0,0,0)
  FaceMakerClass = Part::FaceMakerBullseye
  Placement = pos=(89.5,0,3.5) rot=(0,0,1;0rad)
  Solid = false
  Source = -> Face138
  Symmetric = false
FEATURE [Part::Feature] Face139
  shape: bbox 3.5 x 17.8 x 2e-07 mm, 1 faces, 0 solids (baked)
FEATURE [Part::Revolution] Revolve147  label="removeToCreateScrewAndThreadedInsertHole053"
  Angle = 360
  Axis = (0,1,0)
  Base = (0,0,0)
  FaceMakerClass = Part::FaceMakerBullseye
  Placement = pos=(109.5,4.7,3.5) rot=(0,0,1;0rad)
  Solid = false
  Source = -> Face139
  Symmetric = false
FEATURE [Part::Feature] Face140
  shape: bbox 3.5 x 17.8 x 2e-07 mm, 1 faces, 0 solids (baked)
FEATURE [Part::Revolution] Revolve148  label="removeToCreateScrewAndThreadedInsertHole054"
  Angle = 360
  Axis = (0,1,0)
  Base = (0,0,0)
  FaceMakerClass = Part::FaceMakerBullseye
  Placement = pos=(109.5,4.7,68.5) rot=(0,0,1;0rad)
  Solid = false
  Source = -> Face140
  Symmetric = false
FEATURE [Part::MultiFuse] Fusion114  label="removeToCreateScrewAndThreadedInsertHole055"
  Shapes = -> [Revolve148,Revolve147,Revolve146,Revolve145,Revolve144,Revolve143]
FEATURE [Part::Cut] Cut047  label="casePillars004"
  Base = -> Cut037
  Tool = -> Fusion114
FEATURE [Part::Feature] Face141
  shape: bbox 3.5 x 17.8 x 2e-07 mm, 1 faces, 0 solids (baked)
FEATURE [Part::Feature] Face142
  shape: bbox 3.5 x 17.8 x 2e-07 mm, 1 faces, 0 solids (baked)
FEATURE [Part::Feature] Face143
  shape: bbox 3.5 x 17.8 x 2e-07 mm, 1 faces, 0 solids (baked)
FEATURE [Part::Revolution] Revolve149  label="removeToCreateScrewAndThreadedInsertHole057"
  Angle = 360
  Axis = (0,1,0)
  Base = (0,0,0)
  FaceMakerClass = Part::FaceMakerBullseye
  Placement = pos=(12.5,0,10) rot=(0,0,1;0rad)
  Solid = false
  Source = -> Face141
  Symmetric = false
FEATURE [Part::Feature] Face144
  shape: bbox 3.5 x 17.8 x 2e-07 mm, 1 faces, 0 solids (baked)
FEATURE [Part::Feature] Face145
  shape: bbox 3.5 x 17.8 x 2e-07 mm, 1 faces, 0 solids (baked)
FEATURE [Part::Feature] Face146
  shape: bbox 3.5 x 17.8 x 2e-07 mm, 1 faces, 0 solids (baked)
FEATURE [Part::Revolution] Revolve150  label="removeToCreateScrewAndThreadedInsertHole058"
  Angle = 360
  Axis = (0,1,0)
  Base = (0,0,0)
  FaceMakerClass = Part::FaceMakerBullseye
  Placement = pos=(12.5,0,62) rot=(0,0,1;0rad)
  Solid = false
  Source = -> Face146
  Symmetric = false
FEATURE [Part::Revolution] Revolve151  label="removeToCreateScrewAndThreadedInsertHole059"
  Angle = 360
  Axis = (0,1,0)
  Base = (0,0,0)
  FaceMakerClass = Part::FaceMakerBullseye
  Placement = pos=(89.5,0,68.5) rot=(0,0,1;0rad)
  Solid = false
  Source = -> Face143
  Symmetric = false
FEATURE [Part::Revolution] Revolve152  label="removeToCreateScrewAndThreadedInsertHole060"
  Angle = 360
  Axis = (0,1,0)
  Base = (0,0,0)
  FaceMakerClass = Part::FaceMakerBullseye
  Placement = pos=(89.5,0,3.5) rot=(0,0,1;0rad)
  Solid = false
  Source = -> Face142
  Symmetric = false
FEATURE [Part::Revolution] Revolve153  label="removeToCreateScrewAndThreadedInsertHole061"
  Angle = 360
  Axis = (0,1,0)
  Base = (0,0,0)
  FaceMakerClass = Part::FaceMakerBullseye
  Placement = pos=(109.5,4.7,3.5) rot=(0,0,1;0rad)
  Solid = false
  Source = -> Face145
  Symmetric = false
FEATURE [Part::Revolution] Revolve154  label="removeToCreateScrewAndThreadedInsertHole062"
  Angle = 360
  Axis = (0,1,0)
  Base = (0,0,0)
  FaceMakerClass = Part::FaceMakerBullseye
  Placement = pos=(109.5,4.7,68.5) rot=(0,0,1;0rad)
  Solid = false
  Source = -> Face144
  Symmetric = false
FEATURE [Part::MultiFuse] Fusion115  label="removeToCreateScrewAndThreadedInsertHole056"
  Shapes = -> [Revolve154,Revolve153,Revolve152,Revolve151,Revolve150,Revolve149]
FEATURE [Part::Feature] Face147
  shape: bbox 9.8 x 26.5 x 2e-07 mm, 1 faces, 0 solids (baked)
FEATURE [Part::Revolution] Revolve155
  Angle = 360
  Axis = (0,1,0)
  Base = (0,0,0)
  FaceMakerClass = Part::FaceMakerBullseye
  Placement = pos=(0,0,0) rot=(0,0,1;1.5708rad)
  Solid = false
  Source = -> Face147
  Symmetric = false
FEATURE [Part::Feature] Face148
  shape: bbox 9.8 x 26.5 x 2e-07 mm, 1 faces, 0 solids (baked)
FEATURE [Part::Revolution] Revolve156
  Angle = 360
  Axis = (0,1,0)
  Base = (0,0,0)
  FaceMakerClass = Part::FaceMakerBullseye
  Placement = pos=(0,0,0) rot=(0,0,1;1.5708rad)
  Solid = false
  Source = -> Face148
  Symmetric = false
FEATURE [Part::MultiFuse] Fusion116
  Placement = pos=(-18,19,36) rot=(0,0,1;0rad)
  Shapes = -> [Revolve156,Revolve155]
FEATURE [Part::Box] Box029  label="Cube016"
  AttacherType = Attacher::AttachEngine3D
  Height = 28
  Length = 3
  Placement = pos=(110.7,19,22) rot=(0,0,1;0rad)
  Width = 15.7
FEATURE [Part::Cylinder] Cylinder046
  Angle = 360
  AttacherType = Attacher::AttachEngine3D
  Height = 10
  Placement = pos=(0,0,36.15) rot=(0,0,1;0rad)
  Radius = 4
FEATURE [Part::Cylinder] Cylinder047
  Angle = 360
  AttacherType = Attacher::AttachEngine3D
  Height = 20
  Placement = pos=(0,0,36.15) rot=(0,0,1;0rad)
  Radius = 10.3
FEATURE [Part::MultiFuse] Fusion117  label="removeToCreteHoleForPlugHousing041"
  Placement = pos=(70,19,36) rot=(0,1,0;1.5708rad)
  Shapes = -> [Cylinder047,Cylinder046]
FEATURE [Part::Cut] Cut049  label="plugHousingTab004"
  Base = -> Box029
  Placement = pos=(-107.4,-14,0) rot=(0,0,1;0rad)
  Tool = -> Fusion117
FEATURE [Part::Box] Box030  label="Cube017"
  AttacherType = Attacher::AttachEngine3D
  Height = 28
  Length = 3
  Placement = pos=(110.7,19,22) rot=(0,0,1;0rad)
  Width = 15.7
FEATURE [Part::Cylinder] Cylinder048
  Angle = 360
  AttacherType = Attacher::AttachEngine3D
  Height = 10
  Placement = pos=(0,0,36.15) rot=(0,0,1;0rad)
  Radius = 4
FEATURE [Part::Cylinder] Cylinder049
  Angle = 360
  AttacherType = Attacher::AttachEngine3D
  Height = 20
  Placement = pos=(0,0,36.15) rot=(0,0,1;0rad)
  Radius = 10.3
FEATURE [Part::MultiFuse] Fusion118  label="removeToCreteHoleForPlugHousing042"
  Placement = pos=(70,19,36) rot=(0,1,0;1.5708rad)
  Shapes = -> [Cylinder049,Cylinder048]
FEATURE [Part::Cut] Cut050  label="plugHousingTab005"
  Base = -> Box030
  Placement = pos=(-107.4,-14,0) rot=(0,0,1;0rad)
  Tool = -> Fusion118
FEATURE [Part::MultiFuse] Fusion119
  Placement = pos=(9.6,23,0) rot=(0,0,1;3.14159rad)
  Shapes = -> [Cut049,Cut050]
FEATURE [Part::Box] Box031  label="Cube018"
  AttacherType = Attacher::AttachEngine3D
  Height = 10
  Length = 3
  Placement = pos=(3.3,4,12) rot=(0,0,1;0rad)
  Width = 10
FEATURE [Part::Fillet] Fillet044
  Base = -> Box031
  Edges = 1 edges r=2: [Edge11]
FEATURE [Part::Box] Box032  label="Cube019"
  AttacherType = Attacher::AttachEngine3D
  Height = 10
  Length = 3
  Placement = pos=(3.3,4,50) rot=(0,0,1;0rad)
  Width = 10
FEATURE [Part::Fillet] Fillet045
  Base = -> Box032
  Edges = 1 edges r=2: [Edge12]
FEATURE [Part::Box] Box033  label="Cube020"
  AttacherType = Attacher::AttachEngine3D
  Height = 28
  Length = 4
  Placement = pos=(5,0,22) rot=(0,0,1;0rad)
  Width = 10
FEATURE [Part::Fillet] Fillet046
  Base = -> Box033
  Edges = 1 edges r=1: [Edge7]
FEATURE [Part::Fillet] Fillet047
  Base = -> Fillet046
  Edges = 1 edges r=2: [Edge5]
FEATURE [Part::Fillet] Fillet048
  Base = -> Fillet047
  Edges = 1 edges r=2: [Edge2]
FEATURE [Part::Cylinder] Cylinder050
  Angle = 360
  AttacherType = Attacher::AttachEngine3D
  Height = 20
  Placement = pos=(0,0,36.15) rot=(0,0,1;0rad)
  Radius = 8.2
FEATURE [Part::Cylinder] Cylinder051
  Angle = 360
  AttacherType = Attacher::AttachEngine3D
  Height = 10
  Placement = pos=(0,0,36.15) rot=(0,0,1;0rad)
  Radius = 4
FEATURE [Part::MultiFuse] Fusion120  label="removeToCreteHoleForPlugHousing043"
  Placement = pos=(-42,19,36) rot=(0,1,0;1.5708rad)
  Shapes = -> [Cylinder050,Cylinder051]
FEATURE [Sketcher::SketchObject] Sketch067  label="topSketch018"
  FullyConstrained = true
  sketch-geometry (4):
    g0: LineSegment StartX=16.8446 StartY=31.512 StartZ=0 EndX=16.3251 EndY=34.4666 EndZ=0
    g1: ArcOfCircle CenterX=19 CenterY=19.2524 CenterZ=0 NormalX=0 NormalY=0 NormalZ=1 AngleXU=0 Radius=15.4476 StartAngle=1.74483 EndAngle=2.72717
    g2: ArcOfCircle CenterX=19 CenterY=19.2524 CenterZ=0 NormalX=0 NormalY=0 NormalZ=1 AngleXU=0 Radius=12.4476 StartAngle=1.74483 EndAngle=2.73189
    g3: LineSegment StartX=4.86004 StartY=25.4725 StartZ=0 EndX=7.58253 EndY=24.2107 EndZ=0
  constraints (7):
    c: Block(g0)
    c: Coincident(g1,g0)
    c: Coincident(g2,g0)
    c: Coincident(g3,g1)
    c: Coincident(g3,g2)
    c: Block(g1)
    c: Block(g2)
FEATURE [Part::Extrusion] Extrude058
  Base = -> Sketch067
  Dir = (0,0,1)
  DirMode = 2
  FaceMakerClass = Part::FaceMakerBullseye
  LengthFwd = 10
  LengthRev = 0
  Placement = pos=(0,0,31) rot=(0,0,1;0rad)
  Solid = true
  Symmetric = false
FEATURE [Part::Cut] Cut051
  Base = -> Extrude058
  Tool = -> Fusion120
FEATURE [Part::Fillet] Fillet049
  Base = -> Cut051
  Edges = 1 edges r=2: [Edge1]
FEATURE [Part::Fillet] Fillet050
  Base = -> Fillet049
  Edges = 1 edges r=2.5: [Edge1]
FEATURE [Part::Fillet] Fillet051
  Base = -> Fillet050
  Edges = 1 edges r=2.5: [Edge2]
FEATURE [Part::MultiFuse] Fusion121  label="wireHolder003"
  Shapes = -> [Fusion116,Fillet051]
FEATURE [Part::MultiFuse] Fusion122
  Shapes = -> [Fillet045,Fusion121]
FEATURE [Part::MultiFuse] Fusion123  label="wireHolder004"
  Shapes = -> [Fusion122,Fillet048]
FEATURE [Part::MultiFuse] Fusion124  label="wireHolder005"
  Shapes = -> [Fillet044,Fusion119,Fusion123]
FEATURE [Sketcher::SketchObject] Sketch068  label="topSketch019"
  FullyConstrained = true
  sketch-geometry (6):
    g0: LineSegment StartX=19 StartY=38 StartZ=0 EndX=117 EndY=38 EndZ=0
    g1: ArcOfCircle CenterX=19 CenterY=19 CenterZ=0 NormalX=0 NormalY=0 NormalZ=1 AngleXU=0 Radius=19 StartAngle=1.5708 EndAngle=3.14159
    g2: LineSegment StartX=117 StartY=38 StartZ=0 EndX=117 EndY=19 EndZ=0
    g3: LineSegment StartX=98 StartY=1.0161e-12 StartZ=0 EndX=5.22862e-06 EndY=1.0161e-12 EndZ=0
    g4: LineSegment StartX=5.22862e-06 StartY=19 StartZ=0 EndX=5.22862e-06 EndY=1.0161e-12 EndZ=0
    g5: ArcOfCircle CenterX=98 CenterY=19 CenterZ=0 NormalX=0 NormalY=0 NormalZ=1 AngleXU=0 Radius=19 StartAngle=4.71239 EndAngle=6.28319
  constraints (16):
    c: Horizontal(g0)
    c: Distance(g0) = 98
    c: Coincident(g1,g0)
    c: Block(g1)
    c: Coincident(g2,g0)
    c: Vertical(g2)
    c: Distance(g2) = 19
    c: Horizontal(g3)
    c: Coincident(g4,g1)
    c: Vertical(g4)
    c: Coincident(g3,g4)
    c: Block(g3)
    c: Coincident(g5,g2)
    c: Coincident(g5,g3)
    c: Block(g0)
    c: Block(g5)
FEATURE [Part::Extrusion] Extrude059  label="sideA002"
  Base = -> Sketch068
  Dir = (0,0,1)
  DirMode = 2
  FaceMakerClass = Part::FaceMakerBullseye
  LengthFwd = 3
  LengthRev = 0
  Placement = pos=(0,0,-2.7) rot=(0,0,1;0rad)
  Solid = true
  Symmetric = false
FEATURE [Sketcher::SketchObject] Sketch069  label="topSketch020"
  FullyConstrained = true
  sketch-geometry (6):
    g0: LineSegment StartX=19 StartY=38 StartZ=0 EndX=117 EndY=38 EndZ=0
    g1: ArcOfCircle CenterX=19 CenterY=19 CenterZ=0 NormalX=0 NormalY=0 NormalZ=1 AngleXU=0 Radius=19 StartAngle=1.5708 EndAngle=3.14159
    g2: LineSegment StartX=117 StartY=38 StartZ=0 EndX=117 EndY=19 EndZ=0
    g3: LineSegment StartX=98 StartY=1.0161e-12 StartZ=0 EndX=5.22862e-06 EndY=1.0161e-12 EndZ=0
    g4: LineSegment StartX=5.22862e-06 StartY=19 StartZ=0 EndX=5.22862e-06 EndY=1.0161e-12 EndZ=0
    g5: ArcOfCircle CenterX=98 CenterY=19 CenterZ=0 NormalX=0 NormalY=0 NormalZ=1 AngleXU=0 Radius=19 StartAngle=4.71239 EndAngle=6.28319
  constraints (16):
    c: Horizontal(g0)
    c: Distance(g0) = 98
    c: Coincident(g1,g0)
    c: Block(g1)
    c: Coincident(g2,g0)
    c: Vertical(g2)
    c: Distance(g2) = 19
    c: Horizontal(g3)
    c: Coincident(g4,g1)
    c: Vertical(g4)
    c: Coincident(g3,g4)
    c: Block(g3)
    c: Coincident(g5,g2)
    c: Coincident(g5,g3)
    c: Block(g0)
    c: Block(g5)
FEATURE [Part::Extrusion] Extrude060  label="sideB002"
  Base = -> Sketch069
  Dir = (0,0,1)
  DirMode = 2
  FaceMakerClass = Part::FaceMakerBullseye
  LengthFwd = 3
  LengthRev = 0
  Placement = pos=(0,0,71.7) rot=(0,0,1;0rad)
  Solid = true
  Symmetric = false
FEATURE [Part::MultiFuse] Fusion127  label="removeFromBottom001"
  Placement = pos=(2,0,0) rot=(0,0,1;0rad)
  Shapes = -> [Extrude059,Extrude060]
FEATURE [Part::Cylinder] Cylinder052
  Angle = 360
  AttacherType = Attacher::AttachEngine3D
  Height = 20
  Placement = pos=(0,0,36.15) rot=(0,0,1;0rad)
  Radius = 14
FEATURE [Part::Cylinder] Cylinder053
  Angle = 360
  AttacherType = Attacher::AttachEngine3D
  Height = 10
  Placement = pos=(0,0,36.15) rot=(0,0,1;0rad)
  Radius = 4
FEATURE [Part::MultiFuse] Fusion128  label="removeToCreteHoleForPlugHousing044"
  Placement = pos=(70,19,36) rot=(0,1,0;1.5708rad)
  Shapes = -> [Cylinder052,Cylinder053]
FEATURE [Part::Cut] Cut052  label="bottom011"
  Base = -> Extrude043
  Tool = -> Fusion128
FEATURE [Part::Cut] Cut054  label="bottom012"
  Base = -> Cut052
  Tool = -> Fusion115
FEATURE [Sketcher::SketchObject] Sketch070
  FullyConstrained = true
  Placement = pos=(117,19,0) rot=(0.57735,0.57735,0.57735;2.0944rad)
  sketch-geometry (48):
    g0: LineSegment StartX=-49.19 StartY=69.25 StartZ=0 EndX=-49.19 EndY=66.25 EndZ=0
    g1: LineSegment StartX=-49.19 StartY=63.5 StartZ=0 EndX=-49.19 EndY=60.5 EndZ=0
    g2: LineSegment StartX=-49.19 StartY=57.75 StartZ=0 EndX=-49.19 EndY=54.75 EndZ=0
    g3: LineSegment StartX=-49.19 StartY=52 StartZ=0 EndX=-49.19 EndY=49 EndZ=0
    g4: LineSegment StartX=-49.19 StartY=46.25 StartZ=0 EndX=-49.19 EndY=43.25 EndZ=0
    g5: LineSegment StartX=-49.19 StartY=40.5 StartZ=0 EndX=-49.19 EndY=37.5 EndZ=0
    g6: LineSegment StartX=-49.19 StartY=34.5 StartZ=0 EndX=-49.19 EndY=31.5 EndZ=0
    g7: LineSegment StartX=-49.19 StartY=28.75 StartZ=0 EndX=-49.19 EndY=25.75 EndZ=0
    g8: LineSegment StartX=-49.19 StartY=23 StartZ=0 EndX=-49.19 EndY=20 EndZ=0
    g9: LineSegment StartX=-49.19 StartY=17.25 StartZ=0 EndX=-49.19 EndY=14.25 EndZ=0
    g10: LineSegment StartX=-49.19 StartY=11.5 StartZ=0 EndX=-49.19 EndY=8.5 EndZ=0
    g11: LineSegment StartX=-49.19 StartY=5.75 StartZ=0 EndX=-49.19 EndY=2.75 EndZ=0
    g12: ArcOfCircle CenterX=-1.5 CenterY=67.75 CenterZ=0 NormalX=0 NormalY=0 NormalZ=1 AngleXU=0 Radius=1.5 StartAngle=4.71239 EndAngle=7.85398
    g13: ArcOfCircle CenterX=-1.5 CenterY=62 CenterZ=0 NormalX=0 NormalY=0 NormalZ=1 AngleXU=0 Radius=1.5 StartAngle=4.71239 EndAngle=7.85398
    g14: ArcOfCircle CenterX=-1.5 CenterY=56.25 CenterZ=0 NormalX=0 NormalY=0 NormalZ=1 AngleXU=0 Radius=1.5 StartAngle=4.71239 EndAngle=7.85398
    g15: ArcOfCircle CenterX=-11.49 CenterY=50.5 CenterZ=0 NormalX=0 NormalY=0 NormalZ=1 AngleXU=0 Radius=1.5 StartAngle=4.71239 EndAngle=7.85398
    g16: ArcOfCircle CenterX=-16.28 CenterY=44.75 CenterZ=0 NormalX=0 NormalY=0 NormalZ=1 AngleXU=0 Radius=1.5 StartAngle=4.71239 EndAngle=7.85398
    g17: ArcOfCircle CenterX=-18.2337 CenterY=39 CenterZ=0 NormalX=0 NormalY=0 NormalZ=1 AngleXU=0 Radius=1.5 StartAngle=4.71485 EndAngle=7.85398
    g18: ArcOfCircle CenterX=-16.2837 CenterY=27.25 CenterZ=0 NormalX=0 NormalY=0 NormalZ=1 AngleXU=0 Radius=1.5 StartAngle=4.71485 EndAngle=7.85398
    g19: ArcOfCircle CenterX=-18.2337 CenterY=33 CenterZ=0 NormalX=0 NormalY=0 NormalZ=1 AngleXU=0 Radius=1.5 StartAngle=4.71485 EndAngle=7.85398
    g20: ArcOfCircle CenterX=-11.49 CenterY=21.5 CenterZ=0 NormalX=0 NormalY=0 NormalZ=1 AngleXU=0 Radius=1.5 StartAngle=4.71239 EndAngle=7.85398
    g21: ArcOfCircle CenterX=-1.5 CenterY=4.25 CenterZ=0 NormalX=0 NormalY=0 NormalZ=1 AngleXU=0 Radius=1.5 StartAngle=4.71239 EndAngle=7.85398
    g22: ArcOfCircle CenterX=-1.5 CenterY=10 CenterZ=0 NormalX=0 NormalY=0 NormalZ=1 AngleXU=0 Radius=1.5 StartAngle=4.71239 EndAngle=7.85398
    g23: ArcOfCircle CenterX=-1.5 CenterY=15.75 CenterZ=0 NormalX=0 NormalY=0 NormalZ=1 AngleXU=0 Radius=1.5 StartAngle=4.71239 EndAngle=7.85398
    g24: LineSegment StartX=-49.19 StartY=69.25 StartZ=0 EndX=-1.5 EndY=69.25 EndZ=0
    g25: LineSegment StartX=-49.19 StartY=66.25 StartZ=0 EndX=-1.5 EndY=66.25 EndZ=0
    g26: LineSegment StartX=-49.19 StartY=63.5 StartZ=0 EndX=-1.5 EndY=63.5 EndZ=0
    g27: LineSegment StartX=-49.19 StartY=60.5 StartZ=0 EndX=-1.5 EndY=60.5 EndZ=0
    g28: LineSegment StartX=-49.19 StartY=57.75 StartZ=0 EndX=-1.5 EndY=57.75 EndZ=0
    g29: LineSegment StartX=-49.19 StartY=54.75 StartZ=0 EndX=-1.5 EndY=54.75 EndZ=0
    g30: LineSegment StartX=-49.19 StartY=52 StartZ=0 EndX=-11.49 EndY=52 EndZ=0
    g31: LineSegment StartX=-49.19 StartY=49 StartZ=0 EndX=-11.49 EndY=49 EndZ=0
    g32: LineSegment StartX=-49.19 StartY=46.25 StartZ=0 EndX=-16.28 EndY=46.25 EndZ=0
    g33: LineSegment StartX=-49.19 StartY=43.25 StartZ=0 EndX=-16.28 EndY=43.25 EndZ=0
    g34: LineSegment StartX=-49.19 StartY=40.5 StartZ=0 EndX=-18.2337 EndY=40.5 EndZ=0
    g35: LineSegment StartX=-49.19 StartY=37.5 StartZ=0 EndX=-18.23 EndY=37.5 EndZ=0
    g36: LineSegment StartX=-49.19 StartY=34.5 StartZ=0 EndX=-18.2337 EndY=34.5 EndZ=0
    g37: LineSegment StartX=-49.19 StartY=31.5 StartZ=0 EndX=-18.23 EndY=31.5 EndZ=0
    g38: LineSegment StartX=-49.19 StartY=28.75 StartZ=0 EndX=-16.2837 EndY=28.75 EndZ=0
    g39: LineSegment StartX=-49.19 StartY=25.75 StartZ=0 EndX=-16.28 EndY=25.75 EndZ=0
    g40: LineSegment StartX=-49.19 StartY=23 StartZ=0 EndX=-11.49 EndY=23 EndZ=0
    g41: LineSegment StartX=-49.19 StartY=20 StartZ=0 EndX=-11.49 EndY=20 EndZ=0
    g42: LineSegment StartX=-49.19 StartY=17.25 StartZ=0 EndX=-1.5 EndY=17.25 EndZ=0
    g43: LineSegment StartX=-49.19 StartY=14.25 StartZ=0 EndX=-1.5 EndY=14.25 EndZ=0
    g44: LineSegment StartX=-49.19 StartY=11.5 StartZ=0 EndX=-1.5 EndY=11.5 EndZ=0
    g45: LineSegment StartX=-49.19 StartY=8.5 StartZ=0 EndX=-1.5 EndY=8.5 EndZ=0
    g46: LineSegment StartX=-49.19 StartY=5.75 StartZ=0 EndX=-1.5 EndY=5.75 EndZ=0
    g47: LineSegment StartX=-49.19 StartY=2.75 StartZ=0 EndX=-1.5 EndY=2.75 EndZ=0
  constraints (120):
    c: Vertical(g0)
    c: Distance(g0) = 3
    c: Block(g0)
    c: Vertical(g1)
    c: Distance(g1) = 3
    c: Vertical(g2)
    c: Equal(g0,g2) = 3
    c: Block(g2)
    c: Vertical(g3)
    c: Equal(g1,g3) = 3
    c: Vertical(g4)
    c: Equal(g0,g4) = 3
    c: Block(g4)
    c: Vertical(g5)
    c: Equal(g1,g5) = 3
    c: Vertical(g6)
    c: Equal(g0,g6) = 3
    c: Block(g6)
    c: Vertical(g7)
    c: Equal(g1,g7) = 3
    c: Vertical(g8)
    c: Equal(g0,g8) = 3
    c: Block(g8)
    c: Vertical(g9)
    c: Equal(g1,g9) = 3
    c: Vertical(g10)
    c: Equal(g0,g10) = 3
    c: Block(g10)
    c: Vertical(g11)
    c: Equal(g1,g11) = 3
    c: Block(g12)
    c: Block(g13)
    c: Block(g14)
    c: Block(g15)
    c: Block(g16)
    c: Block(g17)
    c: Block(g18)
    c: Block(g19)
    c: Block(g20)
    c: Block(g21)
    c: Block(g22)
    c: Block(g23)
    c: Block(g11)
    c: Block(g9)
    c: Block(g7)
    c: Block(g5)
    c: Block(g3)
    c: Block(g1)
    c: Coincident(g24,g0)
    c: Coincident(g24,g12)
    c: Horizontal(g24)
    c: Coincident(g25,g0)
    c: Coincident(g25,g12)
    c: Horizontal(g25)
    c: Coincident(g26,g1)
    c: Coincident(g26,g13)
    c: Horizontal(g26)
    c: Coincident(g27,g1)
    c: Coincident(g27,g13)
    c: Horizontal(g27)
    c: Coincident(g28,g2)
    c: Coincident(g28,g14)
    c: Horizontal(g28)
    c: Coincident(g29,g2)
    c: Coincident(g29,g14)
    c: Horizontal(g29)
    c: Coincident(g30,g3)
    c: Coincident(g30,g15)
    c: Horizontal(g30)
    c: Coincident(g31,g3)
    c: Coincident(g31,g15)
    c: Horizontal(g31)
    c: Coincident(g32,g4)
    c: Coincident(g32,g16)
    c: Horizontal(g32)
    c: Coincident(g33,g4)
    c: Coincident(g33,g16)
    c: Horizontal(g33)
    c: Coincident(g34,g5)
    c: Coincident(g34,g17)
    c: Horizontal(g34)
    c: Coincident(g35,g5)
    c: Coincident(g35,g17)
    c: Horizontal(g35)
    c: Coincident(g36,g6)
    c: Coincident(g36,g19)
    c: Horizontal(g36)
    c: Coincident(g37,g6)
    c: Coincident(g37,g19)
    c: Horizontal(g37)
    c: Coincident(g38,g7)
    c: Coincident(g38,g18)
    c: Horizontal(g38)
    c: Coincident(g39,g7)
    c: Coincident(g39,g18)
    c: Horizontal(g39)
    c: Coincident(g40,g8)
    c: Coincident(g40,g20)
    c: Horizontal(g40)
    c: Coincident(g41,g8)
    c: Coincident(g41,g20)
    c: Horizontal(g41)
    c: Coincident(g42,g9)
    c: Coincident(g42,g23)
    c: Horizontal(g42)
    c: Coincident(g43,g9)
    c: Coincident(g43,g23)
    c: Horizontal(g43)
    c: Coincident(g44,g10)
    c: Coincident(g44,g22)
    c: Horizontal(g44)
    c: Coincident(g45,g10)
    c: Coincident(g45,g22)
    c: Horizontal(g45)
    c: Coincident(g46,g11)
    c: Coincident(g46,g21)
    c: Horizontal(g46)
    c: Coincident(g47,g11)
    c: Coincident(g47,g21)
    c: Horizontal(g47)
FEATURE [Part::Extrusion] Extrude061
  Base = -> Sketch070
  Dir = (1,0,0)
  DirMode = 2
  FaceMakerClass = Part::FaceMakerBullseye
  LengthFwd = 23
  LengthRev = 0
  Placement = pos=(-19,0,0) rot=(0,0,1;0rad)
  Solid = true
  Symmetric = false
FEATURE [Part::Fillet] Fillet052  label="removeToCreateVentalationHoles002"
  Base = -> Extrude061
  Edges = <same value as first occurrence — deduplicated (x6 in doc)>
  Placement = pos=(7,0.02,0) rot=(0,0,1;0rad)
FEATURE [Part::MultiFuse] Fusion130  label="bottom013"
  Shapes = -> [Cut054,Cut034]
FEATURE [Part::Cut] Cut055
  Base = -> Fusion130
  Tool = -> Fillet052
FEATURE [Part::Cylinder] Cylinder054
  Angle = 360
  AttacherType = Attacher::AttachEngine3D
  Height = 20
  Placement = pos=(0,0,36.15) rot=(0,0,1;0rad)
  Radius = 4
FEATURE [Sketcher::SketchObject] Sketch071  label="bottomSketch002"
  FullyConstrained = true
  sketch-geometry (32):
    g0: LineSegment StartX=3.3 StartY=-6.03275e-07 StartZ=0 EndX=98 EndY=-6.03275e-07 EndZ=0
    g1: ArcOfCircle CenterX=98 CenterY=19 CenterZ=0 NormalX=0 NormalY=0 NormalZ=1 AngleXU=0 Radius=19 StartAngle=4.71239 EndAngle=5.71103
    g2: LineSegment StartX=6.3 StartY=8 StartZ=0 EndX=3.3 EndY=8 EndZ=0
    g3: LineSegment StartX=3.3 StartY=8 StartZ=0 EndX=3.3 EndY=-6.03275e-07 EndZ=0
    g4: ArcOfCircle CenterX=8.3 CenterY=5 CenterZ=0 NormalX=0 NormalY=0 NormalZ=1 AngleXU=0 Radius=2 StartAngle=3.14159 EndAngle=4.71239
    g5: LineSegment StartX=6.3 StartY=8 StartZ=0 EndX=6.3 EndY=5 EndZ=0
    g6: ArcOfCircle CenterX=98 CenterY=19 CenterZ=0 NormalX=0 NormalY=0 NormalZ=1 AngleXU=0 Radius=12.7 StartAngle=4.71239 EndAngle=6.28319
    g7: LineSegment StartX=94.7 StartY=3 StartZ=0 EndX=8.3 EndY=3 EndZ=0
    g8-g12: Circle x5 (B-spline internal-alignment scaffolding for g13; pole/knot coordinates omitted)
    g13: BSplineCurve PolesCount=5 KnotsCount=3 Degree=3 IsPeriodic=0
    g14: GeomPoint X=98 Y=6.3 Z=0
    g15: GeomPoint X=96.3938 Y=4.71946 Z=0
    g16: GeomPoint X=94.7 Y=3 Z=0
    g17-g23: Circle x7 (B-spline internal-alignment scaffolding for g24; pole/knot coordinates omitted)
    g24: BSplineCurve PolesCount=7 KnotsCount=5 Degree=3 IsPeriodic=0
    g25-g29: GeomPoint x5 (B-spline internal-alignment scaffolding for g24; pole/knot coordinates omitted)
    g30: ArcOfCircle CenterX=98 CenterY=19 CenterZ=0 NormalX=0 NormalY=0 NormalZ=1 AngleXU=0 Radius=15.7 StartAngle=5.81226 EndAngle=6.28319
    g31: LineSegment StartX=110.7 StartY=19 StartZ=0 EndX=113.7 EndY=19 EndZ=0
  constraints (41):
    c: Horizontal(g0)
    c: Coincident(g1,g0)
    c: Block(g1)
    c: Horizontal(g2)
    c: Distance(g2) = 3
    c: Coincident(g3,g2)
    c: Vertical(g3)
    c: Coincident(g3,g0)
    c: Block(g4)
    c: Block(g2)
    c: Coincident(g5,g2)
    c: Coincident(g5,g4)
    c: Vertical(g5)
    c: Coincident(g6,g1)
    c: Block(g6)
    c: Coincident(g7,g4)
    c: Horizontal(g7)
    c: Block(g0)
    c: Block(g7)
    c: Block(g3)
    c: Coincident(g13,g6)
    c: Weight(g8) = 1
    c: Equal(g8, g9-g12) x4
    c: Coincident(g13,g7)
    c: InternalAlignment(g8-g12 -> g13) x5
    c: InternalAlignment(g14,g13)
    c: InternalAlignment(g15,g13)
    c: InternalAlignment(g16,g13)
    c: Block(g13)
    c: Weight(g17) = 1
    c: Equal(g17, g18-g23) x6
    c: Coincident(g24,g1)
    c: InternalAlignment(g17-g23 -> g24) x7
    c: InternalAlignment(g25-g29 -> g24) x5
    c: Block(g24)
    c: Coincident(g30,g24)
    c: Coincident(g31,g6)
    c: Coincident(g31,g30)
    c: Horizontal(g31)
    c: Block(g31)
    c: Block(g30)
FEATURE [Part::Extrusion] Extrude062  label="bottom014"
  Base = -> Sketch071
  Dir = (0,0,1)
  DirMode = 2
  FaceMakerClass = Part::FaceMakerBullseye
  LengthFwd = 71.4
  LengthRev = 0
  Placement = pos=(0,0,0.3) rot=(0,0,1;0rad)
  Solid = true
  Symmetric = false
FEATURE [Part::Fillet] Fillet054
  Base = -> Extrude062
  Edges = 1 edges r=2.4: [Edge17]
FEATURE [Part::Fillet] Fillet055  label="bottom015"
  Base = -> Fillet054
  Edges = 1 edges r=2.4: [Edge36]
FEATURE [Part::Cylinder] Cylinder055
  Angle = 360
  AttacherType = Attacher::AttachEngine3D
  Height = 10
  Placement = pos=(0,0,36.15) rot=(0,0,1;0rad)
  Radius = 4
FEATURE [Part::MultiFuse] Fusion131  label="removeToCreateHoleForPlugHousing002"
  Placement = pos=(70,19,36.15) rot=(0,1,0;1.5708rad)
  Shapes = -> [Cylinder054,Cylinder055]
FEATURE [Part::Cut] Cut056  label="Bottom001"
  Base = -> Fillet055
  Placement = pos=(9,0,0) rot=(0,0,1;0rad)
  Tool = -> Fusion131
FEATURE [Part::Cut] Cut057
  Base = -> Cut055
  Tool = -> Cut056
FEATURE [Sketcher::SketchObject] Sketch072  label="topSketch021"
  FullyConstrained = true
  sketch-geometry (4):
    g0: ArcOfCircle CenterX=105 CenterY=19 CenterZ=0 NormalX=0 NormalY=0 NormalZ=1 AngleXU=0 Radius=20.6155 StartAngle=5.54125 EndAngle=6.28319
    g1: ArcOfCircle CenterX=105 CenterY=19 CenterZ=0 NormalX=0 NormalY=0 NormalZ=1 AngleXU=0 Radius=13 StartAngle=5.54125 EndAngle=6.28319
    g2: LineSegment StartX=118 StartY=19 StartZ=0 EndX=125.616 EndY=19 EndZ=0
    g3: LineSegment StartX=114.583 StartY=10.2157 StartZ=0 EndX=120.197 EndY=5.06982 EndZ=0
  constraints (7):
    c: Block(g0)
    c: Block(g1)
    c: Coincident(g2,g1)
    c: Coincident(g2,g0)
    c: Horizontal(g2)
    c: Coincident(g3,g1)
    c: Coincident(g3,g0)
FEATURE [Part::Extrusion] Extrude063  label="bottomPlugHousingBit003"
  Base = -> Sketch072
  Dir = (0,0,1)
  DirMode = 2
  FaceMakerClass = Part::FaceMakerBullseye
  LengthFwd = 72
  LengthRev = 0
  Solid = true
  Symmetric = false
FEATURE [Part::Cylinder] Cylinder056
  Angle = 360
  AttacherType = Attacher::AttachEngine3D
  Height = 20
  Placement = pos=(0,0,36.15) rot=(0,0,1;0rad)
  Radius = 14.3
FEATURE [Part::Cylinder] Cylinder057
  Angle = 360
  AttacherType = Attacher::AttachEngine3D
  Height = 10
  Placement = pos=(0,0,36.15) rot=(0,0,1;0rad)
  Radius = 4
FEATURE [Part::Box] Box034  label="removeToCreteHoleForPlugHousing047"
  AttacherType = Attacher::AttachEngine3D
  Height = 28.6
  Length = 20
  Placement = pos=(106.15,0,21.7) rot=(0,0,1;0rad)
  Width = 19
FEATURE [Part::Cylinder] Cylinder058
  Angle = 360
  AttacherType = Attacher::AttachEngine3D
  Height = 20
  Placement = pos=(0,0,36.15) rot=(0,0,1;0rad)
  Radius = 14.3
FEATURE [Part::Cylinder] Cylinder059
  Angle = 360
  AttacherType = Attacher::AttachEngine3D
  Height = 10
  Placement = pos=(0,0,36.15) rot=(0,0,1;0rad)
  Radius = 4
FEATURE [Part::MultiFuse] Fusion134  label="removeToCreteHoleForPlugHousing046"
  Placement = pos=(70,19,36) rot=(0,1,0;1.5708rad)
  Shapes = -> [Cylinder058,Cylinder059]
FEATURE [Part::Cylinder] Cylinder060
  Angle = 360
  AttacherType = Attacher::AttachEngine3D
  Height = 20
  Placement = pos=(0,0,36.15) rot=(0,0,1;0rad)
  Radius = 14
FEATURE [Part::Cylinder] Cylinder061
  Angle = 360
  AttacherType = Attacher::AttachEngine3D
  Height = 10
  Placement = pos=(0,0,36.15) rot=(0,0,1;0rad)
  Radius = 4
FEATURE [Part::MultiFuse] Fusion135  label="removeToCreteHoleForPlugHousing048"
  Placement = pos=(70,19,36) rot=(0,1,0;1.5708rad)
  Shapes = -> [Cylinder060,Cylinder061]
FEATURE [Part::Box] Box035  label="removeToCreteHoleForPlugHousing049"
  AttacherType = Attacher::AttachEngine3D
  Height = 28.6
  Length = 20
  Placement = pos=(106.15,0,21.7) rot=(0,0,1;0rad)
  Width = 19
FEATURE [Part::MultiFuse] Fusion133  label="removeToCreteHoleForPlugHousing045"
  Placement = pos=(0,0,-28.3) rot=(0,0,1;0rad)
  Shapes = -> [Box035,Fusion134]
FEATURE [Part::MultiFuse] Fusion138  label="removeToCreteHoleForPlugHousing051"
  Placement = pos=(70,19,36) rot=(0,1,0;1.5708rad)
  Shapes = -> [Cylinder056,Cylinder057]
FEATURE [Part::MultiFuse] Fusion137  label="removeToCreteHoleForPlugHousing050"
  Placement = pos=(0,0,28.3) rot=(0,0,1;0rad)
  Shapes = -> [Box034,Fusion138]
FEATURE [Part::MultiFuse] Fusion132  label="removeToCreatePlugHousingBottomBit002"
  Shapes = -> [Fusion133,Fusion137]
FEATURE [Part::MultiFuse] Fusion136  label="removeToCreatePlugHousingBottomBit003"
  Shapes = -> [Fusion135,Fusion132]
FEATURE [Part::Cut] Cut058  label="bottomPlugHousingBit002"
  Base = -> Extrude063
  Placement = pos=(-0.09,0,0) rot=(0,0,1;0rad)
  Tool = -> Fusion136
FEATURE [Sketcher::SketchObject] Sketch073  label="bottomSketch003"
  FullyConstrained = true
  sketch-geometry (45):
    g0: LineSegment StartX=6.29999 StartY=8 StartZ=0 EndX=3.29999 EndY=8 EndZ=0
    g1: LineSegment StartX=3.29999 StartY=8 StartZ=0 EndX=3.29999 EndY=-6.03275e-07 EndZ=0
    g2: ArcOfCircle CenterX=8.29999 CenterY=5 CenterZ=0 NormalX=0 NormalY=0 NormalZ=1 AngleXU=0 Radius=2 StartAngle=3.14159 EndAngle=4.71239
    g3: LineSegment StartX=6.29999 StartY=8 StartZ=0 EndX=6.29999 EndY=5 EndZ=0
    g4: ArcOfCircle CenterX=105 CenterY=19 CenterZ=0 NormalX=0 NormalY=0 NormalZ=1 AngleXU=0 Radius=12.7 StartAngle=4.71239 EndAngle=5.94289
    g5-g11: Circle x7 (B-spline internal-alignment scaffolding for g12; pole/knot coordinates omitted)
    g12: BSplineCurve PolesCount=7 KnotsCount=5 Degree=3 IsPeriodic=0
    g13-g17: GeomPoint x5 (B-spline internal-alignment scaffolding for g12; pole/knot coordinates omitted)
    g18: ArcOfCircle CenterX=105 CenterY=19 CenterZ=0 NormalX=0 NormalY=0 NormalZ=1 AngleXU=0 Radius=15.7 StartAngle=5.81226 EndAngle=6.28319
    g19: BSplineCurve PolesCount=5 KnotsCount=3 Degree=3 IsPeriodic=0
    g20: LineSegment StartX=8.29999 StartY=3 StartZ=0 EndX=101.7 EndY=3 EndZ=0
    g21: LineSegment StartX=3.29999 StartY=-6.03275e-07 StartZ=0 EndX=105 EndY=-6.03275e-07 EndZ=0
    g22: LineSegment StartX=120.974 StartY=8.71251 StartZ=0 EndX=122.332 EndY=7.83778 EndZ=0
    g23: LineSegment StartX=105 StartY=-6.03274e-07 StartZ=0 EndX=113 EndY=-6.03274e-07 EndZ=0
    g24: ArcOfCircle CenterX=105 CenterY=19 CenterZ=0 NormalX=0 NormalY=0 NormalZ=1 AngleXU=0 Radius=20.6155 StartAngle=5.11091 EndAngle=5.71103
    g25: ArcOfCircle CenterX=117.7 CenterY=19 CenterZ=0 NormalX=0 NormalY=0 NormalZ=1 AngleXU=0 Radius=3 StartAngle=1.2e-15 EndAngle=2.10468
    g26: Circle CenterX=116.345 CenterY=16.3232 CenterZ=0 NormalX=0 NormalY=0 NormalZ=1 AngleXU=0 Radius=1
    g27: Circle CenterX=117.24 CenterY=15.7584 CenterZ=0 NormalX=0 NormalY=0 NormalZ=1 AngleXU=0 Radius=1
    g28: Circle CenterX=116.972 CenterY=14.7612 CenterZ=0 NormalX=0 NormalY=0 NormalZ=1 AngleXU=0 Radius=1
    g29: BSplineCurve PolesCount=3 KnotsCount=2 Degree=2 IsPeriodic=0
    g30: GeomPoint X=116.345 Y=16.3232 Z=0
    g31: GeomPoint X=116.972 Y=14.7612 Z=0
    g32: Circle CenterX=115.828 CenterY=17.157 CenterZ=0 NormalX=0 NormalY=0 NormalZ=1 AngleXU=0 Radius=1
    g33: Circle CenterX=115.841 CenterY=16.639 CenterZ=0 NormalX=0 NormalY=0 NormalZ=1 AngleXU=0 Radius=1
    g34: Circle CenterX=116.345 CenterY=16.3232 CenterZ=0 NormalX=0 NormalY=0 NormalZ=1 AngleXU=0 Radius=1
    g35: BSplineCurve PolesCount=3 KnotsCount=2 Degree=2 IsPeriodic=0
    g36: GeomPoint X=115.828 Y=17.157 Z=0
    g37: GeomPoint X=116.345 Y=16.3232 Z=0
    g38: LineSegment StartX=115.828 StartY=17.157 StartZ=0 EndX=115.828 EndY=20.8307 EndZ=0
    g39: Circle CenterX=115.828 CenterY=20.8307 CenterZ=0 NormalX=0 NormalY=0 NormalZ=1 AngleXU=0 Radius=1
    g40: Circle CenterX=115.831 CenterY=21.3396 CenterZ=0 NormalX=0 NormalY=0 NormalZ=1 AngleXU=0 Radius=1
    g41: Circle CenterX=116.173 CenterY=21.5825 CenterZ=0 NormalX=0 NormalY=0 NormalZ=1 AngleXU=0 Radius=1
    g42: BSplineCurve PolesCount=3 KnotsCount=2 Degree=2 IsPeriodic=0
    g43: GeomPoint X=115.828 Y=20.8307 Z=0
    g44: GeomPoint X=116.173 Y=21.5825 Z=0
  constraints (70):
    c: Horizontal(g0)
    c: Distance(g0) = 3
    c: Coincident(g1,g0)
    c: Vertical(g1)
    c: Block(g2)
    c: Block(g0)
    c: Coincident(g3,g0)
    c: Coincident(g3,g2)
    c: Vertical(g3)
    c: Block(g1)
    c: Block(g4)
    c: Coincident(g19,g4)
    c: Block(g19)
    c: Equal(g5, g6-g11) x6
    c: InternalAlignment(g5-g11 -> g12) x7
    c: InternalAlignment(g13-g17 -> g12) x5
    c: Block(g12)
    c: Coincident(g18,g12)
    c: Block(g18)
    c: Coincident(g20,g2)
    c: Coincident(g20,g19)
    c: Horizontal(g20)
    c: Distance(g20) = 93.4
    c: Coincident(g21,g1)
    c: Horizontal(g21)
    c: Distance(g21) = 101.7
    c: Horizontal(g23)
    c: Distance(g23) = 8
    c: Coincident(g24,g23)
    c: Block(g23)
    c: Coincident(g22,g24)
    c: Block(g24)
    c: Block(g22)
    c: Distance(g22) = 1.61553
    c: Coincident(g25,g18)
    c: Block(g25)
    c: Weight(g26) = 1
    c: Equal(g26,g27)
    c: Equal(g26,g28)
    c: Coincident(g29,g4)
    c: InternalAlignment(g26,g29)
    c: InternalAlignment(g27,g29)
    c: InternalAlignment(g28,g29)
    c: InternalAlignment(g30,g29)
    c: InternalAlignment(g31,g29)
    c: Block(g29)
    c: Weight(g32) = 1
    c: Equal(g32,g33)
    c: Equal(g32,g34)
    c: Coincident(g35,g29)
    c: InternalAlignment(g32,g35)
    c: InternalAlignment(g33,g35)
    c: InternalAlignment(g34,g35)
    c: InternalAlignment(g36,g35)
    c: InternalAlignment(g37,g35)
    c: Block(g35)
    c: Coincident(g38,g35)
    c: Vertical(g38)
    c: Block(g38)
    c: Coincident(g42,g38)
    c: Weight(g39) = 1
    c: Equal(g39,g40)
    c: Equal(g39,g41)
    c: Coincident(g42,g25)
    c: InternalAlignment(g39,g42)
    c: InternalAlignment(g40,g42)
    c: InternalAlignment(g41,g42)
    c: InternalAlignment(g43,g42)
    c: InternalAlignment(g44,g42)
    c: Block(g42)
FEATURE [Part::Extrusion] Extrude064  label="bottom016"
  Base = -> Sketch073
  Dir = (0,0,1)
  DirMode = 2
  FaceMakerClass = Part::FaceMakerBullseye
  LengthFwd = 71.4
  LengthRev = 0
  Placement = pos=(0,0,0.3) rot=(0,0,1;0rad)
  Solid = true
  Symmetric = false
FEATURE [Part::Revolution] Revolve157  label="removeToCreateScrewAndThreadedInsertHole063"
  Angle = 360
  Axis = (0,1,0)
  Base = (0,0,0)
  FaceMakerClass = Part::FaceMakerBullseye
  Placement = pos=(12.5,0,10) rot=(0,0,1;0rad)
  Solid = false
  Source = -> Face141
  Symmetric = false
FEATURE [Sketcher::SketchObject] Sketch074
  FullyConstrained = true
  Placement = pos=(117,19,0) rot=(0.57735,0.57735,0.57735;2.0944rad)
  sketch-geometry (48):
    g0: LineSegment StartX=-49.19 StartY=69.25 StartZ=0 EndX=-49.19 EndY=66.25 EndZ=0
    g1: LineSegment StartX=-49.19 StartY=63.5 StartZ=0 EndX=-49.19 EndY=60.5 EndZ=0
    g2: LineSegment StartX=-49.19 StartY=57.75 StartZ=0 EndX=-49.19 EndY=54.75 EndZ=0
    g3: LineSegment StartX=-49.19 StartY=52 StartZ=0 EndX=-49.19 EndY=49 EndZ=0
    g4: LineSegment StartX=-49.19 StartY=46.25 StartZ=0 EndX=-49.19 EndY=43.25 EndZ=0
    g5: LineSegment StartX=-49.19 StartY=40.5 StartZ=0 EndX=-49.19 EndY=37.5 EndZ=0
    g6: LineSegment StartX=-49.19 StartY=34.5 StartZ=0 EndX=-49.19 EndY=31.5 EndZ=0
    g7: LineSegment StartX=-49.19 StartY=28.75 StartZ=0 EndX=-49.19 EndY=25.75 EndZ=0
    g8: LineSegment StartX=-49.19 StartY=23 StartZ=0 EndX=-49.19 EndY=20 EndZ=0
    g9: LineSegment StartX=-49.19 StartY=17.25 StartZ=0 EndX=-49.19 EndY=14.25 EndZ=0
    g10: LineSegment StartX=-49.19 StartY=11.5 StartZ=0 EndX=-49.19 EndY=8.5 EndZ=0
    g11: LineSegment StartX=-49.19 StartY=5.75 StartZ=0 EndX=-49.19 EndY=2.75 EndZ=0
    g12: ArcOfCircle CenterX=-1.5 CenterY=67.75 CenterZ=0 NormalX=0 NormalY=0 NormalZ=1 AngleXU=0 Radius=1.5 StartAngle=4.71239 EndAngle=7.85398
    g13: ArcOfCircle CenterX=-1.5 CenterY=62 CenterZ=0 NormalX=0 NormalY=0 NormalZ=1 AngleXU=0 Radius=1.5 StartAngle=4.71239 EndAngle=7.85398
    g14: ArcOfCircle CenterX=-1.5 CenterY=56.25 CenterZ=0 NormalX=0 NormalY=0 NormalZ=1 AngleXU=0 Radius=1.5 StartAngle=4.71239 EndAngle=7.85398
    g15: ArcOfCircle CenterX=-11.49 CenterY=50.5 CenterZ=0 NormalX=0 NormalY=0 NormalZ=1 AngleXU=0 Radius=1.5 StartAngle=4.71239 EndAngle=7.85398
    g16: ArcOfCircle CenterX=-16.28 CenterY=44.75 CenterZ=0 NormalX=0 NormalY=0 NormalZ=1 AngleXU=0 Radius=1.5 StartAngle=4.71239 EndAngle=7.85398
    g17: ArcOfCircle CenterX=-18.2337 CenterY=39 CenterZ=0 NormalX=0 NormalY=0 NormalZ=1 AngleXU=0 Radius=1.5 StartAngle=4.71485 EndAngle=7.85398
    g18: ArcOfCircle CenterX=-16.2837 CenterY=27.25 CenterZ=0 NormalX=0 NormalY=0 NormalZ=1 AngleXU=0 Radius=1.5 StartAngle=4.71485 EndAngle=7.85398
    g19: ArcOfCircle CenterX=-18.2337 CenterY=33 CenterZ=0 NormalX=0 NormalY=0 NormalZ=1 AngleXU=0 Radius=1.5 StartAngle=4.71485 EndAngle=7.85398
    g20: ArcOfCircle CenterX=-11.49 CenterY=21.5 CenterZ=0 NormalX=0 NormalY=0 NormalZ=1 AngleXU=0 Radius=1.5 StartAngle=4.71239 EndAngle=7.85398
    g21: ArcOfCircle CenterX=-1.5 CenterY=4.25 CenterZ=0 NormalX=0 NormalY=0 NormalZ=1 AngleXU=0 Radius=1.5 StartAngle=4.71239 EndAngle=7.85398
    g22: ArcOfCircle CenterX=-1.5 CenterY=10 CenterZ=0 NormalX=0 NormalY=0 NormalZ=1 AngleXU=0 Radius=1.5 StartAngle=4.71239 EndAngle=7.85398
    g23: ArcOfCircle CenterX=-1.5 CenterY=15.75 CenterZ=0 NormalX=0 NormalY=0 NormalZ=1 AngleXU=0 Radius=1.5 StartAngle=4.71239 EndAngle=7.85398
    g24: LineSegment StartX=-49.19 StartY=69.25 StartZ=0 EndX=-1.5 EndY=69.25 EndZ=0
    g25: LineSegment StartX=-49.19 StartY=66.25 StartZ=0 EndX=-1.5 EndY=66.25 EndZ=0
    g26: LineSegment StartX=-49.19 StartY=63.5 StartZ=0 EndX=-1.5 EndY=63.5 EndZ=0
    g27: LineSegment StartX=-49.19 StartY=60.5 StartZ=0 EndX=-1.5 EndY=60.5 EndZ=0
    g28: LineSegment StartX=-49.19 StartY=57.75 StartZ=0 EndX=-1.5 EndY=57.75 EndZ=0
    g29: LineSegment StartX=-49.19 StartY=54.75 StartZ=0 EndX=-1.5 EndY=54.75 EndZ=0
    g30: LineSegment StartX=-49.19 StartY=52 StartZ=0 EndX=-11.49 EndY=52 EndZ=0
    g31: LineSegment StartX=-49.19 StartY=49 StartZ=0 EndX=-11.49 EndY=49 EndZ=0
    g32: LineSegment StartX=-49.19 StartY=46.25 StartZ=0 EndX=-16.28 EndY=46.25 EndZ=0
    g33: LineSegment StartX=-49.19 StartY=43.25 StartZ=0 EndX=-16.28 EndY=43.25 EndZ=0
    g34: LineSegment StartX=-49.19 StartY=40.5 StartZ=0 EndX=-18.2337 EndY=40.5 EndZ=0
    g35: LineSegment StartX=-49.19 StartY=37.5 StartZ=0 EndX=-18.23 EndY=37.5 EndZ=0
    g36: LineSegment StartX=-49.19 StartY=34.5 StartZ=0 EndX=-18.2337 EndY=34.5 EndZ=0
    g37: LineSegment StartX=-49.19 StartY=31.5 StartZ=0 EndX=-18.23 EndY=31.5 EndZ=0
    g38: LineSegment StartX=-49.19 StartY=28.75 StartZ=0 EndX=-16.2837 EndY=28.75 EndZ=0
    g39: LineSegment StartX=-49.19 StartY=25.75 StartZ=0 EndX=-16.28 EndY=25.75 EndZ=0
    g40: LineSegment StartX=-49.19 StartY=23 StartZ=0 EndX=-11.49 EndY=23 EndZ=0
    g41: LineSegment StartX=-49.19 StartY=20 StartZ=0 EndX=-11.49 EndY=20 EndZ=0
    g42: LineSegment StartX=-49.19 StartY=17.25 StartZ=0 EndX=-1.5 EndY=17.25 EndZ=0
    g43: LineSegment StartX=-49.19 StartY=14.25 StartZ=0 EndX=-1.5 EndY=14.25 EndZ=0
    g44: LineSegment StartX=-49.19 StartY=11.5 StartZ=0 EndX=-1.5 EndY=11.5 EndZ=0
    g45: LineSegment StartX=-49.19 StartY=8.5 StartZ=0 EndX=-1.5 EndY=8.5 EndZ=0
    g46: LineSegment StartX=-49.19 StartY=5.75 StartZ=0 EndX=-1.5 EndY=5.75 EndZ=0
    g47: LineSegment StartX=-49.19 StartY=2.75 StartZ=0 EndX=-1.5 EndY=2.75 EndZ=0
  constraints (120):
    c: Vertical(g0)
    c: Distance(g0) = 3
    c: Block(g0)
    c: Vertical(g1)
    c: Distance(g1) = 3
    c: Vertical(g2)
    c: Equal(g0,g2) = 3
    c: Block(g2)
    c: Vertical(g3)
    c: Equal(g1,g3) = 3
    c: Vertical(g4)
    c: Equal(g0,g4) = 3
    c: Block(g4)
    c: Vertical(g5)
    c: Equal(g1,g5) = 3
    c: Vertical(g6)
    c: Equal(g0,g6) = 3
    c: Block(g6)
    c: Vertical(g7)
    c: Equal(g1,g7) = 3
    c: Vertical(g8)
    c: Equal(g0,g8) = 3
    c: Block(g8)
    c: Vertical(g9)
    c: Equal(g1,g9) = 3
    c: Vertical(g10)
    c: Equal(g0,g10) = 3
    c: Block(g10)
    c: Vertical(g11)
    c: Equal(g1,g11) = 3
    c: Block(g12)
    c: Block(g13)
    c: Block(g14)
    c: Block(g15)
    c: Block(g16)
    c: Block(g17)
    c: Block(g18)
    c: Block(g19)
    c: Block(g20)
    c: Block(g21)
    c: Block(g22)
    c: Block(g23)
    c: Block(g11)
    c: Block(g9)
    c: Block(g7)
    c: Block(g5)
    c: Block(g3)
    c: Block(g1)
    c: Coincident(g24,g0)
    c: Coincident(g24,g12)
    c: Horizontal(g24)
    c: Coincident(g25,g0)
    c: Coincident(g25,g12)
    c: Horizontal(g25)
    c: Coincident(g26,g1)
    c: Coincident(g26,g13)
    c: Horizontal(g26)
    c: Coincident(g27,g1)
    c: Coincident(g27,g13)
    c: Horizontal(g27)
    c: Coincident(g28,g2)
    c: Coincident(g28,g14)
    c: Horizontal(g28)
    c: Coincident(g29,g2)
    c: Coincident(g29,g14)
    c: Horizontal(g29)
    c: Coincident(g30,g3)
    c: Coincident(g30,g15)
    c: Horizontal(g30)
    c: Coincident(g31,g3)
    c: Coincident(g31,g15)
    c: Horizontal(g31)
    c: Coincident(g32,g4)
    c: Coincident(g32,g16)
    c: Horizontal(g32)
    c: Coincident(g33,g4)
    c: Coincident(g33,g16)
    c: Horizontal(g33)
    c: Coincident(g34,g5)
    c: Coincident(g34,g17)
    c: Horizontal(g34)
    c: Coincident(g35,g5)
    c: Coincident(g35,g17)
    c: Horizontal(g35)
    c: Coincident(g36,g6)
    c: Coincident(g36,g19)
    c: Horizontal(g36)
    c: Coincident(g37,g6)
    c: Coincident(g37,g19)
    c: Horizontal(g37)
    c: Coincident(g38,g7)
    c: Coincident(g38,g18)
    c: Horizontal(g38)
    c: Coincident(g39,g7)
    c: Coincident(g39,g18)
    c: Horizontal(g39)
    c: Coincident(g40,g8)
    c: Coincident(g40,g20)
    c: Horizontal(g40)
    c: Coincident(g41,g8)
    c: Coincident(g41,g20)
    c: Horizontal(g41)
    c: Coincident(g42,g9)
    c: Coincident(g42,g23)
    c: Horizontal(g42)
    c: Coincident(g43,g9)
    c: Coincident(g43,g23)
    c: Horizontal(g43)
    c: Coincident(g44,g10)
    c: Coincident(g44,g22)
    c: Horizontal(g44)
    c: Coincident(g45,g10)
    c: Coincident(g45,g22)
    c: Horizontal(g45)
    c: Coincident(g46,g11)
    c: Coincident(g46,g21)
    c: Horizontal(g46)
    c: Coincident(g47,g11)
    c: Coincident(g47,g21)
    c: Horizontal(g47)
FEATURE [Part::Extrusion] Extrude065
  Base = -> Sketch074
  Dir = (1,0,0)
  DirMode = 2
  FaceMakerClass = Part::FaceMakerBullseye
  LengthFwd = 23
  LengthRev = 0
  Placement = pos=(-19,0,0) rot=(0,0,1;0rad)
  Solid = true
  Symmetric = false
FEATURE [Part::Fillet] Fillet056  label="removeToCreateVentalationHoles003"
  Base = -> Extrude065
  Edges = <same value as first occurrence — deduplicated (x6 in doc)>
  Placement = pos=(7,0.02,0) rot=(0,0,1;0rad)
FEATURE [Part::Revolution] Revolve158  label="removeToCreateScrewAndThreadedInsertHole065"
  Angle = 360
  Axis = (0,1,0)
  Base = (0,0,0)
  FaceMakerClass = Part::FaceMakerBullseye
  Placement = pos=(12.5,0,62) rot=(0,0,1;0rad)
  Solid = false
  Source = -> Face146
  Symmetric = false
FEATURE [Part::Revolution] Revolve159  label="removeToCreateScrewAndThreadedInsertHole066"
  Angle = 360
  Axis = (0,1,0)
  Base = (0,0,0)
  FaceMakerClass = Part::FaceMakerBullseye
  Placement = pos=(89.5,0,68.5) rot=(0,0,1;0rad)
  Solid = false
  Source = -> Face143
  Symmetric = false
FEATURE [Part::Revolution] Revolve160  label="removeToCreateScrewAndThreadedInsertHole067"
  Angle = 360
  Axis = (0,1,0)
  Base = (0,0,0)
  FaceMakerClass = Part::FaceMakerBullseye
  Placement = pos=(89.5,0,3.5) rot=(0,0,1;0rad)
  Solid = false
  Source = -> Face142
  Symmetric = false
FEATURE [Part::Revolution] Revolve161  label="removeToCreateScrewAndThreadedInsertHole068"
  Angle = 360
  Axis = (0,1,0)
  Base = (0,0,0)
  FaceMakerClass = Part::FaceMakerBullseye
  Placement = pos=(109.5,4.7,3.5) rot=(0,0,1;0rad)
  Solid = false
  Source = -> Face145
  Symmetric = false
FEATURE [Part::Revolution] Revolve162  label="removeToCreateScrewAndThreadedInsertHole069"
  Angle = 360
  Axis = (0,1,0)
  Base = (0,0,0)
  FaceMakerClass = Part::FaceMakerBullseye
  Placement = pos=(109.5,4.7,68.5) rot=(0,0,1;0rad)
  Solid = false
  Source = -> Face144
  Symmetric = false
FEATURE [Part::MultiFuse] Fusion141  label="removeToCreateScrewAndThreadedInsertHole064"
  Shapes = -> [Revolve162,Revolve161,Revolve160,Revolve159,Revolve158,Revolve157]
FEATURE [Part::Cylinder] Cylinder062
  Angle = 360
  AttacherType = Attacher::AttachEngine3D
  Height = 20
  Placement = pos=(0,0,36.15) rot=(0,0,1;0rad)
  Radius = 14
FEATURE [Part::Cylinder] Cylinder063
  Angle = 360
  AttacherType = Attacher::AttachEngine3D
  Height = 10
  Placement = pos=(0,0,36.15) rot=(0,0,1;0rad)
  Radius = 4
FEATURE [Part::MultiFuse] Fusion139  label="removeToCreteHoleForPlugHousing052"
  Placement = pos=(70,19,36) rot=(0,1,0;1.5708rad)
  Shapes = -> [Cylinder062,Cylinder063]
FEATURE [Part::Cut] Cut060  label="bottom017"
  Base = -> Extrude064
  Tool = -> Fusion139
FEATURE [Part::Cut] Cut061  label="bottom019"
  Base = -> Cut060
  Tool = -> Fusion141
FEATURE [Part::MultiFuse] Fusion140  label="bottom018"
  Shapes = -> [Cut061,Cut058]
FEATURE [Part::Cut] Cut059  label="bottom020"
  Base = -> Fusion140
  Tool = -> Fillet056
FEATURE [Part::Box] Box036  label="Cube021"
  AttacherType = Attacher::AttachEngine3D
  Height = 80
  Length = 26
  Placement = pos=(0,-1,-5) rot=(0,0,1;0rad)
  Width = 11
FEATURE [Part::Cut] Cut062  label="removeFromBottom002"
  Base = -> Cut057
  Tool = -> Box036
FEATURE [Part::Cut] Cut063
  Base = -> Cut059
  Tool = -> Cut062
FEATURE [Part::Cut] Cut064  label="pcbStands"
  Base = -> Fusion095
  Tool = -> Fusion127
FEATURE [Sketcher::SketchObject] Sketch075  label="topSketch022"
  FullyConstrained = true
  sketch-geometry (6):
    g0: LineSegment StartX=19 StartY=38 StartZ=0 EndX=117 EndY=38 EndZ=0
    g1: ArcOfCircle CenterX=19 CenterY=19 CenterZ=0 NormalX=0 NormalY=0 NormalZ=1 AngleXU=0 Radius=19 StartAngle=1.5708 EndAngle=3.14159
    g2: LineSegment StartX=117 StartY=38 StartZ=0 EndX=117 EndY=19 EndZ=0
    g3: LineSegment StartX=98 StartY=1.0161e-12 StartZ=0 EndX=5.22862e-06 EndY=1.0161e-12 EndZ=0
    g4: LineSegment StartX=5.22862e-06 StartY=19 StartZ=0 EndX=5.22862e-06 EndY=1.0161e-12 EndZ=0
    g5: ArcOfCircle CenterX=98 CenterY=19 CenterZ=0 NormalX=0 NormalY=0 NormalZ=1 AngleXU=0 Radius=19 StartAngle=4.71239 EndAngle=6.28319
  constraints (16):
    c: Horizontal(g0)
    c: Distance(g0) = 98
    c: Coincident(g1,g0)
    c: Block(g1)
    c: Coincident(g2,g0)
    c: Vertical(g2)
    c: Distance(g2) = 19
    c: Horizontal(g3)
    c: Coincident(g4,g1)
    c: Vertical(g4)
    c: Coincident(g3,g4)
    c: Block(g3)
    c: Coincident(g5,g2)
    c: Coincident(g5,g3)
    c: Block(g0)
    c: Block(g5)
FEATURE [Part::Extrusion] Extrude067  label="sideB003"
  Base = -> Sketch075
  Dir = (0,0,1)
  DirMode = 2
  FaceMakerClass = Part::FaceMakerBullseye
  LengthFwd = 3
  LengthRev = 0
  Placement = pos=(0,0,71.7) rot=(0,0,1;0rad)
  Solid = true
  Symmetric = false
FEATURE [Sketcher::SketchObject] Sketch076  label="topSketch023"
  FullyConstrained = true
  sketch-geometry (6):
    g0: LineSegment StartX=19 StartY=38 StartZ=0 EndX=117 EndY=38 EndZ=0
    g1: ArcOfCircle CenterX=19 CenterY=19 CenterZ=0 NormalX=0 NormalY=0 NormalZ=1 AngleXU=0 Radius=19 StartAngle=1.5708 EndAngle=3.14159
    g2: LineSegment StartX=117 StartY=38 StartZ=0 EndX=117 EndY=19 EndZ=0
    g3: LineSegment StartX=98 StartY=1.0161e-12 StartZ=0 EndX=5.22862e-06 EndY=1.0161e-12 EndZ=0
    g4: LineSegment StartX=5.22862e-06 StartY=19 StartZ=0 EndX=5.22862e-06 EndY=1.0161e-12 EndZ=0
    g5: ArcOfCircle CenterX=98 CenterY=19 CenterZ=0 NormalX=0 NormalY=0 NormalZ=1 AngleXU=0 Radius=19 StartAngle=4.71239 EndAngle=6.28319
  constraints (16):
    c: Horizontal(g0)
    c: Distance(g0) = 98
    c: Coincident(g1,g0)
    c: Block(g1)
    c: Coincident(g2,g0)
    c: Vertical(g2)
    c: Distance(g2) = 19
    c: Horizontal(g3)
    c: Coincident(g4,g1)
    c: Vertical(g4)
    c: Coincident(g3,g4)
    c: Block(g3)
    c: Coincident(g5,g2)
    c: Coincident(g5,g3)
    c: Block(g0)
    c: Block(g5)
FEATURE [Part::Extrusion] Extrude066  label="sideA003"
  Base = -> Sketch076
  Dir = (0,0,1)
  DirMode = 2
  FaceMakerClass = Part::FaceMakerBullseye
  LengthFwd = 3
  LengthRev = 0
  Placement = pos=(0,0,-2.7) rot=(0,0,1;0rad)
  Solid = true
  Symmetric = false
FEATURE [Part::MultiFuse] Fusion142  label="removeFromBottom003"
  Placement = pos=(2,0,0) rot=(0,0,1;0rad)
  Shapes = -> [Extrude066,Extrude067]
FEATURE [Part::Cut] Cut065  label="screwRetainers002"
  Base = -> Fusion096
  Tool = -> Fusion142
FEATURE [Sketcher::SketchObject] Sketch077
  FullyConstrained = true
  Placement = pos=(117,19,0) rot=(0.57735,0.57735,0.57735;2.0944rad)
  sketch-geometry (8):
    g0: LineSegment StartX=-49.19 StartY=63.5 StartZ=0 EndX=-49.19 EndY=60.5 EndZ=0
    g1: LineSegment StartX=-49.19 StartY=11.5 StartZ=0 EndX=-49.19 EndY=8.5 EndZ=0
    g2: ArcOfCircle CenterX=-1.5 CenterY=62 CenterZ=0 NormalX=0 NormalY=0 NormalZ=1 AngleXU=0 Radius=1.5 StartAngle=4.71239 EndAngle=7.85398
    g3: ArcOfCircle CenterX=-1.5 CenterY=10 CenterZ=0 NormalX=0 NormalY=0 NormalZ=1 AngleXU=0 Radius=1.5 StartAngle=4.71239 EndAngle=7.85398
    g4: LineSegment StartX=-49.19 StartY=63.5 StartZ=0 EndX=-1.5 EndY=63.5 EndZ=0
    g5: LineSegment StartX=-49.19 StartY=60.5 StartZ=0 EndX=-1.5 EndY=60.5 EndZ=0
    g6: LineSegment StartX=-49.19 StartY=11.5 StartZ=0 EndX=-1.5 EndY=11.5 EndZ=0
    g7: LineSegment StartX=-49.19 StartY=8.5 StartZ=0 EndX=-1.5 EndY=8.5 EndZ=0
  constraints (19):
    c: Vertical(g0)
    c: Distance(g0) = 3
    c: Vertical(g1)
    c: Block(g1)
    c: Block(g2)
    c: Block(g3)
    c: Block(g0)
    c: Coincident(g4,g0)
    c: Coincident(g4,g2)
    c: Horizontal(g4)
    c: Coincident(g5,g0)
    c: Coincident(g5,g2)
    c: Horizontal(g5)
    c: Coincident(g6,g1)
    c: Coincident(g6,g3)
    c: Horizontal(g6)
    c: Coincident(g7,g1)
    c: Coincident(g7,g3)
    c: Horizontal(g7)
FEATURE [Part::Extrusion] Extrude068
  Base = -> Sketch077
  Dir = (1,0,0)
  DirMode = 2
  FaceMakerClass = Part::FaceMakerBullseye
  LengthFwd = 10
  LengthRev = 0
  Solid = true
  Symmetric = false
FEATURE [Part::Fillet] Fillet057  label="removeFromtMoreFrontCaseScrewRetainers002"
  Base = -> Extrude068
  Edges = 4 edges r=1.49: [Edge6,Edge11,Edge18,Edge23]
  Placement = pos=(-12,0,0) rot=(0,0,1;0rad)
FEATURE [Sketcher::SketchObject] Sketch078
  FullyConstrained = true
  Placement = pos=(117,19,0) rot=(0.57735,0.57735,0.57735;2.0944rad)
  sketch-geometry (8):
    g0: LineSegment StartX=-49.19 StartY=69.25 StartZ=0 EndX=-49.19 EndY=66.25 EndZ=0
    g1: LineSegment StartX=-49.19 StartY=5.75 StartZ=0 EndX=-49.19 EndY=2.75 EndZ=0
    g2: ArcOfCircle CenterX=-1.5 CenterY=67.75 CenterZ=0 NormalX=0 NormalY=0 NormalZ=1 AngleXU=0 Radius=1.5 StartAngle=4.71239 EndAngle=7.85398
    g3: ArcOfCircle CenterX=-1.5 CenterY=4.25 CenterZ=0 NormalX=0 NormalY=0 NormalZ=1 AngleXU=0 Radius=1.5 StartAngle=4.71239 EndAngle=7.85398
    g4: LineSegment StartX=-49.19 StartY=69.25 StartZ=0 EndX=-1.5 EndY=69.25 EndZ=0
    g5: LineSegment StartX=-49.19 StartY=66.25 StartZ=0 EndX=-1.5 EndY=66.25 EndZ=0
    g6: LineSegment StartX=-49.19 StartY=5.75 StartZ=0 EndX=-1.5 EndY=5.75 EndZ=0
    g7: LineSegment StartX=-49.19 StartY=2.75 StartZ=0 EndX=-1.5 EndY=2.75 EndZ=0
  constraints (19):
    c: Vertical(g0)
    c: Distance(g0) = 3
    c: Block(g0)
    c: Vertical(g1)
    c: Block(g2)
    c: Block(g3)
    c: Block(g1)
    c: Coincident(g4,g0)
    c: Coincident(g4,g2)
    c: Horizontal(g4)
    c: Coincident(g5,g0)
    c: Coincident(g5,g2)
    c: Horizontal(g5)
    c: Coincident(g6,g1)
    c: Coincident(g6,g3)
    c: Horizontal(g6)
    c: Coincident(g7,g1)
    c: Coincident(g7,g3)
    c: Horizontal(g7)
FEATURE [Part::Extrusion] Extrude069
  Base = -> Sketch078
  Dir = (1,0,0)
  DirMode = 2
  FaceMakerClass = Part::FaceMakerBullseye
  LengthFwd = 10
  LengthRev = 0
  Solid = true
  Symmetric = false
FEATURE [Part::Fillet] Fillet058  label="removeFromtMoreFrontCaseScrewRetainers003"
  Base = -> Extrude069
  Edges = 4 edges r=1.49: [Edge6,Edge11,Edge18,Edge23]
  Placement = pos=(-4,0,0) rot=(0,0,1;0rad)
FEATURE [Part::Cut] Cut066
  Base = -> Cut065
  Tool = -> Fillet058
FEATURE [Part::Cut] Cut067  label="screwPillars"
  Base = -> Cut066
  Tool = -> Fillet057
FEATURE [Part::MultiFuse] Fusion143  label="bottom021"
  Shapes = -> [Cut031,Cut063]
FEATURE [Part::Cylinder] Cylinder
  Angle = 360
  AttacherType = Attacher::AttachEngine3D
  Height = 10
  Placement = pos=(20.65,12,4.68) rot=(1,0,0;1.5708rad)
  Radius = 2
FEATURE [Part::Cylinder] Cylinder064
  Angle = 360
  AttacherType = Attacher::AttachEngine3D
  Height = 10
  Placement = pos=(20.65,12,67.38) rot=(1,0,0;1.5708rad)
  Radius = 2
FEATURE [Part::Cylinder] Cylinder065
  Angle = 360
  AttacherType = Attacher::AttachEngine3D
  Height = 10
  Placement = pos=(77.15,12,67.38) rot=(1,0,0;1.5708rad)
  Radius = 2
FEATURE [Part::Cylinder] Cylinder066
  Angle = 360
  AttacherType = Attacher::AttachEngine3D
  Height = 10
  Placement = pos=(77.15,12,4.68) rot=(1,0,0;1.5708rad)
  Radius = 2
FEATURE [Part::MultiFuse] Fusion144  label="removeFromThreadedInsertHousing"
  Shapes = -> [Cylinder065,Cylinder064,Cylinder,Cylinder066]
FEATURE [Part::Cut] Cut068  label="pcbStands001"
  Base = -> Cut064
  Tool = -> Fusion144
FEATURE [Part::MultiFuse] Fusion145
  Shapes = -> [Cut068,Fusion143]
FEATURE [Part::MultiFuse] Fusion146
  Shapes = -> [Fusion145]
FEATURE [Part::MultiFuse] Fusion147  label="bottom022"
  Shapes = -> [Cut067,Fusion146]
FEATURE [Part::MultiFuse] Fusion148  label="casePillars005"
  Shapes = -> [Cut047,Fusion092]
FEATURE [Part::MultiFuse] Fusion149  label="bottom023"
  Shapes = -> [Fusion124,Fusion113,Fusion147]
FEATURE [Part::MultiFuse] Fusion150  label="topBits"
  Shapes = -> [Cut025,Fusion148,Cut030,Fillet034]
FEATURE [Part::Feature] Face149 .. Face152  x4 (patterned run collapsed; names and placements below)
  shape: bbox 3.2 x 1.5 x 2e-07 mm, 1 faces, 0 solids (baked)
FEATURE [Part::Feature] Face153
  shape: bbox 3.6 x 3.2 x 2e-07 mm, 1 faces, 0 solids (baked)
FEATURE [Part::Feature] Face154
  shape: bbox 3.6 x 3.2 x 2e-07 mm, 1 faces, 0 solids (baked)
FEATURE [Sketcher::SketchObject] Sketch079  label="topSketch024"
  FullyConstrained = true
  sketch-geometry (6):
    g0: LineSegment StartX=19 StartY=38 StartZ=0 EndX=117 EndY=38 EndZ=0
    g1: ArcOfCircle CenterX=19 CenterY=19 CenterZ=0 NormalX=0 NormalY=0 NormalZ=1 AngleXU=0 Radius=19 StartAngle=1.5708 EndAngle=3.14159
    g2: LineSegment StartX=117 StartY=38 StartZ=0 EndX=117 EndY=19 EndZ=0
    g3: LineSegment StartX=98 StartY=1.0161e-12 StartZ=0 EndX=5.22862e-06 EndY=1.0161e-12 EndZ=0
    g4: LineSegment StartX=5.22862e-06 StartY=19 StartZ=0 EndX=5.22862e-06 EndY=1.0161e-12 EndZ=0
    g5: ArcOfCircle CenterX=98 CenterY=19 CenterZ=0 NormalX=0 NormalY=0 NormalZ=1 AngleXU=0 Radius=19 StartAngle=4.71239 EndAngle=6.28319
  constraints (16):
    c: Horizontal(g0)
    c: Distance(g0) = 98
    c: Coincident(g1,g0)
    c: Block(g1)
    c: Coincident(g2,g0)
    c: Vertical(g2)
    c: Distance(g2) = 19
    c: Horizontal(g3)
    c: Coincident(g4,g1)
    c: Vertical(g4)
    c: Coincident(g3,g4)
    c: Block(g3)
    c: Coincident(g5,g2)
    c: Coincident(g5,g3)
    c: Block(g0)
    c: Block(g5)
FEATURE [Sketcher::SketchObject] Sketch080  label="topSketch025"
  FullyConstrained = true
  sketch-geometry (6):
    g0: LineSegment StartX=19 StartY=38 StartZ=0 EndX=117 EndY=38 EndZ=0
    g1: ArcOfCircle CenterX=19 CenterY=19 CenterZ=0 NormalX=0 NormalY=0 NormalZ=1 AngleXU=0 Radius=19 StartAngle=1.5708 EndAngle=3.14159
    g2: LineSegment StartX=117 StartY=38 StartZ=0 EndX=117 EndY=19 EndZ=0
    g3: LineSegment StartX=98 StartY=1.0161e-12 StartZ=0 EndX=5.22862e-06 EndY=1.0161e-12 EndZ=0
    g4: LineSegment StartX=5.22862e-06 StartY=19 StartZ=0 EndX=5.22862e-06 EndY=1.0161e-12 EndZ=0
    g5: ArcOfCircle CenterX=98 CenterY=19 CenterZ=0 NormalX=0 NormalY=0 NormalZ=1 AngleXU=0 Radius=19 StartAngle=4.71239 EndAngle=6.28319
  constraints (16):
    c: Horizontal(g0)
    c: Distance(g0) = 98
    c: Coincident(g1,g0)
    c: Block(g1)
    c: Coincident(g2,g0)
    c: Vertical(g2)
    c: Distance(g2) = 19
    c: Horizontal(g3)
    c: Coincident(g4,g1)
    c: Vertical(g4)
    c: Coincident(g3,g4)
    c: Block(g3)
    c: Coincident(g5,g2)
    c: Coincident(g5,g3)
    c: Block(g0)
    c: Block(g5)
FEATURE [Part::Extrusion] Extrude070  label="sideA004"
  Base = -> Sketch080
  Dir = (0,0,1)
  DirMode = 2
  FaceMakerClass = Part::FaceMakerBullseye
  LengthFwd = 3
  LengthRev = 0
  Placement = pos=(0,0,-2.7) rot=(0,0,1;0rad)
  Solid = true
  Symmetric = false
FEATURE [Sketcher::SketchObject] Sketch081
  FullyConstrained = true
  Placement = pos=(117,19,0) rot=(0.57735,0.57735,0.57735;2.0944rad)
  sketch-geometry (8):
    g0: LineSegment StartX=-49.19 StartY=63.5 StartZ=0 EndX=-49.19 EndY=60.5 EndZ=0
    g1: LineSegment StartX=-49.19 StartY=11.5 StartZ=0 EndX=-49.19 EndY=8.5 EndZ=0
    g2: ArcOfCircle CenterX=-1.5 CenterY=62 CenterZ=0 NormalX=0 NormalY=0 NormalZ=1 AngleXU=0 Radius=1.5 StartAngle=4.71239 EndAngle=7.85398
    g3: ArcOfCircle CenterX=-1.5 CenterY=10 CenterZ=0 NormalX=0 NormalY=0 NormalZ=1 AngleXU=0 Radius=1.5 StartAngle=4.71239 EndAngle=7.85398
    g4: LineSegment StartX=-49.19 StartY=63.5 StartZ=0 EndX=-1.5 EndY=63.5 EndZ=0
    g5: LineSegment StartX=-49.19 StartY=60.5 StartZ=0 EndX=-1.5 EndY=60.5 EndZ=0
    g6: LineSegment StartX=-49.19 StartY=11.5 StartZ=0 EndX=-1.5 EndY=11.5 EndZ=0
    g7: LineSegment StartX=-49.19 StartY=8.5 StartZ=0 EndX=-1.5 EndY=8.5 EndZ=0
  constraints (19):
    c: Vertical(g0)
    c: Distance(g0) = 3
    c: Vertical(g1)
    c: Block(g1)
    c: Block(g2)
    c: Block(g3)
    c: Block(g0)
    c: Coincident(g4,g0)
    c: Coincident(g4,g2)
    c: Horizontal(g4)
    c: Coincident(g5,g0)
    c: Coincident(g5,g2)
    c: Horizontal(g5)
    c: Coincident(g6,g1)
    c: Coincident(g6,g3)
    c: Horizontal(g6)
    c: Coincident(g7,g1)
    c: Coincident(g7,g3)
    c: Horizontal(g7)
FEATURE [Part::Extrusion] Extrude071  label="sideB004"
  Base = -> Sketch079
  Dir = (0,0,1)
  DirMode = 2
  FaceMakerClass = Part::FaceMakerBullseye
  LengthFwd = 3
  LengthRev = 0
  Placement = pos=(0,0,71.7) rot=(0,0,1;0rad)
  Solid = true
  Symmetric = false
FEATURE [Part::MultiFuse] Fusion152  label="removeFromBottom004"
  Placement = pos=(2,0,0) rot=(0,0,1;0rad)
  Shapes = -> [Extrude070,Extrude071]
FEATURE [Part::Extrusion] Extrude072
  Base = -> Sketch081
  Dir = (1,0,0)
  DirMode = 2
  FaceMakerClass = Part::FaceMakerBullseye
  LengthFwd = 10
  LengthRev = 0
  Solid = true
  Symmetric = false
FEATURE [Part::Fillet] Fillet059  label="removeFromtMoreFrontCaseScrewRetainers004"
  Base = -> Extrude072
  Edges = 4 edges r=1.49: [Edge6,Edge11,Edge18,Edge23]
  Placement = pos=(-12,0,0) rot=(0,0,1;0rad)
FEATURE [Sketcher::SketchObject] Sketch082
  FullyConstrained = true
  Placement = pos=(117,19,0) rot=(0.57735,0.57735,0.57735;2.0944rad)
  sketch-geometry (8):
    g0: LineSegment StartX=-49.19 StartY=69.25 StartZ=0 EndX=-49.19 EndY=66.25 EndZ=0
    g1: LineSegment StartX=-49.19 StartY=5.75 StartZ=0 EndX=-49.19 EndY=2.75 EndZ=0
    g2: ArcOfCircle CenterX=-1.5 CenterY=67.75 CenterZ=0 NormalX=0 NormalY=0 NormalZ=1 AngleXU=0 Radius=1.5 StartAngle=4.71239 EndAngle=7.85398
    g3: ArcOfCircle CenterX=-1.5 CenterY=4.25 CenterZ=0 NormalX=0 NormalY=0 NormalZ=1 AngleXU=0 Radius=1.5 StartAngle=4.71239 EndAngle=7.85398
    g4: LineSegment StartX=-49.19 StartY=69.25 StartZ=0 EndX=-1.5 EndY=69.25 EndZ=0
    g5: LineSegment StartX=-49.19 StartY=66.25 StartZ=0 EndX=-1.5 EndY=66.25 EndZ=0
    g6: LineSegment StartX=-49.19 StartY=5.75 StartZ=0 EndX=-1.5 EndY=5.75 EndZ=0
    g7: LineSegment StartX=-49.19 StartY=2.75 StartZ=0 EndX=-1.5 EndY=2.75 EndZ=0
  constraints (19):
    c: Vertical(g0)
    c: Distance(g0) = 3
    c: Block(g0)
    c: Vertical(g1)
    c: Block(g2)
    c: Block(g3)
    c: Block(g1)
    c: Coincident(g4,g0)
    c: Coincident(g4,g2)
    c: Horizontal(g4)
    c: Coincident(g5,g0)
    c: Coincident(g5,g2)
    c: Horizontal(g5)
    c: Coincident(g6,g1)
    c: Coincident(g6,g3)
    c: Horizontal(g6)
    c: Coincident(g7,g1)
    c: Coincident(g7,g3)
    c: Horizontal(g7)
FEATURE [Part::Extrusion] Extrude073
  Base = -> Sketch082
  Dir = (1,0,0)
  DirMode = 2
  FaceMakerClass = Part::FaceMakerBullseye
  LengthFwd = 10
  LengthRev = 0
  Solid = true
  Symmetric = false
FEATURE [Part::Fillet] Fillet060  label="removeFromtMoreFrontCaseScrewRetainers005"
  Base = -> Extrude073
  Edges = 4 edges r=1.49: [Edge6,Edge11,Edge18,Edge23]
  Placement = pos=(-4,0,0) rot=(0,0,1;0rad)
FEATURE [Part::Revolution] Revolve163  label="backCaseScrewRetainer004"
  Angle = 360
  Axis = (0,1,0)
  Base = (0,0,0)
  FaceMakerClass = Part::FaceMakerBullseye
  Placement = pos=(12.5,3,62) rot=(0,0,1;0rad)
  Solid = false
  Source = -> Face149
  Symmetric = false
FEATURE [Part::Revolution] Revolve164  label="frontCaseScrewRetainer006"
  Angle = 360
  Axis = (0,1,0)
  Base = (0,0,0)
  FaceMakerClass = Part::FaceMakerBullseye
  Placement = pos=(89.5,3,68.5) rot=(0,0,1;0rad)
  Solid = false
  Source = -> Face151
  Symmetric = false
FEATURE [Part::Revolution] Revolve165  label="frontCaseScrewRetainer007"
  Angle = 360
  Axis = (0,1,0)
  Base = (0,0,0)
  FaceMakerClass = Part::FaceMakerBullseye
  Placement = pos=(89.5,3,3.5) rot=(0,0,1;0rad)
  Solid = false
  Source = -> Face152
  Symmetric = false
FEATURE [Part::Revolution] Revolve166  label="backCaseScrewRetainer005"
  Angle = 360
  Axis = (0,1,0)
  Base = (0,0,0)
  FaceMakerClass = Part::FaceMakerBullseye
  Placement = pos=(12.5,3,10) rot=(0,0,1;0rad)
  Solid = false
  Source = -> Face150
  Symmetric = false
FEATURE [Part::Revolution] Revolve167  label="moreFrontCaseScrewRetainer006"
  Angle = 360
  Axis = (0,1,0)
  Base = (0,0,0)
  FaceMakerClass = Part::FaceMakerBullseye
  Placement = pos=(109.5,4.5,68.5) rot=(0,0,1;0rad)
  Solid = false
  Source = -> Face153
  Symmetric = false
FEATURE [Part::Revolution] Revolve168  label="moreFrontCaseScrewRetainer007"
  Angle = 360
  Axis = (0,1,0)
  Base = (0,0,0)
  FaceMakerClass = Part::FaceMakerBullseye
  Placement = pos=(109.5,4.5,3.5) rot=(0,0,1;0rad)
  Solid = false
  Source = -> Face154
  Symmetric = false
FEATURE [Part::MultiFuse] Fusion151  label="screwRetainers003"
  Shapes = -> [Revolve168,Revolve167,Revolve166,Revolve165,Revolve164,Revolve163]
FEATURE [Part::Cut] Cut069  label="screwRetainers004"
  Base = -> Fusion151
  Tool = -> Fusion152
FEATURE [Part::Cut] Cut070
  Base = -> Cut069
  Tool = -> Fillet060
FEATURE [Part::Cut] Cut071  label="screwPillars001"
  Base = -> Cut070
  Tool = -> Fillet059
FEATURE [Part::MultiFuse] Fusion153  label="bottom024"
  Shapes = -> [Fusion149,Cut071]
FEATURE [Part::Cylinder] Cylinder067
  Angle = 360
  AttacherType = Attacher::AttachEngine3D
  Height = 10
  Placement = pos=(20.65,12,4.68) rot=(1,0,0;1.5708rad)
  Radius = 2
FEATURE [Part::Cylinder] Cylinder068
  Angle = 360
  AttacherType = Attacher::AttachEngine3D
  Height = 10
  Placement = pos=(20.65,12,67.38) rot=(1,0,0;1.5708rad)
  Radius = 2
FEATURE [Part::Cylinder] Cylinder069
  Angle = 360
  AttacherType = Attacher::AttachEngine3D
  Height = 10
  Placement = pos=(77.15,12,67.38) rot=(1,0,0;1.5708rad)
  Radius = 2
FEATURE [Part::Cylinder] Cylinder070
  Angle = 360
  AttacherType = Attacher::AttachEngine3D
  Height = 10
  Placement = pos=(77.15,12,4.68) rot=(1,0,0;1.5708rad)
  Radius = 2
FEATURE [Part::MultiFuse] Fusion154  label="removeFromThreadedInsertHousing001"
  Shapes = -> [Cylinder069,Cylinder068,Cylinder067,Cylinder070]
FEATURE [Part::Cut] Cut072  label="bottom025"
  Base = -> Fusion153
  Tool = -> Fusion154
FEATURE [Image::ImagePlane] ImagePlane
  XSize = 339
  YSize = 72
FEATURE [Sketcher::SketchObject] Sketch083
  FullyConstrained = true
  MapMode = 5
  Support = -> [XY_Plane]
  sketch-geometry (338):
    g0: LineSegment StartX=-151.619 StartY=28.8932 StartZ=0 EndX=-140.819 EndY=28.8932 EndZ=0
    g1: LineSegment StartX=-151.619 StartY=24.0313 StartZ=0 EndX=-151.619 EndY=28.8932 EndZ=0
    g2: LineSegment StartX=-140.819 StartY=17.7713 StartZ=0 EndX=-151.619 EndY=17.7713 EndZ=0
    g3: LineSegment StartX=-151.619 StartY=17.7713 StartZ=0 EndX=-151.619 EndY=22.6313 EndZ=0
    g4: LineSegment StartX=-151.619 StartY=22.6313 StartZ=0 EndX=-145.128 EndY=22.6313 EndZ=0
    g5: LineSegment StartX=-145.128 StartY=24.0313 StartZ=0 EndX=-140.819 EndY=28.8932 EndZ=0
    g6: LineSegment StartX=-145.128 StartY=22.6313 StartZ=0 EndX=-140.819 EndY=17.7713 EndZ=0
    g7: ArcOfCircle CenterX=-155.157 CenterY=23.3323 CenterZ=0 NormalX=0 NormalY=0 NormalZ=1 AngleXU=0 Radius=6.92354 StartAngle=1.03434 EndAngle=5.24885
    g8: ArcOfCircle CenterX=-155.157 CenterY=23.3323 CenterZ=0 NormalX=0 NormalY=0 NormalZ=1 AngleXU=0 Radius=12.6269 StartAngle=1.28675 EndAngle=4.99643
    g9: LineSegment StartX=-151.619 StartY=35.4532 StartZ=0 EndX=-151.619 EndY=29.2832 EndZ=0
    g10: LineSegment StartX=-151.619 StartY=17.3813 StartZ=0 EndX=-151.619 EndY=11.2113 EndZ=0
    g11-g21: Circle x11 (B-spline internal-alignment scaffolding for g22; pole/knot coordinates omitted)
    g22: BSplineCurve PolesCount=11 KnotsCount=9 Degree=3 IsPeriodic=0
    g23-g31: GeomPoint x9 (B-spline internal-alignment scaffolding for g22; pole/knot coordinates omitted)
    g32-g49: Circle x18 (B-spline internal-alignment scaffolding for g50; pole/knot coordinates omitted)
    g50: BSplineCurve PolesCount=18 KnotsCount=16 Degree=3 IsPeriodic=0
    g51-g66: GeomPoint x16 (B-spline internal-alignment scaffolding for g50; pole/knot coordinates omitted)
    g67: LineSegment StartX=-117.124 StartY=30.093 StartZ=0 EndX=-117.603 EndY=26.5272 EndZ=0
    g68: LineSegment StartX=-117.603 StartY=17.8472 StartZ=0 EndX=-117.124 EndY=14.2659 EndZ=0
    g69: Ellipse CenterX=-109.671 CenterY=20.025 CenterZ=0 NormalX=0 NormalY=0 NormalZ=1 MajorRadius=3.34798 MinorRadius=2.71052 AngleXU=-1.56793
    g70: GeomPoint X=-109.666 Y=18.0598 Z=0
    g71: GeomPoint X=-109.677 Y=21.9902 Z=0
    g72: Ellipse CenterX=-109.671 CenterY=20.0123 CenterZ=0 NormalX=0 NormalY=0 NormalZ=1 MajorRadius=6.93002 MinorRadius=6.36273 AngleXU=-3.13976
    g73: GeomPoint X=-112.417 Y=20.0073 Z=0
    g74: GeomPoint X=-106.925 Y=20.0173 Z=0
    g75: Ellipse CenterX=-51.7682 CenterY=20.1463 CenterZ=0 NormalX=0 NormalY=0 NormalZ=1 MajorRadius=3.19279 MinorRadius=2.71052 AngleXU=-1.52774
    g76: GeomPoint X=-51.6955 Y=18.4606 Z=0
    g77: GeomPoint X=-51.8408 Y=21.832 Z=0
    g78: GeomPoint X=-54.5142 Y=20.1413 Z=0
    g79: GeomPoint X=-49.0221 Y=20.1513 Z=0
    g80: Ellipse CenterX=-51.7682 CenterY=20.1463 CenterZ=0 NormalX=0 NormalY=0 NormalZ=1 MajorRadius=6.93002 MinorRadius=6.36273 AngleXU=-3.13976
    g81: Ellipse CenterX=-22.8436 CenterY=20.1783 CenterZ=0 NormalX=0 NormalY=0 NormalZ=1 MajorRadius=3.31512 MinorRadius=2.71052 AngleXU=-1.60214
    g82: GeomPoint X=-22.9034 Y=18.2706 Z=0
    g83: GeomPoint X=-22.7838 Y=22.0861 Z=0
    g84: GeomPoint X=-25.5897 Y=20.1733 Z=0
    g85: GeomPoint X=-20.0976 Y=20.1833 Z=0
    g86: Ellipse CenterX=-22.8436 CenterY=20.1783 CenterZ=0 NormalX=0 NormalY=0 NormalZ=1 MajorRadius=6.93002 MinorRadius=6.36273 AngleXU=-3.13976
    g87: LineSegment StartX=-101.889 StartY=14.1107 StartZ=0 EndX=-97.7455 EndY=14.1107 EndZ=0
    g88: LineSegment StartX=-93.8155 StartY=14.1107 StartZ=0 EndX=-89.6755 EndY=14.1107 EndZ=0
    g89: LineSegment StartX=-85.7455 StartY=14.1107 StartZ=0 EndX=-81.6055 EndY=14.1107 EndZ=0
    g90: LineSegment StartX=-101.889 StartY=14.1107 StartZ=0 EndX=-101.889 EndY=25.9907 EndZ=0
    g91: LineSegment StartX=-101.889 StartY=25.9907 StartZ=0 EndX=-97.8594 EndY=25.9907 EndZ=0
    g92: LineSegment StartX=-97.8594 StartY=25.9907 StartZ=0 EndX=-97.8594 EndY=24.0907 EndZ=0
    g93: LineSegment StartX=-97.7455 StartY=14.1107 StartZ=0 EndX=-97.7455 EndY=19.9107 EndZ=0
    g94: LineSegment StartX=-89.6755 StartY=14.1107 StartZ=0 EndX=-89.6755 EndY=19.9107 EndZ=0
    g95: LineSegment StartX=-93.8155 StartY=14.1107 StartZ=0 EndX=-93.8155 EndY=21.0107 EndZ=0
    g96-g106: Circle x11 (B-spline internal-alignment scaffolding for g107; pole/knot coordinates omitted)
    g107: BSplineCurve PolesCount=11 KnotsCount=9 Degree=3 IsPeriodic=0
    g108-g116: GeomPoint x9 (B-spline internal-alignment scaffolding for g107; pole/knot coordinates omitted)
    g117: BSplineCurve PolesCount=11 KnotsCount=9 Degree=3 IsPeriodic=0
    g118-g125: Circle x8 (B-spline internal-alignment scaffolding for g126; pole/knot coordinates omitted)
    g126: BSplineCurve PolesCount=8 KnotsCount=6 Degree=3 IsPeriodic=0
    g127-g132: GeomPoint x6 (B-spline internal-alignment scaffolding for g126; pole/knot coordinates omitted)
    g133: BSplineCurve PolesCount=8 KnotsCount=6 Degree=3 IsPeriodic=0
    g134: LineSegment StartX=-85.7455 StartY=21.0107 StartZ=0 EndX=-85.7455 EndY=14.1107 EndZ=0
    g135: LineSegment StartX=-80.0879 StartY=14.1107 StartZ=0 EndX=-75.944 EndY=14.1107 EndZ=0
    g136: LineSegment StartX=-72.014 StartY=14.1107 StartZ=0 EndX=-67.874 EndY=14.1107 EndZ=0
    g137: LineSegment StartX=-63.944 StartY=14.1107 StartZ=0 EndX=-59.804 EndY=14.1107 EndZ=0
    g138: LineSegment StartX=-80.0879 StartY=14.1107 StartZ=0 EndX=-80.0879 EndY=25.9907 EndZ=0
    g139: LineSegment StartX=-80.0879 StartY=25.9907 StartZ=0 EndX=-76.0579 EndY=25.9907 EndZ=0
    g140: LineSegment StartX=-76.0579 StartY=25.9907 StartZ=0 EndX=-76.0579 EndY=24.0907 EndZ=0
    g141: LineSegment StartX=-75.944 StartY=14.1107 StartZ=0 EndX=-75.944 EndY=19.9107 EndZ=0
    g142: LineSegment StartX=-67.874 StartY=14.1107 StartZ=0 EndX=-67.874 EndY=19.9107 EndZ=0
    g143: LineSegment StartX=-72.014 StartY=14.1107 StartZ=0 EndX=-72.014 EndY=21.0107 EndZ=0
    g144-g148: Circle x5 (B-spline internal-alignment scaffolding for g149; pole/knot coordinates omitted)
    g149: BSplineCurve PolesCount=11 KnotsCount=9 Degree=3 IsPeriodic=0
    g150-g158: GeomPoint x9 (B-spline internal-alignment scaffolding for g149; pole/knot coordinates omitted)
    g159: BSplineCurve PolesCount=11 KnotsCount=9 Degree=3 IsPeriodic=0
    g160-g167: Circle x8 (B-spline internal-alignment scaffolding for g168; pole/knot coordinates omitted)
    g168: BSplineCurve PolesCount=8 KnotsCount=6 Degree=3 IsPeriodic=0
    g169-g174: GeomPoint x6 (B-spline internal-alignment scaffolding for g168; pole/knot coordinates omitted)
    g175: BSplineCurve PolesCount=8 KnotsCount=6 Degree=3 IsPeriodic=0
    g176: LineSegment StartX=-63.944 StartY=21.0107 StartZ=0 EndX=-63.944 EndY=14.1107 EndZ=0
    g177: LineSegment StartX=-59.804 StartY=14.1107 StartZ=0 EndX=-59.804 EndY=21.5868 EndZ=0
    g178: BSplineCurve PolesCount=4 KnotsCount=2 Degree=3 IsPeriodic=0
    g179: GeomPoint X=-59.804 Y=21.5868 Z=0
    g180: GeomPoint X=-60.2379 Y=24.0907 Z=0
    g181: LineSegment StartX=-81.6055 StartY=14.1107 StartZ=0 EndX=-81.6055 EndY=21.5868 EndZ=0
    g182: LineSegment StartX=-151.619 StartY=24.0313 StartZ=0 EndX=-145.128 EndY=24.0313 EndZ=0
    g183: Circle CenterX=-82.0394 CenterY=24.0907 CenterZ=0 NormalX=0 NormalY=0 NormalZ=1 AngleXU=0 Radius=1
    g184: Circle CenterX=-81.7131 CenterY=23.2736 CenterZ=0 NormalX=0 NormalY=0 NormalZ=1 AngleXU=0 Radius=1
    g185: Circle CenterX=-81.6055 CenterY=21.5868 CenterZ=0 NormalX=0 NormalY=0 NormalZ=1 AngleXU=0 Radius=1
    g186: BSplineCurve PolesCount=3 KnotsCount=2 Degree=2 IsPeriodic=0
    g187: GeomPoint X=-82.0394 Y=24.0907 Z=0
    g188: GeomPoint X=-81.6055 Y=21.5868 Z=0
    g189: Ellipse CenterX=-37.3522 CenterY=19.9515 CenterZ=0 NormalX=0 NormalY=0 NormalZ=1 MajorRadius=2.99755 MinorRadius=2.49 AngleXU=1.5708
    g190: GeomPoint X=-37.3522 Y=21.6203 Z=0
    g191: GeomPoint X=-37.3522 Y=18.2826 Z=0
    g192: ArcOfEllipse CenterX=-38.7647 CenterY=20.06 CenterZ=0 NormalX=0 NormalY=0 NormalZ=1 MajorRadius=6.30025 MinorRadius=5.3849 AngleXU=1.57276 StartAngle=5.50632 EndAngle=10.3035
    g193: GeomPoint X=-38.7711 Y=23.3304 Z=0
    g194: GeomPoint X=-38.7583 Y=16.7895 Z=0
    g195: LineSegment StartX=-34.6109 StartY=14.1107 StartZ=0 EndX=-30.8984 EndY=14.1107 EndZ=0
    g196: LineSegment StartX=-30.8984 StartY=14.1107 StartZ=0 EndX=-30.8984 EndY=31.1784 EndZ=0
    g197: LineSegment StartX=-30.8984 StartY=31.1784 StartZ=0 EndX=-34.9984 EndY=31.1784 EndZ=0
    g198: LineSegment StartX=-34.9984 StartY=24.5602 StartZ=0 EndX=-34.9984 EndY=31.1784 EndZ=0
    g199: LineSegment StartX=-34.6109 StartY=16.0476 StartZ=0 EndX=-34.6109 EndY=14.1107 EndZ=0
    g200: LineSegment StartX=-14.8781 StartY=14.1107 StartZ=0 EndX=-10.5106 EndY=14.1107 EndZ=0
    g201: LineSegment StartX=-14.8781 StartY=14.1107 StartZ=0 EndX=-14.8781 EndY=25.8504 EndZ=0
    g202: LineSegment StartX=-14.8781 StartY=25.8504 StartZ=0 EndX=-10.8534 EndY=25.8504 EndZ=0
    g203: LineSegment StartX=-10.8534 StartY=25.8504 StartZ=0 EndX=-10.8534 EndY=24.0923 EndZ=0
    g204: LineSegment StartX=-10.5106 StartY=14.1107 StartZ=0 EndX=-10.5106 EndY=19.7752 EndZ=0
    g205: LineSegment StartX=-5.96397 StartY=25.9304 StartZ=0 EndX=-5.96397 EndY=22.574 EndZ=0
    g206-g214: Circle x9 (B-spline internal-alignment scaffolding for g215; pole/knot coordinates omitted)
    g215: BSplineCurve PolesCount=9 KnotsCount=7 Degree=3 IsPeriodic=0
    g216-g222: GeomPoint x7 (B-spline internal-alignment scaffolding for g215; pole/knot coordinates omitted)
    g223-g232: Circle x10 (B-spline internal-alignment scaffolding for g233; pole/knot coordinates omitted)
    g233: BSplineCurve PolesCount=10 KnotsCount=8 Degree=3 IsPeriodic=0
    g234-g241: GeomPoint x8 (B-spline internal-alignment scaffolding for g233; pole/knot coordinates omitted)
    g242: LineSegment StartX=-1.58923 StartY=21.0696 StartZ=0 EndX=2.62034 EndY=21.0696 EndZ=0
    g243: LineSegment StartX=-1.55856 StartY=18.7342 StartZ=0 EndX=6.45946 EndY=18.7342 EndZ=0
    g244: LineSegment StartX=5.29231 StartY=17.386 StartZ=0 EndX=5.29231 EndY=14.3674 EndZ=0
    g245-g269: Circle x25 (B-spline internal-alignment scaffolding for g270; pole/knot coordinates omitted)
    g270: BSplineCurve PolesCount=25 KnotsCount=23 Degree=3 IsPeriodic=0
    g271-g293: GeomPoint x23 (B-spline internal-alignment scaffolding for g270; pole/knot coordinates omitted)
    g294-g304: Circle x11 (B-spline internal-alignment scaffolding for g305; pole/knot coordinates omitted)
    g305: BSplineCurve PolesCount=11 KnotsCount=9 Degree=3 IsPeriodic=0
    g306-g314: GeomPoint x9 (B-spline internal-alignment scaffolding for g305; pole/knot coordinates omitted)
    g315-g326: Circle x12 (B-spline internal-alignment scaffolding for g327; pole/knot coordinates omitted)
    g327: BSplineCurve PolesCount=12 KnotsCount=10 Degree=3 IsPeriodic=0
    g328-g337: GeomPoint x10 (B-spline internal-alignment scaffolding for g327; pole/knot coordinates omitted)
  constraints (252):
    c: Coincident(g1,g0)
    c: Horizontal(g0)
    c: Vertical(g1)
    c: Coincident(g2,g3)
    c: Coincident(g3,g4)
    c: Horizontal(g4)
    c: Horizontal(g2)
    c: Vertical(g3)
    c: Block(g1)
    c: Distance(g3) = 4.86
    c: Block(g4)
    c: Distance(g0) = 10.8
    c: Distance(g2) = 10.8
    c: Coincident(g5,g0)
    c: Coincident(g6,g4)
    c: Coincident(g6,g2)
    c: Block(g8)
    c: Block(g7)
    c: Coincident(g9,g8)
    c: Coincident(g9,g7)
    c: Vertical(g9)
    c: Coincident(g10,g7)
    c: Coincident(g10,g8)
    c: Vertical(g10)
    c: Weight(g11) = 1
    c: Equal(g11, g12-g21) x10
    c: InternalAlignment(g11-g21 -> g22) x11
    c: InternalAlignment(g23-g31 -> g22) x9
    c: Block(g22)
    c: Weight(g32) = 1
    c: Equal(g32, g33-g49) x17
    c: InternalAlignment(g32-g49 -> g50) x18
    c: InternalAlignment(g51-g66 -> g50) x16
    c: Block(g50)
    c: Coincident(g67,g50)
    c: Coincident(g67,g22)
    c: Coincident(g68,g22)
    c: Coincident(g68,g50)
    c: InternalAlignment(g70,g69)
    c: InternalAlignment(g71,g69)
    c: Block(g69)
    c: InternalAlignment(g73,g72)
    c: InternalAlignment(g74,g72)
    c: Block(g72)
    c: InternalAlignment(g76,g75)
    c: InternalAlignment(g77,g75)
    c: InternalAlignment(g78,g80)
    c: InternalAlignment(g79,g80)
    c: Block(g80)
    c: Coincident(g75,g80)
    c: Block(g75)
    c: InternalAlignment(g82,g81)
    c: InternalAlignment(g83,g81)
    c: InternalAlignment(g84,g86)
    c: InternalAlignment(g85,g86)
    c: Block(g86)
    c: Coincident(g81,g86)
    c: Block(g81)
    c: Horizontal(g87)
    c: Block(g87)
    c: Horizontal(g88)
    c: Distance(g88) = 4.14
    c: Horizontal(g89)
    c: Equal(g88,g89) = 4.14
    c: Block(g89)
    c: Block(g88)
    c: Coincident(g90,g87)
    c: Vertical(g90)
    c: Distance(g90) = 11.88
    c: Coincident(g91,g90)
    c: Horizontal(g91)
    c: Coincident(g92,g91)
    c: Vertical(g92)
    c: Distance(g91) = 4.03
    c: Distance(g92) = 1.9
    c: Coincident(g93,g87)
    c: Vertical(g93)
    c: Vertical(g94)
    c: Coincident(g94,g88)
    c: Distance(g93) = 5.8
    c: Distance(g94) = 5.8
    c: Vertical(g95)
    c: Coincident(g95,g88)
    c: Distance(g95) = 6.9
    c: Coincident(g107,g92)
    c: Weight(g96) = 1
    c: Equal(g96, g97-g106) x10
    c: InternalAlignment(g96-g106 -> g107) x11
    c: InternalAlignment(g108-g116 -> g107) x9
    c: Block(g107)
    c: Block(g117)
    c: Coincident(g126,g93)
    c: Weight(g118) = 1
    c: Equal(g118, g119-g125) x7
    c: Coincident(g126,g95)
    c: InternalAlignment(g118-g125 -> g126) x8
    c: InternalAlignment(g127-g132 -> g126) x6
    c: Coincident(g133,g94)
    c: Block(g126)
    c: Block(g133)
    c: Coincident(g134,g133)
    c: Coincident(g134,g89)
    c: Vertical(g134)
    c: Horizontal(g135)
    c: Block(g135)
    c: Horizontal(g136)
    c: Equal(g88,g136) = 4.14
    c: Horizontal(g137)
    c: Equal(g136,g137) = 4.14
    c: Block(g137)
    c: Block(g136)
    c: Coincident(g138,g135)
    c: Vertical(g138)
    c: Equal(g90,g138) = 11.88
    c: Coincident(g139,g138)
    c: Horizontal(g139)
    c: Coincident(g140,g139)
    c: Vertical(g140)
    c: Equal(g91,g139) = 4.03
    c: Equal(g92,g140) = 1.9
    c: Coincident(g141,g135)
    c: Vertical(g141)
    c: Vertical(g142)
    c: Coincident(g142,g136)
    c: Equal(g93,g141) = 5.8
    c: Equal(g94,g142) = 5.8
    c: Vertical(g143)
    c: Coincident(g143,g136)
    c: Equal(g95,g143) = 6.9
    c: Coincident(g149,g140)
    c: Equal(g96,g144) = 1
    c: Equal(g144, g145-g148) x4
    c: InternalAlignment(g144-g148 -> g149) x5
    c: InternalAlignment(g150-g158 -> g149) x9
    c: Block(g149)
    c: Block(g159)
    c: Coincident(g168,g141)
    c: Equal(g118,g160) = 1
    c: Equal(g160, g161-g167) x7
    c: Coincident(g168,g143)
    c: InternalAlignment(g160-g167 -> g168) x8
    c: InternalAlignment(g169-g174 -> g168) x6
    c: Coincident(g175,g142)
    c: Block(g168)
    c: Block(g175)
    c: Coincident(g176,g175)
    c: Coincident(g176,g137)
    c: Vertical(g176)
    c: Coincident(g177,g137)
    c: Vertical(g177)
    c: Coincident(g178,g177)
    c: Coincident(g178,g159)
    c: InternalAlignment(g179,g178)
    c: InternalAlignment(g180,g178)
    c: Block(g178)
    c: Vertical(g181)
    c: Coincident(g181,g89)
    c: Block(g5)
    c: Coincident(g182,g1)
    c: Coincident(g182,g5)
    c: Horizontal(g182)
    c: Coincident(g186,g117)
    c: Weight(g183) = 1
    c: Equal(g183,g184)
    c: Equal(g183,g185)
    c: Coincident(g186,g181)
    c: InternalAlignment(g183,g186)
    c: InternalAlignment(g184,g186)
    c: InternalAlignment(g185,g186)
    c: InternalAlignment(g187,g186)
    c: InternalAlignment(g188,g186)
    c: Block(g186)
    c: InternalAlignment(g190,g189)
    c: InternalAlignment(g191,g189)
    c: Block(g189)
    c: InternalAlignment(g193,g192)
    c: InternalAlignment(g194,g192)
    c: Block(g192)
    c: Horizontal(g195)
    c: Block(g195)
    c: Coincident(g196,g195)
    c: Vertical(g196)
    c: Block(g196)
    c: Distance(g195) = 3.71244
    c: Coincident(g197,g196)
    c: Horizontal(g197)
    c: Distance(g197) = 4.1
    c: Coincident(g198,g192)
    c: Coincident(g198,g197)
    c: Vertical(g198)
    c: Block(g198)
    c: Coincident(g199,g192)
    c: Coincident(g199,g195)
    c: Vertical(g199)
    c: Block(g199)
    c: Horizontal(g200)
    c: Block(g200)
    c: Coincident(g201,g200)
    c: Vertical(g201)
    c: Block(g201)
    c: Coincident(g202,g201)
    c: Horizontal(g202)
    c: Block(g202)
    c: Coincident(g203,g202)
    c: Vertical(g203)
    c: Block(g203)
    c: Coincident(g204,g200)
    c: Vertical(g204)
    c: Block(g204)
    c: Coincident(g215,g203)
    c: Weight(g206) = 1
    c: Equal(g206, g207-g214) x8
    c: Coincident(g215,g205)
    c: InternalAlignment(g206-g214 -> g215) x9
    c: InternalAlignment(g216-g222 -> g215) x7
    c: Coincident(g233,g204)
    c: Weight(g223) = 1
    c: Equal(g223, g224-g232) x9
    c: Coincident(g233,g205)
    c: InternalAlignment(g223-g232 -> g233) x10
    c: InternalAlignment(g234-g241 -> g233) x8
    c: Vertical(g205)
    c: Block(g205)
    c: Block(g215)
    c: Block(g233)
    c: Horizontal(g242)
    c: Horizontal(g243)
    c: Block(g242)
    c: Block(g243)
    c: Vertical(g244)
    c: Block(g244)
    c: Coincident(g270,g243)
    c: Weight(g245) = 1
    c: Equal(g245, g246-g269) x24
    c: Coincident(g270,g244)
    c: InternalAlignment(g245-g269 -> g270) x25
    c: InternalAlignment(g271-g293 -> g270) x23
    c: Coincident(g305,g242)
    c: Weight(g294) = 1
    c: Equal(g294, g295-g304) x10
    c: Coincident(g305,g242)
    c: InternalAlignment(g294-g304 -> g305) x11
    c: InternalAlignment(g306-g314 -> g305) x9
    c: Block(g305)
    c: Coincident(g327,g243)
    c: Weight(g315) = 1
    c: Equal(g315, g316-g326) x11
    c: Coincident(g327,g244)
    c: InternalAlignment(g315-g326 -> g327) x12
    c: InternalAlignment(g328-g337 -> g327) x10
    c: Block(g327)
    c: Block(g270)
FEATURE [PartDesign::Body] Body  label="CommodoreLogoAndText"
  Group = -> [Sketch083]
  Origin = -> Origin
FEATURE [Part::Extrusion] Extrude074  label="CommodoreLogoAndText001"
  Base = -> Sketch083
  Dir = (0,0,1)
  DirMode = 2
  FaceMakerClass = Part::FaceMakerBullseye
  LengthFwd = 10
  LengthRev = 0
  Solid = true
  Symmetric = false
FEATURE [Part::FeaturePython] Clone  label="CommodoreLogoAndTextScale"  # Draft clone (typed FeaturePython)
  AttacherType = Attacher::AttachEngine3D
  Fuse = false
  Objects = -> [Extrude074]
  Placement = pos=(111,5.37,-11.6) rot=(0,0,1;0rad)
  Scale = (0.62,0.62,1)
